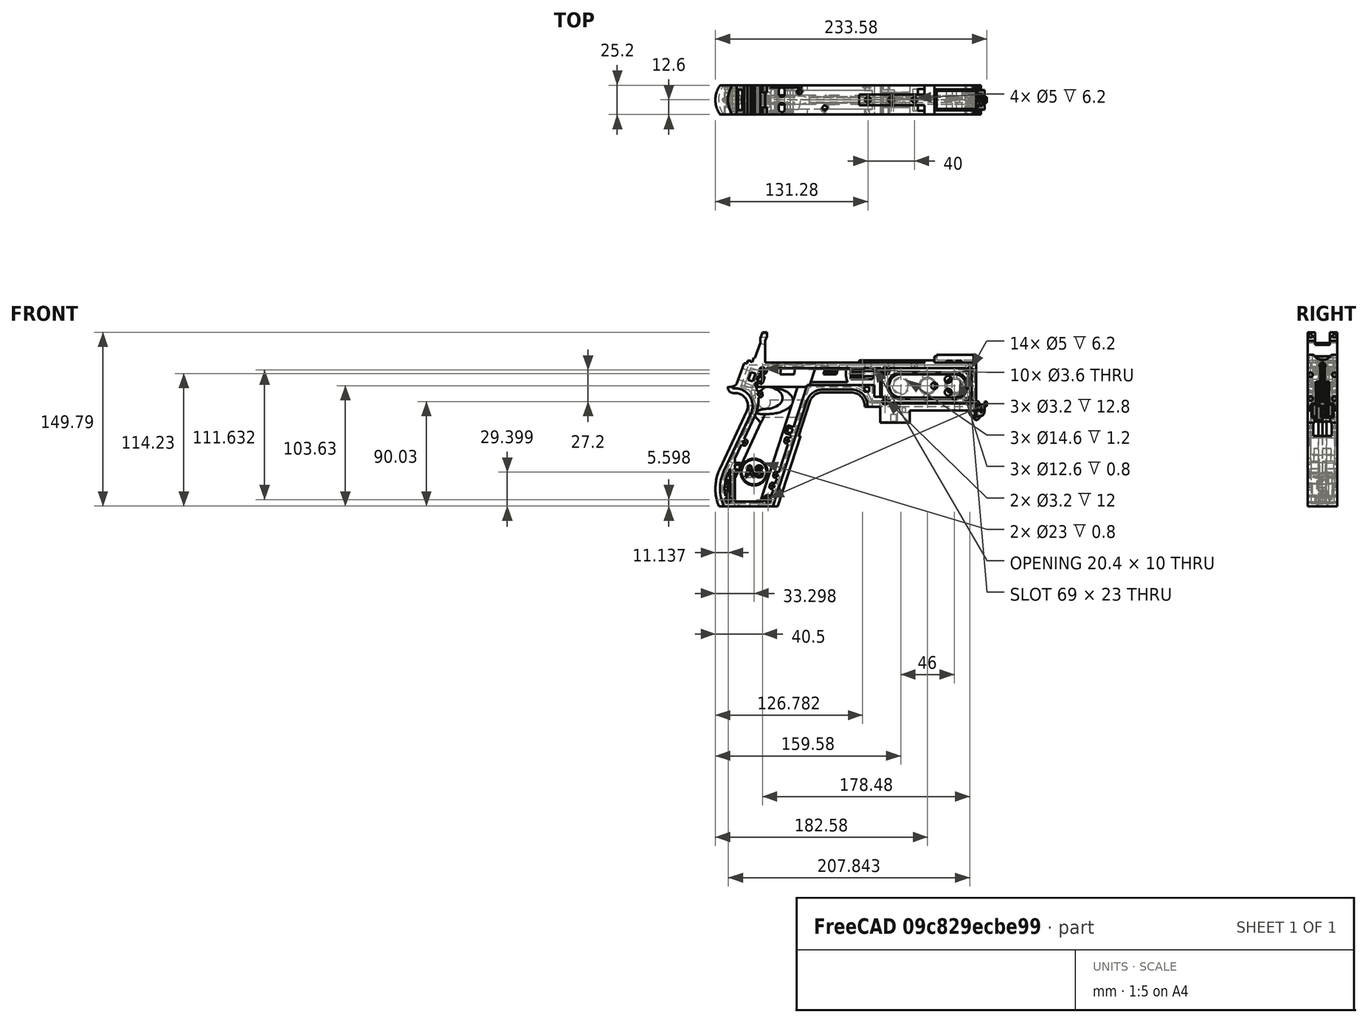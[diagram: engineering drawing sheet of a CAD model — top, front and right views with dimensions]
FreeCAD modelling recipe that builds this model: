
FCSTD DOCUMENT  (FreeCAD 1.0R39319 (Git))
Label: PICON-OF_ver_53_BIS
License: All rights reserved
LicenseURL: https://en.wikipedia.org/wiki/All_rights_reserved
objects: Sketcher::SketchObject×124, Part::Extrusion×63, Part::Cut×48, PartDesign::Pad×29, PartDesign::Pocket×21, PartDesign::Chamfer×15, PartDesign::Body×10, PartDesign::Fillet×6, Part::MultiFuse×5, Part::Part2DObjectPython×4, PartDesign::SubtractivePipe×4, PartDesign::SubtractiveLoft×4, PartDesign::Plane×3, PartDesign::SubShapeBinder×2, Part::Sweep×1, PartDesign::ShapeBinder×1, Mesh::Feature×1, PartDesign::Point×1, PartDesign::Groove×1
note: 626 computed .brp shape members not serialized (recipe doc carries the construction recipe); baked Part::Feature solids carry a one-line shape summary decoded from their .brp

FEATURE [Sketcher::SketchObject] Sketch  label="corpo principale"
  ArcFitTolerance = 1e-06
  AttacherType = Attacher::AttachEngine3D
  AttachmentSupport = -> [XZ_Plane]
  FullyConstrained = true
  MakeInternals = false
  MapMode = 5
  Placement = pos=(0,0,0) rot=(1,0,0;1.5708rad)
  sketch-geometry (65):
    g0: LineSegment StartX=0 StartY=0 StartZ=0 EndX=-57.2 EndY=0 EndZ=0
    g1: LineSegment StartX=-57.2 StartY=0 StartZ=0 EndX=-57.2 EndY=-10.4 EndZ=0
    g2: LineSegment StartX=-57.2 StartY=-10.4 StartZ=0 EndX=-82.8 EndY=-10.4 EndZ=0
    g3: LineSegment StartX=-82.8 StartY=-10.4 StartZ=0 EndX=-82.8 EndY=3.2 EndZ=0
    g4: LineSegment StartX=-82.8 StartY=3.2 StartZ=0 EndX=-93.6 EndY=3.2 EndZ=0
    g5: LineSegment StartX=-93.6 StartY=3.2 StartZ=0 EndX=-93.6 EndY=4 EndZ=0
    g6: LineSegment StartX=-107.6 StartY=18 StartZ=0 EndX=-132.428 EndY=18 EndZ=0
    g7: LineSegment StartX=-145.743 StartY=8.32624 StartZ=0 EndX=-175.232 EndY=-82.4316 EndZ=0
    g8: LineSegment StartX=-175.232 StartY=-82.4316 StartZ=0 EndX=-217.232 EndY=-82.4316 EndZ=0
    g9: LineSegment StartX=-217.232 StartY=-52.1862 StartZ=0 EndX=-193.988 EndY=-2.33927 EndZ=0
    g10: LineSegment StartX=-206.196 StartY=23.0857 StartZ=0 EndX=-199.861 EndY=40.4914 EndZ=0
    g11: LineSegment StartX=-199.861 StartY=40.4914 StartZ=0 EndX=-197.061 EndY=40.4914 EndZ=0
    g12: LineSegment StartX=-197.061 StartY=40.4914 StartZ=0 EndX=-197.061 EndY=42.8914 EndZ=0
    g13: LineSegment StartX=-197.061 StartY=42.8914 StartZ=0 EndX=-194.261 EndY=42.8914 EndZ=0
    g14: LineSegment StartX=-194.261 StartY=42.8914 StartZ=0 EndX=-194.535 EndY=42.1397 EndZ=0
    g15: LineSegment StartX=-194.535 StartY=42.1397 StartZ=0 EndX=-193.031 EndY=41.5924 EndZ=0
    g16: LineSegment StartX=-193.031 StartY=41.5924 StartZ=0 EndX=-191.663 EndY=45.3512 EndZ=0
    g17: LineSegment StartX=-191.663 StartY=45.3512 StartZ=0 EndX=-190.536 EndY=44.9408 EndZ=0
    g18: LineSegment StartX=-190.536 StartY=44.9408 StartZ=0 EndX=-185.747 EndY=58.0965 EndZ=0
    g19: LineSegment StartX=-185.747 StartY=58.0965 StartZ=0 EndX=-185.747 EndY=62.0965 EndZ=0
    g20: LineSegment StartX=-185.747 StartY=62.0965 StartZ=0 EndX=-183.832 EndY=67.3588 EndZ=0
    g21: LineSegment StartX=-183.832 StartY=67.3588 StartZ=0 EndX=-180.232 EndY=67.3588 EndZ=0
    g22: LineSegment StartX=-180.232 StartY=67.3588 StartZ=0 EndX=-180.232 EndY=63.7588 EndZ=0
    g23: LineSegment StartX=-180.232 StartY=63.7588 StartZ=0 EndX=-181.6 EndY=60 EndZ=0
    g24: LineSegment StartX=-181.6 StartY=60 StartZ=0 EndX=-181.6 EndY=41.2 EndZ=0
    g25: LineSegment StartX=-181.6 StartY=41.2 StartZ=0 EndX=-100.8 EndY=41.2 EndZ=0
    g26: LineSegment StartX=-36 StartY=43.2 StartZ=0 EndX=-36 EndY=41.2 EndZ=0
    g27: LineSegment StartX=0 StartY=48 StartZ=0 EndX=0 EndY=0 EndZ=0
    g28: LineSegment StartX=-209.901 StartY=19.85 StartZ=0 EndX=-209.901 EndY=20.1 EndZ=0
    g29: LineSegment StartX=-208.001 StartY=22 StartZ=0 EndX=-207.747 EndY=22 EndZ=0
    g30: LineSegment StartX=-207.583 StartY=19 StartZ=0 EndX=-209.051 EndY=19 EndZ=0
    g31: ArcOfCircle CenterX=-208.001 CenterY=20.1 CenterZ=0 NormalX=0 NormalY=0 NormalZ=1 AngleXU=0 Radius=1.9 StartAngle=1.5708 EndAngle=3.14159
    g32: GeomPoint [constr] X=-209.901 Y=22 Z=0
    g33: ArcOfCircle CenterX=-209.051 CenterY=19.85 CenterZ=0 NormalX=0 NormalY=0 NormalZ=1 AngleXU=0 Radius=0.85 StartAngle=3.14159 EndAngle=4.71239
    g34: GeomPoint [constr] X=-209.901 Y=19 Z=0
    g35: ArcOfCircle CenterX=-207.747 CenterY=23.65 CenterZ=0 NormalX=0 NormalY=0 NormalZ=1 AngleXU=0 Radius=1.65 StartAngle=4.71239 EndAngle=5.93412
    g36: GeomPoint [constr] X=-206.591 Y=22 Z=0
    g37: LineSegment StartX=-4 StartY=6 StartZ=0 EndX=-4 EndY=36.4 EndZ=0
    g38: LineSegment StartX=-4 StartY=36.4 StartZ=0 EndX=-185.2 EndY=36.4 EndZ=0
    g39: LineSegment StartX=-185.2 StartY=36.4 StartZ=0 EndX=-190.441 EndY=22 EndZ=0
    g40: LineSegment StartX=-214.575 StartY=-78.4316 StartZ=0 EndX=-178.142 EndY=-78.4316 EndZ=0
    g41: LineSegment StartX=-178.142 StartY=-78.4316 StartZ=0 EndX=-145.51 EndY=22 EndZ=0
    g42: LineSegment StartX=-145.51 StartY=22 StartZ=0 EndX=-87.91 EndY=22 EndZ=0
    g43: LineSegment StartX=-87.91 StartY=22 StartZ=0 EndX=-87.91 EndY=11.6 EndZ=0
    g44: LineSegment StartX=-87.91 StartY=11.6 StartZ=0 EndX=-80.11 EndY=11.6 EndZ=0
    g45: LineSegment StartX=-80.11 StartY=11.6 StartZ=0 EndX=-80.11 EndY=6 EndZ=0
    g46: LineSegment StartX=-80.11 StartY=6 StartZ=0 EndX=-4 EndY=6 EndZ=0
    g47: LineSegment StartX=-190.363 StartY=-4.02975 StartZ=0 EndX=-213.607 EndY=-53.8767 EndZ=0
    g48: ArcOfCircle CenterX=-132.428 CenterY=4 CenterZ=0 NormalX=0 NormalY=0 NormalZ=1 AngleXU=0 Radius=14 StartAngle=1.5708 EndAngle=2.82743
    g49: GeomPoint [constr] X=-142.6 Y=18 Z=0
    g50: ArcOfCircle CenterX=-107.6 CenterY=4 CenterZ=0 NormalX=0 NormalY=0 NormalZ=1 AngleXU=0 Radius=14 StartAngle=0 EndAngle=1.5708
    g51: GeomPoint [constr] X=-93.6 Y=18 Z=0
    g52: ArcOfCircle CenterX=-184.801 CenterY=-67.3089 CenterZ=0 NormalX=0 NormalY=0 NormalZ=1 AngleXU=0 Radius=35.7833 StartAngle=2.70526 EndAngle=3.57792
    g53: ArcOfCircle CenterX=-207.583 CenterY=4 CenterZ=0 NormalX=0 NormalY=0 NormalZ=1 AngleXU=0 Radius=15 StartAngle=5.84685 EndAngle=7.85398
    g54: LineSegment [constr] StartX=-213.607 StartY=-53.8767 StartZ=0 EndX=-217.232 EndY=-52.1862 EndZ=0
    g55: ArcOfCircle CenterX=-184.801 CenterY=-67.3089 CenterZ=0 NormalX=0 NormalY=0 NormalZ=1 AngleXU=0 Radius=31.7833 StartAngle=2.70526 EndAngle=3.49911
    g56: ArcOfCircle CenterX=-218.095 CenterY=8.90192 CenterZ=0 NormalX=0 NormalY=0 NormalZ=1 AngleXU=0 Radius=30.5989 StartAngle=5.84685 EndAngle=6.72553
    g57: LineSegment StartX=-44.6 StartY=43.2 StartZ=0 EndX=-36 EndY=43.2 EndZ=0
    g58: LineSegment StartX=-100.8 StartY=41.2 StartZ=0 EndX=-44.6 EndY=41.2 EndZ=0
    g59: LineSegment StartX=-44.6 StartY=41.2 StartZ=0 EndX=-44.6 EndY=43.2 EndZ=0
    g60: LineSegment StartX=-2.4 StartY=48 StartZ=0 EndX=0 EndY=48 EndZ=0
    g61: LineSegment StartX=-36 StartY=41.2 StartZ=0 EndX=-2.4 EndY=41.2 EndZ=0
    g62: LineSegment StartX=-2.4 StartY=41.2 StartZ=0 EndX=-2.4 EndY=48 EndZ=0
    g63: LineSegment [constr] StartX=-181.6 StartY=36.4 StartZ=0 EndX=-152.209 EndY=36.4 EndZ=0
    g64: LineSegment [constr] StartX=-181.6 StartY=36.4 StartZ=0 EndX=-130.41 EndY=36.4 EndZ=0
  constraints (183):
    c: Coincident(g-1,g0)
    c: PointOnObject(g0,g-1)
    c: Coincident(g0,g1)
    c: Vertical(g1)
    c: Coincident(g1,g2)
    c: Horizontal(g2)
    c: Coincident(g2,g3)
    c: Vertical(g3)
    c: Coincident(g3,g4)
    c: Coincident(g4,g5)
    c: Vertical(g5)
    c: Horizontal(g6)
    c: Coincident(g7,g8)
    c: Horizontal(g8)
    c: Coincident(g10,g11)
    c: Horizontal(g11)
    c: Coincident(g11,g12)
    c: Vertical(g12)
    c: Coincident(g12,g13)
    c: Horizontal(g13)
    c: Coincident(g13,g14)
    c: Coincident(g14,g15)
    c: Coincident(g15,g16)
    c: Coincident(g16,g17)
    c: Coincident(g17,g18)
    c: Coincident(g18,g19)
    c: Vertical(g19)
    c: Coincident(g19,g20)
    c: Coincident(g20,g21)
    c: Horizontal(g21)
    c: Coincident(g21,g22)
    c: Vertical(g22)
    c: Coincident(g22,g23)
    c: Coincident(g23,g24)
    c: Vertical(g24)
    c: Coincident(g24,g25)
    c: Horizontal(g25)
    c: Coincident(g57,g26)
    c: Vertical(g26)
    c: Coincident(g26,g61)
    c: PointOnObject(g60,g-2)
    c: Coincident(g60,g27)
    c: Coincident(g27,g0)
    c: DistanceY(g27,g27) = 48
    c: DistanceY(g1,g1) = 10.4
    c: DistanceX(g0,g0) = 57.2
    c: DistanceX(g2,g2) = 25.6
    c: Horizontal(g4)
    c: DistanceY(g3,g3) = 13.6
    c: DistanceX(g4,g4) = 10.8
    c: DistanceY(g5,g51) = 14.8
    c: DistanceX(g49,g51) = 49
    c: Distance(g7,g49) = 105.6
    c: DistanceX(g61,g60) = 36
    c: DistanceX(g25,g25) = 80.8
    c: DistanceY(g24,g24) = 18.8
    c: DistanceY(g22,g22) = 3.6
    c: Distance(g23) = 4
    c: Angle(g-1,g23) = 1.22173
    c: DistanceX(g21,g21) = 3.6
    c: Distance(g20) = 5.6
    c: Angle(g-1,g20) = 1.22173
    c: DistanceY(g19,g19) = 4
    c: Distance(g18) = 14
    c: Angle(g-1,g18) = 1.22173
    c: Distance(g17) = 1.2
    c: Distance(g16) = 4
    c: Angle(g16) = 1.22173
    c: Perpendicular(g18,g17)
    c: Distance(g15) = 1.6
    c: Perpendicular(g16,g15)
    c: Distance(g14) = 0.8
    c: DistanceX(g13,g13) = 2.8
    c: Perpendicular(g15,g14)
    c: DistanceY(g12,g12) = 2.4
    c: DistanceX(g11,g11) = 2.8
    c: Distance(g9) = 55
    c: Angle(g9,g-1) = 2.00713
    c: Horizontal(g29)
    c: Vertical(g28)
    c: Horizontal(g30)
    c: PointOnObject(g32,g29)
    c: PointOnObject(g32,g28)
    c: Tangent(g29,g31) = 1.5708
    c: Tangent(g28,g31) = 1.5708
    c: PointOnObject(g34,g28)
    c: PointOnObject(g34,g30)
    c: Tangent(g28,g33) = 1.5708
    c: Tangent(g30,g33) = 1.5708
    c: PointOnObject(g36,g29)
    c: PointOnObject(g36,g10)
    c: Tangent(g29,g35) = -1.5708
    c: Tangent(g10,g35) = -1.5708
    c: Angle(g-1,g10) = 1.22173
    c: Radius(g35) = 1.65
    c: Vertical(g37)
    c: Coincident(g37,g38)
    c: Horizontal(g38)
    c: Coincident(g38,g39)
    c: Horizontal(g40)
    c: Coincident(g40,g41)
    c: Coincident(g41,g42)
    c: Horizontal(g42)
    c: Coincident(g42,g43)
    c: Vertical(g43)
    c: Coincident(g43,g44)
    c: Horizontal(g44)
    c: Coincident(g44,g45)
    c: Vertical(g45)
    c: Coincident(g45,g46)
    c: Coincident(g46,g37)
    c: Horizontal(g46)
    c: DistanceY(g0,g37) = 6
    c: DistanceX(g37,g0) = 4
    c: DistanceY(g37,g25) = 4.8
    c: DistanceX(g38,g38) = 181.2
    c: DistanceX(g42,g42) = 57.6
    c: DistanceY(g49,g41) = 4
    c: DistanceX(g41,g49) = 2.91
    c: DistanceY(g43,g43) = 10.4
    c: DistanceX(g44,g44) = 7.8
    c: DistanceY(g7,g40) = 4
    c: Distance(g47) = 55
    c: Angle(g-1,g39) = 1.22173
    c: PointOnObject(g49,g7)
    c: PointOnObject(g49,g6)
    c: Tangent(g7,g48) = -1.5708
    c: Tangent(g6,g48) = -1.5708
    c: PointOnObject(g51,g5)
    c: PointOnObject(g51,g6)
    c: Tangent(g5,g50) = -1.5708
    c: Tangent(g6,g50) = -1.5708
    c: Radius(g50) = 14
    c: Radius(g48) = 14
    c: DistanceX(g8,g8) = 42
    c: Angle(g7,g-1) = 1.88496
    c: Parallel(g41,g7)
    c: Parallel(g47,g9)
    c: Coincident(g52,g8)
    c: Tangent(g52,g9) = 1.5708
    c: DistanceX(g9,g8) = 0
    c: Tangent(g53,g9) = -1.5708
    c: Tangent(g53,g30) = -1.5708
    c: Diameter(g53) = 30
    c: DistanceY(g53,g0) = -4
    c: Coincident(g54,g47)
    c: Distance(g54) = 4
    c: Coincident(g54,g9)
    c: Coincident(g55,g40)
    c: Tangent(g55,g47) = -1.5708
    c: Coincident(g52,g55)
    c: Coincident(g56,g39)
    c: Tangent(g56,g47) = 1.5708
    c: Horizontal(g57)
    c: DistanceX(g57,g57) = 8.6
    c: Coincident(g58,g25)
    c: Horizontal(g58)
    c: Coincident(g59,g58)
    c: Vertical(g59)
    c: DistanceY(g58,g57) = 2
    c: DistanceX(g58,g58) = 56.2
    c: Coincident(g59,g57)
    c: DistanceY(g41,g36) = 0
    c: DistanceY(g36,g39) = 0
    c: DistanceY(g28,g28) = 0.25
    c: DistanceX(g30,g36) = 2.46
    c: DistanceX(g28,g29) = 1.9
    c: Coincident(g62,g60)
    c: Horizontal(g60)
    c: DistanceX(g62,g27) = 2.4
    c: Coincident(g61,g62)
    c: DistanceY(g26,g26) = 2
    c: Vertical(g62)
    c: DistanceY(g61,g60) = 6.8
    c: Horizontal(g61)
    c: Distance(g63) = 29.391
    c: PointOnObject(g63,g38)
    c: PointOnObject(g63,g38)
    c: Distance(g64) = 51.19
    c: PointOnObject(g64,g38)
    c: PointOnObject(g64,g38)
    c: DistanceX(g24,g63) = 0
    c: DistanceX(g24,g64) = 0
FEATURE [Part::Extrusion] Extrude  label="Extrude corpo principale"
  Base = -> Sketch
  Dir = (0,-1,2e-16)
  DirMode = 2
  FaceMakerClass = Part::FaceMakerBullseye
  FaceMakerMode = 3
  LengthFwd = 25.2
  LengthRev = 12.6
  Solid = true
  Symmetric = true
FEATURE [Sketcher::SketchObject] Sketch002  label="scavo grilletto"
  ArcFitTolerance = 1e-06
  AttachmentSupport = -> [XZ_Plane]
  ExternalGeometry = -> [Sketch]
  FullyConstrained = true
  MakeInternals = false
  MapMode = 5
  Placement = pos=(0,0,0) rot=(1,0,0;1.5708rad)
  sketch-geometry (4):
    g0: LineSegment StartX=-89.51 StartY=22 StartZ=0 EndX=-152.71 EndY=22 EndZ=0
    g1: LineSegment StartX=-152.71 StartY=22 StartZ=0 EndX=-167.006 EndY=-22 EndZ=0
    g2: LineSegment StartX=-167.006 StartY=-22 StartZ=0 EndX=-89.51 EndY=-22 EndZ=0
    g3: LineSegment StartX=-89.51 StartY=-22 StartZ=0 EndX=-89.51 EndY=22 EndZ=0
  constraints (12):
    c: Horizontal(g0)
    c: Coincident(g0,g1)
    c: Coincident(g1,g2)
    c: Horizontal(g2)
    c: Coincident(g2,g3)
    c: Coincident(g3,g0)
    c: Vertical(g3)
    c: Angle(g1,g0) = 1.88496
    c: DistanceY(g3,g3) = 44
    c: DistanceX(g0,g0) = 63.2
    c: DistanceX(g0,g-3) = 1.6
    c: DistanceY(g-3,g0) = 0
FEATURE [Sketcher::SketchObject] Sketch004  label="traiettoria arrotondamento impugnatura anteriore"
  ArcFitTolerance = 1e-06
  AttachmentSupport = -> [XZ_Plane]
  ExternalGeometry = -> [Sketch]
  FullyConstrained = true
  MakeInternals = false
  MapMode = 5
  Placement = pos=(0,0,0) rot=(1,0,0;1.5708rad)
  sketch-geometry (13):
    g0: LineSegment StartX=-175.232 StartY=-82.4316 StartZ=0 EndX=-145.743 EndY=8.32624 EndZ=0
    g1: LineSegment StartX=-93.6 StartY=3.2 StartZ=0 EndX=-93.6 EndY=4 EndZ=0
    g2: LineSegment StartX=-132.428 StartY=18 StartZ=0 EndX=-107.6 EndY=18 EndZ=0
    g3: ArcOfCircle CenterX=-132.428 CenterY=4 CenterZ=0 NormalX=0 NormalY=0 NormalZ=1 AngleXU=0 Radius=14 StartAngle=1.5708 EndAngle=2.82743
    g4: ArcOfCircle CenterX=-107.6 CenterY=4 CenterZ=0 NormalX=0 NormalY=0 NormalZ=1 AngleXU=0 Radius=14 StartAngle=0 EndAngle=1.5708
    g5: LineSegment StartX=-175.232 StartY=-82.4316 StartZ=0 EndX=-217.232 EndY=-82.4316 EndZ=0
    g6: LineSegment StartX=-217.232 StartY=-52.1862 StartZ=0 EndX=-193.988 EndY=-2.33927 EndZ=0
    g7: LineSegment StartX=-209.051 StartY=19 StartZ=0 EndX=-207.583 EndY=19 EndZ=0
    g8: LineSegment StartX=-209.901 StartY=20.1 StartZ=0 EndX=-209.901 EndY=19.85 EndZ=0
    g9: ArcOfCircle CenterX=-184.801 CenterY=-67.3089 CenterZ=0 NormalX=0 NormalY=0 NormalZ=1 AngleXU=0 Radius=35.7833 StartAngle=2.70526 EndAngle=3.57792
    g10: ArcOfCircle CenterX=-207.583 CenterY=4 CenterZ=0 NormalX=0 NormalY=0 NormalZ=1 AngleXU=0 Radius=15 StartAngle=5.84685 EndAngle=7.85398
    g11: ArcOfCircle CenterX=-209.051 CenterY=19.85 CenterZ=0 NormalX=0 NormalY=0 NormalZ=1 AngleXU=0 Radius=0.85 StartAngle=3.14159 EndAngle=4.71239
    g12: ArcOfCircle CenterX=-208.001 CenterY=20.1 CenterZ=0 NormalX=0 NormalY=0 NormalZ=1 AngleXU=0 Radius=1.9 StartAngle=1.5708 EndAngle=3.14159
  constraints (26):
    c: Coincident(g0,g-3)
    c: Coincident(g0,g-6)
    c: Coincident(g1,g-8)
    c: Coincident(g1,g-7)
    c: Coincident(g2,g-5)
    c: Coincident(g2,g-4)
    c: Coincident(g3,g2)
    c: Tangent(g3,g0) = 1.5708
    c: Coincident(g4,g1)
    c: Tangent(g4,g2) = 1.5708
    c: Coincident(g5,g0)
    c: Coincident(g5,g-9)
    c: Coincident(g6,g-12)
    c: Coincident(g6,g-11)
    c: Coincident(g7,g-15)
    c: Coincident(g7,g-14)
    c: Coincident(g8,g-16)
    c: Coincident(g8,g-17)
    c: Tangent(g9,g6) = 1.5708
    c: Coincident(g9,g5)
    c: Coincident(g10,g7)
    c: Tangent(g10,g6) = -1.5708
    c: Tangent(g11,g7) = -1.5708
    c: Coincident(g11,g8)
    c: Tangent(g12,g8) = -1.5708
    c: Coincident(g12,g-17)
FEATURE [PartDesign::Plane] DatumPlane  label="Piano per disegno arrotondamento impugnatura"
  AttachmentSupport = -> [Sketch]
  Length = 73.6581
  MapMode = 7
  Placement = pos=(-145.743,1.8e-15,8.32624) rot=(0.154555,0.154555,0.97582;1.59527rad)
  ResizeMode = 0
  Width = 303.511
FEATURE [Sketcher::SketchObject] Sketch005  label="forma arrotondamento impugnatura anteriore"
  ArcFitTolerance = 1e-06
  AttachmentSupport = -> [DatumPlane]
  FullyConstrained = true
  MakeInternals = false
  MapMode = 5
  Placement = pos=(-145.743,1.8e-15,8.32624) rot=(0.154555,0.154555,0.97582;1.59527rad)
  sketch-geometry (5):
    g0: GeomPoint [constr] X=0 Y=-4 Z=0
    g1: GeomPoint [constr] X=-12.6 Y=7.1e-15 Z=0
    g2: GeomPoint [constr] X=12.6 Y=4.97e-14 Z=0
    g3: LineSegment StartX=-12.6 StartY=7.1e-15 StartZ=0 EndX=12.6 EndY=4.97e-14 EndZ=0
    g4: ArcOfCircle CenterX=-3.88e-14 CenterY=17.845 CenterZ=0 NormalX=0 NormalY=0 NormalZ=1 AngleXU=0 Radius=21.845 StartAngle=4.09759 EndAngle=5.32718
  constraints (11):
    c: DistanceY(g0,g-1) = 4
    c: DistanceX(g-1,g0) = 0
    c: DistanceX(g1,g-1) = 12.6
    c: DistanceX(g-1,g2) = 12.6
    c: DistanceY(g-1,g2) = 0
    c: DistanceY(g-1,g1) = 0
    c: Coincident(g3,g1)
    c: Coincident(g3,g2)
    c: Coincident(g4,g1)
    c: Coincident(g4,g2)
    c: PointOnObject(g0,g4)
FEATURE [Part::Sweep] Sweep  label="Sweep impugnatura"
  Frenet = true
  Sections = -> [Sketch005]
  Solid = true
  Spine = -> Sketch [Edge32,Edge33,Edge34,Edge35,Edge36,Edge37,Edge38,Edge39,Edge40,Edge41,Edge42,Edge43,Edge44]
  Transition = 1
FEATURE [Sketcher::SketchObject] Sketch008  label="buchi e pulizie varie"
  ArcFitTolerance = 1e-06
  AttachmentSupport = -> [XZ_Plane]
  ExternalGeometry = -> [Sketch]
  FullyConstrained = true
  MakeInternals = false
  MapMode = 5
  Placement = pos=(0,0,0) rot=(1,0,0;1.5708rad)
  sketch-geometry (26):
    g0: LineSegment StartX=-96.278 StartY=20.155 StartZ=0 EndX=-92.278 EndY=20.155 EndZ=0
    g1: LineSegment StartX=-92.278 StartY=20.155 StartZ=0 EndX=-92.278 EndY=16.155 EndZ=0
    g2: LineSegment StartX=-92.278 StartY=16.155 StartZ=0 EndX=-96.278 EndY=16.155 EndZ=0
    g3: LineSegment StartX=-96.278 StartY=16.155 StartZ=0 EndX=-96.278 EndY=20.155 EndZ=0
    g4: LineSegment StartX=-222.232 StartY=-82.4316 StartZ=0 EndX=-170.232 EndY=-82.4316 EndZ=0
    g5: LineSegment StartX=-170.232 StartY=-82.4316 StartZ=0 EndX=-170.232 EndY=-86.4316 EndZ=0
    g6: LineSegment StartX=-170.232 StartY=-86.4316 StartZ=0 EndX=-222.232 EndY=-86.4316 EndZ=0
    g7: LineSegment StartX=-222.232 StartY=-86.4316 StartZ=0 EndX=-222.232 EndY=-82.4316 EndZ=0
    g8: LineSegment StartX=-213.901 StartY=20.1 StartZ=0 EndX=-213.901 EndY=26 EndZ=0
    g9: LineSegment StartX=-213.901 StartY=26 StartZ=0 EndX=-206.196 EndY=26 EndZ=0
    g10: LineSegment StartX=-17.4 StartY=42.8 StartZ=0 EndX=-12.4 EndY=42.8 EndZ=0
    g11: LineSegment StartX=-12.4 StartY=42.8 StartZ=0 EndX=-12.4 EndY=41.2 EndZ=0
    g12: LineSegment StartX=-12.4 StartY=41.2 StartZ=0 EndX=-17.4 EndY=41.2 EndZ=0
    g13: LineSegment StartX=-17.4 StartY=41.2 StartZ=0 EndX=-17.4 EndY=42.8 EndZ=0
    g14: LineSegment StartX=-25.9 StartY=42.8 StartZ=0 EndX=-20.9 EndY=42.8 EndZ=0
    g15: LineSegment StartX=-20.9 StartY=42.8 StartZ=0 EndX=-20.9 EndY=41.2 EndZ=0
    g16: LineSegment StartX=-20.9 StartY=41.2 StartZ=0 EndX=-25.9 EndY=41.2 EndZ=0
    g17: LineSegment StartX=-25.9 StartY=41.2 StartZ=0 EndX=-25.9 EndY=42.8 EndZ=0
    g18: GeomPoint [constr] X=-206.196 Y=23.0857 Z=0
    g19: GeomPoint [constr] X=-213.901 Y=20.1 Z=0
    g20: BSplineCurve PolesCount=4 KnotsCount=2 Degree=3 IsPeriodic=0
    g21-g24: Circle [constr] x4 (B-spline internal-alignment scaffolding for g20; pole/knot coordinates omitted)
    g25: LineSegment StartX=-206.196 StartY=26 StartZ=0 EndX=-206.196 EndY=23.0857 EndZ=0
  constraints (73):
    c: Horizontal(g0)
    c: Coincident(g1,g0)
    c: Vertical(g1)
    c: Coincident(g2,g1)
    c: Horizontal(g2)
    c: Coincident(g3,g2)
    c: Coincident(g3,g0)
    c: Vertical(g3)
    c: DistanceX(g0,g-4) = 4.368
    c: DistanceY(g0,g-4) = 1.845
    c: DistanceY(g1,g1) = 4
    c: DistanceX(g2,g2) = 4
    c: Horizontal(g4)
    c: Coincident(g5,g4)
    c: Vertical(g5)
    c: Coincident(g6,g5)
    c: Horizontal(g6)
    c: Coincident(g7,g6)
    c: Coincident(g7,g4)
    c: Vertical(g7)
    c: DistanceY(g7,g7) = 4
    c: DistanceX(g4,g-5) = 5
    c: DistanceX(g-5,g4) = 5
    c: DistanceY(g4,g-5) = 0
    c: Coincident(g9,g8)
    c: Parallel(g9,g-6)
    c: DistanceX(g8,g-8) = 4
    c: Horizontal(g10)
    c: Coincident(g11,g10)
    c: Vertical(g11)
    c: Coincident(g12,g11)
    c: Horizontal(g12)
    c: Coincident(g13,g12)
    c: Coincident(g13,g10)
    c: Vertical(g13)
    c: Horizontal(g14)
    c: Coincident(g15,g14)
    c: Vertical(g15)
    c: Coincident(g16,g15)
    c: Horizontal(g16)
    c: Coincident(g17,g16)
    c: Coincident(g17,g14)
    c: Vertical(g17)
    c: DistanceY(g11,g10) = 1.6
    c: DistanceX(g10,g10) = 5
    c: DistanceY(g15,g14) = 1.6
    c: DistanceX(g14,g14) = 5
    c: DistanceX(g15,g12) = 3.5
    c: DistanceX(g11,g-9) = 10
    c: DistanceY(g-9,g11) = 0
    c: DistanceY(g-9,g15) = 0
    c: Perpendicular(g8,g9)
    c: DistanceY(g-7,g9) = 4
    c: DistanceY(g8,g-8) = 0
    c: InternalAlignment(g18,g20)
    c: InternalAlignment(g19,g20)
    c: InternalAlignment(g21,g20)
    c: Weight(g21) = 1
    c: InternalAlignment(g22,g20)
    c: Equal(g22,g21)
    c: InternalAlignment(g23,g20)
    c: Equal(g23,g21)
    c: InternalAlignment(g24,g20)
    c: Equal(g24,g21)
    c: Coincident(g18,g-12)
    c: Coincident(g19,g8)
    c: Coincident(g25,g9)
    c: Coincident(g25,g20)
    c: Vertical(g25)
    c: DistanceY(g20,g23) = 0
    c: DistanceY(g22,g18) = 2.26
    c: DistanceX(g22,g18) = 0.93
    c: DistanceX(g20,g23) = 2.9
FEATURE [Part::Extrusion] Extrude004  label="Extrude Buchi e pulizie varie"
  Base = -> Sketch008
  Dir = (0,-1,2e-16)
  DirMode = 2
  FaceMakerClass = Part::FaceMakerBullseye
  FaceMakerMode = 3
  LengthFwd = 25.2
  LengthRev = 0
  Solid = true
  Symmetric = true
FEATURE [Sketcher::SketchObject] Sketch009  label="rinforzi"
  ArcFitTolerance = 1e-06
  AttachmentSupport = -> [XZ_Plane]
  ExternalGeometry = -> [Sketch]
  FullyConstrained = true
  MakeInternals = false
  MapMode = 5
  Placement = pos=(0,0,0) rot=(1,0,0;1.5708rad)
  sketch-geometry (9):
    g0: LineSegment StartX=-87.91 StartY=22 StartZ=0 EndX=-87.91 EndY=36.4 EndZ=0
    g1: LineSegment StartX=-87.91 StartY=36.4 StartZ=0 EndX=-97.91 EndY=36.4 EndZ=0
    g2: LineSegment StartX=-97.91 StartY=36.4 StartZ=0 EndX=-97.91 EndY=22 EndZ=0
    g3: LineSegment StartX=-97.91 StartY=22 StartZ=0 EndX=-87.91 EndY=22 EndZ=0
    g4: LineSegment StartX=-149.713 StartY=9.06563 StartZ=0 EndX=-154.586 EndY=-5.93437 EndZ=0
    g5: LineSegment StartX=-154.586 StartY=-5.93437 StartZ=0 EndX=-191.863 EndY=-5.93437 EndZ=0
    g6: LineSegment StartX=-191.863 StartY=-5.93437 StartZ=0 EndX=-191.863 EndY=9.06563 EndZ=0
    g7: LineSegment StartX=-191.863 StartY=9.06563 StartZ=0 EndX=-149.713 EndY=9.06563 EndZ=0
    g8: LineSegment [constr] StartX=-145.51 StartY=22 StartZ=0 EndX=-149.713 EndY=9.06563 EndZ=0
  constraints (25):
    c: Vertical(g0)
    c: Coincident(g1,g0)
    c: Horizontal(g1)
    c: Coincident(g2,g1)
    c: Vertical(g2)
    c: Coincident(g3,g2)
    c: Coincident(g3,g0)
    c: Horizontal(g3)
    c: Coincident(g0,g-4)
    c: DistanceX(g3,g3) = 10
    c: DistanceY(g0,g-3) = 0
    c: Coincident(g5,g4)
    c: Horizontal(g5)
    c: Coincident(g6,g5)
    c: Vertical(g6)
    c: Coincident(g7,g6)
    c: Coincident(g7,g4)
    c: Horizontal(g7)
    c: Distance(g8) = 13.6
    c: Parallel(g-6,g8)
    c: Coincident(g-6,g8)
    c: Parallel(g4,g-6)
    c: DistanceY(g4,g4) = 15
    c: Coincident(g4,g8)
    c: DistanceX(g-5,g5) = -1.5
FEATURE [Part::Extrusion] Extrude001  label="Extrude scavo grilletto"
  Base = -> Sketch002
  Dir = (0,-1,2e-16)
  DirMode = 2
  FaceMakerClass = Part::FaceMakerBullseye
  FaceMakerMode = 3
  LengthFwd = 16
  LengthRev = 0
  Solid = true
  Symmetric = true
FEATURE [Part::Extrusion] Extrude005  label="Extrude Rinforzi"
  Base = -> Sketch009
  Dir = (0,-1,2e-16)
  DirMode = 2
  FaceMakerClass = Part::FaceMakerBullseye
  FaceMakerMode = 3
  LengthFwd = 2
  LengthRev = 0
  Placement = pos=(0,12.6,0) rot=(0,0,1;0rad)
  Solid = true
  Symmetric = false
FEATURE [PartDesign::ShapeBinder] CopyCut
  TraceSupport = false
FEATURE [PartDesign::Plane] DatumPlane001
  AttachmentSupport = -> [CopyCut]
  Length = 283.944
  MapMode = 5
  Placement = pos=(0,12.6,0) rot=(0,0.707107,0.707107;3.14159rad)
  ResizeMode = 0
  Width = 188.15
FEATURE [Sketcher::SketchObject] Sketch010  label="buco neopixel"
  ArcFitTolerance = 1e-06
  AttachmentSupport = -> [XZ_Plane]
  ExternalGeometry = -> [Sketch]
  FullyConstrained = true
  MakeInternals = false
  MapMode = 5
  Placement = pos=(0,0,0) rot=(1,0,0;1.5708rad)
  sketch-geometry (5):
    g0: LineSegment [constr] StartX=-199.861 StartY=40.4914 StartZ=0 EndX=-201.368 EndY=36.3521 EndZ=0
    g1: LineSegment StartX=-201.368 StartY=36.3521 StartZ=0 EndX=-204.932 EndY=26.5605 EndZ=0
    g2: LineSegment StartX=-201.368 StartY=36.3521 StartZ=0 EndX=-180.2 EndY=28.6477 EndZ=0
    g3: LineSegment StartX=-180.2 StartY=28.6477 StartZ=0 EndX=-183.764 EndY=18.8561 EndZ=0
    g4: LineSegment StartX=-183.764 StartY=18.8561 StartZ=0 EndX=-204.932 EndY=26.5605 EndZ=0
  constraints (14):
    c: Parallel(g0,g-3)
    c: Distance(g0) = 4.405
    c: Coincident(g0,g-3)
    c: Coincident(g2,g1)
    c: Coincident(g3,g2)
    c: Coincident(g4,g3)
    c: Coincident(g4,g1)
    c: Parallel(g1,g-3)
    c: Distance(g1) = 10.42
    c: Coincident(g1,g0)
    c: Parallel(g2,g4)
    c: Perpendicular(g1,g2)
    c: DistanceX(g-4,g2) = 5
    c: Parallel(g3,g1)
FEATURE [Part::Extrusion] Extrude006  label="Extrude buco neopixel"
  Base = -> Sketch010
  Dir = (0,-1,2e-16)
  DirMode = 2
  FaceMakerClass = Part::FaceMakerBullseye
  FaceMakerMode = 3
  LengthFwd = 17.2
  LengthRev = 0
  Solid = true
  Symmetric = true
FEATURE [Sketcher::SketchObject] Sketch011  label="fermo grilletto"
  ArcFitTolerance = 1e-06
  AttachmentSupport = -> [XZ_Plane]
  ExternalGeometry = -> [Sketch]
  FullyConstrained = true
  MakeInternals = false
  MapMode = 5
  Placement = pos=(0,0,0) rot=(1,0,0;1.5708rad)
  sketch-geometry (18):
    g0: LineSegment [constr] StartX=-145.51 StartY=22 StartZ=0 EndX=-157.347 EndY=-14.4293 EndZ=0
    g1: LineSegment [constr] StartX=-157.347 StartY=-14.4293 StartZ=0 EndX=-157.841 EndY=-15.951 EndZ=0
    g2: LineSegment StartX=-161.151 StartY=-13.1932 StartZ=0 EndX=-155.825 EndY=-14.9237 EndZ=0
    g3: LineSegment StartX=-163.167 StartY=-14.2205 StartZ=0 EndX=-164.403 EndY=-18.0247 EndZ=0
    g4: LineSegment StartX=-163.376 StartY=-20.0408 StartZ=0 EndX=-158.05 EndY=-21.7713 EndZ=0
    g5: LineSegment StartX=-158.05 StartY=-21.7713 StartZ=0 EndX=-155.825 EndY=-14.9237 EndZ=0
    g6: LineSegment StartX=-161.645 StartY=-14.7149 StartZ=0 EndX=-157.841 EndY=-15.951 EndZ=0
    g7: LineSegment StartX=-157.841 StartY=-15.951 StartZ=0 EndX=-159.077 EndY=-19.7552 EndZ=0
    g8: LineSegment StartX=-159.077 StartY=-19.7552 StartZ=0 EndX=-162.881 EndY=-18.5191 EndZ=0
    g9: LineSegment StartX=-162.881 StartY=-18.5191 StartZ=0 EndX=-161.645 EndY=-14.7149 EndZ=0
    g10: LineSegment [constr] StartX=-161.645 StartY=-14.7149 StartZ=0 EndX=-161.151 EndY=-13.1932 EndZ=0
    g11: LineSegment [constr] StartX=-159.077 StartY=-19.7552 StartZ=0 EndX=-157.555 EndY=-20.2496 EndZ=0
    g12: LineSegment [constr] StartX=-159.077 StartY=-19.7552 StartZ=0 EndX=-159.572 EndY=-21.2769 EndZ=0
    g13: LineSegment [constr] StartX=-161.645 StartY=-14.7149 StartZ=0 EndX=-163.167 EndY=-14.2205 EndZ=0
    g14: ArcOfCircle CenterX=-161.645 CenterY=-14.7149 CenterZ=0 NormalX=0 NormalY=0 NormalZ=1 AngleXU=0 Radius=1.6 StartAngle=1.25664 EndAngle=2.82743
    g15: GeomPoint [constr] X=-162.673 Y=-12.6988 Z=0
    g16: ArcOfCircle CenterX=-162.881 CenterY=-18.5191 CenterZ=0 NormalX=0 NormalY=0 NormalZ=1 AngleXU=0 Radius=1.6 StartAngle=2.82743 EndAngle=4.39823
    g17: GeomPoint [constr] X=-164.897 Y=-19.5464 Z=0
  constraints (48):
    c: Parallel(g0,g-3)
    c: Distance(g0) = 38.304
    c: Coincident(g0,g-3)
    c: Parallel(g1,g-3)
    c: Distance(g1) = 1.6
    c: Coincident(g1,g0)
    c: Coincident(g5,g4)
    c: Coincident(g5,g2)
    c: Coincident(g7,g6)
    c: Coincident(g8,g7)
    c: Coincident(g9,g8)
    c: Coincident(g9,g6)
    c: Parallel(g7,g-3)
    c: Parallel(g9,g7)
    c: Perpendicular(g6,g7)
    c: Parallel(g6,g8)
    c: Distance(g6) = 4
    c: Distance(g9) = 4
    c: Parallel(g5,g7)
    c: Parallel(g9,g3)
    c: Parallel(g2,g6)
    c: Parallel(g4,g8)
    c: Parallel(g13,g6)
    c: Parallel(g10,g9)
    c: Parallel(g11,g8)
    c: Parallel(g12,g7)
    c: Distance(g10) = 1.6
    c: Distance(g13) = 1.6
    c: Distance(g12) = 1.6
    c: Distance(g11) = 1.6
    c: Coincident(g10,g6)
    c: Coincident(g13,g6)
    c: Coincident(g12,g7)
    c: Coincident(g11,g7)
    c: Distance(g10,g15) = 1.6
    c: Distance(g15,g13) = 1.6
    c: Distance(g4,g12) = 1.6
    c: Distance(g4,g11) = 1.6
    c: PointOnObject(g15,g2)
    c: Tangent(g3,g14) = -1.5708
    c: Tangent(g2,g14) = 1.5708
    c: PointOnObject(g17,g4)
    c: PointOnObject(g17,g3)
    c: Tangent(g4,g16) = -1.5708
    c: Tangent(g3,g16) = -1.5708
    c: Equal(g16,g14)
    c: Coincident(g16,g8)
    c: Coincident(g6,g1)
FEATURE [Part::Extrusion] Extrude007  label="Extrude fermo grilletto"
  Base = -> Sketch011
  Dir = (0,-1,2e-16)
  DirMode = 2
  FaceMakerClass = Part::FaceMakerBullseye
  FaceMakerMode = 3
  LengthFwd = 25.2
  LengthRev = 0
  Solid = true
  Symmetric = true
FEATURE [Sketcher::SketchObject] Sketch012  label="buco oled"
  ArcFitTolerance = 1e-06
  AttachmentSupport = -> [XZ_Plane]
  ExternalGeometry = -> [Sketch]
  FullyConstrained = true
  MakeInternals = false
  MapMode = 5
  Placement = pos=(0,0,0) rot=(1,0,0;1.5708rad)
  sketch-geometry (4):
    g0: LineSegment StartX=-185.747 StartY=58.0965 StartZ=0 EndX=-180.232 EndY=56.0891 EndZ=0
    g1: LineSegment StartX=-185.747 StartY=58.0965 StartZ=0 EndX=-185.747 EndY=67.3588 EndZ=0
    g2: LineSegment StartX=-185.747 StartY=67.3588 StartZ=0 EndX=-180.232 EndY=67.3588 EndZ=0
    g3: LineSegment StartX=-180.232 StartY=67.3588 StartZ=0 EndX=-180.232 EndY=56.0891 EndZ=0
  constraints (10):
    c: Coincident(g1,g0)
    c: Coincident(g2,g1)
    c: Coincident(g3,g2)
    c: Coincident(g3,g0)
    c: Parallel(g1,g-5)
    c: Perpendicular(g-3,g0)
    c: Parallel(g2,g-6)
    c: Parallel(g3,g-4)
    c: Coincident(g0,g-5)
    c: Coincident(g2,g-6)
FEATURE [Part::Extrusion] Extrude008  label="Extrude buco oled"
  Base = -> Sketch012
  Dir = (0,-1,2e-16)
  DirMode = 2
  FaceMakerClass = Part::FaceMakerBullseye
  FaceMakerMode = 3
  LengthFwd = 12.8
  LengthRev = 0
  Solid = true
  Symmetric = true
FEATURE [Sketcher::SketchObject] Sketch013  label="buco pompa"
  ArcFitTolerance = 1e-06
  AttachmentSupport = -> [XZ_Plane]
  ExternalGeometry = -> [Sketch]
  FullyConstrained = true
  MakeInternals = false
  MapMode = 5
  Placement = pos=(0,0,0) rot=(1,0,0;1.5708rad)
  sketch-geometry (8):
    g0: LineSegment StartX=-82.8 StartY=-10.4 StartZ=0 EndX=-82.8 EndY=-9.6 EndZ=0
    g1: LineSegment StartX=-82.8 StartY=-9.6 StartZ=0 EndX=-67.9 EndY=-9.6 EndZ=0
    g2: LineSegment StartX=-67.9 StartY=-9.6 StartZ=0 EndX=-67.9 EndY=6 EndZ=0
    g3: LineSegment StartX=-67.9 StartY=6 StartZ=0 EndX=-65.9 EndY=6 EndZ=0
    g4: LineSegment StartX=-65.9 StartY=6 StartZ=0 EndX=-65.9 EndY=-1.7 EndZ=0
    g5: LineSegment StartX=-65.9 StartY=-1.7 StartZ=0 EndX=-57.2 EndY=-1.7 EndZ=0
    g6: LineSegment StartX=-57.2 StartY=-1.7 StartZ=0 EndX=-57.2 EndY=-10.4 EndZ=0
    g7: LineSegment StartX=-57.2 StartY=-10.4 StartZ=0 EndX=-82.8 EndY=-10.4 EndZ=0
  constraints (22):
    c: Vertical(g0)
    c: Coincident(g1,g0)
    c: Horizontal(g1)
    c: Coincident(g2,g1)
    c: Vertical(g2)
    c: Coincident(g3,g2)
    c: Horizontal(g3)
    c: Coincident(g4,g3)
    c: Vertical(g4)
    c: Coincident(g5,g4)
    c: Horizontal(g5)
    c: Coincident(g6,g5)
    c: Vertical(g6)
    c: Coincident(g7,g6)
    c: Coincident(g7,g0)
    c: DistanceY(g0,g0) = 0.8
    c: DistanceY(g6,g6) = 8.7
    c: DistanceX(g1,g1) = 14.9
    c: DistanceX(g3,g3) = 2
    c: Coincident(g0,g-4)
    c: DistanceY(g2,g-6) = 0
    c: Coincident(g6,g-5)
FEATURE [Part::Extrusion] Extrude009  label="Extrude buco pompa"
  Base = -> Sketch013
  Dir = (0,-1,2e-16)
  DirMode = 2
  FaceMakerClass = Part::FaceMakerBullseye
  FaceMakerMode = 3
  LengthFwd = 13.2
  LengthRev = 0
  Solid = true
  Symmetric = true
FEATURE [Sketcher::SketchObject] Sketch014  label="buco frontale"
  ArcFitTolerance = 1e-06
  AttachmentSupport = -> [XZ_Plane]
  ExternalGeometry = -> [Sketch]
  FullyConstrained = true
  MakeInternals = false
  MapMode = 5
  Placement = pos=(0,0,0) rot=(1,0,0;1.5708rad)
  sketch-geometry (10):
    g0: LineSegment StartX=0 StartY=0 StartZ=0 EndX=0 EndY=24.671 EndZ=0
    g1: LineSegment StartX=0 StartY=24.671 StartZ=0 EndX=-4 EndY=24.671 EndZ=0
    g2: LineSegment StartX=-4 StartY=24.671 StartZ=0 EndX=-4 EndY=16 EndZ=0
    g3: LineSegment StartX=-4 StartY=16 StartZ=0 EndX=-2.4 EndY=16 EndZ=0
    g4: LineSegment StartX=-2.4 StartY=16 StartZ=0 EndX=-2.4 EndY=10 EndZ=0
    g5: LineSegment StartX=-2.4 StartY=10 StartZ=0 EndX=-12 EndY=10 EndZ=0
    g6: LineSegment StartX=-12 StartY=10 StartZ=0 EndX=-12 EndY=6 EndZ=0
    g7: LineSegment StartX=-12 StartY=6 StartZ=0 EndX=-2.4 EndY=6 EndZ=0
    g8: LineSegment StartX=-2.4 StartY=6 StartZ=0 EndX=-2.4 EndY=0 EndZ=0
    g9: LineSegment StartX=-2.4 StartY=0 StartZ=0 EndX=0 EndY=0 EndZ=0
  constraints (29):
    c: Vertical(g0)
    c: Coincident(g1,g0)
    c: Horizontal(g1)
    c: Coincident(g2,g1)
    c: Vertical(g2)
    c: Coincident(g3,g2)
    c: Horizontal(g3)
    c: Coincident(g4,g3)
    c: Vertical(g4)
    c: Coincident(g5,g4)
    c: Horizontal(g5)
    c: Coincident(g6,g5)
    c: Vertical(g6)
    c: Coincident(g7,g6)
    c: Coincident(g8,g7)
    c: Vertical(g8)
    c: Coincident(g9,g8)
    c: Coincident(g9,g0)
    c: Horizontal(g9)
    c: DistanceY(g0,g0) = 24.671
    c: Horizontal(g7)
    c: DistanceY(g6,g6) = 4
    c: DistanceY(g4,g4) = 6
    c: DistanceX(g9,g9) = 2.4
    c: Coincident(g0,g-1)
    c: DistanceY(g-3,g7) = 0
    c: DistanceX(g8,g4) = 0
    c: DistanceX(g-3,g1) = 0
    c: DistanceX(g6,g-3) = 8
FEATURE [Part::Extrusion] Extrude010  label="Extrude buco frontale"
  Base = -> Sketch014
  Dir = (0,-1,2e-16)
  DirMode = 2
  FaceMakerClass = Part::FaceMakerBullseye
  FaceMakerMode = 3
  LengthFwd = 11.2
  LengthRev = 0
  Solid = true
  Symmetric = true
FEATURE [Sketcher::SketchObject] Sketch015  label="guida rail"
  ArcFitTolerance = 1e-06
  AttachmentSupport = -> [XZ_Plane]
  ExternalGeometry = -> [Sketch]
  FullyConstrained = true
  MakeInternals = false
  MapMode = 5
  Placement = pos=(0,0,0) rot=(1,0,0;1.5708rad)
  sketch-geometry (4):
    g0: LineSegment StartX=-100.8 StartY=43.2 StartZ=0 EndX=-44.6 EndY=43.2 EndZ=0
    g1: LineSegment StartX=-44.6 StartY=43.2 StartZ=0 EndX=-44.6 EndY=41.2 EndZ=0
    g2: LineSegment StartX=-44.6 StartY=41.2 StartZ=0 EndX=-100.8 EndY=41.2 EndZ=0
    g3: LineSegment StartX=-100.8 StartY=41.2 StartZ=0 EndX=-100.8 EndY=43.2 EndZ=0
  constraints (9):
    c: Horizontal(g0)
    c: Coincident(g1,g0)
    c: Coincident(g2,g1)
    c: Coincident(g3,g2)
    c: Coincident(g3,g0)
    c: Vertical(g3)
    c: Coincident(g2,g-3)
    c: Coincident(g1,g-3)
    c: Coincident(g0,g-4)
FEATURE [Part::Extrusion] Extrude011  label="Extrude guida rail"
  Base = -> Sketch015
  Dir = (0,-1,2e-16)
  DirMode = 2
  FaceMakerClass = Part::FaceMakerBullseye
  FaceMakerMode = 3
  LengthFwd = 9
  LengthRev = 0
  Solid = true
  Symmetric = true
FEATURE [Sketcher::SketchObject] Sketch016  label="guide per coperture laterali"
  ArcFitTolerance = 1e-06
  AttachmentSupport = -> [XZ_Plane]
  ExternalGeometry = -> [Sketch]
  FullyConstrained = true
  MakeInternals = false
  MapMode = 5
  Placement = pos=(0,0,0) rot=(1,0,0;1.5708rad)
  sketch-geometry (14):
    g0: Circle CenterX=-5.6 CenterY=7.6 CenterZ=0 NormalX=0 NormalY=0 NormalZ=1 AngleXU=0 Radius=1.6
    g1: Circle CenterX=-5.6 CenterY=7.6 CenterZ=0 NormalX=0 NormalY=0 NormalZ=1 AngleXU=0 Radius=4
    g2: Circle CenterX=-5.6 CenterY=34.8 CenterZ=0 NormalX=0 NormalY=0 NormalZ=1 AngleXU=0 Radius=1.6
    g3: Circle CenterX=-5.6 CenterY=34.8 CenterZ=0 NormalX=0 NormalY=0 NormalZ=1 AngleXU=0 Radius=4
    g4: Circle CenterX=-184.08 CenterY=34.8 CenterZ=0 NormalX=0 NormalY=0 NormalZ=1 AngleXU=0 Radius=1.6
    g5: Circle CenterX=-184.08 CenterY=34.8 CenterZ=0 NormalX=0 NormalY=0 NormalZ=1 AngleXU=0 Radius=4
    g6: Circle CenterX=-179.305 CenterY=-76.8316 CenterZ=0 NormalX=0 NormalY=0 NormalZ=1 AngleXU=0 Radius=1.6
    g7: Circle CenterX=-179.305 CenterY=-76.8316 CenterZ=0 NormalX=0 NormalY=0 NormalZ=1 AngleXU=0 Radius=4
    g8: Circle CenterX=-213.443 CenterY=-76.8316 CenterZ=0 NormalX=0 NormalY=0 NormalZ=1 AngleXU=0 Radius=1.6
    g9: Circle CenterX=-213.443 CenterY=-76.8316 CenterZ=0 NormalX=0 NormalY=0 NormalZ=1 AngleXU=0 Radius=4
    g10: Circle CenterX=-78.51 CenterY=7.6 CenterZ=0 NormalX=0 NormalY=0 NormalZ=1 AngleXU=0 Radius=1.6
    g11: Circle CenterX=-78.51 CenterY=7.6 CenterZ=0 NormalX=0 NormalY=0 NormalZ=1 AngleXU=0 Radius=4
    g12: Circle CenterX=-78.51 CenterY=34.8 CenterZ=0 NormalX=0 NormalY=0 NormalZ=1 AngleXU=0 Radius=1.6
    g13: Circle CenterX=-78.51 CenterY=34.8 CenterZ=0 NormalX=0 NormalY=0 NormalZ=1 AngleXU=0 Radius=4
  constraints (35):
    c: Diameter(g0) = 3.2
    c: Diameter(g1) = 8
    c: Coincident(g0,g1)
    c: Diameter(g2) = 3.2
    c: Diameter(g3) = 8
    c: Coincident(g3,g2)
    c: Tangent(g2,g-7)
    c: Diameter(g4) = 3.2
    c: Diameter(g5) = 8
    c: Coincident(g5,g4)
    c: Tangent(g4,g-7)
    c: Tangent(g4,g-8)
    c: Diameter(g6) = 3.2
    c: Diameter(g7) = 8
    c: Coincident(g7,g6)
    c: Tangent(g6,g-9)
    c: Tangent(g6,g-10)
    c: Diameter(g8) = 3.2
    c: Diameter(g9) = 8
    c: Coincident(g9,g8)
    c: Tangent(g8,g-10)
    c: Tangent(g8,g-11)
    c: Diameter(g10) = 3.2
    c: Diameter(g11) = 8
    c: Diameter(g12) = 3.2
    c: Diameter(g13) = 8
    c: Coincident(g12,g13)
    c: Coincident(g10,g11)
    c: Tangent(g12,g-7)
    c: DistanceX(g12,g10) = 0
    c: Tangent(g2,g-6)
    c: Tangent(g0,g-6)
    c: Tangent(g0,g-3)
    c: Tangent(g10,g-3)
    c: Tangent(g10,g-4)
FEATURE [Part::Extrusion] Extrude012  label="extrude guide per coperture laterali"
  Base = -> Sketch016
  Dir = (0,-1,2e-16)
  DirMode = 2
  FaceMakerClass = Part::FaceMakerBullseye
  FaceMakerMode = 3
  LengthFwd = 25.2
  LengthRev = 0
  Solid = true
  Symmetric = true
FEATURE [Sketcher::SketchObject] Sketch017  label="supporto CAM"
  ArcFitTolerance = 1e-06
  AttachmentSupport = -> [XZ_Plane]
  ExternalGeometry = -> [Sketch]
  FullyConstrained = true
  MakeInternals = false
  MapMode = 5
  Placement = pos=(0,0,0) rot=(1,0,0;1.5708rad)
  sketch-geometry (6):
    g0: LineSegment StartX=-2.4 StartY=48 StartZ=0 EndX=-2.4 EndY=41.2 EndZ=0
    g1: LineSegment StartX=-2.4 StartY=48 StartZ=0 EndX=-34 EndY=48 EndZ=0
    g2: LineSegment StartX=-34 StartY=48 StartZ=0 EndX=-34 EndY=46.72 EndZ=0
    g3: LineSegment StartX=-34 StartY=46.72 StartZ=0 EndX=-36 EndY=46.72 EndZ=0
    g4: LineSegment StartX=-36 StartY=46.72 StartZ=0 EndX=-36 EndY=41.2 EndZ=0
    g5: LineSegment StartX=-36 StartY=41.2 StartZ=0 EndX=-2.4 EndY=41.2 EndZ=0
  constraints (15):
    c: Coincident(g1,g0)
    c: Horizontal(g1)
    c: Coincident(g2,g1)
    c: Vertical(g2)
    c: Coincident(g3,g2)
    c: Horizontal(g3)
    c: Coincident(g4,g3)
    c: Coincident(g5,g4)
    c: DistanceX(g1,g0) = 31.6
    c: Coincident(g5,g0)
    c: Vertical(g4)
    c: DistanceY(g2,g1) = 1.28
    c: Coincident(g0,g-3)
    c: Coincident(g0,g-3)
    c: Coincident(g4,g-4)
FEATURE [Part::Extrusion] Extrude013  label="Extrude supporto CAM"
  Base = -> Sketch017
  Dir = (0,-1,2e-16)
  DirMode = 2
  FaceMakerClass = Part::FaceMakerBullseye
  FaceMakerMode = 3
  LengthFwd = 17.8
  LengthRev = 0
  Solid = true
  Symmetric = true
FEATURE [Sketcher::SketchObject] Sketch018  label="Scavo CAM"
  ArcFitTolerance = 1e-06
  AttachmentSupport = -> [YZ_Plane]
  ExternalGeometry = -> [Sketch]
  FullyConstrained = true
  MakeInternals = false
  MapMode = 5
  Placement = pos=(0,0,0) rot=(0.57735,0.57735,0.57735;2.0944rad)
  sketch-geometry (4):
    g0: LineSegment StartX=-7.73 StartY=48 StartZ=0 EndX=7.73 EndY=48 EndZ=0
    g1: LineSegment [constr] StartX=1.07e-14 StartY=48 StartZ=0 EndX=0 EndY=43.5155 EndZ=0
    g2: ArcOfCircle CenterX=9e-15 CenterY=52.42 CenterZ=0 NormalX=0 NormalY=0 NormalZ=1 AngleXU=0 Radius=8.90445 StartAngle=3.66102 EndAngle=5.76376
    g3: Circle [constr] CenterX=9e-15 CenterY=52.42 CenterZ=0 NormalX=0 NormalY=0 NormalZ=1 AngleXU=0 Radius=8.9
  constraints (13):
    c: Horizontal(g0)
    c: DistanceY(g-3,g0) = 0
    c: DistanceX(g0,g0) = 15.46
    c: DistanceX(g0,g-3) = 7.73
    c: DistanceX(g-3) = 0
    c: Coincident(g1,g-3)
    c: PointOnObject(g1,g-2)
    c: Coincident(g2,g0)
    c: Coincident(g2,g0)
    c: PointOnObject(g1,g2)
    c: Diameter(g3) = 17.8
    c: DistanceY(g1,g3) = 4.42
    c: Coincident(g2,g3)
FEATURE [Part::Extrusion] Extrude014  label="Extrude Scavo CAM"
  Base = -> Sketch018
  Dir = (1,0,0)
  DirMode = 2
  FaceMakerClass = Part::FaceMakerBullseye
  FaceMakerMode = 3
  LengthFwd = -34
  LengthRev = 0
  Solid = true
  Symmetric = false
FEATURE [Sketcher::SketchObject] Sketch019  label="scavo rumble"
  ArcFitTolerance = 1e-06
  AttachmentSupport = -> [XZ_Plane]
  ExternalGeometry = -> [Sketch]
  FullyConstrained = true
  MakeInternals = false
  MapMode = 5
  Placement = pos=(0,0,0) rot=(1,0,0;1.5708rad)
  sketch-geometry (6):
    g0: LineSegment StartX=-169.087 StartY=-38.264 StartZ=0 EndX=-166.994 EndY=-38.9438 EndZ=0
    g1: LineSegment StartX=-166.994 StartY=-38.9438 StartZ=0 EndX=-174.102 EndY=-60.8181 EndZ=0
    g2: LineSegment StartX=-174.102 StartY=-60.8181 StartZ=0 EndX=-176.194 EndY=-60.1383 EndZ=0
    g3: LineSegment StartX=-176.194 StartY=-60.1383 StartZ=0 EndX=-169.087 EndY=-38.264 EndZ=0
    g4: LineSegment [constr] StartX=-145.51 StartY=22 StartZ=0 EndX=-165.472 EndY=-39.4383 EndZ=0
    g5: LineSegment [constr] StartX=-166.994 StartY=-38.9438 StartZ=0 EndX=-165.472 EndY=-39.4383 EndZ=0
  constraints (17):
    c: Coincident(g1,g0)
    c: Coincident(g2,g1)
    c: Coincident(g3,g2)
    c: Coincident(g3,g0)
    c: Parallel(g3,g-3)
    c: Parallel(g3,g1)
    c: Perpendicular(g3,g0)
    c: Perpendicular(g2,g3)
    c: Distance(g2,g0) = 23
    c: Parallel(g4,g-3)
    c: Distance(g4) = 64.6
    c: Coincident(g4,g-3)
    c: Parallel(g5,g0)
    c: Distance(g5) = 1.6
    c: Coincident(g5,g0)
    c: Distance(g5,g0) = 3.8
    c: Coincident(g5,g4)
FEATURE [Part::Extrusion] Extrude015  label="scavo rumble001"
  Base = -> Sketch019
  Dir = (0,-1,2e-16)
  DirMode = 2
  FaceMakerClass = Part::FaceMakerBullseye
  FaceMakerMode = 3
  LengthFwd = 21
  LengthRev = 0
  Solid = true
  Symmetric = true
FEATURE [Sketcher::SketchObject] Sketch020  label="fermo rumble"
  ArcFitTolerance = 1e-06
  AttachmentSupport = -> [XZ_Plane]
  ExternalGeometry = -> [Sketch019,Sketch]
  FullyConstrained = true
  MakeInternals = false
  MapMode = 5
  Placement = pos=(0,0,0) rot=(1,0,0;1.5708rad)
  sketch-geometry (16):
    g0: LineSegment [constr] StartX=-171.22 StartY=-57.1279 StartZ=0 EndX=-172.58 EndY=-61.3126 EndZ=0
    g1: LineSegment [constr] StartX=-172.58 StartY=-61.3126 StartZ=0 EndX=-174.102 EndY=-60.8181 EndZ=0
    g2: LineSegment StartX=-172.633 StartY=-54.3557 StartZ=0 EndX=-170.54 EndY=-55.0356 EndZ=0
    g3: LineSegment StartX=-170.54 StartY=-55.0356 StartZ=0 EndX=-171.22 EndY=-57.1279 EndZ=0
    g4: LineSegment StartX=-171.22 StartY=-57.1279 StartZ=0 EndX=-173.313 EndY=-56.4481 EndZ=0
    g5: LineSegment StartX=-173.313 StartY=-56.4481 StartZ=0 EndX=-172.633 EndY=-54.3557 EndZ=0
    g6: LineSegment StartX=-172.138 StartY=-52.8341 StartZ=0 EndX=-168.714 EndY=-53.9465 EndZ=0
    g7: LineSegment StartX=-168.714 StartY=-53.9465 StartZ=0 EndX=-170.321 EndY=-58.892 EndZ=0
    g8: LineSegment StartX=-170.321 StartY=-58.892 StartZ=0 EndX=-173.745 EndY=-57.7795 EndZ=0
    g9: LineSegment StartX=-174.772 StartY=-55.7634 StartZ=0 EndX=-174.154 EndY=-53.8613 EndZ=0
    g10: LineSegment [constr] StartX=-174.154 StartY=-53.8613 StartZ=0 EndX=-173.66 EndY=-52.3396 EndZ=0
    g11: LineSegment [constr] StartX=-173.66 StartY=-52.3396 StartZ=0 EndX=-172.138 EndY=-52.8341 EndZ=0
    g12: ArcOfCircle CenterX=-173.251 CenterY=-56.2579 CenterZ=0 NormalX=0 NormalY=0 NormalZ=1 AngleXU=0 Radius=1.6 StartAngle=2.82743 EndAngle=4.39823
    g13: GeomPoint [constr] X=-175.267 Y=-57.2851 Z=0
    g14: ArcOfCircle CenterX=-172.633 CenterY=-54.3557 CenterZ=0 NormalX=0 NormalY=0 NormalZ=1 AngleXU=0 Radius=1.6 StartAngle=1.25664 EndAngle=2.82743
    g15: GeomPoint [constr] X=-173.66 Y=-52.3396 Z=0
  constraints (42):
    c: Parallel(g0,g-4)
    c: Distance(g0) = 4.4
    c: Coincident(g1,g0)
    c: Perpendicular(g0,g1)
    c: Distance(g1) = 1.6
    c: Coincident(g1,g-5)
    c: Coincident(g3,g2)
    c: Coincident(g4,g3)
    c: Coincident(g5,g4)
    c: Coincident(g5,g2)
    c: Parallel(g3,g-4)
    c: Parallel(g3,g5)
    c: Perpendicular(g2,g3)
    c: Parallel(g4,g2)
    c: Distance(g2) = 2.2
    c: Distance(g3) = 2.2
    c: Coincident(g7,g6)
    c: Coincident(g8,g7)
    c: Parallel(g7,g-4)
    c: Parallel(g7,g9)
    c: Perpendicular(g6,g7)
    c: Parallel(g6,g8)
    c: Distance(g6,g15) = 5.2
    c: Distance(g7) = 5.2
    c: Coincident(g11,g10)
    c: Parallel(g10,g9)
    c: Parallel(g11,g6)
    c: Distance(g10) = 1.6
    c: Distance(g11) = 1.6
    c: Coincident(g10,g15)
    c: Distance(g11,g2) = 1.6
    c: Distance(g2,g10) = 1.6
    c: PointOnObject(g13,g8)
    c: PointOnObject(g13,g9)
    c: Tangent(g8,g12) = 1.5708
    c: Tangent(g9,g12) = 1.5708
    c: PointOnObject(g15,g9)
    c: Tangent(g6,g14) = 1.5708
    c: Tangent(g9,g14) = 1.5708
    c: Equal(g12,g14)
    c: Coincident(g6,g11)
    c: Coincident(g3,g0)
FEATURE [Part::Extrusion] Extrude016  label="Extrude fermo rumble"
  Base = -> Sketch020
  Dir = (0,-1,2e-16)
  DirMode = 2
  FaceMakerClass = Part::FaceMakerBullseye
  FaceMakerMode = 3
  LengthFwd = 25.2
  LengthRev = 0
  Solid = true
  Symmetric = true
FEATURE [Sketcher::SketchObject] Sketch021  label="perno fermo rumble001"
  ArcFitTolerance = 1e-06
  AttachmentSupport = -> [XZ_Plane001]
  FullyConstrained = true
  MakeInternals = false
  MapMode = 5
  Placement = pos=(0,0,0) rot=(1,0,0;1.5708rad)
  sketch-geometry (16):
    g0: LineSegment StartX=0 StartY=0.45 StartZ=0 EndX=0 EndY=1.55 EndZ=0
    g1: LineSegment StartX=0.45 StartY=2 StartZ=0 EndX=1.55 EndY=2 EndZ=0
    g2: LineSegment StartX=2 StartY=1.55 StartZ=0 EndX=2 EndY=0.45 EndZ=0
    g3: LineSegment StartX=1.55 StartY=0 StartZ=0 EndX=0.45 EndY=0 EndZ=0
    g4: ArcOfCircle [constr] CenterX=0.45 CenterY=1.55 CenterZ=0 NormalX=0 NormalY=0 NormalZ=1 AngleXU=0 Radius=0.45 StartAngle=1.5708 EndAngle=3.14159
    g5: GeomPoint [constr] X=0 Y=2 Z=0
    g6: LineSegment StartX=0.45 StartY=2 StartZ=0 EndX=0 EndY=1.55 EndZ=0
    g7: ArcOfCircle [constr] CenterX=1.55 CenterY=1.55 CenterZ=0 NormalX=0 NormalY=0 NormalZ=1 AngleXU=0 Radius=0.45 StartAngle=0 EndAngle=1.5708
    g8: GeomPoint [constr] X=2 Y=2 Z=0
    g9: LineSegment StartX=2 StartY=1.55 StartZ=0 EndX=1.55 EndY=2 EndZ=0
    g10: ArcOfCircle [constr] CenterX=1.55 CenterY=0.45 CenterZ=0 NormalX=0 NormalY=0 NormalZ=1 AngleXU=0 Radius=0.45 StartAngle=4.71239 EndAngle=6.28319
    g11: GeomPoint [constr] X=2 Y=0 Z=0
    g12: LineSegment StartX=1.55 StartY=0 StartZ=0 EndX=2 EndY=0.45 EndZ=0
    g13: ArcOfCircle [constr] CenterX=0.45 CenterY=0.45 CenterZ=0 NormalX=0 NormalY=0 NormalZ=1 AngleXU=0 Radius=0.45 StartAngle=3.14159 EndAngle=4.71239
    g14: GeomPoint [constr] X=0 Y=0 Z=0
    g15: LineSegment StartX=0 StartY=0.45 StartZ=0 EndX=0.45 EndY=0 EndZ=0
  constraints (35):
    c: Coincident(g14,g-1)
    c: PointOnObject(g5,g-2)
    c: Horizontal(g1)
    c: Vertical(g2)
    c: Horizontal(g3)
    c: DistanceX(g5,g8) = 2
    c: DistanceY(g11,g8) = 2
    c: PointOnObject(g5,g0)
    c: PointOnObject(g5,g1)
    c: Tangent(g0,g4) = 1.5708
    c: Tangent(g1,g4) = 1.5708
    c: Coincident(g6,g0)
    c: Coincident(g6,g1)
    c: PointOnObject(g8,g2)
    c: PointOnObject(g8,g1)
    c: Tangent(g2,g7) = 1.5708
    c: Tangent(g1,g7) = 1.5708
    c: Coincident(g9,g2)
    c: Coincident(g9,g1)
    c: PointOnObject(g11,g2)
    c: PointOnObject(g11,g3)
    c: Tangent(g2,g10) = 1.5708
    c: Tangent(g3,g10) = 1.5708
    c: Coincident(g12,g2)
    c: Coincident(g12,g3)
    c: PointOnObject(g14,g0)
    c: PointOnObject(g14,g3)
    c: Tangent(g0,g13) = 1.5708
    c: Tangent(g3,g13) = 1.5708
    c: Coincident(g15,g0)
    c: Coincident(g15,g3)
    c: Equal(g6,g9)
    c: Equal(g9,g12)
    c: Equal(g12,g15)
    c: DistanceX(g14,g3) = 0.45
FEATURE [Sketcher::SketchObject] Sketch022  label="fori per M3x5(OD)x6(L)"
  ArcFitTolerance = 1e-06
  AttachmentSupport = -> [XZ_Plane]
  ExternalGeometry = -> [Sketch016]
  FullyConstrained = true
  MakeInternals = false
  MapMode = 5
  Placement = pos=(0,0,0) rot=(1,0,0;1.5708rad)
  sketch-geometry (7):
    g0: Circle CenterX=-5.6 CenterY=34.8 CenterZ=0 NormalX=0 NormalY=0 NormalZ=1 AngleXU=0 Radius=2.5
    g1: Circle CenterX=-5.6 CenterY=7.6 CenterZ=0 NormalX=0 NormalY=0 NormalZ=1 AngleXU=0 Radius=2.5
    g2: Circle CenterX=-78.51 CenterY=34.8 CenterZ=0 NormalX=0 NormalY=0 NormalZ=1 AngleXU=0 Radius=2.5
    g3: Circle CenterX=-78.51 CenterY=7.6 CenterZ=0 NormalX=0 NormalY=0 NormalZ=1 AngleXU=0 Radius=2.5
    g4: Circle CenterX=-184.08 CenterY=34.8 CenterZ=0 NormalX=0 NormalY=0 NormalZ=1 AngleXU=0 Radius=2.5
    g5: Circle CenterX=-179.305 CenterY=-76.8316 CenterZ=0 NormalX=0 NormalY=0 NormalZ=1 AngleXU=0 Radius=2.5
    g6: Circle CenterX=-213.443 CenterY=-76.8316 CenterZ=0 NormalX=0 NormalY=0 NormalZ=1 AngleXU=0 Radius=2.5
  constraints (14):
    c: Diameter(g0) = 5
    c: Diameter(g1) = 5
    c: Diameter(g2) = 5
    c: Diameter(g3) = 5
    c: Diameter(g4) = 5
    c: Diameter(g5) = 5
    c: Diameter(g6) = 5
    c: Coincident(g0,g-8)
    c: Coincident(g1,g-9)
    c: Coincident(g2,g-6)
    c: Coincident(g3,g-7)
    c: Coincident(g4,g-5)
    c: Coincident(g5,g-4)
    c: Coincident(g6,g-3)
FEATURE [Part::Extrusion] Extrude018  label="Extrude fori M3x5x6 - dx"
  Base = -> Sketch022
  Dir = (0,-1,2e-16)
  DirMode = 2
  FaceMakerClass = Part::FaceMakerBullseye
  FaceMakerMode = 3
  LengthFwd = 6.2
  LengthRev = 0
  Placement = pos=(0,-9.5,0) rot=(0,0,1;0rad)
  Solid = true
  Symmetric = true
FEATURE [Part::Extrusion] Extrude019  label="Extrude fori M3x5x6 - sx"
  Base = -> Sketch022
  Dir = (0,-1,2e-16)
  DirMode = 2
  FaceMakerClass = Part::FaceMakerBullseye
  FaceMakerMode = 3
  LengthFwd = 6.2
  LengthRev = 0
  Placement = pos=(0,9.5,0) rot=(0,0,1;0rad)
  Solid = true
  Symmetric = true
FEATURE [Sketcher::SketchObject] Sketch023  label="foro anteriore M3x5x6"
  ArcFitTolerance = 1e-06
  AttachmentSupport = -> [YZ_Plane]
  FullyConstrained = true
  MakeInternals = false
  MapMode = 5
  Placement = pos=(0,0,0) rot=(0.57735,0.57735,0.57735;2.0944rad)
  sketch-geometry (2):
    g0: LineSegment [constr] StartX=0 StartY=0 StartZ=0 EndX=0 EndY=38.6 EndZ=0
    g1: Circle CenterX=0 CenterY=38.6 CenterZ=0 NormalX=0 NormalY=0 NormalZ=1 AngleXU=0 Radius=2.5
  constraints (5):
    c: Coincident(g0,g-1)
    c: PointOnObject(g0,g-2)
    c: DistanceY(g0,g0) = 38.6
    c: Diameter(g1) = 5
    c: Coincident(g1,g0)
FEATURE [Part::Extrusion] Extrude020  label="Extrude foro anteriore M3x5x6"
  Base = -> Sketch023
  Dir = (1,0,0)
  DirMode = 2
  FaceMakerClass = Part::FaceMakerBullseye
  FaceMakerMode = 3
  LengthFwd = -6.2
  LengthRev = 0
  Solid = true
  Symmetric = false
FEATURE [Sketcher::SketchObject] Sketch024  label="fori per viti frontale"
  ArcFitTolerance = 1e-06
  AttachmentSupport = -> [YZ_Plane]
  FullyConstrained = true
  MakeInternals = false
  MapMode = 5
  Placement = pos=(0,0,0) rot=(0.57735,0.57735,0.57735;2.0944rad)
  sketch-geometry (9):
    g0: LineSegment [constr] StartX=-10.3 StartY=30.721 StartZ=0 EndX=10.3 EndY=30.721 EndZ=0
    g1: LineSegment [constr] StartX=10.3 StartY=30.721 StartZ=0 EndX=10.3 EndY=10.121 EndZ=0
    g2: LineSegment [constr] StartX=10.3 StartY=10.121 StartZ=0 EndX=-10.3 EndY=10.121 EndZ=0
    g3: LineSegment [constr] StartX=-10.3 StartY=10.121 StartZ=0 EndX=-10.3 EndY=30.721 EndZ=0
    g4: LineSegment [constr] StartX=0 StartY=0 StartZ=0 EndX=0 EndY=10.121 EndZ=0
    g5: Circle CenterX=-10.3 CenterY=30.721 CenterZ=0 NormalX=0 NormalY=0 NormalZ=1 AngleXU=0 Radius=2
    g6: Circle CenterX=10.3 CenterY=30.721 CenterZ=0 NormalX=0 NormalY=0 NormalZ=1 AngleXU=0 Radius=2
    g7: Circle CenterX=-10.3 CenterY=10.121 CenterZ=0 NormalX=0 NormalY=0 NormalZ=1 AngleXU=0 Radius=2
    g8: Circle CenterX=10.3 CenterY=10.121 CenterZ=0 NormalX=0 NormalY=0 NormalZ=1 AngleXU=0 Radius=2
  constraints (22):
    c: Horizontal(g0)
    c: Coincident(g1,g0)
    c: Vertical(g1)
    c: Coincident(g2,g1)
    c: Horizontal(g2)
    c: Coincident(g3,g2)
    c: Coincident(g3,g0)
    c: Vertical(g3)
    c: DistanceX(g0,g0) = 20.6
    c: DistanceY(g3,g3) = 20.6
    c: Coincident(g4,g-1)
    c: PointOnObject(g4,g-2)
    c: DistanceY(g4,g4) = 10.121
    c: Symmetric(g2,g2,g4)
    c: Diameter(g5) = 4
    c: Diameter(g6) = 4
    c: Diameter(g7) = 4
    c: Diameter(g8) = 4
    c: Coincident(g5,g0)
    c: Coincident(g6,g0)
    c: Coincident(g7,g2)
    c: Coincident(g8,g1)
FEATURE [Part::Extrusion] Extrude021  label="Extrude fori per viti frontale"
  Base = -> Sketch024
  Dir = (1,0,0)
  DirMode = 2
  FaceMakerClass = Part::FaceMakerBullseye
  FaceMakerMode = 3
  LengthFwd = -2.4
  LengthRev = 0
  Solid = true
  Symmetric = false
FEATURE [Sketcher::SketchObject] Sketch025  label="foro per filo CAM"
  ArcFitTolerance = 1e-06
  AttachmentSupport = -> [XZ_Plane]
  ExternalGeometry = -> [Sketch]
  FullyConstrained = true
  MakeInternals = false
  MapMode = 5
  Placement = pos=(0,0,0) rot=(1,0,0;1.5708rad)
  sketch-geometry (4):
    g0: LineSegment StartX=-44.6 StartY=41.2 StartZ=0 EndX=-44.6 EndY=36.4 EndZ=0
    g1: LineSegment StartX=-44.6 StartY=36.4 StartZ=0 EndX=-54.6 EndY=36.4 EndZ=0
    g2: LineSegment StartX=-54.6 StartY=36.4 StartZ=0 EndX=-50.4 EndY=41.2 EndZ=0
    g3: LineSegment StartX=-50.4 StartY=41.2 StartZ=0 EndX=-44.6 EndY=41.2 EndZ=0
  constraints (11):
    c: Vertical(g0)
    c: Coincident(g1,g0)
    c: Horizontal(g1)
    c: Coincident(g2,g1)
    c: Coincident(g3,g2)
    c: Coincident(g3,g0)
    c: Horizontal(g3)
    c: Coincident(g0,g-3)
    c: DistanceY(g0,g-4) = 0
    c: DistanceX(g3,g3) = 5.8
    c: DistanceX(g1,g1) = 10
FEATURE [Part::Extrusion] Extrude022  label="Extrude foro per filo CAM dx"
  Base = -> Sketch025
  Dir = (0,-1,2e-16)
  DirMode = 2
  FaceMakerClass = Part::FaceMakerBullseye
  FaceMakerMode = 3
  LengthFwd = 4.9
  LengthRev = 0
  Placement = pos=(0,6.95,0) rot=(0,0,1;0rad)
  Solid = true
  Symmetric = true
FEATURE [Part::Extrusion] Extrude023  label="Extrude foro per filo CAM sx"
  Base = -> Sketch025
  Dir = (0,-1,2e-16)
  DirMode = 2
  FaceMakerClass = Part::FaceMakerBullseye
  FaceMakerMode = 3
  LengthFwd = 4.9
  LengthRev = 0
  Placement = pos=(0,-6.95,0) rot=(0,0,1;0rad)
  Solid = true
  Symmetric = true
FEATURE [Sketcher::SketchObject] Sketch026  label="foro sotto anteriore M3x5x6"
  ArcFitTolerance = 1e-06
  AttachmentSupport = -> [XY_Plane]
  FullyConstrained = true
  MakeInternals = false
  MapMode = 5
  sketch-geometry (2):
    g0: LineSegment [constr] StartX=0 StartY=0 StartZ=0 EndX=-16.5 EndY=0 EndZ=0
    g1: Circle CenterX=-16.5 CenterY=0 CenterZ=0 NormalX=0 NormalY=0 NormalZ=1 AngleXU=0 Radius=2.5
  constraints (5):
    c: Distance(g0) = 16.5
    c: Coincident(g0,g-1)
    c: PointOnObject(g0,g-1)
    c: Diameter(g1) = 5
    c: Coincident(g0,g1)
FEATURE [Sketcher::SketchObject] Sketch027  label="foro sotto posteriore M3x5x6"
  ArcFitTolerance = 1e-06
  AttachmentSupport = -> [XY_Plane]
  ExternalGeometry = -> [Sketch]
  FullyConstrained = true
  MakeInternals = false
  MapMode = 5
  sketch-geometry (2):
    g0: LineSegment [constr] StartX=-82.8 StartY=2e-16 StartZ=0 EndX=-71.3 EndY=2e-16 EndZ=0
    g1: Circle CenterX=-71.3 CenterY=2e-16 CenterZ=0 NormalX=0 NormalY=0 NormalZ=1 AngleXU=0 Radius=2.5
  constraints (5):
    c: Distance(g0) = 11.5
    c: Coincident(g0,g-3)
    c: PointOnObject(g0,g-3)
    c: Diameter(g1) = 5
    c: Coincident(g1,g0)
FEATURE [Sketcher::SketchObject] Sketch029  label="fori sotto impugnatura"
  ArcFitTolerance = 1e-06
  AttachmentSupport = -> [XY_Plane]
  ExternalGeometry = -> [Sketch]
  FullyConstrained = true
  MakeInternals = false
  MapMode = 5
  sketch-geometry (15):
    g0: LineSegment [constr] StartX=-175.232 StartY=-1.83e-14 StartZ=0 EndX=-191.232 EndY=0 EndZ=0
    g1: Circle CenterX=-191.232 CenterY=0 CenterZ=0 NormalX=0 NormalY=0 NormalZ=1 AngleXU=0 Radius=3.95
    g2: LineSegment [constr] StartX=-175.232 StartY=-1.83e-14 StartZ=0 EndX=-204.275 EndY=0 EndZ=0
    g3: LineSegment StartX=-204.275 StartY=3.525 StartZ=0 EndX=-204.275 EndY=-3.525 EndZ=0
    g4: LineSegment StartX=-205.4 StartY=-4.65 StartZ=0 EndX=-206.65 EndY=-4.65 EndZ=0
    g5: LineSegment StartX=-207.775 StartY=-3.525 StartZ=0 EndX=-207.775 EndY=3.525 EndZ=0
    g6: LineSegment StartX=-206.65 StartY=4.65 StartZ=0 EndX=-205.4 EndY=4.65 EndZ=0
    g7: ArcOfCircle CenterX=-206.65 CenterY=3.525 CenterZ=0 NormalX=0 NormalY=0 NormalZ=1 AngleXU=0 Radius=1.125 StartAngle=1.5708 EndAngle=3.14159
    g8: GeomPoint [constr] X=-207.775 Y=4.65 Z=0
    g9: ArcOfCircle CenterX=-205.4 CenterY=3.525 CenterZ=0 NormalX=0 NormalY=0 NormalZ=1 AngleXU=0 Radius=1.125 StartAngle=0 EndAngle=1.5708
    g10: GeomPoint [constr] X=-204.275 Y=4.65 Z=0
    g11: ArcOfCircle CenterX=-205.4 CenterY=-3.525 CenterZ=0 NormalX=0 NormalY=0 NormalZ=1 AngleXU=0 Radius=1.125 StartAngle=4.71239 EndAngle=6.28319
    g12: GeomPoint [constr] X=-204.275 Y=-4.65 Z=0
    g13: ArcOfCircle CenterX=-206.65 CenterY=-3.525 CenterZ=0 NormalX=0 NormalY=0 NormalZ=1 AngleXU=0 Radius=1.125 StartAngle=3.14159 EndAngle=4.71239
    g14: GeomPoint [constr] X=-207.775 Y=-4.65 Z=0
  constraints (35):
    c: Distance(g0) = 16
    c: Coincident(g0,g-3)
    c: PointOnObject(g0,g-1)
    c: Diameter(g1) = 7.9
    c: Coincident(g1,g0)
    c: Coincident(g2,g0)
    c: PointOnObject(g2,g-1)
    c: Vertical(g3)
    c: Horizontal(g4)
    c: Vertical(g5)
    c: Horizontal(g6)
    c: DistanceY(g12,g10) = 9.3
    c: DistanceX(g8,g10) = 3.5
    c: Symmetric(g10,g12,g2)
    c: PointOnObject(g8,g5)
    c: PointOnObject(g8,g6)
    c: Tangent(g5,g7) = 1.5708
    c: Tangent(g6,g7) = 1.5708
    c: PointOnObject(g10,g3)
    c: PointOnObject(g10,g6)
    c: Tangent(g3,g9) = 1.5708
    c: Tangent(g6,g9) = 1.5708
    c: PointOnObject(g12,g3)
    c: PointOnObject(g12,g4)
    c: Tangent(g3,g11) = 1.5708
    c: Tangent(g4,g11) = 1.5708
    c: PointOnObject(g14,g4)
    c: PointOnObject(g14,g5)
    c: Tangent(g4,g13) = 1.5708
    c: Tangent(g5,g13) = 1.5708
    c: Equal(g7,g9)
    c: Equal(g9,g11)
    c: Equal(g11,g13)
    c: DistanceX(g6,g6) = 1.25
    c: DistanceX(g-5,g5) = 6.8
FEATURE [Sketcher::SketchObject] Sketch030  label="fori superiori per solenoide e oled"
  ArcFitTolerance = 1e-06
  AttachmentSupport = -> [XY_Plane]
  ExternalGeometry = -> [Sketch]
  FullyConstrained = true
  MakeInternals = false
  MapMode = 5
  sketch-geometry (33):
    g0: LineSegment [constr] StartX=-181.6 StartY=1.12e-14 StartZ=0 EndX=-169.91 EndY=0 EndZ=0
    g1: LineSegment [constr] StartX=-169.91 StartY=0 StartZ=0 EndX=-169.91 EndY=-2.6 EndZ=0
    g2: LineSegment [constr] StartX=-169.91 StartY=0 StartZ=0 EndX=-169.91 EndY=2.6 EndZ=0
    g3: LineSegment StartX=-169.91 StartY=4.975 StartZ=0 EndX=-169.91 EndY=8.225 EndZ=0
    g4: LineSegment StartX=-167.535 StartY=10.6 StartZ=0 EndX=-167.285 EndY=10.6 EndZ=0
    g5: LineSegment StartX=-164.91 StartY=8.225 StartZ=0 EndX=-164.91 EndY=4.975 EndZ=0
    g6: LineSegment StartX=-167.285 StartY=2.6 StartZ=0 EndX=-167.535 EndY=2.6 EndZ=0
    g7: LineSegment StartX=-169.91 StartY=-4.975 StartZ=0 EndX=-169.91 EndY=-8.225 EndZ=0
    g8: LineSegment StartX=-167.535 StartY=-10.6 StartZ=0 EndX=-167.285 EndY=-10.6 EndZ=0
    g9: LineSegment StartX=-164.91 StartY=-8.225 StartZ=0 EndX=-164.91 EndY=-4.975 EndZ=0
    g10: LineSegment StartX=-167.285 StartY=-2.6 StartZ=0 EndX=-167.535 EndY=-2.6 EndZ=0
    g11: ArcOfCircle CenterX=-167.535 CenterY=8.225 CenterZ=0 NormalX=0 NormalY=0 NormalZ=1 AngleXU=0 Radius=2.375 StartAngle=1.5708 EndAngle=3.14159
    g12: GeomPoint [constr] X=-169.91 Y=10.6 Z=0
    g13: ArcOfCircle CenterX=-167.285 CenterY=8.225 CenterZ=0 NormalX=0 NormalY=0 NormalZ=1 AngleXU=0 Radius=2.375 StartAngle=0 EndAngle=1.5708
    g14: GeomPoint [constr] X=-164.91 Y=10.6 Z=0
    g15: ArcOfCircle CenterX=-167.285 CenterY=4.975 CenterZ=0 NormalX=0 NormalY=0 NormalZ=1 AngleXU=0 Radius=2.375 StartAngle=4.71239 EndAngle=6.28319
    g16: GeomPoint [constr] X=-164.91 Y=2.6 Z=0
    g17: ArcOfCircle CenterX=-167.535 CenterY=4.975 CenterZ=0 NormalX=0 NormalY=0 NormalZ=1 AngleXU=0 Radius=2.375 StartAngle=3.14159 EndAngle=4.71239
    g18: GeomPoint [constr] X=-169.91 Y=2.6 Z=0
    g19: ArcOfCircle CenterX=-167.535 CenterY=-4.975 CenterZ=0 NormalX=0 NormalY=0 NormalZ=1 AngleXU=0 Radius=2.375 StartAngle=1.5708 EndAngle=3.14159
    g20: GeomPoint [constr] X=-169.91 Y=-2.6 Z=0
    g21: ArcOfCircle CenterX=-167.285 CenterY=-4.975 CenterZ=0 NormalX=0 NormalY=0 NormalZ=1 AngleXU=0 Radius=2.375 StartAngle=0 EndAngle=1.5708
    g22: GeomPoint [constr] X=-164.91 Y=-2.6 Z=0
    g23: ArcOfCircle CenterX=-167.285 CenterY=-8.225 CenterZ=0 NormalX=0 NormalY=0 NormalZ=1 AngleXU=0 Radius=2.375 StartAngle=4.71239 EndAngle=6.28319
    g24: GeomPoint [constr] X=-164.91 Y=-10.6 Z=0
    g25: ArcOfCircle CenterX=-167.535 CenterY=-8.225 CenterZ=0 NormalX=0 NormalY=0 NormalZ=1 AngleXU=0 Radius=2.375 StartAngle=3.14159 EndAngle=4.71239
    g26: GeomPoint [constr] X=-169.91 Y=-10.6 Z=0
    g27: LineSegment [constr] StartX=-181.6 StartY=1.12e-14 StartZ=0 EndX=-152.209 EndY=0 EndZ=0
    g28: LineSegment [constr] StartX=-181.6 StartY=1.12e-14 StartZ=0 EndX=-130.41 EndY=0 EndZ=0
    g29: LineSegment [constr] StartX=-152.209 StartY=0 StartZ=0 EndX=-152.209 EndY=6.95 EndZ=0
    g30: LineSegment [constr] StartX=-130.41 StartY=0 StartZ=0 EndX=-130.41 EndY=-6.95 EndZ=0
    g31: Circle CenterX=-152.209 CenterY=6.95 CenterZ=0 NormalX=0 NormalY=0 NormalZ=1 AngleXU=0 Radius=2.1
    g32: Circle CenterX=-130.41 CenterY=-6.95 CenterZ=0 NormalX=0 NormalY=0 NormalZ=1 AngleXU=0 Radius=2.1
  constraints (79):
    c: Distance(g0) = 11.69
    c: PointOnObject(g0,g-1)
    c: Coincident(g-4,g0)
    c: Distance(g1) = 2.6
    c: Coincident(g1,g0)
    c: Vertical(g1)
    c: Distance(g2) = 2.6
    c: Coincident(g2,g0)
    c: Vertical(g2)
    c: Distance(g18,g12) = 8
    c: Coincident(g18,g2)
    c: Vertical(g3)
    c: Distance(g14,g12) = 5
    c: Horizontal(g4)
    c: Distance(g16,g14) = 8
    c: Vertical(g5)
    c: Distance(g26,g20) = 8
    c: Coincident(g20,g1)
    c: Vertical(g7)
    c: Distance(g26,g24) = 5
    c: Horizontal(g8)
    c: Distance(g24,g22) = 8
    c: Vertical(g9)
    c: PointOnObject(g12,g3)
    c: PointOnObject(g12,g4)
    c: Tangent(g3,g11) = 1.5708
    c: Tangent(g4,g11) = 1.5708
    c: PointOnObject(g14,g5)
    c: PointOnObject(g14,g4)
    c: Tangent(g5,g13) = 1.5708
    c: Tangent(g4,g13) = 1.5708
    c: PointOnObject(g16,g5)
    c: PointOnObject(g16,g6)
    c: Tangent(g5,g15) = 1.5708
    c: Tangent(g6,g15) = 1.5708
    c: PointOnObject(g18,g3)
    c: PointOnObject(g18,g6)
    c: Tangent(g3,g17) = 1.5708
    c: Tangent(g6,g17) = 1.5708
    c: Equal(g11,g13)
    c: Equal(g13,g15)
    c: Equal(g15,g17)
    c: DistanceX(g4,g4) = 0.25
    c: PointOnObject(g20,g7)
    c: PointOnObject(g20,g10)
    c: Tangent(g7,g19) = -1.5708
    c: Tangent(g10,g19) = -1.5708
    c: PointOnObject(g22,g9)
    c: PointOnObject(g22,g10)
    c: Tangent(g9,g21) = -1.5708
    c: Tangent(g10,g21) = -1.5708
    c: PointOnObject(g24,g9)
    c: PointOnObject(g24,g8)
    c: Tangent(g9,g23) = -1.5708
    c: Tangent(g8,g23) = -1.5708
    c: PointOnObject(g26,g8)
    c: PointOnObject(g26,g7)
    c: Tangent(g8,g25) = -1.5708
    c: Tangent(g7,g25) = -1.5708
    c: Equal(g19,g21)
    c: Equal(g21,g23)
    c: Equal(g23,g25)
    c: DistanceX(g10,g10) = 0.25
    c: Distance(g27) = 29.391
    c: Coincident(g27,g0)
    c: PointOnObject(g27,g-1)
    c: Distance(g28) = 51.19
    c: Coincident(g28,g0)
    c: PointOnObject(g28,g-1)
    c: Distance(g29) = 6.95
    c: Coincident(g29,g27)
    c: Vertical(g29)
    c: Distance(g30) = 6.95
    c: Coincident(g30,g28)
    c: Vertical(g30)
    c: Diameter(g31) = 4.2
    c: Diameter(g32) = 4.2
    c: Coincident(g32,g30)
    c: Coincident(g31,g29)
FEATURE [Sketcher::SketchObject] Sketch031  label="fori inferiori switch pompa"
  ArcFitTolerance = 1e-06
  AttachmentSupport = -> [XY_Plane]
  ExternalGeometry = -> [Sketch]
  FullyConstrained = true
  MakeInternals = false
  MapMode = 5
  sketch-geometry (4):
    g0: LineSegment [constr] StartX=-57.2 StartY=1.9e-15 StartZ=0 EndX=-62.45 EndY=1.9e-15 EndZ=0
    g1: LineSegment [constr] StartX=-62.45 StartY=3.25 StartZ=0 EndX=-62.45 EndY=-3.25 EndZ=0
    g2: Circle CenterX=-62.45 CenterY=3.25 CenterZ=0 NormalX=0 NormalY=0 NormalZ=1 AngleXU=0 Radius=1.6
    g3: Circle CenterX=-62.45 CenterY=-3.25 CenterZ=0 NormalX=0 NormalY=0 NormalZ=1 AngleXU=0 Radius=1.6
  constraints (10):
    c: Distance(g0) = 5.25
    c: Coincident(g0,g-3)
    c: PointOnObject(g0,g-3)
    c: Vertical(g1)
    c: DistanceY(g1,g1) = 6.5
    c: Symmetric(g1,g1,g0)
    c: Diameter(g2) = 3.2
    c: Diameter(g3) = 3.2
    c: Coincident(g2,g1)
    c: Coincident(g3,g1)
FEATURE [Sketcher::SketchObject] Sketch032  label="spazio per PILA 18650"
  ArcFitTolerance = 1e-06
  AttachmentSupport = -> [XY_Plane]
  ExternalGeometry = -> [Sketch]
  FullyConstrained = true
  MakeInternals = false
  MapMode = 5
  sketch-geometry (2):
    g0: LineSegment [constr] StartX=-178.142 StartY=-1.74e-14 StartZ=0 EndX=-191.142 EndY=-1.83e-14 EndZ=0
    g1: Circle CenterX=-191.142 CenterY=-1.83e-14 CenterZ=0 NormalX=0 NormalY=0 NormalZ=1 AngleXU=0 Radius=10.5
  constraints (5):
    c: Distance(g0) = 13
    c: Coincident(g0,g-3)
    c: PointOnObject(g0,g-4)
    c: Diameter(g1) = 21
    c: Coincident(g1,g0)
FEATURE [Part::Extrusion] Extrude030  label="Extrude spazio per PILA 18650"
  Base = -> Sketch032
  Dir = (0,0,1)
  DirLink = -> Sketch [Edge45]
  DirMode = 2
  FaceMakerClass = Part::FaceMakerBullseye
  FaceMakerMode = 3
  LengthFwd = 76
  LengthRev = 0
  Placement = pos=(6,0,-72) rot=(0,0,1;0rad)
  Solid = true
  Symmetric = false
FEATURE [Sketcher::SketchObject] Sketch033  label="fermo per scheda micro"
  ArcFitTolerance = 1e-06
  AttachmentSupport = -> [XZ_Plane]
  ExternalGeometry = -> [Sketch]
  FullyConstrained = true
  MakeInternals = false
  MapMode = 5
  Placement = pos=(0,0,0) rot=(1,0,0;1.5708rad)
  sketch-geometry (12):
    g0: LineSegment StartX=-11.6 StartY=6 StartZ=0 EndX=-4 EndY=6 EndZ=0
    g1: LineSegment StartX=-4 StartY=6 StartZ=0 EndX=-4 EndY=36.4 EndZ=0
    g2: LineSegment StartX=-4 StartY=36.4 StartZ=0 EndX=-11.6 EndY=36.4 EndZ=0
    g3: LineSegment StartX=-11.6 StartY=36.4 StartZ=0 EndX=-11.6 EndY=6 EndZ=0
    g4: LineSegment StartX=-80.11 StartY=11.6 StartZ=0 EndX=-70.51 EndY=11.6 EndZ=0
    g5: LineSegment StartX=-70.51 StartY=11.6 StartZ=0 EndX=-70.51 EndY=6 EndZ=0
    g6: LineSegment StartX=-70.51 StartY=6 StartZ=0 EndX=-80.11 EndY=6 EndZ=0
    g7: LineSegment StartX=-80.11 StartY=6 StartZ=0 EndX=-80.11 EndY=11.6 EndZ=0
    g8: LineSegment StartX=-78.51 StartY=36.4 StartZ=0 EndX=-70.51 EndY=36.4 EndZ=0
    g9: LineSegment StartX=-70.51 StartY=36.4 StartZ=0 EndX=-70.51 EndY=30.8 EndZ=0
    g10: LineSegment StartX=-70.51 StartY=30.8 StartZ=0 EndX=-78.51 EndY=30.8 EndZ=0
    g11: LineSegment StartX=-78.51 StartY=30.8 StartZ=0 EndX=-78.51 EndY=36.4 EndZ=0
  constraints (33):
    c: Horizontal(g0)
    c: Coincident(g1,g0)
    c: Coincident(g2,g1)
    c: Horizontal(g2)
    c: Coincident(g3,g2)
    c: Coincident(g3,g0)
    c: Vertical(g3)
    c: DistanceX(g2,g2) = 7.6
    c: Coincident(g1,g-3)
    c: Coincident(g0,g-3)
    c: Horizontal(g4)
    c: Coincident(g5,g4)
    c: Vertical(g5)
    c: Coincident(g6,g5)
    c: Horizontal(g6)
    c: Coincident(g7,g6)
    c: Coincident(g7,g4)
    c: Vertical(g7)
    c: DistanceY(g5,g5) = 5.6
    c: DistanceX(g4,g4) = 9.6
    c: Coincident(g9,g8)
    c: Vertical(g9)
    c: Coincident(g10,g9)
    c: Horizontal(g10)
    c: Coincident(g11,g10)
    c: Coincident(g11,g8)
    c: Vertical(g11)
    c: DistanceY(g9,g9) = 5.6
    c: DistanceX(g10,g10) = 8
    c: Coincident(g4,g-4)
    c: DistanceX(g4,g10) = 1.6
    c: Horizontal(g8)
    c: DistanceY(g8,g1) = 0
FEATURE [Sketcher::SketchObject] Sketch034  label="buchi guida rail"
  ArcFitTolerance = 1e-06
  AttachmentSupport = -> [XY_Plane]
  ExternalGeometry = -> [Sketch]
  FullyConstrained = true
  MakeInternals = false
  MapMode = 5
  sketch-geometry (6):
    g0: LineSegment [constr] StartX=-100.8 StartY=9.1e-15 StartZ=0 EndX=-93.3 EndY=0 EndZ=0
    g1: LineSegment [constr] StartX=-93.3 StartY=0 StartZ=0 EndX=-73.3 EndY=0 EndZ=0
    g2: LineSegment [constr] StartX=-73.3 StartY=0 StartZ=0 EndX=-53.3 EndY=0 EndZ=0
    g3: Circle CenterX=-93.3 CenterY=0 CenterZ=0 NormalX=0 NormalY=0 NormalZ=1 AngleXU=0 Radius=2.5
    g4: Circle CenterX=-73.3 CenterY=0 CenterZ=0 NormalX=0 NormalY=0 NormalZ=1 AngleXU=0 Radius=2.5
    g5: Circle CenterX=-53.3 CenterY=0 CenterZ=0 NormalX=0 NormalY=0 NormalZ=1 AngleXU=0 Radius=2.5
  constraints (15):
    c: Distance(g0) = 7.5
    c: Coincident(g0,g-3)
    c: PointOnObject(g0,g-1)
    c: Distance(g1) = 20
    c: Coincident(g1,g0)
    c: PointOnObject(g1,g-1)
    c: Distance(g2) = 20
    c: Coincident(g2,g1)
    c: PointOnObject(g2,g-1)
    c: Diameter(g3) = 5
    c: Diameter(g4) = 5
    c: Diameter(g5) = 5
    c: Coincident(g3,g0)
    c: Coincident(g4,g1)
    c: Coincident(g5,g2)
FEATURE [Part::Extrusion] Extrude032  label="Extrude buchi guida rail"
  Base = -> Sketch034
  Dir = (0,0,1)
  DirMode = 2
  FaceMakerClass = Part::FaceMakerBullseye
  FaceMakerMode = 3
  LengthFwd = -6.2
  LengthRev = 0
  Placement = pos=(0,0,43.2) rot=(0,0,1;0rad)
  Solid = true
  Symmetric = false
FEATURE [Part::Extrusion] Extrude033  label="Extrude fori superiori per solenoide e oled001"
  Base = -> Sketch030
  Dir = (0,0,1)
  DirMode = 2
  FaceMakerClass = Part::FaceMakerBullseye
  FaceMakerMode = 3
  LengthFwd = -4.8
  LengthRev = 0
  Placement = pos=(0,0,41.2) rot=(0,0,1;0rad)
  Solid = true
  Symmetric = false
FEATURE [Part::Extrusion] Extrude034  label="Extrude fori sotto impugnatura001"
  Base = -> Sketch029
  Dir = (0,0,1)
  DirMode = 2
  FaceMakerClass = Part::FaceMakerBullseye
  FaceMakerMode = 3
  LengthFwd = 5
  LengthRev = 0
  Placement = pos=(0,0,-83) rot=(0,0,1;0rad)
  Solid = true
  Symmetric = false
FEATURE [Part::Extrusion] Extrude035  label="Extrude fori inferiori switch pompa001"
  Base = -> Sketch031
  Dir = (0,0,1)
  DirMode = 2
  FaceMakerClass = Part::FaceMakerBullseye
  FaceMakerMode = 3
  LengthFwd = 4
  LengthRev = 0
  Placement = pos=(0,0,-1.7) rot=(0,0,1;0rad)
  Solid = true
  Symmetric = false
FEATURE [Part::Extrusion] Extrude036  label="Extrude foro sotto posteriore M3x5x007"
  Base = -> Sketch027
  Dir = (0,0,1)
  DirMode = 2
  FaceMakerClass = Part::FaceMakerBullseye
  FaceMakerMode = 3
  LengthFwd = 6.2
  LengthRev = 0
  Placement = pos=(0,0,-9.6) rot=(0,0,1;0rad)
  Solid = true
  Symmetric = false
FEATURE [Part::Extrusion] Extrude037  label="Extrude foro sotto anteriore M3x5x007"
  Base = -> Sketch026
  Dir = (0,0,1)
  DirMode = 2
  FaceMakerClass = Part::FaceMakerBullseye
  FaceMakerMode = 3
  LengthFwd = 6.2
  LengthRev = 0
  Solid = true
  Symmetric = false
FEATURE [Sketcher::SketchObject] Sketch035  label="foro per fissaggio micro"
  ArcFitTolerance = 1e-06
  AttachmentSupport = -> [XZ_Plane]
  ExternalGeometry = -> [Sketch,Sketch033]
  FullyConstrained = true
  MakeInternals = false
  MapMode = 5
  Placement = pos=(0,0,0) rot=(1,0,0;1.5708rad)
  sketch-geometry (3):
    g0: Circle CenterX=-7.8 CenterY=21.2 CenterZ=0 NormalX=0 NormalY=0 NormalZ=1 AngleXU=0 Radius=1.6
    g1: GeomPoint [constr] X=-4 Y=21.2 Z=0
    g2: LineSegment [constr] StartX=-4 StartY=21.2 StartZ=0 EndX=-11.6 EndY=21.2 EndZ=0
  constraints (6):
    c: Diameter(g0) = 3.2
    c: Symmetric(g-3,g-3,g1)
    c: Coincident(g2,g1)
    c: Horizontal(g2)
    c: DistanceX(g-4,g2) = 0
    c: Symmetric(g2,g1,g0)
FEATURE [Part::Extrusion] Extrude038  label="Extrude foro per fissaggio micro"
  Base = -> Sketch035
  Dir = (0,-1,2e-16)
  DirMode = 2
  FaceMakerClass = Part::FaceMakerBullseye
  FaceMakerMode = 3
  LengthFwd = 3
  LengthRev = 0
  Placement = pos=(0,8.6,0) rot=(0,0,1;0rad)
  Solid = true
  Symmetric = false
FEATURE [Sketcher::SketchObject] Sketch036  label="supporto per alimentatore"
  ArcFitTolerance = 1e-06
  AttachmentSupport = -> [XZ_Plane]
  ExternalGeometry = -> [Sketch,Sketch016,Sketch022]
  FullyConstrained = true
  MakeInternals = false
  MapMode = 5
  Placement = pos=(0,0,0) rot=(1,0,0;1.5708rad)
  sketch-geometry (5):
    g0: LineSegment StartX=-211.843 StartY=-50.0944 StartZ=0 EndX=-211.843 EndY=-80.4316 EndZ=0
    g1: LineSegment StartX=-211.843 StartY=-50.0944 StartZ=0 EndX=-207.775 EndY=-41.3701 EndZ=0
    g2: LineSegment [constr] StartX=-209.443 StartY=-50.0944 StartZ=0 EndX=-209.443 EndY=-80.4316 EndZ=0
    g3: LineSegment StartX=-207.775 StartY=-41.3701 StartZ=0 EndX=-207.775 EndY=-80.4316 EndZ=0
    g4: LineSegment StartX=-211.843 StartY=-80.4316 StartZ=0 EndX=-207.775 EndY=-80.4316 EndZ=0
  constraints (15):
    c: Vertical(g0)
    c: Coincident(g1,g0)
    c: Vertical(g2)
    c: Tangent(g2,g-5)
    c: Coincident(g3,g1)
    c: Vertical(g3)
    c: DistanceY(g-3,g3) = -2
    c: Tangent(g1,g-8)
    c: DistanceY(g-3,g0) = -2
    c: Coincident(g4,g0)
    c: Coincident(g4,g3)
    c: Tangent(g0,g-6)
    c: DistanceY(g-3,g2) = -2
    c: DistanceY(g2,g0) = 0
    c: DistanceX(g-3,g3) = 6.8
FEATURE [Part::Extrusion] Extrude039  label="Extrude039 supporto alimentatore"
  Base = -> Sketch036
  Dir = (0,-1,2e-16)
  DirMode = 2
  FaceMakerClass = Part::FaceMakerBullseye
  FaceMakerMode = 3
  LengthFwd = 25.2
  LengthRev = 0
  Solid = true
  Symmetric = true
FEATURE [Sketcher::SketchObject] Sketch037  label="scavo per alimentatore"
  ArcFitTolerance = 1e-06
  AttachmentSupport = -> [XZ_Plane]
  ExternalGeometry = -> [Sketch036]
  FullyConstrained = true
  MakeInternals = false
  MapMode = 5
  Placement = pos=(0,0,0) rot=(1,0,0;1.5708rad)
  sketch-geometry (4):
    g0: LineSegment StartX=-209.575 StartY=-50.4316 StartZ=0 EndX=-209.575 EndY=-80.4316 EndZ=0
    g1: LineSegment StartX=-209.575 StartY=-50.4316 StartZ=0 EndX=-207.775 EndY=-50.4316 EndZ=0
    g2: LineSegment StartX=-207.775 StartY=-50.4316 StartZ=0 EndX=-207.775 EndY=-80.4316 EndZ=0
    g3: LineSegment StartX=-207.775 StartY=-80.4316 StartZ=0 EndX=-209.575 EndY=-80.4316 EndZ=0
  constraints (11):
    c: Vertical(g0)
    c: Coincident(g1,g0)
    c: Horizontal(g1)
    c: Coincident(g2,g1)
    c: Vertical(g2)
    c: Coincident(g3,g2)
    c: Coincident(g3,g0)
    c: Horizontal(g3)
    c: DistanceX(g1,g1) = 1.8
    c: Coincident(g2,g-3)
    c: DistanceY(g2,g2) = 30
FEATURE [Part::Extrusion] Extrude040  label="Extrude040 scavo alimentatore"
  Base = -> Sketch037
  Dir = (0,-1,2e-16)
  DirMode = 2
  FaceMakerClass = Part::FaceMakerBullseye
  FaceMakerMode = 3
  LengthFwd = 19.5
  LengthRev = 0
  Solid = true
  Symmetric = true
FEATURE [Part::Extrusion] Extrude031  label="Extrude fermo per scheda micro"
  Base = -> Sketch033
  Dir = (0,-1,2e-16)
  DirMode = 2
  FaceMakerClass = Part::FaceMakerBullseye
  FaceMakerMode = 3
  LengthFwd = 3
  LengthRev = 0
  Placement = pos=(0,8.6,0) rot=(0,0,1;0rad)
  Solid = true
  Symmetric = false
FEATURE [Sketcher::SketchObject] Sketch038  label="scavo driver solenoide"
  ArcFitTolerance = 1e-06
  AttachmentSupport = -> [XZ_Plane]
  ExternalGeometry = -> [Sketch,Sketch036]
  FullyConstrained = true
  MakeInternals = false
  MapMode = 5
  Placement = pos=(0,0,0) rot=(1,0,0;1.5708rad)
  sketch-geometry (7):
    g0: LineSegment StartX=-192.222 StartY=-8.0175 StartZ=0 EndX=-194.941 EndY=-6.74965 EndZ=0
    g1: LineSegment StartX=-194.941 StartY=-6.74965 StartZ=0 EndX=-212.269 EndY=-43.9083 EndZ=0
    g2: LineSegment StartX=-192.222 StartY=-8.0175 StartZ=0 EndX=-188.779 EndY=-9.62345 EndZ=0
    g3: LineSegment StartX=-188.779 StartY=-9.62345 StartZ=0 EndX=-205.357 EndY=-45.1761 EndZ=0
    g4: LineSegment StartX=-205.357 StartY=-45.1761 StartZ=0 EndX=-209.55 EndY=-45.1761 EndZ=0
    g5: LineSegment [constr] StartX=-212.269 StartY=-43.9083 StartZ=0 EndX=-209.55 EndY=-45.1761 EndZ=0
    g6: LineSegment StartX=-212.269 StartY=-43.9083 StartZ=0 EndX=-209.55 EndY=-45.1761 EndZ=0
  constraints (20):
    c: Coincident(g1,g0)
    c: Coincident(g3,g2)
    c: Coincident(g4,g3)
    c: Distance(g2) = 3.8
    c: Distance(g1) = 41
    c: Coincident(g5,g1)
    c: Distance(g5) = 3
    c: Perpendicular(g5,g-3)
    c: Parallel(g1,g-3)
    c: Perpendicular(g1,g0)
    c: Distance(g0) = 3
    c: Coincident(g6,g1)
    c: Parallel(g3,g-3)
    c: Perpendicular(g2,g3)
    c: Coincident(g2,g0)
    c: Perpendicular(g-4,g4)
    c: PointOnObject(g5,g-3)
    c: Distance(g-3,g5) = 9.6
    c: Coincident(g4,g5)
    c: Coincident(g6,g4)
FEATURE [Part::Extrusion] Extrude041  label="Extrude scavo driver solenoide"
  Base = -> Sketch038
  Dir = (0,-1,2e-16)
  DirMode = 2
  FaceMakerClass = Part::FaceMakerBullseye
  FaceMakerMode = 3
  LengthFwd = 20.6
  LengthRev = 0
  Solid = true
  Symmetric = true
FEATURE [Sketcher::SketchObject] Sketch039  label="scavo per cavo usb per micro"
  ArcFitTolerance = 1e-06
  AttachmentSupport = -> [XZ_Plane]
  ExternalGeometry = -> [Sketch,Sketch016]
  FullyConstrained = true
  MakeInternals = false
  MapMode = 5
  Placement = pos=(0,0,0) rot=(1,0,0;1.5708rad)
  sketch-geometry (4):
    g0: LineSegment StartX=-82.51 StartY=36.4 StartZ=0 EndX=-74.51 EndY=36.4 EndZ=0
    g1: LineSegment StartX=-74.51 StartY=36.4 StartZ=0 EndX=-74.51 EndY=30.8 EndZ=0
    g2: LineSegment StartX=-74.51 StartY=30.8 StartZ=0 EndX=-82.51 EndY=30.8 EndZ=0
    g3: LineSegment StartX=-82.51 StartY=30.8 StartZ=0 EndX=-82.51 EndY=36.4 EndZ=0
  constraints (11):
    c: Coincident(g1,g0)
    c: Vertical(g1)
    c: Coincident(g2,g1)
    c: Horizontal(g2)
    c: Coincident(g3,g2)
    c: Coincident(g3,g0)
    c: Vertical(g3)
    c: Tangent(g0,g-3)
    c: Tangent(g2,g-4)
    c: Tangent(g3,g-4)
    c: Tangent(g1,g-4)
FEATURE [Part::Extrusion] Extrude042  label="Extrude scavo per cavo usb per micro"
  Base = -> Sketch039
  Dir = (0,-1,2e-16)
  DirMode = 2
  FaceMakerClass = Part::FaceMakerBullseye
  FaceMakerMode = 3
  LengthFwd = 11.2
  LengthRev = 0
  Solid = true
  Symmetric = true
FEATURE [Sketcher::SketchObject] Sketch040  label="scavo saldature alimentatore connettore 5v"
  ArcFitTolerance = 1e-06
  AttachmentSupport = -> [XZ_Plane]
  ExternalGeometry = -> [Sketch037]
  FullyConstrained = true
  MakeInternals = false
  MapMode = 5
  Placement = pos=(0,0,0) rot=(1,0,0;1.5708rad)
  sketch-geometry (4):
    g0: LineSegment StartX=-211.175 StartY=-52.4316 StartZ=0 EndX=-211.175 EndY=-56.4316 EndZ=0
    g1: LineSegment StartX=-211.175 StartY=-52.4316 StartZ=0 EndX=-209.575 EndY=-52.4316 EndZ=0
    g2: LineSegment StartX=-209.575 StartY=-52.4316 StartZ=0 EndX=-209.575 EndY=-56.4316 EndZ=0
    g3: LineSegment StartX=-209.575 StartY=-56.4316 StartZ=0 EndX=-211.175 EndY=-56.4316 EndZ=0
  constraints (11):
    c: Vertical(g0)
    c: Coincident(g1,g0)
    c: Horizontal(g1)
    c: Coincident(g2,g1)
    c: Coincident(g3,g2)
    c: Coincident(g3,g0)
    c: Horizontal(g3)
    c: DistanceX(g1,g1) = 1.6
    c: DistanceY(g2,g2) = 4
    c: Tangent(g2,g-3)
    c: DistanceY(g1,g-3) = 2
FEATURE [Part::Extrusion] Extrude043  label="Extrude scavo saldature alimentatore connettore 5v"
  Base = -> Sketch040
  Dir = (0,-1,2e-16)
  DirMode = 2
  FaceMakerClass = Part::FaceMakerBullseye
  FaceMakerMode = 3
  LengthFwd = 8
  LengthRev = 0
  Solid = true
  Symmetric = true
FEATURE [Sketcher::SketchObject] Sketch041  label="scavo saldature alimentatore connettore 5v verticali"
  ArcFitTolerance = 1e-06
  AttachmentSupport = -> [XZ_Plane]
  ExternalGeometry = -> [Sketch037]
  FullyConstrained = true
  MakeInternals = false
  MapMode = 5
  Placement = pos=(0,0,0) rot=(1,0,0;1.5708rad)
  sketch-geometry (4):
    g0: LineSegment StartX=-211.175 StartY=-53.6316 StartZ=0 EndX=-209.575 EndY=-53.6316 EndZ=0
    g1: LineSegment StartX=-209.575 StartY=-53.6316 StartZ=0 EndX=-209.575 EndY=-76.6316 EndZ=0
    g2: LineSegment StartX=-209.575 StartY=-76.6316 StartZ=0 EndX=-211.175 EndY=-76.6316 EndZ=0
    g3: LineSegment StartX=-211.175 StartY=-76.6316 StartZ=0 EndX=-211.175 EndY=-53.6316 EndZ=0
  constraints (11):
    c: Horizontal(g0)
    c: Coincident(g1,g0)
    c: Coincident(g2,g1)
    c: Horizontal(g2)
    c: Coincident(g3,g2)
    c: Coincident(g3,g0)
    c: Vertical(g3)
    c: DistanceY(g3,g3) = 23
    c: DistanceX(g0,g0) = 1.6
    c: Tangent(g1,g-3)
    c: DistanceY(g0,g-3) = 3.2
FEATURE [Part::Extrusion] Extrude044  label="Extrude scavo saldature alimentatore connettore 5v verticali"
  Base = -> Sketch041
  Dir = (0,-1,2e-16)
  DirMode = 2
  FaceMakerClass = Part::FaceMakerBullseye
  FaceMakerMode = 3
  LengthFwd = 3.2
  LengthRev = 0
  Placement = pos=(0,8.3,0) rot=(0,0,1;0rad)
  Solid = true
  Symmetric = false
FEATURE [Sketcher::SketchObject] Sketch042  label="fermi per driver solenoide e alimentatore"
  ArcFitTolerance = 1e-06
  AttachmentSupport = -> [XZ_Plane]
  ExternalGeometry = -> [Sketch036,Sketch037,Sketch,Sketch038]
  FullyConstrained = true
  MakeInternals = false
  MapMode = 5
  Placement = pos=(0,0,0) rot=(1,0,0;1.5708rad)
  sketch-geometry (27):
    g0: LineSegment StartX=-200.506 StartY=-25.7811 StartZ=0 EndX=-201.436 EndY=-27.775 EndZ=0
    g1: LineSegment StartX=-201.436 StartY=-27.775 StartZ=0 EndX=-199.442 EndY=-28.7048 EndZ=0
    g2: LineSegment StartX=-199.442 StartY=-28.7048 StartZ=0 EndX=-198.512 EndY=-26.7109 EndZ=0
    g3: LineSegment StartX=-198.512 StartY=-26.7109 StartZ=0 EndX=-200.506 EndY=-25.7811 EndZ=0
    g4: LineSegment StartX=-201.28 StartY=-23.6549 StartZ=0 EndX=-203.562 EndY=-28.5489 EndZ=0
    g5: LineSegment StartX=-203.562 StartY=-28.5489 StartZ=0 EndX=-200.118 EndY=-30.1549 EndZ=0
    g6: LineSegment StartX=-197.992 StartY=-29.381 StartZ=0 EndX=-197.062 EndY=-27.3871 EndZ=0
    g7: LineSegment StartX=-197.836 StartY=-25.2608 StartZ=0 EndX=-201.28 EndY=-23.6549 EndZ=0
    g8: LineSegment [constr] StartX=-198.668 StartY=-30.8311 StartZ=0 EndX=-197.992 EndY=-29.381 EndZ=0
    g9: LineSegment [constr] StartX=-198.668 StartY=-30.8311 StartZ=0 EndX=-200.118 EndY=-30.1549 EndZ=0
    g10: ArcOfCircle CenterX=-198.512 CenterY=-26.7109 CenterZ=0 NormalX=0 NormalY=0 NormalZ=1 AngleXU=0 Radius=1.6 StartAngle=5.84685 EndAngle=7.41765
    g11: GeomPoint [constr] X=-196.386 Y=-25.937 Z=0
    g12: ArcOfCircle CenterX=-199.442 CenterY=-28.7048 CenterZ=0 NormalX=0 NormalY=0 NormalZ=1 AngleXU=0 Radius=1.6 StartAngle=4.27606 EndAngle=5.84685
    g13: GeomPoint [constr] X=-198.668 Y=-30.8311 Z=0
    g14: LineSegment StartX=-207.775 StartY=-46.8316 StartZ=0 EndX=-207.775 EndY=-50.8316 EndZ=0
    g15: LineSegment StartX=-207.775 StartY=-46.8316 StartZ=0 EndX=-203.775 EndY=-46.8316 EndZ=0
    g16: LineSegment StartX=-203.775 StartY=-46.8316 StartZ=0 EndX=-203.775 EndY=-50.8316 EndZ=0
    g17: LineSegment StartX=-207.775 StartY=-50.8316 StartZ=0 EndX=-203.775 EndY=-50.8316 EndZ=0
    g18: LineSegment StartX=-209.375 StartY=-52.4316 StartZ=0 EndX=-203.775 EndY=-52.4316 EndZ=0
    g19: LineSegment StartX=-202.175 StartY=-50.8316 StartZ=0 EndX=-202.175 EndY=-46.8316 EndZ=0
    g20: LineSegment StartX=-203.775 StartY=-45.2316 StartZ=0 EndX=-209.375 EndY=-45.2316 EndZ=0
    g21: LineSegment StartX=-209.375 StartY=-45.2316 StartZ=0 EndX=-209.375 EndY=-52.4316 EndZ=0
    g22: ArcOfCircle CenterX=-203.775 CenterY=-46.8316 CenterZ=0 NormalX=0 NormalY=0 NormalZ=1 AngleXU=0 Radius=1.6 StartAngle=1.8e-15 EndAngle=1.5708
    g23: GeomPoint [constr] X=-202.175 Y=-45.2316 Z=0
    g24: ArcOfCircle CenterX=-203.775 CenterY=-50.8316 CenterZ=0 NormalX=0 NormalY=0 NormalZ=1 AngleXU=0 Radius=1.6 StartAngle=4.71239 EndAngle=6.28319
    g25: GeomPoint [constr] X=-202.175 Y=-52.4316 Z=0
    g26: LineSegment [constr] StartX=-207.775 StartY=-50.4316 StartZ=0 EndX=-207.775 EndY=-50.8316 EndZ=0
  constraints (69):
    c: Coincident(g1,g0)
    c: Coincident(g2,g1)
    c: Coincident(g3,g2)
    c: Coincident(g3,g0)
    c: Parallel(g0,g2)
    c: Perpendicular(g3,g0)
    c: Perpendicular(g1,g0)
    c: Coincident(g5,g4)
    c: Coincident(g7,g4)
    c: Distance(g3) = 2.2
    c: Distance(g2) = 2.2
    c: Parallel(g6,g2)
    c: Parallel(g6,g4)
    c: Perpendicular(g5,g6)
    c: Perpendicular(g7,g6)
    c: Distance(g13,g11) = 5.4
    c: Distance(g5,g13) = 5.4
    c: Coincident(g9,g8)
    c: Distance(g8) = 1.6
    c: Distance(g9) = 1.6
    c: Perpendicular(g9,g8)
    c: Parallel(g8,g6)
    c: Coincident(g8,g13)
    c: Distance(g8,g1) = 1.6
    c: Distance(g9,g1) = 1.6
    c: Tangent(g0,g-5)
    c: Distance(g0,g-6) = 19.2
    c: PointOnObject(g11,g7)
    c: PointOnObject(g11,g6)
    c: Tangent(g7,g10) = -1.5708
    c: Tangent(g6,g10) = -1.5708
    c: PointOnObject(g13,g5)
    c: Tangent(g5,g12) = -1.5708
    c: Tangent(g6,g12) = -1.5708
    c: Equal(g10,g12)
    c: Coincident(g10,g2)
    c: Vertical(g14)
    c: Coincident(g15,g14)
    c: Horizontal(g15)
    c: Coincident(g16,g15)
    c: Vertical(g16)
    c: Coincident(g17,g14)
    c: Coincident(g17,g16)
    c: Horizontal(g17)
    c: Distance(g16) = 4
    c: Distance(g15) = 4
    c: Horizontal(g18)
    c: Vertical(g19)
    c: Horizontal(g20)
    c: Coincident(g21,g20)
    c: Coincident(g21,g18)
    c: Vertical(g21)
    c: Distance(g20,g23) = 7.2
    c: Distance(g25,g23) = 7.2
    c: DistanceY(g18,g14) = 1.6
    c: DistanceX(g18,g14) = 1.6
    c: PointOnObject(g23,g20)
    c: PointOnObject(g23,g19)
    c: Tangent(g20,g22) = -1.5708
    c: Tangent(g19,g22) = -1.5708
    c: PointOnObject(g25,g19)
    c: Tangent(g18,g24) = -1.5708
    c: Tangent(g19,g24) = -1.5708
    c: Equal(g22,g24)
    c: Coincident(g22,g15)
    c: Vertical(g26)
    c: Distance(g26) = 0.4
    c: Coincident(g26,g-4)
    c: Coincident(g14,g26)
FEATURE [Part::Extrusion] Extrude045  label="Extrude fermi per driver solenoide e alimentatore"
  Base = -> Sketch042
  Dir = (0,-1,2e-16)
  DirMode = 2
  FaceMakerClass = Part::FaceMakerBullseye
  FaceMakerMode = 3
  LengthFwd = 25.2
  LengthRev = 0
  Solid = true
  Symmetric = true
FEATURE [Sketcher::SketchObject] Sketch043  label="scavo pulizia fermo alimentatore"
  ArcFitTolerance = 1e-06
  AttachmentSupport = -> [XZ_Plane]
  ExternalGeometry = -> [Sketch042,Sketch036,Sketch037]
  FullyConstrained = true
  MakeInternals = false
  MapMode = 5
  Placement = pos=(0,0,0) rot=(1,0,0;1.5708rad)
  sketch-geometry (6):
    g0: LineSegment StartX=-209.375 StartY=-52.4316 StartZ=0 EndX=-209.375 EndY=-50.4316 EndZ=0
    g1: LineSegment StartX=-209.375 StartY=-50.4316 StartZ=0 EndX=-207.775 EndY=-50.4316 EndZ=0
    g2: LineSegment StartX=-207.775 StartY=-50.4316 StartZ=0 EndX=-207.775 EndY=-45.2316 EndZ=0
    g3: LineSegment StartX=-207.775 StartY=-45.2316 StartZ=0 EndX=-202.175 EndY=-45.2316 EndZ=0
    g4: LineSegment StartX=-202.175 StartY=-45.2316 StartZ=0 EndX=-202.175 EndY=-52.4316 EndZ=0
    g5: LineSegment StartX=-202.175 StartY=-52.4316 StartZ=0 EndX=-209.375 EndY=-52.4316 EndZ=0
  constraints (13):
    c: Vertical(g0)
    c: Coincident(g1,g0)
    c: Coincident(g2,g1)
    c: Coincident(g3,g2)
    c: Coincident(g4,g3)
    c: Coincident(g5,g4)
    c: Coincident(g5,g0)
    c: Horizontal(g5)
    c: Coincident(g0,g-6)
    c: Tangent(g1,g-8)
    c: Tangent(g2,g-4)
    c: Tangent(g3,g-7)
    c: Tangent(g4,g-3)
FEATURE [Part::Extrusion] Extrude046  label="Extrude scavo pulizia fermo alimentatore"
  Base = -> Sketch043
  Dir = (0,-1,2e-16)
  DirMode = 2
  FaceMakerClass = Part::FaceMakerBullseye
  FaceMakerMode = 3
  LengthFwd = 19.5
  LengthRev = 0
  Solid = true
  Symmetric = true
FEATURE [Sketcher::SketchObject] Sketch044  label="buchini per fissaggio oled"
  ArcFitTolerance = 1e-06
  AttachmentSupport = -> [YZ_Plane]
  ExternalGeometry = -> [Sketch]
  FullyConstrained = true
  MakeInternals = false
  MapMode = 5
  Placement = pos=(0,0,0) rot=(0.57735,0.57735,0.57735;2.0944rad)
  sketch-geometry (5):
    g0: LineSegment [constr] StartX=1.5e-14 StartY=67.3588 StartZ=0 EndX=0 EndY=64.3588 EndZ=0
    g1: LineSegment [constr] StartX=0 StartY=64.3588 StartZ=0 EndX=10.4 EndY=64.3588 EndZ=0
    g2: LineSegment [constr] StartX=0 StartY=64.3588 StartZ=0 EndX=-10.4 EndY=64.3588 EndZ=0
    g3: Circle CenterX=10.4 CenterY=64.3588 CenterZ=0 NormalX=0 NormalY=0 NormalZ=1 AngleXU=0 Radius=1.5
    g4: Circle CenterX=-10.4 CenterY=64.3588 CenterZ=0 NormalX=0 NormalY=0 NormalZ=1 AngleXU=0 Radius=1.5
  constraints (13):
    c: Distance(g0) = 3
    c: PointOnObject(g0,g-2)
    c: Coincident(g1,g0)
    c: Horizontal(g1)
    c: Coincident(g2,g0)
    c: Horizontal(g2)
    c: DistanceX(g1,g1) = 10.4
    c: Coincident(g3,g1)
    c: Diameter(g4) = 3
    c: Coincident(g4,g2)
    c: Coincident(g0,g-7)
    c: Equal(g1,g2)
    c: Equal(g4,g3)
FEATURE [Part::Extrusion] Extrude047  label="Extrude buchini per fissaggio oled"
  Base = -> Sketch044
  Dir = (1,0,0)
  DirMode = 2
  FaceMakerClass = Part::FaceMakerBullseye
  FaceMakerMode = 3
  LengthFwd = 10
  LengthRev = 0
  Placement = pos=(-186,0,0) rot=(0,0,1;0rad)
  Solid = true
  Symmetric = false
FEATURE [Sketcher::SketchObject] Sketch046  label="scavo 5x5 neopixel"
  ArcFitTolerance = 1e-06
  AttachmentSupport = -> [YZ_Plane002]
  FullyConstrained = true
  MakeInternals = false
  MapMode = 5
  Placement = pos=(0,0,0) rot=(0.57735,0.57735,0.57735;2.0944rad)
  sketch-geometry (4):
    g0: LineSegment StartX=-2.7 StartY=2.7 StartZ=0 EndX=2.7 EndY=2.7 EndZ=0
    g1: LineSegment StartX=2.7 StartY=2.7 StartZ=0 EndX=2.7 EndY=-2.7 EndZ=0
    g2: LineSegment StartX=2.7 StartY=-2.7 StartZ=0 EndX=-2.7 EndY=-2.7 EndZ=0
    g3: LineSegment StartX=-2.7 StartY=-2.7 StartZ=0 EndX=-2.7 EndY=2.7 EndZ=0
  constraints (11):
    c: Horizontal(g0)
    c: Coincident(g1,g0)
    c: Vertical(g1)
    c: Coincident(g2,g1)
    c: Horizontal(g2)
    c: Coincident(g3,g2)
    c: Coincident(g3,g0)
    c: Vertical(g3)
    c: DistanceX(g0,g0) = 5.4
    c: DistanceY(g1,g1) = 5.4
    c: Symmetric(g0,g1,g-1)
FEATURE [Sketcher::SketchObject] Sketch047  label="scavo 10x10 neopixel corpo"
  ArcFitTolerance = 1e-06
  AttachmentOffset = pos=(0,0,1) rot=(0,0,1;0rad)
  AttachmentSupport = -> [YZ_Plane002]
  FullyConstrained = true
  MakeInternals = false
  MapMode = 5
  Placement = pos=(1,0,0) rot=(0.57735,0.57735,0.57735;2.0944rad)
  sketch-geometry (4):
    g0: LineSegment StartX=-5 StartY=5.1 StartZ=0 EndX=5 EndY=5.1 EndZ=0
    g1: LineSegment StartX=5 StartY=5.1 StartZ=0 EndX=5 EndY=-5.1 EndZ=0
    g2: LineSegment StartX=5 StartY=-5.1 StartZ=0 EndX=-5 EndY=-5.1 EndZ=0
    g3: LineSegment StartX=-5 StartY=-5.1 StartZ=0 EndX=-5 EndY=5.1 EndZ=0
  constraints (11):
    c: Horizontal(g0)
    c: Coincident(g1,g0)
    c: Vertical(g1)
    c: Coincident(g2,g1)
    c: Horizontal(g2)
    c: Coincident(g3,g2)
    c: Coincident(g3,g0)
    c: Vertical(g3)
    c: DistanceX(g0,g0) = 10
    c: DistanceY(g1,g1) = 10.2
    c: Symmetric(g0,g2,g-1)
FEATURE [Sketcher::SketchObject] Sketch048  label="buco per perno blocco neopixel"
  ArcFitTolerance = 1e-06
  AttachmentSupport = -> [XZ_Plane002]
  FullyConstrained = true
  MakeInternals = false
  MapMode = 5
  Placement = pos=(0,0,0) rot=(1,0,0;1.5708rad)
  sketch-geometry (4):
    g0: LineSegment StartX=3 StartY=1.2 StartZ=0 EndX=3 EndY=-1.2 EndZ=0
    g1: LineSegment StartX=3 StartY=-1.2 StartZ=0 EndX=5.4 EndY=-1.2 EndZ=0
    g2: LineSegment StartX=5.4 StartY=-1.2 StartZ=0 EndX=5.4 EndY=1.2 EndZ=0
    g3: LineSegment StartX=5.4 StartY=1.2 StartZ=0 EndX=3 EndY=1.2 EndZ=0
  constraints (11):
    c: Coincident(g1,g0)
    c: Horizontal(g1)
    c: Coincident(g2,g1)
    c: Vertical(g2)
    c: Coincident(g3,g2)
    c: Coincident(g3,g0)
    c: Horizontal(g3)
    c: DistanceX(g1,g1) = 2.4
    c: DistanceY(g2,g2) = 2.4
    c: Symmetric(g0,g0,g-1)
    c: DistanceX(g-1,g0) = 3
FEATURE [Sketcher::SketchObject] Sketch045  label="blocco principale per neopixel"
  ArcFitTolerance = 1e-06
  AttachmentSupport = -> [XZ_Plane002]
  ExternalGeometry = -> [Sketch048]
  FullyConstrained = true
  MakeInternals = false
  MapMode = 5
  Placement = pos=(0,0,0) rot=(1,0,0;1.5708rad)
  sketch-geometry (6):
    g0: LineSegment StartX=0 StartY=5.1 StartZ=0 EndX=0 EndY=-5.1 EndZ=0
    g1: LineSegment StartX=0 StartY=-5.1 StartZ=0 EndX=3 EndY=-5.1 EndZ=0
    g2: LineSegment StartX=7 StartY=-1.1 StartZ=0 EndX=7 EndY=5.1 EndZ=0
    g3: LineSegment StartX=7 StartY=5.1 StartZ=0 EndX=0 EndY=5.1 EndZ=0
    g4: ArcOfCircle CenterX=3 CenterY=-1.1 CenterZ=0 NormalX=0 NormalY=0 NormalZ=1 AngleXU=0 Radius=4 StartAngle=4.71239 EndAngle=6.28319
    g5: GeomPoint [constr] X=7 Y=-5.1 Z=0
  constraints (15):
    c: Vertical(g0)
    c: Coincident(g1,g0)
    c: Horizontal(g1)
    c: Vertical(g2)
    c: Coincident(g3,g2)
    c: Coincident(g3,g0)
    c: Horizontal(g3)
    c: DistanceY(g0,g0) = 10.2
    c: Symmetric(g0,g0,g-1)
    c: DistanceX(g3,g3) = 7
    c: PointOnObject(g5,g2)
    c: PointOnObject(g5,g1)
    c: Tangent(g2,g4) = -1.5708
    c: Tangent(g1,g4) = -1.5708
    c: DistanceX(g-3,g1) = 0
FEATURE [Sketcher::SketchObject] Sketch049  label="rinforzi esterni per corpo neopoixel"
  ArcFitTolerance = 1e-06
  AttachmentSupport = -> [XZ_Plane002]
  ExternalGeometry = -> [Sketch045]
  FullyConstrained = true
  MakeInternals = false
  MapMode = 5
  Placement = pos=(0,0,0) rot=(1,0,0;1.5708rad)
  sketch-geometry (8):
    g0: LineSegment StartX=1 StartY=-4.1 StartZ=0 EndX=2 EndY=-4.1 EndZ=0
    g1: LineSegment StartX=2 StartY=-4.1 StartZ=0 EndX=2 EndY=-5.1 EndZ=0
    g2: LineSegment StartX=2 StartY=-5.1 StartZ=0 EndX=1 EndY=-5.1 EndZ=0
    g3: LineSegment StartX=1 StartY=-5.1 StartZ=0 EndX=1 EndY=-4.1 EndZ=0
    g4: LineSegment StartX=1 StartY=5.1 StartZ=0 EndX=2 EndY=5.1 EndZ=0
    g5: LineSegment StartX=2 StartY=5.1 StartZ=0 EndX=2 EndY=4.1 EndZ=0
    g6: LineSegment StartX=2 StartY=4.1 StartZ=0 EndX=1 EndY=4.1 EndZ=0
    g7: LineSegment StartX=1 StartY=4.1 StartZ=0 EndX=1 EndY=5.1 EndZ=0
  constraints (24):
    c: Horizontal(g0)
    c: Coincident(g1,g0)
    c: Vertical(g1)
    c: Coincident(g2,g1)
    c: Horizontal(g2)
    c: Coincident(g3,g2)
    c: Coincident(g3,g0)
    c: Vertical(g3)
    c: Horizontal(g4)
    c: Coincident(g5,g4)
    c: Vertical(g5)
    c: Coincident(g6,g5)
    c: Horizontal(g6)
    c: Coincident(g7,g6)
    c: Coincident(g7,g4)
    c: Vertical(g7)
    c: DistanceX(g4,g4) = 1
    c: DistanceY(g5,g5) = 1
    c: DistanceX(g0,g0) = 1
    c: DistanceY(g1,g1) = 1
    c: DistanceX(g-3,g4) = 1
    c: DistanceY(g-3,g4) = 0
    c: DistanceX(g-4,g2) = 1
    c: DistanceY(g2,g-4) = 0
FEATURE [Sketcher::SketchObject] Sketch052  label="scavo saldature driver solenoide"
  ArcFitTolerance = 1e-06
  AttachmentSupport = -> [XZ_Plane]
  ExternalGeometry = -> [Sketch038]
  FullyConstrained = true
  MakeInternals = false
  MapMode = 5
  Placement = pos=(0,0,0) rot=(1,0,0;1.5708rad)
  sketch-geometry (4):
    g0: LineSegment StartX=-195.304 StartY=-6.5806 StartZ=0 EndX=-196.994 EndY=-10.2058 EndZ=0
    g1: LineSegment StartX=-196.994 StartY=-10.2058 StartZ=0 EndX=-196.632 EndY=-10.3749 EndZ=0
    g2: LineSegment StartX=-196.632 StartY=-10.3749 StartZ=0 EndX=-194.941 EndY=-6.74965 EndZ=0
    g3: LineSegment StartX=-194.941 StartY=-6.74965 StartZ=0 EndX=-195.304 EndY=-6.5806 EndZ=0
  constraints (11):
    c: Coincident(g1,g0)
    c: Coincident(g2,g1)
    c: Coincident(g3,g2)
    c: Coincident(g3,g0)
    c: Parallel(g2,g0)
    c: Perpendicular(g2,g3)
    c: Perpendicular(g1,g2,g1) = 1.5708
    c: Parallel(g2,g-3)
    c: Distance(g2) = 4
    c: Distance(g3) = 0.4
    c: Coincident(g2,g-3)
FEATURE [Part::Extrusion] Extrude055  label="Extrude scavo saldature driver solenoide"
  Base = -> Sketch052
  Dir = (0,-1,2e-16)
  DirMode = 2
  FaceMakerClass = Part::FaceMakerBullseye
  FaceMakerMode = 3
  LengthFwd = 6
  LengthRev = 0
  Solid = true
  Symmetric = true
FEATURE [Sketcher::SketchObject] Sketch053  label="scavo saldature rumble"
  ArcFitTolerance = 1e-06
  AttachmentSupport = -> [XZ_Plane]
  ExternalGeometry = -> [Sketch019]
  FullyConstrained = true
  MakeInternals = false
  MapMode = 5
  Placement = pos=(0,0,0) rot=(1,0,0;1.5708rad)
  sketch-geometry (4):
    g0: LineSegment StartX=-172.866 StartY=-57.0139 StartZ=0 EndX=-174.102 EndY=-60.8181 EndZ=0
    g1: LineSegment StartX=-174.102 StartY=-60.8181 StartZ=0 EndX=-175.243 EndY=-60.4473 EndZ=0
    g2: LineSegment StartX=-175.243 StartY=-60.4473 StartZ=0 EndX=-174.007 EndY=-56.6431 EndZ=0
    g3: LineSegment StartX=-174.007 StartY=-56.6431 StartZ=0 EndX=-172.866 EndY=-57.0139 EndZ=0
  constraints (11):
    c: Coincident(g1,g0)
    c: Coincident(g2,g1)
    c: Coincident(g3,g2)
    c: Coincident(g3,g0)
    c: Parallel(g0,g2)
    c: Perpendicular(g3,g0)
    c: Perpendicular(g1,g0)
    c: Parallel(g0,g-3)
    c: Distance(g0) = 4
    c: Distance(g1) = 1.2
    c: Coincident(g0,g-3)
FEATURE [Part::Extrusion] Extrude056  label="Extrude scavo saldature rumble"
  Base = -> Sketch053
  Dir = (0,-1,2e-16)
  DirMode = 2
  FaceMakerClass = Part::FaceMakerBullseye
  FaceMakerMode = 3
  LengthFwd = 8.4
  LengthRev = 0
  Solid = true
  Symmetric = true
FEATURE [Sketcher::SketchObject] Sketch054  label="scavo saldature alimentatore connettore USB"
  ArcFitTolerance = 1e-06
  AttachmentSupport = -> [XZ_Plane]
  ExternalGeometry = -> [Sketch037]
  FullyConstrained = true
  MakeInternals = false
  MapMode = 5
  Placement = pos=(0,0,0) rot=(1,0,0;1.5708rad)
  sketch-geometry (4):
    g0: LineSegment StartX=-209.575 StartY=-80.4316 StartZ=0 EndX=-210.375 EndY=-80.4316 EndZ=0
    g1: LineSegment StartX=-210.375 StartY=-80.4316 StartZ=0 EndX=-210.375 EndY=-72.4316 EndZ=0
    g2: LineSegment StartX=-210.375 StartY=-72.4316 StartZ=0 EndX=-209.575 EndY=-72.4316 EndZ=0
    g3: LineSegment StartX=-209.575 StartY=-72.4316 StartZ=0 EndX=-209.575 EndY=-80.4316 EndZ=0
  constraints (11):
    c: Horizontal(g0)
    c: Coincident(g1,g0)
    c: Vertical(g1)
    c: Coincident(g2,g1)
    c: Horizontal(g2)
    c: Coincident(g3,g2)
    c: Coincident(g3,g0)
    c: Vertical(g3)
    c: DistanceX(g0,g0) = 0.8
    c: DistanceY(g3,g3) = 8
    c: Coincident(g0,g-4)
FEATURE [Part::Extrusion] Extrude057  label="Extrude scavo saldature alimentatore connettore USB"
  Base = -> Sketch054
  Dir = (0,-1,2e-16)
  DirMode = 2
  FaceMakerClass = Part::FaceMakerBullseye
  FaceMakerMode = 3
  LengthFwd = 11
  LengthRev = 0
  Solid = true
  Symmetric = true
FEATURE [Sketcher::SketchObject] Sketch055  label="buco interno per micro switch"
  ArcFitTolerance = 1e-06
  AttachmentSupport = -> [XZ_Plane]
  ExternalGeometry = -> [Sketch]
  FullyConstrained = true
  MakeInternals = false
  MapMode = 5
  Placement = pos=(0,0,0) rot=(1,0,0;1.5708rad)
  sketch-geometry (11):
    g0: LineSegment [constr] StartX=-194.483 StartY=34.2854 StartZ=0 EndX=-196.022 EndY=30.0568 EndZ=0
    g1: LineSegment [constr] StartX=-196.022 StartY=30.0568 StartZ=0 EndX=-197.561 EndY=25.8282 EndZ=0
    g2: LineSegment [constr] StartX=-196.022 StartY=30.0568 StartZ=0 EndX=-194.143 EndY=29.3727 EndZ=0
    g3: LineSegment [constr] StartX=-196.022 StartY=30.0568 StartZ=0 EndX=-197.902 EndY=30.7408 EndZ=0
    g4: LineSegment StartX=-196.362 StartY=34.9694 StartZ=0 EndX=-192.604 EndY=33.6014 EndZ=0
    g5: LineSegment StartX=-199.441 StartY=26.5122 StartZ=0 EndX=-195.682 EndY=25.1441 EndZ=0
    g6: LineSegment StartX=-192.604 StartY=33.6014 StartZ=0 EndX=-195.682 EndY=25.1441 EndZ=0
    g7: LineSegment StartX=-196.362 StartY=34.9694 StartZ=0 EndX=-199.441 EndY=26.5122 EndZ=0
    g8: GeomPoint [constr] X=-187.821 Y=29.2 Z=0
    g9: LineSegment [constr] StartX=-188.505 StartY=27.3206 StartZ=0 EndX=-196.022 EndY=30.0568 EndZ=0
    g10: LineSegment [constr] StartX=-187.821 StartY=29.2 StartZ=0 EndX=-188.505 EndY=27.3206 EndZ=0
  constraints (27):
    c: Coincident(g2,g0)
    c: Parallel(g0,g-3)
    c: Tangent(g1,g0) = -1.5708
    c: Perpendicular(g0,g2)
    c: Tangent(g2,g3)
    c: Distance(g0,g1) = 9
    c: Equal(g0,g1)
    c: Distance(g3,g2) = 4
    c: Equal(g2,g3)
    c: Parallel(g3,g4)
    c: Symmetric(g4,g4,g0)
    c: Parallel(g6,g1)
    c: Parallel(g7,g1)
    c: Symmetric(g6,g6,g2)
    c: Symmetric(g5,g5,g1)
    c: Symmetric(g7,g7,g3)
    c: Coincident(g7,g4)
    c: Coincident(g6,g4)
    c: Coincident(g5,g6)
    c: Symmetric(g-3,g-3,g8)
    c: Perpendicular(g-3,g9)
    c: Distance(g9) = 8
    c: Coincident(g3,g9)
    c: Coincident(g10,g8)
    c: Parallel(g10,g-3)
    c: Distance(g10) = 2
    c: Coincident(g10,g9)
FEATURE [Sketcher::SketchObject] Sketch056  label="buco esterno per micro switch"
  ArcFitTolerance = 1e-06
  AttachmentSupport = -> [XZ_Plane]
  ExternalGeometry = -> [Sketch055]
  FullyConstrained = true
  MakeInternals = false
  MapMode = 5
  Placement = pos=(0,0,0) rot=(1,0,0;1.5708rad)
  sketch-geometry (17):
    g0: GeomPoint [constr] X=-194.143 Y=29.3727 Z=0
    g1: GeomPoint [constr] X=-194.483 Y=34.2854 Z=0
    g2: GeomPoint [constr] X=-197.902 Y=30.7408 Z=0
    g3: GeomPoint [constr] X=-197.561 Y=25.8282 Z=0
    g4: GeomPoint [constr] X=-196.022 Y=30.0568 Z=0
    g5: LineSegment [constr] StartX=-194.483 StartY=34.2854 StartZ=0 EndX=-196.022 EndY=30.0568 EndZ=0
    g6: LineSegment [constr] StartX=-196.022 StartY=30.0568 StartZ=0 EndX=-197.561 EndY=25.8282 EndZ=0
    g7: LineSegment [constr] StartX=-197.902 StartY=30.7408 StartZ=0 EndX=-196.022 EndY=30.0568 EndZ=0
    g8: LineSegment [constr] StartX=-196.022 StartY=30.0568 StartZ=0 EndX=-194.143 EndY=29.3727 EndZ=0
    g9: LineSegment [constr] StartX=-195.338 StartY=31.9362 StartZ=0 EndX=-196.022 EndY=30.0568 EndZ=0
    g10: LineSegment [constr] StartX=-196.022 StartY=30.0568 StartZ=0 EndX=-196.706 EndY=28.1774 EndZ=0
    g11: LineSegment [constr] StartX=-196.022 StartY=30.0568 StartZ=0 EndX=-196.821 EndY=30.3475 EndZ=0
    g12: LineSegment [constr] StartX=-196.022 StartY=30.0568 StartZ=0 EndX=-195.223 EndY=29.7661 EndZ=0
    g13: LineSegment StartX=-194.539 StartY=31.6454 StartZ=0 EndX=-195.907 EndY=27.8867 EndZ=0
    g14: LineSegment StartX=-196.137 StartY=32.2269 StartZ=0 EndX=-197.505 EndY=28.4681 EndZ=0
    g15: LineSegment StartX=-196.137 StartY=32.2269 StartZ=0 EndX=-194.539 EndY=31.6454 EndZ=0
    g16: LineSegment StartX=-197.505 StartY=28.4681 StartZ=0 EndX=-195.907 EndY=27.8867 EndZ=0
  constraints (34):
    c: Symmetric(g-5,g-5,g1)
    c: Symmetric(g-5,g-6,g0)
    c: Symmetric(g-6,g-6,g3)
    c: Symmetric(g-5,g-6,g2)
    c: Coincident(g5,g1)
    c: Coincident(g5,g4)
    c: Coincident(g6,g4)
    c: Coincident(g6,g3)
    c: Equal(g5,g6)
    c: Coincident(g7,g2)
    c: Coincident(g7,g4)
    c: Coincident(g8,g4)
    c: Coincident(g8,g0)
    c: Equal(g7,g8)
    c: Coincident(g11,g9)
    c: Coincident(g12,g9)
    c: Tangent(g10,g9) = -1.5708
    c: Perpendicular(g11,g9)
    c: Parallel(g9,g-4)
    c: Equal(g9,g10)
    c: Parallel(g12,g11)
    c: Equal(g11,g12)
    c: Distance(g11,g12) = 1.7
    c: Distance(g9,g10) = 4
    c: Symmetric(g13,g13,g12)
    c: Parallel(g13,g9)
    c: Symmetric(g14,g14,g11)
    c: Symmetric(g15,g15,g9)
    c: Parallel(g15,g11)
    c: Symmetric(g16,g16,g10)
    c: Coincident(g16,g14)
    c: Coincident(g15,g14)
    c: Coincident(g13,g15)
    c: Coincident(g9,g4)
FEATURE [Sketcher::SketchObject] Sketch057  label="buco interno per SWITCH"
  ArcFitTolerance = 1e-06
  AttachmentSupport = -> [XZ_Plane]
  ExternalGeometry = -> [Sketch]
  FullyConstrained = true
  MakeInternals = false
  MapMode = 5
  Placement = pos=(0,0,0) rot=(1,0,0;1.5708rad)
  sketch-geometry (10):
    g0: GeomPoint [constr] X=-187.821 Y=29.2 Z=0
    g1: LineSegment [constr] StartX=-188.505 StartY=27.3206 StartZ=0 EndX=-193.203 EndY=29.0307 EndZ=0
    g2: LineSegment [constr] StartX=-190.809 StartY=35.6086 StartZ=0 EndX=-195.597 EndY=22.4529 EndZ=0
    g3: GeomPoint [constr] X=-193.203 Y=29.0307 Z=0
    g4: LineSegment [constr] StartX=-196.492 StartY=30.2278 StartZ=0 EndX=-189.914 EndY=27.8336 EndZ=0
    g5: LineSegment StartX=-194.098 StartY=36.8056 StartZ=0 EndX=-187.52 EndY=34.4115 EndZ=0
    g6: LineSegment StartX=-194.098 StartY=36.8056 StartZ=0 EndX=-198.886 EndY=23.6499 EndZ=0
    g7: LineSegment StartX=-187.52 StartY=34.4115 StartZ=0 EndX=-192.308 EndY=21.2558 EndZ=0
    g8: LineSegment StartX=-198.886 StartY=23.6499 StartZ=0 EndX=-192.308 EndY=21.2558 EndZ=0
    g9: LineSegment [constr] StartX=-187.821 StartY=29.2 StartZ=0 EndX=-188.505 EndY=27.3206 EndZ=0
  constraints (23):
    c: Symmetric(g-3,g-3,g0)
    c: Perpendicular(g1,g-3)
    c: Parallel(g2,g-3)
    c: Symmetric(g2,g2,g3)
    c: Perpendicular(g2,g4)
    c: Symmetric(g4,g4,g3)
    c: Distance(g2) = 14
    c: Distance(g4) = 7
    c: Distance(g1) = 5
    c: Parallel(g5,g4)
    c: Parallel(g7,g2)
    c: Symmetric(g5,g5,g2)
    c: Symmetric(g6,g6,g4)
    c: Symmetric(g7,g7,g4)
    c: Symmetric(g8,g8,g2)
    c: Coincident(g6,g5)
    c: Coincident(g7,g5)
    c: Coincident(g8,g7)
    c: Coincident(g3,g1)
    c: Coincident(g9,g0)
    c: Parallel(g9,g-3)
    c: Distance(g9) = 2
    c: Coincident(g1,g9)
FEATURE [Sketcher::SketchObject] Sketch058  label="buco esterno per SWITCH"
  ArcFitTolerance = 1e-06
  AttachmentSupport = -> [XZ_Plane]
  ExternalGeometry = -> [Sketch057]
  FullyConstrained = true
  MakeInternals = false
  MapMode = 5
  Placement = pos=(0,0,0) rot=(1,0,0;1.5708rad)
  sketch-geometry (12):
    g0: GeomPoint [constr] X=-190.809 Y=35.6086 Z=0
    g1: GeomPoint [constr] X=-196.492 Y=30.2278 Z=0
    g2: GeomPoint [constr] X=-189.914 Y=27.8336 Z=0
    g3: GeomPoint [constr] X=-195.597 Y=22.4529 Z=0
    g4: GeomPoint [constr] X=-193.203 Y=29.0307 Z=0
    g5: LineSegment [constr] StartX=-192.006 StartY=32.3196 StartZ=0 EndX=-194.4 EndY=25.7418 EndZ=0
    g6: GeomPoint [constr] X=-193.203 Y=29.0307 Z=0
    g7: LineSegment [constr] StartX=-195.082 StartY=29.7148 StartZ=0 EndX=-191.324 EndY=28.3467 EndZ=0
    g8: LineSegment StartX=-193.885 StartY=33.0037 StartZ=0 EndX=-190.127 EndY=31.6356 EndZ=0
    g9: LineSegment StartX=-190.127 StartY=31.6356 StartZ=0 EndX=-192.521 EndY=25.0578 EndZ=0
    g10: LineSegment StartX=-196.28 StartY=26.4258 StartZ=0 EndX=-192.521 EndY=25.0578 EndZ=0
    g11: LineSegment StartX=-193.885 StartY=33.0037 StartZ=0 EndX=-196.28 EndY=26.4258 EndZ=0
  constraints (21):
    c: Symmetric(g-6,g-6,g3)
    c: Symmetric(g-4,g-6,g2)
    c: Symmetric(g-5,g-4,g0)
    c: Symmetric(g-5,g-6,g1)
    c: Symmetric(g1,g2,g4)
    c: Parallel(g5,g-4)
    c: Symmetric(g5,g5,g6)
    c: Perpendicular(g7,g5)
    c: Symmetric(g7,g7,g6)
    c: Distance(g5) = 7
    c: Distance(g7) = 4
    c: Parallel(g8,g7)
    c: Parallel(g11,g5)
    c: Symmetric(g8,g8,g5)
    c: Symmetric(g9,g9,g7)
    c: Symmetric(g10,g10,g5)
    c: Symmetric(g11,g11,g7)
    c: Coincident(g11,g8)
    c: Coincident(g9,g8)
    c: Coincident(g9,g10)
    c: Coincident(g6,g4)
FEATURE [Part::Extrusion] Extrude060  label="Extrude buco interno per SWITCH destro"
  Base = -> Sketch057
  Dir = (0,-1,2e-16)
  DirMode = 2
  FaceMakerClass = Part::FaceMakerBullseye
  FaceMakerMode = 3
  LengthFwd = 13.2
  LengthRev = 0
  Placement = pos=(0,2.6,0) rot=(0,0,1;0rad)
  Solid = true
  Symmetric = false
FEATURE [Part::Extrusion] Extrude061  label="Extrude buco esterno per SWITCH destro"
  Base = -> Sketch058
  Dir = (0,-1,2e-16)
  DirMode = 2
  FaceMakerClass = Part::FaceMakerBullseye
  FaceMakerMode = 3
  LengthFwd = 2
  LengthRev = 0
  Placement = pos=(0,-10.6,0) rot=(0,0,1;0rad)
  Solid = true
  Symmetric = false
FEATURE [Sketcher::SketchObject] Sketch059  label="buco per spazio introduzione SWITCH"
  ArcFitTolerance = 1e-06
  AttachmentSupport = -> [XZ_Plane]
  ExternalGeometry = -> [Sketch057,Sketch010]
  FullyConstrained = true
  MakeInternals = false
  MapMode = 5
  Placement = pos=(0,0,0) rot=(1,0,0;1.5708rad)
  sketch-geometry (8):
    g0: LineSegment [constr] StartX=-201.368 StartY=36.3521 StartZ=0 EndX=-195.094 EndY=34.0687 EndZ=0
    g1: LineSegment [constr] StartX=-194.098 StartY=36.8056 StartZ=0 EndX=-195.094 EndY=34.0687 EndZ=0
    g2: LineSegment StartX=-198.658 StartY=24.2771 StartZ=0 EndX=-199.654 EndY=21.5401 EndZ=0
    g3: LineSegment StartX=-199.654 StartY=21.5401 StartZ=0 EndX=-181.196 EndY=14.822 EndZ=0
    g4: LineSegment StartX=-181.196 StartY=14.822 StartZ=0 EndX=-180.2 EndY=17.559 EndZ=0
    g5: LineSegment StartX=-180.2 StartY=17.559 StartZ=0 EndX=-198.658 EndY=24.2771 EndZ=0
    g6: LineSegment [constr] StartX=-204.932 StartY=26.5605 StartZ=0 EndX=-198.658 EndY=24.2771 EndZ=0
    g7: LineSegment [constr] StartX=-198.658 StartY=24.2771 StartZ=0 EndX=-199.654 EndY=21.5401 EndZ=0
  constraints (20):
    c: Parallel(g1,g-3)
    c: Parallel(g0,g-4)
    c: Coincident(g0,g-4)
    c: Coincident(g1,g-3)
    c: Coincident(g0,g1)
    c: Coincident(g3,g2)
    c: Coincident(g4,g3)
    c: Coincident(g5,g4)
    c: Coincident(g5,g2)
    c: Parallel(g5,g-5)
    c: Parallel(g3,g-5)
    c: Parallel(g4,g-6)
    c: DistanceX(g-6,g4) = 0
    c: Coincident(g6,g-5)
    c: Equal(g6,g0)
    c: Coincident(g7,g6)
    c: Equal(g7,g1)
    c: Tangent(g7,g-3)
    c: Coincident(g2,g6)
    c: Coincident(g2,g7)
FEATURE [Part::Extrusion] Extrude062  label="Extrude buco per spazio introduzione SWITCH"
  Base = -> Sketch059
  Dir = (0,-1,2e-16)
  DirMode = 2
  FaceMakerClass = Part::FaceMakerBullseye
  FaceMakerMode = 3
  LengthFwd = 13.2
  LengthRev = 0
  Solid = true
  Symmetric = true
FEATURE [Part::Extrusion] Extrude063  label="Extrude buco interno per SWITCH sinistro"
  Base = -> Sketch057
  Dir = (0,-1,2e-16)
  DirMode = 2
  FaceMakerClass = Part::FaceMakerBullseye
  FaceMakerMode = 3
  LengthFwd = 13.2
  LengthRev = 0
  Placement = pos=(0,10.6,0) rot=(0,0,1;0rad)
  Solid = true
  Symmetric = false
FEATURE [Part::Extrusion] Extrude064  label="Extrude buco esterno per SWITCH sinistro"
  Base = -> Sketch058
  Dir = (0,-1,2e-16)
  DirMode = 2
  FaceMakerClass = Part::FaceMakerBullseye
  FaceMakerMode = 3
  LengthFwd = 2
  LengthRev = 0
  Placement = pos=(0,12.6,0) rot=(0,0,1;0rad)
  Solid = true
  Symmetric = false
FEATURE [Sketcher::SketchObject] Sketch061  label="struttura esterna blocco switch"
  ArcFitTolerance = 1e-06
  AttachmentSupport = -> [XZ_Plane003]
  FullyConstrained = true
  MakeInternals = false
  MapMode = 5
  Placement = pos=(0,0,0) rot=(1,0,0;1.5708rad)
  sketch-geometry (5):
    g0: LineSegment StartX=-1 StartY=-5.1 StartZ=0 EndX=1 EndY=-5.1 EndZ=0
    g1: LineSegment StartX=1 StartY=-5.1 StartZ=0 EndX=1 EndY=5.1 EndZ=0
    g2: LineSegment StartX=1 StartY=5.1 StartZ=0 EndX=-1 EndY=5.1 EndZ=0
    g3: LineSegment StartX=-1 StartY=5.1 StartZ=0 EndX=-1 EndY=-5.1 EndZ=0
    g4: GeomPoint [constr] X=0 Y=0 Z=0
  constraints (12):
    c: Coincident(g0,g1)
    c: Coincident(g1,g2)
    c: Coincident(g2,g3)
    c: Coincident(g3,g0)
    c: Horizontal(g0)
    c: Horizontal(g2)
    c: Vertical(g1)
    c: Vertical(g3)
    c: Symmetric(g2,g0,g4)
    c: Distance(g1,g3) = 2
    c: Distance(g0,g2) = 10.2
    c: Coincident(g4,g-1)
FEATURE [Sketcher::SketchObject] Sketch062  label="struttura interna blocco switch"
  ArcFitTolerance = 1e-06
  AttachmentSupport = -> [XZ_Plane003]
  ExternalGeometry = -> [Sketch061]
  FullyConstrained = true
  MakeInternals = false
  MapMode = 5
  Placement = pos=(0,0,0) rot=(1,0,0;1.5708rad)
  sketch-geometry (5):
    g0: LineSegment StartX=-1 StartY=3.1 StartZ=0 EndX=-1 EndY=-3.1 EndZ=0
    g1: LineSegment StartX=-1 StartY=-3.1 StartZ=0 EndX=1 EndY=-3.1 EndZ=0
    g2: LineSegment StartX=1 StartY=-3.1 StartZ=0 EndX=1 EndY=3.1 EndZ=0
    g3: LineSegment StartX=1 StartY=3.1 StartZ=0 EndX=-1 EndY=3.1 EndZ=0
    g4: GeomPoint [constr] X=0 Y=0 Z=0
  constraints (12):
    c: Coincident(g0,g1)
    c: Coincident(g1,g2)
    c: Coincident(g2,g3)
    c: Coincident(g3,g0)
    c: Vertical(g0)
    c: Vertical(g2)
    c: Horizontal(g1)
    c: Horizontal(g3)
    c: Symmetric(g2,g0,g4)
    c: Coincident(g4,g-1)
    c: Distance(g0) = 6.2
    c: Equal(g3,g-3)
FEATURE [Sketcher::SketchObject] Sketch063  label="blocchi tra switch"
  ArcFitTolerance = 1e-06
  AttachmentSupport = -> [XZ_Plane003]
  ExternalGeometry = -> [Sketch061,Sketch062]
  FullyConstrained = true
  MakeInternals = false
  MapMode = 5
  Placement = pos=(0,0,0) rot=(1,0,0;1.5708rad)
  sketch-geometry (8):
    g0: LineSegment StartX=-3 StartY=5.1 StartZ=0 EndX=-1 EndY=5.1 EndZ=0
    g1: LineSegment StartX=-1 StartY=5.1 StartZ=0 EndX=-1 EndY=3.1 EndZ=0
    g2: LineSegment StartX=-1 StartY=3.1 StartZ=0 EndX=-3 EndY=3.1 EndZ=0
    g3: LineSegment StartX=-3 StartY=3.1 StartZ=0 EndX=-3 EndY=5.1 EndZ=0
    g4: LineSegment StartX=-3 StartY=-3.1 StartZ=0 EndX=-1 EndY=-3.1 EndZ=0
    g5: LineSegment StartX=-1 StartY=-3.1 StartZ=0 EndX=-1 EndY=-5.1 EndZ=0
    g6: LineSegment StartX=-1 StartY=-5.1 StartZ=0 EndX=-3 EndY=-5.1 EndZ=0
    g7: LineSegment StartX=-3 StartY=-5.1 StartZ=0 EndX=-3 EndY=-3.1 EndZ=0
  constraints (20):
    c: Horizontal(g0)
    c: Coincident(g1,g0)
    c: Coincident(g2,g1)
    c: Horizontal(g2)
    c: Coincident(g3,g2)
    c: Coincident(g3,g0)
    c: Vertical(g3)
    c: Horizontal(g4)
    c: Coincident(g5,g4)
    c: Coincident(g6,g5)
    c: Horizontal(g6)
    c: Coincident(g7,g6)
    c: Coincident(g7,g4)
    c: Vertical(g7)
    c: Coincident(g0,g-4)
    c: Coincident(g1,g-5)
    c: Coincident(g4,g-6)
    c: Coincident(g5,g-7)
    c: Distance(g0) = 2
    c: Distance(g4) = 2
FEATURE [Sketcher::SketchObject] Sketch066  label="piano per rampino"
  ArcFitTolerance = 1e-06
  AttachmentSupport = -> [XZ_Plane002]
  ExternalGeometry = -> [Sketch045]
  FullyConstrained = true
  MakeInternals = false
  MapMode = 5
  Placement = pos=(0,0,0) rot=(1,0,0;1.5708rad)
  sketch-geometry (4):
    g0: LineSegment StartX=5.4 StartY=5.1 StartZ=0 EndX=5.4 EndY=3.9 EndZ=0
    g1: LineSegment StartX=5.4 StartY=3.9 StartZ=0 EndX=7 EndY=3.9 EndZ=0
    g2: LineSegment StartX=7 StartY=3.9 StartZ=0 EndX=7 EndY=5.1 EndZ=0
    g3: LineSegment StartX=7 StartY=5.1 StartZ=0 EndX=5.4 EndY=5.1 EndZ=0
  constraints (11):
    c: Coincident(g0,g1)
    c: Coincident(g1,g2)
    c: Coincident(g2,g3)
    c: Coincident(g3,g0)
    c: Vertical(g0)
    c: Vertical(g2)
    c: Horizontal(g1)
    c: Horizontal(g3)
    c: Distance(g0,g2) = 1.6
    c: Distance(g1,g3) = 1.2
    c: Coincident(g2,g-3)
FEATURE [Sketcher::SketchObject] Sketch064  label="rampini_per_serraggio_struttura"
  ArcFitTolerance = 1e-06
  AttachmentSupport = -> [XZ_Plane002]
  ExternalGeometry = -> [Sketch066,Sketch045]
  FullyConstrained = true
  MakeInternals = false
  MapMode = 5
  Placement = pos=(0,0,0) rot=(1,0,0;1.5708rad)
  sketch-geometry (7):
    g0: LineSegment StartX=7 StartY=5.1 StartZ=0 EndX=7 EndY=3.9 EndZ=0
    g1: LineSegment StartX=7 StartY=3.9 StartZ=0 EndX=9 EndY=3.9 EndZ=0
    g2: LineSegment StartX=7 StartY=5.1 StartZ=0 EndX=7 EndY=5.1 EndZ=0
    g3: LineSegment StartX=7 StartY=5.1 StartZ=0 EndX=7 EndY=7.5 EndZ=0
    g4: LineSegment StartX=9 StartY=5.1 StartZ=0 EndX=9 EndY=3.9 EndZ=0
    g5: LineSegment StartX=7 StartY=7.5 StartZ=0 EndX=9 EndY=7.5 EndZ=0
    g6: LineSegment StartX=9 StartY=7.5 StartZ=0 EndX=9 EndY=5.1 EndZ=0
  constraints (20):
    c: Vertical(g0)
    c: Coincident(g1,g0)
    c: Horizontal(g1)
    c: Coincident(g2,g0)
    c: Horizontal(g2)
    c: Coincident(g3,g2)
    c: Vertical(g3)
    c: Coincident(g5,g3)
    c: Coincident(g4,g6)
    c: Coincident(g4,g1)
    c: Vertical(g4)
    c: Coincident(g0,g-3)
    c: DistanceY(g-4,g3) = 2.4
    c: DistanceX(g1,g1) = 2
    c: DistanceY(g2,g6) = 0
    c: DistanceX(g2,g2) = 0
    c: DistanceY(g0,g0) = 1.2
    c: Coincident(g5,g6)
    c: Horizontal(g5)
    c: Vertical(g6)
FEATURE [Sketcher::SketchObject] Sketch067  label="perno per blocco switch"
  ArcFitTolerance = 1e-06
  AttachmentSupport = -> [XZ_Plane]
  ExternalGeometry = -> [Sketch,Sketch010]
  FullyConstrained = true
  MakeInternals = false
  MapMode = 5
  Placement = pos=(0,0,0) rot=(1,0,0;1.5708rad)
  sketch-geometry (14):
    g0: LineSegment StartX=-191.073 StartY=24.9429 StartZ=0 EndX=-185.81 EndY=23.0276 EndZ=0
    g1: LineSegment StartX=-183.76 StartY=23.9839 StartZ=0 EndX=-182.392 EndY=27.7427 EndZ=0
    g2: LineSegment StartX=-183.348 StartY=29.7934 StartZ=0 EndX=-188.61 EndY=31.7087 EndZ=0
    g3: LineSegment StartX=-188.61 StartY=31.7087 StartZ=0 EndX=-191.073 EndY=24.9429 EndZ=0
    g4: GeomPoint [constr] X=-186.459 Y=27.0946 Z=0
    g5: LineSegment StartX=-189.022 StartY=25.8992 StartZ=0 EndX=-185.263 EndY=24.5311 EndZ=0
    g6: LineSegment StartX=-185.263 StartY=24.5311 StartZ=0 EndX=-183.895 EndY=28.2899 EndZ=0
    g7: LineSegment StartX=-183.895 StartY=28.2899 StartZ=0 EndX=-187.654 EndY=29.658 EndZ=0
    g8: LineSegment StartX=-187.654 StartY=29.658 StartZ=0 EndX=-189.022 EndY=25.8992 EndZ=0
    g9: GeomPoint [constr] X=-186.459 Y=27.0946 Z=0
    g10: ArcOfCircle CenterX=-185.263 CenterY=24.5311 CenterZ=0 NormalX=0 NormalY=0 NormalZ=1 AngleXU=0 Radius=1.6 StartAngle=4.36332 EndAngle=5.93412
    g11: GeomPoint [constr] X=-184.307 Y=22.4804 Z=0
    g12: ArcOfCircle CenterX=-183.895 CenterY=28.2899 CenterZ=0 NormalX=0 NormalY=0 NormalZ=1 AngleXU=0 Radius=1.6 StartAngle=5.93412 EndAngle=7.50492
    g13: GeomPoint [constr] X=-181.844 Y=29.2462 Z=0
  constraints (30):
    c: Coincident(g2,g3)
    c: Coincident(g3,g0)
    c: Symmetric(g13,g0,g4)
    c: Distance(g11,g3) = 7.2
    c: Distance(g0,g2) = 7.2
    c: Parallel(g3,g1)
    c: Parallel(g2,g0)
    c: Perpendicular(g2,g3)
    c: Coincident(g5,g6)
    c: Coincident(g6,g7)
    c: Coincident(g7,g8)
    c: Coincident(g8,g5)
    c: Symmetric(g7,g5,g9)
    c: Distance(g6,g8) = 4
    c: Distance(g5,g7) = 4
    c: Coincident(g9,g4)
    c: Parallel(g8,g6)
    c: Parallel(g7,g5)
    c: Perpendicular(g7,g8)
    c: Tangent(g8,g-3)
    c: Tangent(g2,g-4)
    c: PointOnObject(g11,g1)
    c: PointOnObject(g11,g0)
    c: Tangent(g1,g10) = -1.5708
    c: Tangent(g0,g10) = -1.5708
    c: PointOnObject(g13,g1)
    c: Tangent(g1,g12) = -1.5708
    c: Tangent(g2,g12) = -1.5708
    c: Equal(g10,g12)
    c: Coincident(g10,g5)
FEATURE [Part::Extrusion] Extrude072  label="Extrude perno per blocco switch"
  Base = -> Sketch067
  Dir = (0,-1,2e-16)
  DirMode = 2
  FaceMakerClass = Part::FaceMakerBullseye
  FaceMakerMode = 3
  LengthFwd = 25.2
  LengthRev = 0
  Solid = true
  Symmetric = true
FEATURE [Part::MultiFuse] Fusion
  Refine = true
  Shapes = -> [Extrude,Sweep,Extrude007,Extrude011,Extrude005,Extrude012,Extrude013,Extrude016,Extrude031,Extrude039,Extrude045,Extrude072]
FEATURE [Part::Cut] Cut
  Base = -> Fusion
  Refine = true
  Tool = -> Extrude001
FEATURE [Part::Cut] Cut001
  Base = -> Cut
  Refine = true
  Tool = -> Extrude004
FEATURE [Part::Cut] Cut002
  Base = -> Cut001
  Refine = true
  Tool = -> Extrude006
FEATURE [Part::Cut] Cut003
  Base = -> Cut002
  Refine = true
  Tool = -> Extrude008
FEATURE [Part::Cut] Cut004
  Base = -> Cut003
  Refine = true
  Tool = -> Extrude009
FEATURE [Part::Cut] Cut005
  Base = -> Cut004
  Refine = true
  Tool = -> Extrude010
FEATURE [Part::Cut] Cut006
  Base = -> Cut005
  Refine = true
  Tool = -> Extrude014
FEATURE [Part::Cut] Cut007
  Base = -> Cut006
  Refine = true
  Tool = -> Extrude015
FEATURE [Part::Cut] Cut008
  Base = -> Cut007
  Refine = true
  Tool = -> Extrude018
FEATURE [Part::Cut] Cut009
  Base = -> Cut008
  Refine = true
  Tool = -> Extrude019
FEATURE [Part::Cut] Cut010
  Base = -> Cut009
  Refine = true
  Tool = -> Extrude020
FEATURE [Part::Cut] Cut011
  Base = -> Cut010
  Refine = true
  Tool = -> Extrude021
FEATURE [Part::Cut] Cut012
  Base = -> Cut011
  Refine = true
  Tool = -> Extrude022
FEATURE [Part::Cut] Cut013
  Base = -> Cut012
  Refine = true
  Tool = -> Extrude023
FEATURE [Part::Cut] Cut014
  Base = -> Cut013
  Refine = true
  Tool = -> Extrude032
FEATURE [Part::Cut] Cut015
  Base = -> Cut014
  Refine = true
  Tool = -> Extrude033
FEATURE [Part::Cut] Cut016
  Base = -> Cut015
  Refine = true
  Tool = -> Extrude034
FEATURE [Part::Cut] Cut017
  Base = -> Cut016
  Refine = true
  Tool = -> Extrude035
FEATURE [Part::Cut] Cut018
  Base = -> Cut017
  Refine = true
  Tool = -> Extrude036
FEATURE [Part::Cut] Cut019
  Base = -> Cut018
  Refine = true
  Tool = -> Extrude037
FEATURE [Part::Cut] Cut020
  Base = -> Cut019
  Refine = true
  Tool = -> Extrude030
FEATURE [Part::Cut] Cut022
  Base = -> Cut020
  Refine = true
  Tool = -> Extrude038
FEATURE [Part::Cut] Cut023
  Base = -> Cut022
  Refine = true
  Tool = -> Extrude041
FEATURE [Part::Cut] Cut024
  Base = -> Cut023
  Refine = true
  Tool = -> Extrude040
FEATURE [Part::Cut] Cut025
  Base = -> Cut024
  Refine = true
  Tool = -> Extrude042
FEATURE [Part::Cut] Cut026
  Base = -> Cut025
  Refine = true
  Tool = -> Extrude043
FEATURE [Part::Cut] Cut027
  Base = -> Cut026
  Refine = true
  Tool = -> Extrude044
FEATURE [Part::Cut] Cut028
  Base = -> Cut027
  Refine = true
  Tool = -> Extrude046
FEATURE [Part::Cut] Cut029
  Base = -> Cut028
  Refine = true
  Tool = -> Extrude047
FEATURE [Part::Cut] Cut033
  Base = -> Cut029
  Refine = true
  Tool = -> Extrude055
FEATURE [Part::Cut] Cut034
  Base = -> Cut033
  Refine = true
  Tool = -> Extrude056
FEATURE [Part::Cut] Cut035
  Base = -> Cut034
  Refine = true
  Tool = -> Extrude057
FEATURE [Part::Cut] Cut037
  Base = -> Cut035
  Refine = true
  Tool = -> Extrude060
FEATURE [Part::Cut] Cut038
  Base = -> Cut037
  Refine = true
  Tool = -> Extrude061
FEATURE [Part::Cut] Cut039
  Base = -> Cut038
  Refine = true
  Tool = -> Extrude063
FEATURE [Part::Cut] Cut040
  Base = -> Cut039
  Refine = true
  Tool = -> Extrude064
FEATURE [Part::Cut] Cut041
  Base = -> Cut040
  Refine = true
  Tool = -> Extrude062
FEATURE [Sketcher::SketchObject] Sketch068  label="base con smusso sopra neopixel"
  ArcFitTolerance = 1e-06
  AttachmentSupport = -> [YZ_Plane002]
  FullyConstrained = true
  MakeInternals = false
  MapMode = 5
  Placement = pos=(0,0,0) rot=(0.57735,0.57735,0.57735;2.0944rad)
  sketch-geometry (5):
    g0: LineSegment StartX=-9.5 StartY=-6.1 StartZ=0 EndX=9.5 EndY=-6.1 EndZ=0
    g1: LineSegment StartX=9.5 StartY=-6.1 StartZ=0 EndX=9.5 EndY=6.1 EndZ=0
    g2: LineSegment StartX=9.5 StartY=6.1 StartZ=0 EndX=-9.5 EndY=6.1 EndZ=0
    g3: LineSegment StartX=-9.5 StartY=6.1 StartZ=0 EndX=-9.5 EndY=-6.1 EndZ=0
    g4: GeomPoint [constr] X=0 Y=0 Z=0
  constraints (12):
    c: Coincident(g0,g1)
    c: Coincident(g1,g2)
    c: Coincident(g2,g3)
    c: Coincident(g3,g0)
    c: Horizontal(g0)
    c: Horizontal(g2)
    c: Vertical(g1)
    c: Vertical(g3)
    c: Symmetric(g2,g0,g4)
    c: Distance(g1,g3) = 19
    c: Distance(g0,g2) = 12.2
    c: Coincident(g4,g-1)
FEATURE [Sketcher::SketchObject] Sketch069  label="cilindro minore"
  ArcFitTolerance = 1e-06
  AttachmentSupport = -> [XZ_Plane004]
  FullyConstrained = true
  MakeInternals = false
  MapMode = 5
  Placement = pos=(0,0,0) rot=(1,0,0;1.5708rad)
  sketch-geometry (1):
    g0: Circle CenterX=0 CenterY=0 CenterZ=0 NormalX=0 NormalY=0 NormalZ=1 AngleXU=0 Radius=5.8
  constraints (2):
    c: Diameter(g0) = 11.6
    c: Coincident(g0,g-1)
FEATURE [Sketcher::SketchObject] Sketch070  label="cilindro maggiore"
  ArcFitTolerance = 1e-06
  AttachmentSupport = -> [XZ_Plane004]
  ExternalGeometry = -> [Sketch069]
  FullyConstrained = true
  MakeInternals = false
  MapMode = 5
  Placement = pos=(0,0,0) rot=(1,0,0;1.5708rad)
  sketch-geometry (1):
    g0: Circle CenterX=0 CenterY=0 CenterZ=0 NormalX=0 NormalY=0 NormalZ=1 AngleXU=0 Radius=6.5
  constraints (2):
    c: Coincident(g0,g-1)
    c: Diameter(g0) = 13
FEATURE [Sketcher::SketchObject] Sketch071  label="buco interno"
  ArcFitTolerance = 1e-06
  AttachmentSupport = -> [XZ_Plane004]
  ExternalGeometry = -> [Sketch069]
  FullyConstrained = true
  MakeInternals = false
  MapMode = 5
  Placement = pos=(0,0,0) rot=(1,0,0;1.5708rad)
  sketch-geometry (1):
    g0: Circle CenterX=0 CenterY=0 CenterZ=0 NormalX=0 NormalY=0 NormalZ=1 AngleXU=0 Radius=5
  constraints (2):
    c: Coincident(g0,g-1)
    c: Diameter(g0) = 10
FEATURE [PartDesign::Pad] Pad
  Direction = (0,-1,2e-16)
  Length = 1.2
  Length2 = 10
  Placement = pos=(0,0,0) rot=(1,0,0;1.5708rad)
  Profile = -> Sketch070
  ReferenceAxis = -> Sketch070 [N_Axis]
  Refine = true
  Suppressed = false
  Type = 0
FEATURE [PartDesign::Pad] Pad001
  BaseFeature = -> Pad
  Direction = (0,-1,2e-16)
  Length = 5.6
  Length2 = 10
  Placement = pos=(0,0,0) rot=(1,0,0;1.5708rad)
  Profile = -> Sketch069
  ReferenceAxis = -> Sketch069 [N_Axis]
  Refine = true
  Suppressed = false
  Type = 0
FEATURE [PartDesign::Pocket] Pocket
  BaseFeature = -> Pad001
  Direction = (0,1,-2e-16)
  Length = 7
  Length2 = 5
  Midplane = true
  Placement = pos=(0,0,0) rot=(1,0,0;1.5708rad)
  Profile = -> Sketch071
  ReferenceAxis = -> Sketch071 [N_Axis]
  Refine = true
  Suppressed = false
  Type = 0
FEATURE [PartDesign::Fillet] Fillet
  Base = -> Pocket [Face7]
  BaseFeature = -> Pocket
  Placement = pos=(0,0,0) rot=(1,0,0;1.5708rad)
  Radius = 1
  Refine = true
  SupportTransform = false
  Suppressed = false
  UseAllEdges = false
FEATURE [PartDesign::Body] Body004  label="pulsanti lato sinistro"
  AllowCompound = false
  Group = -> [Sketch069,Sketch070,Sketch071,Pad,Pad001,Pocket,Fillet]
  Origin = -> Origin004
  Tip = -> Fillet
FEATURE [Sketcher::SketchObject] Sketch072  label="buco per saldature e diodo driver solenoide"
  ArcFitTolerance = 1e-06
  AttachmentSupport = -> [XZ_Plane]
  ExternalGeometry = -> [Sketch038]
  FullyConstrained = true
  MakeInternals = false
  MapMode = 5
  Placement = pos=(0,0,0) rot=(1,0,0;1.5708rad)
  sketch-geometry (4):
    g0: LineSegment StartX=-212.269 StartY=-43.9083 StartZ=0 EndX=-207.197 EndY=-33.0326 EndZ=0
    g1: LineSegment StartX=-207.197 StartY=-33.0326 StartZ=0 EndX=-207.56 EndY=-32.8635 EndZ=0
    g2: LineSegment StartX=-207.56 StartY=-32.8635 StartZ=0 EndX=-212.631 EndY=-43.7392 EndZ=0
    g3: LineSegment StartX=-212.631 StartY=-43.7392 StartZ=0 EndX=-212.269 EndY=-43.9083 EndZ=0
  constraints (11):
    c: Coincident(g1,g0)
    c: Coincident(g2,g1)
    c: Coincident(g3,g2)
    c: Coincident(g3,g0)
    c: Parallel(g-3,g0)
    c: Parallel(g0,g2)
    c: Perpendicular(g0,g3)
    c: Perpendicular(g1,g0)
    c: Distance(g3) = 0.4
    c: Distance(g2) = 12
    c: Coincident(g0,g-3)
FEATURE [Part::Extrusion] Extrude074  label="Extrude buco per saldature e diodo driver solenoide"
  Base = -> Sketch072
  Dir = (0,-1,2e-16)
  DirMode = 2
  FaceMakerClass = Part::FaceMakerBullseye
  FaceMakerMode = 3
  LengthFwd = 14.6
  LengthRev = 0
  Solid = true
  Symmetric = true
FEATURE [Part::Cut] Cut042
  Base = -> Cut041
  Refine = true
  Tool = -> Extrude074
FEATURE [Sketcher::SketchObject] Sketch073  label="fori slargati blocco solenoide"
  ArcFitTolerance = 1e-06
  AttachmentSupport = -> [XY_Plane]
  ExternalGeometry = -> [Sketch030]
  FullyConstrained = true
  MakeInternals = false
  MapMode = 5
  sketch-geometry (2):
    g0: Circle CenterX=-152.209 CenterY=6.95 CenterZ=0 NormalX=0 NormalY=0 NormalZ=1 AngleXU=0 Radius=3.7
    g1: Circle CenterX=-130.41 CenterY=-6.95 CenterZ=0 NormalX=0 NormalY=0 NormalZ=1 AngleXU=0 Radius=3.7
  constraints (4):
    c: Diameter(g0) = 7.4
    c: Coincident(g0,g-3)
    c: Diameter(g1) = 7.4
    c: Coincident(g1,g-4)
FEATURE [Part::Extrusion] Extrude075  label="Extrude fori slargati blocco solenoide"
  Base = -> Sketch073
  Dir = (0,0,1)
  DirMode = 2
  FaceMakerClass = Part::FaceMakerBullseye
  FaceMakerMode = 3
  LengthFwd = 1.5
  LengthRev = 0
  Placement = pos=(0,0,36.4) rot=(0,0,1;0rad)
  Solid = true
  Symmetric = false
FEATURE [Part::Cut] Cut043
  Base = -> Cut042
  Refine = true
  Tool = -> Extrude075
FEATURE [Sketcher::SketchObject] Sketch074  label="lato sx pistola"
  ArcFitTolerance = 1e-06
  AttachmentSupport = -> [XZ_Plane]
  ExternalGeometry = -> [Sketch016,Sketch,Sketch058]
  FullyConstrained = true
  MakeInternals = false
  MapMode = 5
  Placement = pos=(0,0,0) rot=(1,0,0;1.5708rad)
  sketch-geometry (37):
    g0: LineSegment StartX=-82.8 StartY=3.2 StartZ=0 EndX=0 EndY=3.2 EndZ=0
    g1: LineSegment StartX=-82.8 StartY=3.2 StartZ=0 EndX=-82.8 EndY=6.2 EndZ=0
    g2: LineSegment [constr] StartX=-107.6 StartY=18 StartZ=0 EndX=-107.6 EndY=20 EndZ=0
    g3: LineSegment [constr] StartX=-132.428 StartY=18 StartZ=0 EndX=-132.428 EndY=20 EndZ=0
    g4: LineSegment StartX=-132.428 StartY=20 StartZ=0 EndX=-107.6 EndY=20 EndZ=0
    g5: ArcOfCircle CenterX=-107.6 CenterY=4 CenterZ=0 NormalX=0 NormalY=0 NormalZ=1 AngleXU=0 Radius=16 StartAngle=0.137937 EndAngle=1.5708
    g6: LineSegment StartX=-82.8 StartY=6.2 StartZ=0 EndX=-91.752 EndY=6.2 EndZ=0
    g7: LineSegment [constr] StartX=-145.743 StartY=8.32624 StartZ=0 EndX=-147.645 EndY=8.94427 EndZ=0
    g8: ArcOfCircle CenterX=-132.428 CenterY=4 CenterZ=0 NormalX=0 NormalY=0 NormalZ=1 AngleXU=0 Radius=16 StartAngle=1.5708 EndAngle=2.82743
    g9: LineSegment StartX=-215.932 StartY=-80.4316 StartZ=0 EndX=-176.685 EndY=-80.4316 EndZ=0
    g10: LineSegment StartX=-147.645 StartY=8.94427 StartZ=0 EndX=-176.685 EndY=-80.4316 EndZ=0
    g11: LineSegment [constr] StartX=-193.988 StartY=-2.33927 StartZ=0 EndX=-192.176 EndY=-3.18451 EndZ=0
    g12: LineSegment [constr] StartX=-217.232 StartY=-52.1862 StartZ=0 EndX=-215.42 EndY=-53.0314 EndZ=0
    g13: LineSegment StartX=-192.176 StartY=-3.18451 StartZ=0 EndX=-215.42 EndY=-53.0314 EndZ=0
    g14: ArcOfCircle CenterX=-184.801 CenterY=-67.3089 CenterZ=0 NormalX=0 NormalY=0 NormalZ=1 AngleXU=0 Radius=33.7833 StartAngle=2.70526 EndAngle=3.54053
    g15: ArcOfCircle CenterX=-207.583 CenterY=4 CenterZ=0 NormalX=0 NormalY=0 NormalZ=1 AngleXU=0 Radius=17 StartAngle=5.84685 EndAngle=7.56663
    g16: LineSegment StartX=-202.765 StartY=20.303 StartZ=0 EndX=-195.887 EndY=39.2 EndZ=0
    g17: LineSegment [constr] StartX=-193.885 StartY=33.0037 StartZ=0 EndX=-197.644 EndY=34.3718 EndZ=0
    g18: LineSegment StartX=-195.887 StartY=39.2 StartZ=0 EndX=0 EndY=39.2 EndZ=0
    g19: LineSegment StartX=0 StartY=3.2 StartZ=0 EndX=0 EndY=39.2 EndZ=0
    g20: LineSegment StartX=-189.939 StartY=31.5672 StartZ=0 EndX=-192.333 EndY=24.9893 EndZ=0
    g21: LineSegment StartX=-196.467 StartY=26.4942 StartZ=0 EndX=-194.073 EndY=33.0721 EndZ=0
    g22: Circle CenterX=-213.443 CenterY=-76.8316 CenterZ=0 NormalX=0 NormalY=0 NormalZ=1 AngleXU=0 Radius=1.8
    g23: Circle CenterX=-179.305 CenterY=-76.8316 CenterZ=0 NormalX=0 NormalY=0 NormalZ=1 AngleXU=0 Radius=1.8
    g24: Circle CenterX=-184.08 CenterY=34.8 CenterZ=0 NormalX=0 NormalY=0 NormalZ=1 AngleXU=0 Radius=1.8
    g25: Circle CenterX=-78.51 CenterY=34.8 CenterZ=0 NormalX=0 NormalY=0 NormalZ=1 AngleXU=0 Radius=1.8
    g26: Circle CenterX=-78.51 CenterY=7.6 CenterZ=0 NormalX=0 NormalY=0 NormalZ=1 AngleXU=0 Radius=1.8
    g27: Circle CenterX=-5.6 CenterY=34.8 CenterZ=0 NormalX=0 NormalY=0 NormalZ=1 AngleXU=0 Radius=1.8
    g28: Circle CenterX=-5.6 CenterY=7.6 CenterZ=0 NormalX=0 NormalY=0 NormalZ=1 AngleXU=0 Radius=1.8
    g29: LineSegment StartX=-190.127 StartY=31.6356 StartZ=0 EndX=-189.939 EndY=31.5672 EndZ=0
    g30: LineSegment StartX=-194.073 StartY=33.0721 StartZ=0 EndX=-193.885 EndY=33.0037 EndZ=0
    g31: LineSegment StartX=-193.885 StartY=33.0037 StartZ=0 EndX=-190.127 EndY=31.6356 EndZ=0
    g32: LineSegment StartX=-196.467 StartY=26.4942 StartZ=0 EndX=-192.333 EndY=24.9893 EndZ=0
    g33: Circle CenterX=-19 CenterY=21.2 CenterZ=0 NormalX=0 NormalY=0 NormalZ=1 AngleXU=0 Radius=6.3
    g34: Circle CenterX=-42 CenterY=21.2 CenterZ=0 NormalX=0 NormalY=0 NormalZ=1 AngleXU=0 Radius=6.3
    g35: Circle CenterX=-65 CenterY=21.2 CenterZ=0 NormalX=0 NormalY=0 NormalZ=1 AngleXU=0 Radius=6.3
    g36: LineSegment [constr] StartX=-4 StartY=21.2 StartZ=0 EndX=-65 EndY=21.2 EndZ=0
  constraints (96):
    c: Coincident(g0,g-41)
    c: Horizontal(g0)
    c: PointOnObject(g0,g-39)
    c: Coincident(g1,g0)
    c: Vertical(g1)
    c: DistanceY(g1,g1) = 3
    c: Coincident(g2,g-17)
    c: Vertical(g2)
    c: Coincident(g3,g-16)
    c: Vertical(g3)
    c: DistanceY(g2,g2) = 2
    c: DistanceY(g3,g3) = 2
    c: Coincident(g4,g3)
    c: Coincident(g4,g2)
    c: Coincident(g5,g-17)
    c: Coincident(g5,g2)
    c: Coincident(g6,g1)
    c: Horizontal(g6)
    c: Coincident(g6,g5)
    c: Coincident(g7,g-15)
    c: Coincident(g8,g7)
    c: Coincident(g8,g3)
    c: Coincident(g8,g-15)
    c: Horizontal(g9)
    c: DistanceY(g-13,g9) = 2
    c: Coincident(g10,g7)
    c: Parallel(g10,g-14)
    c: Coincident(g9,g10)
    c: Distance(g11) = 2
    c: Coincident(g11,g-11)
    c: Perpendicular(g-11,g11)
    c: Distance(g12) = 2
    c: Coincident(g12,g-12)
    c: Perpendicular(g-11,g12)
    c: Coincident(g13,g11)
    c: Coincident(g13,g12)
    c: Coincident(g14,g-32)
    c: Coincident(g14,g12)
    c: Coincident(g14,g9)
    c: Coincident(g15,g-10)
    c: Coincident(g15,g11)
    c: Parallel(g16,g-22)
    c: Distance(g17) = 4
    c: PointOnObject(g17,g16)
    c: Coincident(g15,g16)
    c: Horizontal(g18)
    c: Coincident(g18,g16)
    c: Coincident(g19,g0)
    c: PointOnObject(g19,g-39)
    c: DistanceY(g19,g-36) = 2
    c: Coincident(g18,g19)
    c: Diameter(g22) = 3.6
    c: Coincident(g22,g-9)
    c: Diameter(g23) = 3.6
    c: Coincident(g23,g-8)
    c: Diameter(g24) = 3.6
    c: Diameter(g25) = 3.6
    c: Diameter(g26) = 3.6
    c: Diameter(g27) = 3.6
    c: Diameter(g28) = 3.6
    c: Coincident(g27,g-4)
    c: Coincident(g28,g-3)
    c: Coincident(g25,g-6)
    c: Coincident(g26,g-5)
    c: Coincident(g24,g-7)
    c: Parallel(g20,g-21)
    c: Equal(g20,g-21)
    c: Parallel(g21,g-19)
    c: Equal(g21,g-19)
    c: Distance(g29) = 0.2
    c: Distance(g30) = 0.2
    c: Parallel(g29,g-20)
    c: Parallel(g31,g-20)
    c: Equal(g31,g-20)
    c: Coincident(g30,g31)
    c: Coincident(g31,g29)
    c: Coincident(g29,g-21)
    c: Parallel(g30,g31)
    c: Coincident(g17,g30)
    c: Coincident(g20,g29)
    c: Coincident(g21,g30)
    c: Perpendicular(g16,g17)
    c: Coincident(g32,g21)
    c: Coincident(g32,g20)
    c: Perpendicular(g10,g7)
    c: Diameter(g33) = 12.6
    c: Diameter(g34) = 12.6
    c: Diameter(g35) = 12.6
    c: Horizontal(g36)
    c: PointOnObject(g33,g36)
    c: PointOnObject(g34,g36)
    c: DistanceX(g34,g33) = 23
    c: DistanceX(g35,g34) = 23
    c: DistanceX(g33,g36) = 15
    c: Symmetric(g-24,g-24,g36)
    c: Coincident(g36,g35)
FEATURE [Sketcher::SketchObject] Sketch075  label="lato dx pistola"
  ArcFitTolerance = 1e-06
  AttachmentSupport = -> [XZ_Plane]
  ExternalGeometry = -> [Sketch016,Sketch,Sketch058,Sketch074]
  FullyConstrained = true
  MakeInternals = false
  MapMode = 5
  Placement = pos=(0,0,0) rot=(1,0,0;1.5708rad)
  sketch-geometry (61):
    g0: LineSegment StartX=-82.8 StartY=3.2 StartZ=0 EndX=0 EndY=3.2 EndZ=0
    g1: LineSegment StartX=-82.8 StartY=3.2 StartZ=0 EndX=-82.8 EndY=6.2 EndZ=0
    g2: LineSegment [constr] StartX=-107.6 StartY=18 StartZ=0 EndX=-107.6 EndY=20 EndZ=0
    g3: LineSegment [constr] StartX=-132.428 StartY=18 StartZ=0 EndX=-132.428 EndY=20 EndZ=0
    g4: LineSegment StartX=-132.428 StartY=20 StartZ=0 EndX=-107.6 EndY=20 EndZ=0
    g5: ArcOfCircle CenterX=-107.6 CenterY=4 CenterZ=0 NormalX=0 NormalY=0 NormalZ=1 AngleXU=0 Radius=16 StartAngle=0.137937 EndAngle=1.5708
    g6: LineSegment StartX=-82.8 StartY=6.2 StartZ=0 EndX=-91.752 EndY=6.2 EndZ=0
    g7: LineSegment [constr] StartX=-145.743 StartY=8.32624 StartZ=0 EndX=-147.645 EndY=8.94427 EndZ=0
    g8: ArcOfCircle CenterX=-132.428 CenterY=4 CenterZ=0 NormalX=0 NormalY=0 NormalZ=1 AngleXU=0 Radius=16 StartAngle=1.5708 EndAngle=2.82743
    g9: LineSegment StartX=-215.932 StartY=-80.4316 StartZ=0 EndX=-176.685 EndY=-80.4316 EndZ=0
    g10: LineSegment StartX=-147.645 StartY=8.94427 StartZ=0 EndX=-176.685 EndY=-80.4316 EndZ=0
    g11: LineSegment [constr] StartX=-193.988 StartY=-2.33927 StartZ=0 EndX=-192.176 EndY=-3.18451 EndZ=0
    g12: LineSegment [constr] StartX=-217.232 StartY=-52.1862 StartZ=0 EndX=-215.42 EndY=-53.0314 EndZ=0
    g13: LineSegment StartX=-192.176 StartY=-3.18451 StartZ=0 EndX=-215.42 EndY=-53.0314 EndZ=0
    g14: ArcOfCircle CenterX=-184.801 CenterY=-67.3089 CenterZ=0 NormalX=0 NormalY=0 NormalZ=1 AngleXU=0 Radius=33.7833 StartAngle=2.70526 EndAngle=3.54053
    g15: ArcOfCircle CenterX=-207.583 CenterY=4 CenterZ=0 NormalX=0 NormalY=0 NormalZ=1 AngleXU=0 Radius=17 StartAngle=5.84685 EndAngle=7.56663
    g16: LineSegment StartX=-202.765 StartY=20.303 StartZ=0 EndX=-195.887 EndY=39.2 EndZ=0
    g17: LineSegment [constr] StartX=-193.885 StartY=33.0037 StartZ=0 EndX=-197.644 EndY=34.3718 EndZ=0
    g18: LineSegment StartX=-195.887 StartY=39.2 StartZ=0 EndX=0 EndY=39.2 EndZ=0
    g19: LineSegment StartX=0 StartY=3.2 StartZ=0 EndX=0 EndY=39.2 EndZ=0
    g20: LineSegment StartX=-189.939 StartY=31.5672 StartZ=0 EndX=-192.333 EndY=24.9893 EndZ=0
    g21: LineSegment StartX=-196.467 StartY=26.4942 StartZ=0 EndX=-194.073 EndY=33.0721 EndZ=0
    g22: Circle CenterX=-213.443 CenterY=-76.8316 CenterZ=0 NormalX=0 NormalY=0 NormalZ=1 AngleXU=0 Radius=1.8
    g23: Circle CenterX=-179.305 CenterY=-76.8316 CenterZ=0 NormalX=0 NormalY=0 NormalZ=1 AngleXU=0 Radius=1.8
    g24: Circle CenterX=-184.08 CenterY=34.8 CenterZ=0 NormalX=0 NormalY=0 NormalZ=1 AngleXU=0 Radius=1.8
    g25: Circle CenterX=-78.51 CenterY=34.8 CenterZ=0 NormalX=0 NormalY=0 NormalZ=1 AngleXU=0 Radius=1.8
    g26: Circle CenterX=-78.51 CenterY=7.6 CenterZ=0 NormalX=0 NormalY=0 NormalZ=1 AngleXU=0 Radius=1.8
    g27: Circle CenterX=-5.6 CenterY=34.8 CenterZ=0 NormalX=0 NormalY=0 NormalZ=1 AngleXU=0 Radius=1.8
    g28: Circle CenterX=-5.6 CenterY=7.6 CenterZ=0 NormalX=0 NormalY=0 NormalZ=1 AngleXU=0 Radius=1.8
    g29: LineSegment StartX=-190.127 StartY=31.6356 StartZ=0 EndX=-189.939 EndY=31.5672 EndZ=0
    g30: LineSegment StartX=-194.073 StartY=33.0721 StartZ=0 EndX=-193.885 EndY=33.0037 EndZ=0
    g31: LineSegment StartX=-193.885 StartY=33.0037 StartZ=0 EndX=-190.127 EndY=31.6356 EndZ=0
    g32: LineSegment StartX=-196.467 StartY=26.4942 StartZ=0 EndX=-192.333 EndY=24.9893 EndZ=0
    g33: LineSegment [constr] StartX=-4 StartY=21.2 StartZ=0 EndX=-87.91 EndY=21.2 EndZ=0
    g34: GeomPoint [constr] X=-4 Y=21.2 Z=0
    g35: LineSegment [constr] StartX=-15.2 StartY=33.7 StartZ=0 EndX=-15.2 EndY=8.7 EndZ=0
    g36: LineSegment [constr] StartX=-15.2 StartY=33.7 StartZ=0 EndX=-56.2 EndY=33.7 EndZ=0
    g37: LineSegment [constr] StartX=-15.2 StartY=8.7 StartZ=0 EndX=-56.2 EndY=8.7 EndZ=0
    g38: LineSegment [constr] StartX=-56.2 StartY=33.7 StartZ=0 EndX=-56.2 EndY=8.7 EndZ=0
    g39: Circle CenterX=-18.6 CenterY=30.3 CenterZ=0 NormalX=0 NormalY=0 NormalZ=1 AngleXU=0 Radius=3.4
    g40: Circle CenterX=-18.6 CenterY=12.1 CenterZ=0 NormalX=0 NormalY=0 NormalZ=1 AngleXU=0 Radius=3.4
    g41: Circle CenterX=-43.2 CenterY=30.3 CenterZ=0 NormalX=0 NormalY=0 NormalZ=1 AngleXU=0 Radius=3.4
    g42: Circle CenterX=-43.2 CenterY=12.1 CenterZ=0 NormalX=0 NormalY=0 NormalZ=1 AngleXU=0 Radius=3.4
    g43: LineSegment [constr] StartX=-4 StartY=21.2 StartZ=0 EndX=-15.2 EndY=21.2 EndZ=0
    g44: LineSegment [constr] StartX=-15.2 StartY=21.2 StartZ=0 EndX=-36.2 EndY=21.2 EndZ=0
    g45: LineSegment [constr] StartX=-41.5 StartY=16.2 StartZ=0 EndX=-30.9 EndY=16.2 EndZ=0
    g46: LineSegment [constr] StartX=-30.9 StartY=16.2 StartZ=0 EndX=-30.9 EndY=26.2 EndZ=0
    g47: LineSegment [constr] StartX=-30.9 StartY=26.2 StartZ=0 EndX=-41.5 EndY=26.2 EndZ=0
    g48: LineSegment [constr] StartX=-41.5 StartY=26.2 StartZ=0 EndX=-41.5 EndY=16.2 EndZ=0
    g49: GeomPoint [constr] X=-36.2 Y=21.2 Z=0
    g50: Circle CenterX=-36.2 CenterY=21.2 CenterZ=0 NormalX=0 NormalY=0 NormalZ=1 AngleXU=0 Radius=2.8
    g51: LineSegment [constr] StartX=-24.2 StartY=26.7 StartZ=0 EndX=-24.2 EndY=15.7 EndZ=0
    g52: Circle CenterX=-24.2 CenterY=26.7 CenterZ=0 NormalX=0 NormalY=0 NormalZ=1 AngleXU=0 Radius=3
    g53: Circle CenterX=-24.2 CenterY=15.7 CenterZ=0 NormalX=0 NormalY=0 NormalZ=1 AngleXU=0 Radius=3
    g54: GeomPoint X=-18.6 Y=30.3 Z=0
    g55: GeomPoint X=-18.6 Y=12.1 Z=0
    g56: GeomPoint X=-43.2 Y=12.1 Z=0
    g57: GeomPoint X=-43.2 Y=30.3 Z=0
    g58: Circle CenterX=-65 CenterY=21.2 CenterZ=0 NormalX=0 NormalY=0 NormalZ=1 AngleXU=0 Radius=1.5
    g59: Circle CenterX=-42 CenterY=21.2 CenterZ=0 NormalX=0 NormalY=0 NormalZ=1 AngleXU=0 Radius=1.5
    g60: Circle CenterX=-19 CenterY=21.2 CenterZ=0 NormalX=0 NormalY=0 NormalZ=1 AngleXU=0 Radius=1.5
  constraints (149):
    c: Coincident(g0,g-41)
    c: Horizontal(g0)
    c: PointOnObject(g0,g-39)
    c: Coincident(g1,g0)
    c: Vertical(g1)
    c: DistanceY(g1,g1) = 3
    c: Coincident(g2,g-17)
    c: Vertical(g2)
    c: Coincident(g3,g-16)
    c: Vertical(g3)
    c: DistanceY(g2,g2) = 2
    c: DistanceY(g3,g3) = 2
    c: Coincident(g4,g3)
    c: Coincident(g4,g2)
    c: Coincident(g5,g-17)
    c: Coincident(g5,g2)
    c: Coincident(g6,g1)
    c: Horizontal(g6)
    c: Coincident(g6,g5)
    c: Coincident(g7,g-15)
    c: Coincident(g8,g7)
    c: Coincident(g8,g3)
    c: Coincident(g8,g-15)
    c: Horizontal(g9)
    c: DistanceY(g-13,g9) = 2
    c: Coincident(g10,g7)
    c: Parallel(g10,g-14)
    c: Coincident(g9,g10)
    c: Distance(g11) = 2
    c: Coincident(g11,g-11)
    c: Perpendicular(g-11,g11)
    c: Distance(g12) = 2
    c: Coincident(g12,g-12)
    c: Perpendicular(g-11,g12)
    c: Coincident(g13,g11)
    c: Coincident(g13,g12)
    c: Coincident(g14,g-32)
    c: Coincident(g14,g12)
    c: Coincident(g14,g9)
    c: Coincident(g15,g-10)
    c: Coincident(g15,g11)
    c: Parallel(g16,g-22)
    c: Distance(g17) = 4
    c: PointOnObject(g17,g16)
    c: Coincident(g15,g16)
    c: Horizontal(g18)
    c: Coincident(g18,g16)
    c: Coincident(g19,g0)
    c: PointOnObject(g19,g-39)
    c: DistanceY(g19,g-36) = 2
    c: Coincident(g18,g19)
    c: Diameter(g22) = 3.6
    c: Coincident(g22,g-9)
    c: Diameter(g23) = 3.6
    c: Coincident(g23,g-8)
    c: Diameter(g24) = 3.6
    c: Diameter(g25) = 3.6
    c: Diameter(g26) = 3.6
    c: Diameter(g27) = 3.6
    c: Diameter(g28) = 3.6
    c: Coincident(g27,g-4)
    c: Coincident(g28,g-3)
    c: Coincident(g25,g-6)
    c: Coincident(g26,g-5)
    c: Coincident(g24,g-7)
    c: Parallel(g20,g-21)
    c: Equal(g20,g-21)
    c: Parallel(g21,g-19)
    c: Equal(g21,g-19)
    c: Distance(g29) = 0.2
    c: Distance(g30) = 0.2
    c: Parallel(g29,g-20)
    c: Parallel(g31,g-20)
    c: Equal(g31,g-20)
    c: Coincident(g30,g31)
    c: Coincident(g31,g29)
    c: Coincident(g29,g-21)
    c: Parallel(g30,g31)
    c: Coincident(g17,g30)
    c: Coincident(g20,g29)
    c: Coincident(g21,g30)
    c: Perpendicular(g16,g17)
    c: Coincident(g32,g21)
    c: Coincident(g32,g20)
    c: Perpendicular(g10,g7)
    c: Horizontal(g33)
    c: Symmetric(g-24,g-24,g33)
    c: PointOnObject(g33,g-28)
    c: Symmetric(g-24,g-24,g34)
    c: DistanceY(g35,g35) = 25
    c: Symmetric(g35,g35,g33)
    c: Distance(g36) = 41
    c: Coincident(g36,g35)
    c: Horizontal(g36)
    c: Coincident(g37,g35)
    c: Horizontal(g37)
    c: Coincident(g38,g36)
    c: Vertical(g38)
    c: Coincident(g37,g38)
    c: Diameter(g39) = 6.8
    c: Diameter(g40) = 6.8
    c: Tangent(g39,g36)
    c: Tangent(g40,g37)
    c: Tangent(g39,g35)
    c: Tangent(g40,g35)
    c: Diameter(g41) = 6.8
    c: Diameter(g42) = 6.8
    c: Tangent(g41,g36)
    c: Tangent(g42,g37)
    c: DistanceX(g41,g39) = 24.6
    c: DistanceX(g42,g40) = 24.6
    c: Distance(g43) = 11.2
    c: Coincident(g43,g33)
    c: PointOnObject(g43,g33)
    c: PointOnObject(g43,g35)
    c: Distance(g44) = 21
    c: Coincident(g44,g43)
    c: PointOnObject(g44,g33)
    c: Coincident(g45,g46)
    c: Coincident(g46,g47)
    c: Coincident(g47,g48)
    c: Coincident(g48,g45)
    c: Horizontal(g45)
    c: Horizontal(g47)
    c: Vertical(g46)
    c: Vertical(g48)
    c: Symmetric(g47,g45,g49)
    c: Distance(g46,g48) = 10.6
    c: Distance(g45,g47) = 10
    c: Coincident(g49,g44)
    c: Diameter(g50) = 5.6
    c: Coincident(g50,g44)
    c: Distance(g51) = 11
    c: Symmetric(g51,g51,g33)
    c: DistanceX(g51,g43) = 9
    c: Diameter(g52) = 6
    c: Coincident(g52,g51)
    c: Diameter(g53) = 6
    c: Coincident(g53,g51)
    c: Coincident(g40,g55)
    c: Coincident(g39,g54)
    c: Coincident(g41,g57)
    c: Coincident(g42,g56)
    c: Diameter(g58) = 3
    c: Diameter(g59) = 3
    c: Diameter(g60) = 3
    c: Coincident(g58,g-44)
    c: Coincident(g59,g-46)
    c: Coincident(g60,g-45)
FEATURE [Sketcher::SketchObject] Sketch078
  ArcFitTolerance = 1e-06
  AttachmentSupport = -> [XZ_Plane005]
  FullyConstrained = true
  MakeInternals = false
  MapMode = 5
  Placement = pos=(0,0,0) rot=(1,0,0;1.5708rad)
  sketch-geometry (5):
    g0: LineSegment [constr] StartX=0 StartY=5.5 StartZ=0 EndX=0 EndY=-5.5 EndZ=0
    g1: ArcOfCircle CenterX=0 CenterY=5.5 CenterZ=0 NormalX=0 NormalY=0 NormalZ=1 AngleXU=0 Radius=2.7 StartAngle=0 EndAngle=3.14159
    g2: ArcOfCircle CenterX=0 CenterY=-5.5 CenterZ=0 NormalX=0 NormalY=0 NormalZ=1 AngleXU=0 Radius=2.7 StartAngle=3.1416 EndAngle=6.28318
    g3: LineSegment StartX=-2.7 StartY=5.5 StartZ=0 EndX=-2.7 EndY=-5.50001 EndZ=0
    g4: LineSegment StartX=2.7 StartY=5.5 StartZ=0 EndX=2.7 EndY=-5.50001 EndZ=0
  constraints (13):
    c: Distance(g0) = 11
    c: Vertical(g0)
    c: Symmetric(g0,g0,g-1)
    c: Radius(g1) = 2.7
    c: Coincident(g1,g0)
    c: Radius(g2) = 2.7
    c: Coincident(g2,g0)
    c: Vertical(g3)
    c: Vertical(g4)
    c: Coincident(g2,g4)
    c: Coincident(g2,g3)
    c: Tangent(g3,g1) = -1.5708
    c: Tangent(g4,g1) = 1.5708
FEATURE [PartDesign::Pad] Pad002
  Direction = (0,-1,2e-16)
  Length = 0.8
  Length2 = 10
  Placement = pos=(0,0,0) rot=(1,0,0;1.5708rad)
  Profile = -> Sketch078
  ReferenceAxis = -> Sketch078 [N_Axis]
  Refine = true
  Suppressed = false
  Type = 0
FEATURE [Sketcher::SketchObject] Sketch079
  ArcFitTolerance = 1e-06
  AttachmentSupport = -> [XZ_Plane005]
  ExternalGeometry = -> [Sketch078]
  FullyConstrained = true
  MakeInternals = false
  MapMode = 5
  Placement = pos=(0,0,0) rot=(1,0,0;1.5708rad)
  sketch-geometry (2):
    g0: Circle CenterX=-1e-16 CenterY=5.5 CenterZ=0 NormalX=0 NormalY=0 NormalZ=1 AngleXU=0 Radius=2.7
    g1: Circle CenterX=0 CenterY=-5.5 CenterZ=0 NormalX=0 NormalY=0 NormalZ=1 AngleXU=0 Radius=2.7
  constraints (4):
    c: Coincident(g0,g-3)
    c: PointOnObject(g-3,g0)
    c: Coincident(g1,g-4)
    c: Equal(g1,g-4)
FEATURE [PartDesign::Pad] Pad003
  BaseFeature = -> Pad002
  Direction = (0,-1,2e-16)
  Length = 5
  Length2 = 10
  Placement = pos=(0,0,0) rot=(1,0,0;1.5708rad)
  Profile = -> Sketch079
  ReferenceAxis = -> Sketch079 [N_Axis]
  Refine = true
  Suppressed = false
  Type = 0
FEATURE [PartDesign::Fillet] Fillet001
  Base = -> Pad003 [Edge16,Edge14]
  BaseFeature = -> Pad003
  Placement = pos=(0,0,0) rot=(1,0,0;1.5708rad)
  Radius = 0.4
  Refine = true
  SupportTransform = false
  Suppressed = false
  UseAllEdges = false
FEATURE [PartDesign::Body] Body005  label="pulsanti lato destro"
  AllowCompound = false
  Group = -> [Sketch078,Pad002,Sketch079,Pad003,Fillet001]
  Origin = -> Origin005
  Tip = -> Fillet001
FEATURE [PartDesign::SubShapeBinder] Binder
  BindCopyOnChange = 0
  BindMode = 0
  ClaimChildren = false
  Context = -> Body006 [Binder.]
  Fuse = false
  MakeFace = true
  OffsetFill = false
  OffsetIntersection = false
  OffsetJoinType = 0
  OffsetOpenResult = false
  PartialLoad = false
  Refine = true
  Relative = true
  Support = -> [Body[Sketch074.]]
  _Version = 2
FEATURE [PartDesign::SubShapeBinder] Binder001
  BindCopyOnChange = 0
  BindMode = 0
  ClaimChildren = false
  Context = -> Body007 [Binder001.]
  Fuse = false
  MakeFace = true
  OffsetFill = false
  OffsetIntersection = false
  OffsetJoinType = 0
  OffsetOpenResult = false
  PartialLoad = false
  Refine = true
  Relative = true
  Support = -> [Body[Sketch075.]]
  _Version = 2
FEATURE [Mesh::Feature] logo_per_PCB_definitivo_positivo
  Placement = pos=(-191,17,-66) rot=(0,1,1;0rad)
FEATURE [Sketcher::SketchObject] Sketch114  label="Sketch114 - base lato DX"
  ArcFitTolerance = 1e-06
  AttachmentSupport = -> [Binder001]
  ExternalGeometry = -> [Binder001]
  FullyConstrained = true
  MakeInternals = false
  MapMode = 5
  Placement = pos=(0,1e-15,0) rot=(0,0.707107,0.707107;3.14159rad)
  sketch-geometry (30):
    g0: Circle CenterX=5.6 CenterY=34.8 CenterZ=0 NormalX=0 NormalY=0 NormalZ=1 AngleXU=0 Radius=1.8
    g1: Circle CenterX=5.6 CenterY=7.6 CenterZ=0 NormalX=0 NormalY=0 NormalZ=1 AngleXU=0 Radius=1.8
    g2: Circle CenterX=24.2 CenterY=26.7 CenterZ=0 NormalX=0 NormalY=0 NormalZ=1 AngleXU=0 Radius=3
    g3: Circle CenterX=24.2 CenterY=15.7 CenterZ=0 NormalX=0 NormalY=0 NormalZ=1 AngleXU=0 Radius=3
    g4: Circle CenterX=36.2 CenterY=21.2 CenterZ=0 NormalX=0 NormalY=0 NormalZ=1 AngleXU=0 Radius=2.8
    g5: Circle CenterX=78.51 CenterY=34.8 CenterZ=0 NormalX=0 NormalY=0 NormalZ=1 AngleXU=0 Radius=1.8
    g6: Circle CenterX=78.51 CenterY=7.6 CenterZ=0 NormalX=0 NormalY=0 NormalZ=1 AngleXU=0 Radius=1.8
    g7: Circle CenterX=184.08 CenterY=34.8 CenterZ=0 NormalX=0 NormalY=0 NormalZ=1 AngleXU=0 Radius=1.8
    g8: Circle CenterX=213.443 CenterY=-76.8316 CenterZ=0 NormalX=0 NormalY=0 NormalZ=1 AngleXU=0 Radius=1.8
    g9: Circle CenterX=179.305 CenterY=-76.8316 CenterZ=0 NormalX=0 NormalY=0 NormalZ=1 AngleXU=0 Radius=1.8
    g10: ArcOfCircle [constr] CenterX=132.428 CenterY=4 CenterZ=0 NormalX=0 NormalY=0 NormalZ=1 AngleXU=0 Radius=16 StartAngle=0.314159 EndAngle=1.5708
    g11: ArcOfCircle CenterX=107.6 CenterY=4 CenterZ=0 NormalX=0 NormalY=0 NormalZ=1 AngleXU=0 Radius=16 StartAngle=1.5708 EndAngle=3.00366
    g12: ArcOfCircle CenterX=207.583 CenterY=4 CenterZ=0 NormalX=0 NormalY=0 NormalZ=1 AngleXU=0 Radius=17 StartAngle=1.85815 EndAngle=3.57792
    g13: ArcOfCircle CenterX=184.801 CenterY=-67.3089 CenterZ=0 NormalX=0 NormalY=0 NormalZ=1 AngleXU=0 Radius=33.7833 StartAngle=5.88425 EndAngle=6.71952
    g14: LineSegment StartX=0 StartY=39.2 StartZ=0 EndX=0 EndY=3.2 EndZ=0
    g15: LineSegment StartX=0 StartY=3.2 StartZ=0 EndX=82.8 EndY=3.2 EndZ=0
    g16: LineSegment StartX=82.8 StartY=3.2 StartZ=0 EndX=82.8 EndY=6.2 EndZ=0
    g17: LineSegment StartX=82.8 StartY=6.2 StartZ=0 EndX=91.752 EndY=6.2 EndZ=0
    g18: LineSegment StartX=107.6 StartY=20 StartZ=0 EndX=132.428 EndY=20 EndZ=0
    g19: LineSegment StartX=147.645 StartY=8.94427 StartZ=0 EndX=176.685 EndY=-80.4316 EndZ=0
    g20: LineSegment StartX=176.685 StartY=-80.4316 StartZ=0 EndX=215.932 EndY=-80.4316 EndZ=0
    g21: LineSegment StartX=215.42 StartY=-53.0314 StartZ=0 EndX=192.176 EndY=-3.18451 EndZ=0
    g22: LineSegment StartX=202.765 StartY=20.303 StartZ=0 EndX=195.887 EndY=39.2 EndZ=0
    g23: LineSegment StartX=195.887 StartY=39.2 StartZ=0 EndX=0 EndY=39.2 EndZ=0
    g24: LineSegment StartX=196.467 StartY=26.4942 StartZ=0 EndX=194.073 EndY=33.0721 EndZ=0
    g25: LineSegment StartX=194.073 StartY=33.0721 StartZ=0 EndX=189.939 EndY=31.5672 EndZ=0
    g26: LineSegment StartX=189.939 StartY=31.5672 StartZ=0 EndX=192.333 EndY=24.9893 EndZ=0
    g27: LineSegment StartX=192.333 StartY=24.9893 StartZ=0 EndX=196.467 EndY=26.4942 EndZ=0
    g28: LineSegment StartX=132.428 StartY=20 StartZ=0 EndX=144.053 EndY=20 EndZ=0
    g29: LineSegment StartX=144.053 StartY=20 StartZ=0 EndX=147.645 EndY=8.94427 EndZ=0
  constraints (65):
    c: Equal(g0,g-25)
    c: Equal(g2,g-29)
    c: Equal(g3,g-30)
    c: Equal(g4,g-28)
    c: Equal(g1,g-26)
    c: Coincident(g0,g-25)
    c: Coincident(g1,g-26)
    c: Coincident(g2,g-29)
    c: Coincident(g3,g-30)
    c: Coincident(g4,g-28)
    c: Equal(g5,g-23)
    c: Equal(g6,g-24)
    c: Coincident(g5,g-23)
    c: Coincident(g6,g-24)
    c: Equal(g7,g-20)
    c: Coincident(g7,g-20)
    c: Equal(g9,g-22)
    c: Coincident(g9,g-22)
    c: Equal(g8,g-21)
    c: Coincident(g8,g-21)
    c: Equal(g13,g-12)
    c: Equal(g12,g-14)
    c: Equal(g10,g-9)
    c: Equal(g11,g-7)
    c: Coincident(g14,g-27)
    c: Coincident(g14,g-27)
    c: Coincident(g15,g14)
    c: Coincident(g15,g-5)
    c: Coincident(g16,g15)
    c: Coincident(g16,g-6)
    c: Coincident(g17,g16)
    c: Coincident(g17,g-7)
    c: Coincident(g11,g17)
    c: Coincident(g11,g-8)
    c: Coincident(g18,g11)
    c: Coincident(g18,g-9)
    c: Coincident(g10,g18)
    c: Coincident(g10,g-10)
    c: Coincident(g19,g10)
    c: Coincident(g19,g-11)
    c: Coincident(g20,g19)
    c: Coincident(g20,g-12)
    c: Coincident(g13,g20)
    c: Coincident(g13,g-13)
    c: Coincident(g21,g13)
    c: Coincident(g21,g-14)
    c: Coincident(g12,g21)
    c: Coincident(g12,g-15)
    c: Coincident(g22,g12)
    c: Coincident(g22,g-15)
    c: Coincident(g23,g22)
    c: Coincident(g23,g14)
    c: Coincident(g24,g-18)
    c: Coincident(g24,g-16)
    c: Coincident(g25,g24)
    c: Coincident(g25,g-19)
    c: Coincident(g26,g25)
    c: Coincident(g26,g-19)
    c: Coincident(g27,g26)
    c: Coincident(g27,g24)
    c: Coincident(g29,g10)
    c: Coincident(g28,g10)
    c: Coincident(g29,g28)
    c: Parallel(g28,g18)
    c: Parallel(g29,g19)
FEATURE [PartDesign::Pad] Pad011
  Direction = (0,1,-2e-16)
  Length = 2
  Length2 = 10
  Profile = -> Sketch114
  ReferenceAxis = -> Sketch114 [N_Axis]
  Refine = true
  Reversed = true
  Suppressed = false
  Type = 0
FEATURE [Sketcher::SketchObject] Sketch115
  ArcFitTolerance = 1e-06
  AttachmentSupport = -> [Pad011]
  ExternalGeometry = -> [Binder001]
  FullyConstrained = true
  MakeInternals = false
  MapMode = 5
  Placement = pos=(0,1.7e-15,0) rot=(0,0.707107,0.707107;3.14159rad)
  sketch-geometry (4):
    g0: ArcOfCircle CenterX=24.2 CenterY=26.7 CenterZ=0 NormalX=0 NormalY=0 NormalZ=1 AngleXU=0 Radius=3 StartAngle=4.48384e-08 EndAngle=3.14159
    g1: ArcOfCircle CenterX=24.2 CenterY=15.7 CenterZ=0 NormalX=0 NormalY=0 NormalZ=1 AngleXU=0 Radius=3 StartAngle=3.14159 EndAngle=6.28318
    g2: LineSegment StartX=21.2 StartY=26.7 StartZ=0 EndX=21.2 EndY=15.7 EndZ=0
    g3: LineSegment StartX=27.2 StartY=26.7 StartZ=0 EndX=27.2 EndY=15.7 EndZ=0
  constraints (12):
    c: Equal(g1,g-4)
    c: Equal(g0,g-3)
    c: Coincident(g0,g-3)
    c: Coincident(g1,g-4)
    c: Vertical(g2)
    c: Vertical(g3)
    c: Tangent(g3,g-3)
    c: Tangent(g2,g-3)
    c: Coincident(g0,g2)
    c: Coincident(g0,g3)
    c: Coincident(g1,g2)
    c: Coincident(g3,g1)
FEATURE [Sketcher::SketchObject] Sketch117  label="Sketch117 - fori per inserto M3 x 3 x 4.5"
  ArcFitTolerance = 1e-06
  AttachmentSupport = -> [Pad011]
  ExternalGeometry = -> [Binder001]
  FullyConstrained = true
  MakeInternals = false
  MapMode = 5
  Placement = pos=(0,1.7e-15,0) rot=(0,0.707107,0.707107;3.14159rad)
  sketch-geometry (4):
    g0: Circle CenterX=43.2 CenterY=30.3 CenterZ=0 NormalX=0 NormalY=0 NormalZ=1 AngleXU=0 Radius=2.25
    g1: Circle CenterX=43.2 CenterY=12.1 CenterZ=0 NormalX=0 NormalY=0 NormalZ=1 AngleXU=0 Radius=2.25
    g2: Circle CenterX=18.6 CenterY=30.3 CenterZ=0 NormalX=0 NormalY=0 NormalZ=1 AngleXU=0 Radius=2.25
    g3: Circle CenterX=18.6 CenterY=12.1 CenterZ=0 NormalX=0 NormalY=0 NormalZ=1 AngleXU=0 Radius=2.25
  constraints (8):
    c: Diameter(g0) = 4.5
    c: Diameter(g1) = 4.5
    c: Diameter(g2) = 4.5
    c: Diameter(g3) = 4.5
    c: Coincident(g2,g-3)
    c: Coincident(g3,g-6)
    c: Coincident(g0,g-4)
    c: Coincident(g1,g-5)
FEATURE [Sketcher::SketchObject] Sketch118
  ArcFitTolerance = 1e-06
  AttachmentSupport = -> [Pad011]
  ExternalGeometry = -> [Binder001]
  FullyConstrained = true
  MakeInternals = false
  MapMode = 5
  Placement = pos=(0,-2,0) rot=(1,0,0;1.5708rad)
  sketch-geometry (12):
    g0: Circle CenterX=-78.51 CenterY=34.8 CenterZ=0 NormalX=0 NormalY=0 NormalZ=1 AngleXU=0 Radius=1.8
    g1: Circle CenterX=-78.51 CenterY=7.6 CenterZ=0 NormalX=0 NormalY=0 NormalZ=1 AngleXU=0 Radius=1.8
    g2: Circle CenterX=-5.6 CenterY=34.8 CenterZ=0 NormalX=0 NormalY=0 NormalZ=1 AngleXU=0 Radius=1.8
    g3: Circle CenterX=-5.6 CenterY=7.6 CenterZ=0 NormalX=0 NormalY=0 NormalZ=1 AngleXU=0 Radius=1.8
    g4: LineSegment StartX=0 StartY=39.2 StartZ=0 EndX=0 EndY=3.2 EndZ=0
    g5: LineSegment StartX=0 StartY=3.2 StartZ=0 EndX=-82.8 EndY=3.2 EndZ=0
    g6: LineSegment StartX=-82.8 StartY=3.2 StartZ=0 EndX=-82.8 EndY=39.2 EndZ=0
    g7: LineSegment StartX=-82.8 StartY=39.2 StartZ=0 EndX=0 EndY=39.2 EndZ=0
    g8: ArcOfCircle CenterX=-65 CenterY=21.2 CenterZ=0 NormalX=0 NormalY=0 NormalZ=1 AngleXU=0 Radius=10 StartAngle=1.5708 EndAngle=4.71239
    g9: ArcOfCircle CenterX=-19 CenterY=21.2 CenterZ=0 NormalX=0 NormalY=0 NormalZ=1 AngleXU=0 Radius=10 StartAngle=4.71239 EndAngle=7.85398
    g10: LineSegment StartX=-65 StartY=31.2 StartZ=0 EndX=-19 EndY=31.2 EndZ=0
    g11: LineSegment StartX=-65 StartY=11.2 StartZ=0 EndX=-19 EndY=11.2 EndZ=0
  constraints (25):
    c: Equal(g2,g-5)
    c: Equal(g3,g-7)
    c: Equal(g1,g-6)
    c: Equal(g0,g-4)
    c: Coincident(g0,g-4)
    c: Coincident(g1,g-6)
    c: Coincident(g3,g-7)
    c: Coincident(g2,g-5)
    c: Coincident(g4,g-8)
    c: Coincident(g4,g-9)
    c: Coincident(g5,g4)
    c: Coincident(g5,g-10)
    c: Coincident(g6,g5)
    c: PointOnObject(g6,g-3)
    c: Vertical(g6)
    c: Coincident(g7,g6)
    c: Coincident(g7,g4)
    c: Tangent(g8,g10) = 1.5708
    c: Tangent(g8,g11) = -1.5708
    c: Tangent(g9,g10) = 1.5708
    c: Tangent(g9,g11) = -1.5708
    c: Equal(g8,g9)
    c: Radius(g8) = 10
    c: Coincident(g8,g-11)
    c: Coincident(g9,g-12)
FEATURE [Sketcher::SketchObject] Sketch120
  ArcFitTolerance = 1e-06
  AttachmentSupport = -> [Pad011]
  ExternalGeometry = -> [Binder001]
  FullyConstrained = true
  MakeInternals = false
  MapMode = 5
  Placement = pos=(0,-2,0) rot=(1,0,0;1.5708rad)
  sketch-geometry (4):
    g0: LineSegment StartX=-137.815 StartY=39.2 StartZ=0 EndX=-142.655 EndY=24.303 EndZ=0
    g1: LineSegment StartX=-137.815 StartY=39.2 StartZ=0 EndX=-110.815 EndY=39.2 EndZ=0
    g2: LineSegment StartX=-142.655 StartY=24.303 StartZ=0 EndX=-110.815 EndY=24.303 EndZ=0
    g3: ArcOfCircle CenterX=-92.2534 CenterY=31.7515 CenterZ=0 NormalX=0 NormalY=0 NormalZ=1 AngleXU=0 Radius=20 StartAngle=2.75997 EndAngle=3.52321
  constraints (12):
    c: PointOnObject(g0,g-3)
    c: Coincident(g1,g0)
    c: PointOnObject(g1,g-3)
    c: Coincident(g2,g0)
    c: Horizontal(g2)
    c: Tangent(g0,g-4)
    c: Vertical(g2,g1)
    c: DistanceX(g1,g1) = 27
    c: DistanceY(g-6,g0) = 4
    c: Radius(g3) = 20
    c: Coincident(g3,g1)
    c: Coincident(g3,g2)
FEATURE [Sketcher::SketchObject] Sketch121
  ArcFitTolerance = 1e-06
  AttachmentSupport = -> [Pad011]
  ExternalGeometry = -> [Binder001]
  FullyConstrained = true
  MakeInternals = false
  MapMode = 5
  Placement = pos=(0,-2,0) rot=(1,0,0;1.5708rad)
  sketch-geometry (15):
    g0: LineSegment StartX=-137.815 StartY=39.2 StartZ=0 EndX=-143.955 EndY=20.303 EndZ=0
    g1: LineSegment StartX=-143.955 StartY=20.303 StartZ=0 EndX=-190.141 EndY=20.303 EndZ=0
    g2: LineSegment StartX=-190.141 StartY=20.303 StartZ=0 EndX=-186.139 EndY=31.3 EndZ=0
    g3: LineSegment StartX=-178.754 StartY=39.2 StartZ=0 EndX=-180.791 EndY=33.6029 EndZ=0
    g4: ArcOfCircle CenterX=-184.08 CenterY=34.8 CenterZ=0 NormalX=0 NormalY=0 NormalZ=1 AngleXU=0 Radius=3.5 StartAngle=4.71239 EndAngle=5.93412
    g5: LineSegment StartX=-184.08 StartY=31.3 StartZ=0 EndX=-186.139 EndY=31.3 EndZ=0
    g6: LineSegment StartX=-137.815 StartY=39.2 StartZ=0 EndX=-156.815 EndY=39.2 EndZ=0
    g7: LineSegment StartX=-168.815 StartY=39.2 StartZ=0 EndX=-178.754 EndY=39.2 EndZ=0
    g8: LineSegment StartX=-157.815 StartY=39.2 StartZ=0 EndX=-167.815 EndY=39.2 EndZ=0
    g9: LineSegment StartX=-168.815 StartY=31.2 StartZ=0 EndX=-156.815 EndY=31.2 EndZ=0
    g10: LineSegment StartX=-167.436 StartY=36.2 StartZ=0 EndX=-157.436 EndY=36.2 EndZ=0
    g11: ArcOfCircle CenterX=-176.411 CenterY=35.2 CenterZ=0 NormalX=0 NormalY=0 NormalZ=1 AngleXU=0 Radius=20 StartAngle=6.08183 EndAngle=6.48454
    g12: ArcOfCircle CenterX=-188.411 CenterY=35.2 CenterZ=0 NormalX=0 NormalY=0 NormalZ=1 AngleXU=0 Radius=20 StartAngle=6.08183 EndAngle=6.48454
    g13: ArcOfCircle CenterX=-177.411 CenterY=35.2 CenterZ=0 NormalX=0 NormalY=0 NormalZ=1 AngleXU=0 Radius=20 StartAngle=0.0500209 EndAngle=0.201358
    g14: ArcOfCircle CenterX=-187.411 CenterY=35.2 CenterZ=0 NormalX=0 NormalY=0 NormalZ=1 AngleXU=0 Radius=20 StartAngle=0.0500209 EndAngle=0.201358
  constraints (46):
    c: PointOnObject(g0,g-3)
    c: Tangent(g0,g-5)
    c: Coincident(g1,g0)
    c: Horizontal(g1)
    c: Coincident(g2,g1)
    c: PointOnObject(g3,g-3)
    c: Parallel(g3,g-6)
    c: Parallel(g2,g-6)
    c: Radius(g4) = 3.5
    c: Coincident(g4,g-7)
    c: Tangent(g3,g4) = 1.5708
    c: Horizontal(g5)
    c: Tangent(g5,g4) = 1.5708
    c: DistanceX(g-8,g5) = 3.8
    c: Coincident(g2,g5)
    c: Coincident(g6,g0)
    c: PointOnObject(g6,g-3)
    c: DistanceX(g6,g6) = 19
    c: PointOnObject(g7,g-3)
    c: DistanceX(g7,g6) = 12
    c: Coincident(g7,g3)
    c: PointOnObject(g8,g-3)
    c: PointOnObject(g8,g-3)
    c: DistanceX(g8,g8) = 10
    c: DistanceX(g8,g6) = 1
    c: Horizontal(g9)
    c: Vertical(g7,g9)
    c: Vertical(g6,g9)
    c: DistanceY(g9,g7) = 8
    c: Horizontal(g10)
    c: Equal(g8,g10)
    c: DistanceY(g10,g8) = 3
    c: Radius(g11) = 20
    c: Coincident(g11,g6)
    c: Coincident(g11,g9)
    c: Radius(g12) = 20
    c: Coincident(g12,g7)
    c: Coincident(g12,g9)
    c: Equal(g13,g11)
    c: Coincident(g13,g8)
    c: Coincident(g13,g10)
    c: Horizontal(g13,g11)
    c: Equal(g14,g12)
    c: Coincident(g14,g8)
    c: Coincident(g14,g10)
    c: Horizontal(g1,g-6)
FEATURE [Sketcher::SketchObject] Sketch122
  ArcFitTolerance = 1e-06
  AttachmentSupport = -> [Pad011]
  ExternalGeometry = -> [Binder001]
  FullyConstrained = true
  MakeInternals = false
  MapMode = 5
  Placement = pos=(0,-2,0) rot=(1,0,0;1.5708rad)
  sketch-geometry (8):
    g0: ArcOfCircle CenterX=-184.801 CenterY=-67.3089 CenterZ=0 NormalX=0 NormalY=0 NormalZ=1 AngleXU=0 Radius=33.7833 StartAngle=2.70526 EndAngle=3.54053
    g1: LineSegment StartX=-176.685 StartY=-80.4316 StartZ=0 EndX=-215.932 EndY=-80.4316 EndZ=0
    g2: LineSegment StartX=-215.42 StartY=-53.0314 StartZ=0 EndX=-192.176 EndY=-3.18454 EndZ=0
    g3: ArcOfCircle CenterX=-207.583 CenterY=4 CenterZ=0 NormalX=0 NormalY=0 NormalZ=1 AngleXU=0 Radius=17 StartAngle=5.84685 EndAngle=7.56663
    g4: Circle CenterX=-213.443 CenterY=-76.8316 CenterZ=0 NormalX=0 NormalY=0 NormalZ=1 AngleXU=0 Radius=3
    g5: Circle CenterX=-179.305 CenterY=-76.8316 CenterZ=0 NormalX=0 NormalY=0 NormalZ=1 AngleXU=0 Radius=3
    g6: LineSegment StartX=-143.955 StartY=20.303 StartZ=0 EndX=-176.685 EndY=-80.4316 EndZ=0
    g7: LineSegment StartX=-202.765 StartY=20.303 StartZ=0 EndX=-143.955 EndY=20.303 EndZ=0
  constraints (18):
    c: Coincident(g0,g-7)
    c: Coincident(g0,g-8)
    c: Coincident(g1,g0)
    c: Tangent(g2,g-5)
    c: Coincident(g3,g-6)
    c: Coincident(g2,g3)
    c: Coincident(g0,g2)
    c: Diameter(g4) = 6
    c: Diameter(g5) = 6
    c: Coincident(g4,g-9)
    c: Coincident(g5,g-10)
    c: Horizontal(g1)
    c: Coincident(g6,g1)
    c: Tangent(g6,g-4)
    c: Coincident(g3,g-6)
    c: Coincident(g7,g3)
    c: Horizontal(g7)
    c: Coincident(g7,g6)
FEATURE [Sketcher::SketchObject] Sketch123
  ArcFitTolerance = 1e-06
  AttachmentSupport = -> [Pad011]
  ExternalGeometry = -> [Binder001]
  FullyConstrained = true
  MakeInternals = false
  MapMode = 5
  Placement = pos=(0,-2,0) rot=(1,0,0;1.5708rad)
  sketch-geometry (4):
    g0: LineSegment StartX=-108 StartY=36.8 StartZ=0 EndX=-90 EndY=36.8 EndZ=0
    g1: LineSegment StartX=-108 StartY=36.8 StartZ=0 EndX=-108 EndY=26.8 EndZ=0
    g2: LineSegment StartX=-108 StartY=26.8 StartZ=0 EndX=-90 EndY=26.8 EndZ=0
    g3: ArcOfCircle CenterX=-94 CenterY=31.8 CenterZ=0 NormalX=0 NormalY=0 NormalZ=1 AngleXU=0 Radius=6.40312 StartAngle=5.38713 EndAngle=7.17924
  constraints (13):
    c: Horizontal(g0)
    c: Coincident(g1,g0)
    c: Vertical(g1)
    c: Coincident(g2,g1)
    c: Horizontal(g2)
    c: DistanceX(g0,g0) = 18
    c: DistanceY(g1,g1) = 10
    c: Equal(g0,g2)
    c: DistanceX(g0,g-3) = 90
    c: DistanceY(g0,g-3) = 2.4
    c: Coincident(g3,g0)
    c: Coincident(g3,g2)
    c: DistanceX(g3,g0) = 4
FEATURE [PartDesign::Chamfer] Chamfer014
  Angle = 45
  Base = -> Pad011 [Edge80,Edge4,Edge7]
  BaseFeature = -> Pad011
  ChamferType = 0
  FlipDirection = false
  Refine = true
  Size = 1.9
  Size2 = 1
  SupportTransform = false
  Suppressed = false
  UseAllEdges = false
FEATURE [PartDesign::Pocket] Pocket006
  BaseFeature = -> Chamfer014
  Direction = (0,-1,2e-16)
  Length = 1.2
  Length2 = 5
  Profile = -> Sketch115
  ReferenceAxis = -> Sketch115 [N_Axis]
  Refine = true
  Suppressed = false
  Type = 0
FEATURE [Sketcher::SketchObject] Sketch116  label="Sketch116 - pieno per inserto M3 x 3 x 4,5"
  ArcFitTolerance = 1e-06
  AttachmentSupport = -> [Pocket006]
  ExternalGeometry = -> [Binder001]
  FullyConstrained = true
  MakeInternals = false
  MapMode = 5
  Placement = pos=(0,1.7e-15,0) rot=(0,0.707107,0.707107;3.14159rad)
  sketch-geometry (4):
    g0: Circle CenterX=43.2 CenterY=30.3 CenterZ=0 NormalX=0 NormalY=0 NormalZ=1 AngleXU=0 Radius=3.4
    g1: Circle CenterX=43.2 CenterY=12.1 CenterZ=0 NormalX=0 NormalY=0 NormalZ=1 AngleXU=0 Radius=3.4
    g2: Circle CenterX=18.6 CenterY=30.3 CenterZ=0 NormalX=0 NormalY=0 NormalZ=1 AngleXU=0 Radius=3.4
    g3: Circle CenterX=18.6 CenterY=12.1 CenterZ=0 NormalX=0 NormalY=0 NormalZ=1 AngleXU=0 Radius=3.4
  constraints (8):
    c: Diameter(g0) = 6.8
    c: Diameter(g1) = 6.8
    c: Diameter(g2) = 6.8
    c: Diameter(g3) = 6.8
    c: Coincident(g2,g-3)
    c: Coincident(g0,g-4)
    c: Coincident(g3,g-6)
    c: Coincident(g1,g-5)
FEATURE [PartDesign::Pad] Pad012
  BaseFeature = -> Pocket006
  Direction = (0,1,-2e-16)
  Length = 2.4
  Length2 = 10
  Profile = -> Sketch116
  ReferenceAxis = -> Sketch116 [N_Axis]
  Refine = true
  Suppressed = false
  Type = 0
FEATURE [PartDesign::Pocket] Pocket007
  BaseFeature = -> Pad012
  Direction = (0,-1,2e-16)
  Length = 0.6
  Length2 = 2.4
  Profile = -> Sketch117
  ReferenceAxis = -> Sketch117 [N_Axis]
  Refine = true
  Suppressed = false
  Type = 4
FEATURE [PartDesign::Pad] Pad013
  BaseFeature = -> Pocket007
  Direction = (0,-1,2e-16)
  Length = 1.6
  Length2 = 10
  Profile = -> Sketch118
  ReferenceAxis = -> Sketch118 [N_Axis]
  Refine = true
  Suppressed = false
  Type = 0
FEATURE [Sketcher::SketchObject] Sketch119
  ArcFitTolerance = 1e-06
  AttachmentSupport = -> [Pad013]
  ExternalGeometry = -> [Binder001]
  FullyConstrained = true
  MakeInternals = false
  MapMode = 5
  Placement = pos=(0,-3.6,0) rot=(1,0,0;1.5708rad)
  sketch-geometry (21):
    g0: LineSegment [constr] StartX=-82.8 StartY=3.2 StartZ=0 EndX=-82.8 EndY=39.2 EndZ=0
    g1: ArcOfCircle CenterX=-78.51 CenterY=34.8 CenterZ=0 NormalX=0 NormalY=0 NormalZ=1 AngleXU=0 Radius=3.5 StartAngle=4.71239 EndAngle=6.28319
    g2: ArcOfCircle CenterX=-78.51 CenterY=7.6 CenterZ=0 NormalX=0 NormalY=0 NormalZ=1 AngleXU=0 Radius=3.5 StartAngle=0 EndAngle=1.5708
    g3: ArcOfCircle CenterX=-5.6 CenterY=34.8 CenterZ=0 NormalX=0 NormalY=0 NormalZ=1 AngleXU=0 Radius=3.5 StartAngle=3.14159 EndAngle=4.71239
    g4: ArcOfCircle CenterX=-5.6 CenterY=7.6 CenterZ=0 NormalX=0 NormalY=0 NormalZ=1 AngleXU=0 Radius=3.5 StartAngle=1.5708 EndAngle=3.14159
    g5: LineSegment StartX=0 StartY=39.2 StartZ=0 EndX=0 EndY=31.3 EndZ=0
    g6: LineSegment StartX=0 StartY=39.2 StartZ=0 EndX=-9.1 EndY=39.2 EndZ=0
    g7: LineSegment StartX=0 StartY=3.2 StartZ=0 EndX=0 EndY=11.1 EndZ=0
    g8: LineSegment StartX=0 StartY=3.2 StartZ=0 EndX=-9.1 EndY=3.2 EndZ=0
    g9: LineSegment StartX=-82.8 StartY=3.2 StartZ=0 EndX=-75.01 EndY=3.2 EndZ=0
    g10: LineSegment StartX=-82.8 StartY=3.2 StartZ=0 EndX=-82.8 EndY=11.1 EndZ=0
    g11: LineSegment StartX=-82.8 StartY=39.2 StartZ=0 EndX=-82.8 EndY=31.3 EndZ=0
    g12: LineSegment StartX=-82.8 StartY=39.2 StartZ=0 EndX=-75.01 EndY=39.2 EndZ=0
    g13: LineSegment StartX=-82.8 StartY=31.3 StartZ=0 EndX=-78.51 EndY=31.3 EndZ=0
    g14: LineSegment StartX=-75.01 StartY=39.2 StartZ=0 EndX=-75.01 EndY=34.8 EndZ=0
    g15: LineSegment StartX=-82.8 StartY=11.1 StartZ=0 EndX=-78.51 EndY=11.1 EndZ=0
    g16: LineSegment StartX=-75.01 StartY=3.2 StartZ=0 EndX=-75.01 EndY=7.6 EndZ=0
    g17: LineSegment StartX=-9.1 StartY=39.2 StartZ=0 EndX=-9.1 EndY=34.8 EndZ=0
    g18: LineSegment StartX=0 StartY=31.3 StartZ=0 EndX=-5.6 EndY=31.3 EndZ=0
    g19: LineSegment StartX=0 StartY=11.1 StartZ=0 EndX=-5.6 EndY=11.1 EndZ=0
    g20: LineSegment StartX=-9.1 StartY=3.2 StartZ=0 EndX=-9.1 EndY=7.6 EndZ=0
  constraints (51):
    c: Coincident(g0,g-10)
    c: PointOnObject(g0,g-8)
    c: Vertical(g0)
    c: Coincident(g1,g-3)
    c: Coincident(g2,g-4)
    c: Coincident(g3,g-5)
    c: Coincident(g4,g-6)
    c: Radius(g4) = 3.5
    c: Radius(g3) = 3.5
    c: Radius(g1) = 3.5
    c: Radius(g2) = 3.5
    c: Coincident(g5,g-9)
    c: PointOnObject(g5,g-9)
    c: Coincident(g6,g5)
    c: PointOnObject(g6,g-8)
    c: Coincident(g7,g-9)
    c: PointOnObject(g7,g-9)
    c: Coincident(g8,g7)
    c: PointOnObject(g8,g-7)
    c: Coincident(g9,g0)
    c: PointOnObject(g9,g-7)
    c: Coincident(g10,g0)
    c: PointOnObject(g10,g0)
    c: Coincident(g11,g0)
    c: PointOnObject(g11,g0)
    c: Coincident(g12,g0)
    c: PointOnObject(g12,g-8)
    c: Coincident(g13,g11)
    c: Horizontal(g13)
    c: Coincident(g14,g12)
    c: Vertical(g14)
    c: Coincident(g15,g10)
    c: Horizontal(g15)
    c: Coincident(g16,g9)
    c: Vertical(g16)
    c: Coincident(g17,g6)
    c: Vertical(g17)
    c: Coincident(g18,g5)
    c: Horizontal(g18)
    c: Coincident(g19,g7)
    c: Horizontal(g19)
    c: Coincident(g20,g8)
    c: Vertical(g20)
    c: Tangent(g20,g4) = 1.5708
    c: Tangent(g4,g19) = -1.5708
    c: Tangent(g18,g3) = 1.5708
    c: Tangent(g3,g17) = -1.5708
    c: Tangent(g13,g1) = -1.5708
    c: Tangent(g1,g14) = 1.5708
    c: Tangent(g16,g2) = -1.5708
    c: Tangent(g2,g15) = 1.5708
FEATURE [PartDesign::Pocket] Pocket008
  BaseFeature = -> Pad013
  Direction = (0,1,-2e-16)
  Length = 1.6
  Length2 = 5
  Profile = -> Sketch119
  ReferenceAxis = -> Sketch119 [N_Axis]
  Refine = true
  Suppressed = false
  Type = 0
FEATURE [PartDesign::Pad] Pad017
  BaseFeature = -> Pocket008
  Direction = (0,-1,2e-16)
  Length = 1.6
  Length2 = 10
  Profile = -> Sketch123
  ReferenceAxis = -> Sketch123 [N_Axis]
  Refine = true
  Suppressed = false
  Type = 0
FEATURE [Sketcher::SketchObject] Sketch125
  ArcFitTolerance = 1e-06
  AttachmentSupport = -> [Pad017]
  ExternalGeometry = -> [Pad017]
  FullyConstrained = true
  MakeInternals = false
  MapMode = 5
  Placement = pos=(0,-3.6,8e-16) rot=(1,0,0;1.5708rad)
  sketch-geometry (20):
    g0: LineSegment StartX=-108 StartY=35.8 StartZ=0 EndX=-108 EndY=35 EndZ=0
    g1: LineSegment StartX=-108 StartY=35 StartZ=0 EndX=-97 EndY=35 EndZ=0
    g2: LineSegment StartX=-97 StartY=35 StartZ=0 EndX=-97 EndY=35.8 EndZ=0
    g3: LineSegment StartX=-97 StartY=35.8 StartZ=0 EndX=-108 EndY=35.8 EndZ=0
    g4: LineSegment StartX=-108 StartY=28.6 StartZ=0 EndX=-108 EndY=27.8 EndZ=0
    g5: LineSegment StartX=-108 StartY=27.8 StartZ=0 EndX=-97 EndY=27.8 EndZ=0
    g6: LineSegment StartX=-97 StartY=27.8 StartZ=0 EndX=-97 EndY=28.6 EndZ=0
    g7: LineSegment StartX=-97 StartY=28.6 StartZ=0 EndX=-108 EndY=28.6 EndZ=0
    g8: LineSegment StartX=-108 StartY=30.4 StartZ=0 EndX=-108 EndY=29.6 EndZ=0
    g9: LineSegment StartX=-108 StartY=29.6 StartZ=0 EndX=-97 EndY=29.6 EndZ=0
    g10: LineSegment StartX=-97 StartY=29.6 StartZ=0 EndX=-97 EndY=30.4 EndZ=0
    g11: LineSegment StartX=-97 StartY=30.4 StartZ=0 EndX=-108 EndY=30.4 EndZ=0
    g12: LineSegment StartX=-108 StartY=32.2 StartZ=0 EndX=-108 EndY=31.4 EndZ=0
    g13: LineSegment StartX=-108 StartY=31.4 StartZ=0 EndX=-97 EndY=31.4 EndZ=0
    g14: LineSegment StartX=-97 StartY=31.4 StartZ=0 EndX=-97 EndY=32.2 EndZ=0
    g15: LineSegment StartX=-97 StartY=32.2 StartZ=0 EndX=-108 EndY=32.2 EndZ=0
    g16: LineSegment StartX=-108 StartY=34 StartZ=0 EndX=-108 EndY=33.2 EndZ=0
    g17: LineSegment StartX=-108 StartY=33.2 StartZ=0 EndX=-97 EndY=33.2 EndZ=0
    g18: LineSegment StartX=-97 StartY=33.2 StartZ=0 EndX=-97 EndY=34 EndZ=0
    g19: LineSegment StartX=-97 StartY=34 StartZ=0 EndX=-108 EndY=34 EndZ=0
  constraints (55):
    c: Coincident(g1,g0)
    c: Horizontal(g1)
    c: Coincident(g2,g1)
    c: Vertical(g2)
    c: Coincident(g3,g2)
    c: Horizontal(g3)
    c: Coincident(g3,g0)
    c: DistanceX(g1,g1) = 11
    c: DistanceY(g2,g2) = 0.8
    c: Coincident(g5,g4)
    c: Horizontal(g5)
    c: Coincident(g6,g5)
    c: Vertical(g6)
    c: Coincident(g7,g6)
    c: Horizontal(g7)
    c: Coincident(g7,g4)
    c: Coincident(g9,g8)
    c: Horizontal(g9)
    c: Coincident(g10,g9)
    c: Vertical(g10)
    c: Coincident(g11,g10)
    c: Horizontal(g11)
    c: Coincident(g11,g8)
    c: Coincident(g13,g12)
    c: Horizontal(g13)
    c: Coincident(g14,g13)
    c: Vertical(g14)
    c: Coincident(g15,g14)
    c: Horizontal(g15)
    c: Coincident(g15,g12)
    c: Coincident(g17,g16)
    c: Horizontal(g17)
    c: Coincident(g18,g17)
    c: Vertical(g18)
    c: Coincident(g19,g18)
    c: Horizontal(g19)
    c: Coincident(g19,g16)
    c: Equal(g3,g19)
    c: Equal(g3,g15)
    c: Equal(g3,g11)
    c: Equal(g3,g7)
    c: Equal(g2,g18)
    c: Equal(g2,g14)
    c: Equal(g2,g10)
    c: Equal(g2,g6)
    c: DistanceY(g-4,g4) = 1
    c: DistanceY(g4,g8) = 1
    c: DistanceY(g8,g12) = 1
    c: DistanceY(g12,g16) = 1
    c: DistanceY(g16,g0) = 1
    c: Tangent(g0,g-5)
    c: Tangent(g16,g-5)
    c: Tangent(g12,g-5)
    c: Tangent(g8,g-5)
    c: Tangent(g4,g-5)
FEATURE [PartDesign::Chamfer] Chamfer009
  Angle = 45
  Base = -> Pad017 [Edge151,Edge154]
  BaseFeature = -> Pad017
  ChamferType = 1
  FlipDirection = false
  Refine = true
  Size = 1.5
  Size2 = 2.8
  SupportTransform = false
  Suppressed = false
  UseAllEdges = false
FEATURE [PartDesign::Pocket] Pocket009
  BaseFeature = -> Chamfer009
  Direction = (0,1,-2e-16)
  Length = 1
  Length2 = 5
  Profile = -> Sketch125
  ReferenceAxis = -> Sketch125 [N_Axis]
  Refine = true
  Suppressed = false
  Type = 0
FEATURE [PartDesign::Pad] Pad014
  BaseFeature = -> Pocket009
  Direction = (0,-1,2e-16)
  Length = 0.8
  Length2 = 10
  Profile = -> Sketch120
  ReferenceAxis = -> Sketch120 [N_Axis]
  Refine = true
  Suppressed = false
  Type = 0
FEATURE [Sketcher::SketchObject] Sketch124
  ArcFitTolerance = 1e-06
  AttachmentSupport = -> [Pad014]
  ExternalGeometry = -> [Binder001]
  FullyConstrained = true
  MakeInternals = false
  MapMode = 5
  Placement = pos=(0,-2.8,6e-16) rot=(1,0,0;1.5708rad)
  sketch-geometry (4):
    g0: LineSegment StartX=-129 StartY=39.2 StartZ=0 EndX=-131.599 EndY=31.2 EndZ=0
    g1: LineSegment StartX=-118 StartY=39.2 StartZ=0 EndX=-120.599 EndY=31.2 EndZ=0
    g2: LineSegment StartX=-129 StartY=39.2 StartZ=0 EndX=-118 EndY=39.2 EndZ=0
    g3: LineSegment StartX=-120.599 StartY=31.2 StartZ=0 EndX=-131.599 EndY=31.2 EndZ=0
  constraints (12):
    c: PointOnObject(g0,g-3)
    c: PointOnObject(g1,g-3)
    c: Parallel(g-4,g0)
    c: Parallel(g-4,g1)
    c: Coincident(g2,g0)
    c: Coincident(g2,g1)
    c: DistanceX(g2,g2) = 11
    c: DistanceY(g1,g1) = 8
    c: Coincident(g3,g1)
    c: Horizontal(g3)
    c: Coincident(g3,g0)
    c: DistanceX(g1,g-3) = 118
FEATURE [PartDesign::Pad] Pad018
  BaseFeature = -> Pad014
  Direction = (0,-1,2e-16)
  Length = 1.2
  Length2 = 10
  Profile = -> Sketch124
  ReferenceAxis = -> Sketch124 [N_Axis]
  Refine = true
  Suppressed = false
  Type = 0
FEATURE [Sketcher::SketchObject] Sketch126
  ArcFitTolerance = 1e-06
  AttachmentSupport = -> [Pad018]
  ExternalGeometry = -> [Pad018]
  FullyConstrained = true
  MakeInternals = false
  MapMode = 5
  Placement = pos=(0,-4,0) rot=(1,0,0;1.5708rad)
  sketch-geometry (8):
    g0: LineSegment StartX=-129.877 StartY=36.5 StartZ=0 EndX=-130.137 EndY=35.7 EndZ=0
    g1: LineSegment StartX=-130.69 StartY=34 StartZ=0 EndX=-130.95 EndY=33.2 EndZ=0
    g2: LineSegment StartX=-129.877 StartY=36.5 StartZ=0 EndX=-118.877 EndY=36.5 EndZ=0
    g3: LineSegment StartX=-130.137 StartY=35.7 StartZ=0 EndX=-119.137 EndY=35.7 EndZ=0
    g4: LineSegment StartX=-130.69 StartY=34 StartZ=0 EndX=-119.69 EndY=34 EndZ=0
    g5: LineSegment StartX=-130.95 StartY=33.2 StartZ=0 EndX=-119.95 EndY=33.2 EndZ=0
    g6: LineSegment StartX=-118.877 StartY=36.5 StartZ=0 EndX=-119.137 EndY=35.7 EndZ=0
    g7: LineSegment StartX=-119.69 StartY=34 StartZ=0 EndX=-119.95 EndY=33.2 EndZ=0
  constraints (20):
    c: Coincident(g2,g0)
    c: Horizontal(g2)
    c: Coincident(g3,g0)
    c: Horizontal(g3)
    c: Coincident(g4,g1)
    c: Horizontal(g4)
    c: Coincident(g5,g1)
    c: Horizontal(g5)
    c: Coincident(g6,g2)
    c: Coincident(g6,g3)
    c: Coincident(g7,g4)
    c: Coincident(g7,g5)
    c: Tangent(g0,g-4)
    c: Tangent(g6,g-5)
    c: Tangent(g1,g-4)
    c: Tangent(g7,g-5)
    c: DistanceY(g3,g2) = 0.8
    c: DistanceY(g5,g4) = 0.8
    c: DistanceY(g-6,g1) = 2
    c: DistanceY(g-6,g0) = 4.5
FEATURE [PartDesign::Chamfer] Chamfer008
  Angle = 45
  Base = -> Pad018 [Edge257]
  BaseFeature = -> Pad018
  ChamferType = 1
  FlipDirection = false
  Refine = true
  Size = 1
  Size2 = 6
  SupportTransform = false
  Suppressed = false
  UseAllEdges = false
FEATURE [PartDesign::Pocket] Pocket010
  BaseFeature = -> Chamfer008
  Direction = (0,1,-2e-16)
  Length = 1
  Length2 = 5
  Profile = -> Sketch126
  ReferenceAxis = -> Sketch126 [N_Axis]
  Refine = true
  Suppressed = false
  Type = 0
FEATURE [PartDesign::Pad] Pad015
  BaseFeature = -> Pocket010
  Direction = (0,-1,2e-16)
  Length = 2
  Length2 = 10
  Profile = -> Sketch121
  ReferenceAxis = -> Sketch121 [N_Axis]
  Refine = true
  Suppressed = false
  Type = 0
FEATURE [PartDesign::Pad] Pad016
  BaseFeature = -> Pad015
  Direction = (0,-1,2e-16)
  Length = 1.6
  Length2 = 10
  Profile = -> Sketch122
  ReferenceAxis = -> Sketch122 [N_Axis]
  Refine = true
  Suppressed = false
  Type = 0
FEATURE [Sketcher::SketchObject] Sketch129
  ArcFitTolerance = 1e-06
  AttachmentSupport = -> [Pad016]
  ExternalGeometry = -> [Binder001]
  FullyConstrained = true
  MakeInternals = false
  MapMode = 5
  Placement = pos=(0,-3.6,0) rot=(1,0,0;1.5708rad)
  sketch-geometry (12):
    g0: LineSegment [constr] StartX=-192.176 StartY=-3.18451 StartZ=0 EndX=-181.223 EndY=20.303 EndZ=0
    g1: LineSegment [constr] StartX=-202.765 StartY=20.303 StartZ=0 EndX=-181.223 EndY=20.303 EndZ=0
    g2: LineSegment StartX=-202.765 StartY=20.303 StartZ=0 EndX=-181.223 EndY=20.303 EndZ=0
    g3: LineSegment StartX=-192.176 StartY=-3.18451 StartZ=0 EndX=-196.804 EndY=-13.1107 EndZ=0
    g4: ArcOfCircle CenterX=-207.583 CenterY=4 CenterZ=0 NormalX=0 NormalY=0 NormalZ=1 AngleXU=0 Radius=17 StartAngle=5.84685 EndAngle=7.56663
    g5: ArcOfEllipse CenterX=-181.223 CenterY=8.55923 CenterZ=0 NormalX=0 NormalY=0 NormalZ=1 MajorRadius=23.4779 MinorRadius=11.7437 AngleXU=2e-16 StartAngle=4.71239 EndAngle=7.85398
    g6: LineSegment [constr] StartX=-157.745 StartY=8.55923 StartZ=0 EndX=-204.701 EndY=8.55923 EndZ=0
    g7: LineSegment [constr] StartX=-181.223 StartY=20.303 StartZ=0 EndX=-181.223 EndY=-3.18451 EndZ=0
    g8: GeomPoint [constr] X=-160.894 Y=8.55923 Z=0
    g9: GeomPoint [constr] X=-201.553 Y=8.55923 Z=0
    g10: ArcOfCircle CenterX=-181.223 CenterY=-20.3763 CenterZ=0 NormalX=0 NormalY=0 NormalZ=1 AngleXU=0 Radius=17.1918 StartAngle=1.57079 EndAngle=2.70526
    g11: GeomPoint [constr] X=-181.223 Y=-3.18451 Z=0
  constraints (23):
    c: Coincident(g0,g-5)
    c: Coincident(g1,g-6)
    c: Horizontal(g1)
    c: Coincident(g1,g0)
    c: Parallel(g0,g-4)
    c: Coincident(g2,g1)
    c: Coincident(g2,g0)
    c: Coincident(g3,g0)
    c: Equal(g4,g-5)
    c: Coincident(g4,g1)
    c: Coincident(g4,g0)
    c: InternalAlignment(g6-g9 -> g5) x4
    c: Vertical(g5,g0)
    c: Horizontal(g6)
    c: Coincident(g5,g0)
    c: DistanceX(g6,g-3) = 10.1
    c: Tangent(g10,g3) = -1.5708
    c: PointOnObject(g11,g10)
    c: Tangent(g5,g10,g11) = 1.5708
    c: Coincident(g10,g5)
    c: Coincident(g11,g7)
    c: Parallel(g3,g-4)
    c: Horizontal(g5,g0)
FEATURE [Sketcher::SketchObject] Sketch130
  ArcFitTolerance = 1e-06
  AttachmentOffset = pos=(0,0,-1.6) rot=(0,0,1;0rad)
  AttachmentSupport = -> [Pad016]
  ExternalGeometry = -> [Binder001]
  FullyConstrained = true
  MakeInternals = false
  MapMode = 5
  Placement = pos=(0,-2,-4e-16) rot=(1,0,0;1.5708rad)
  sketch-geometry (12):
    g0: LineSegment [constr] StartX=-192.176 StartY=-3.18451 StartZ=0 EndX=-181.223 EndY=20.303 EndZ=0
    g1: LineSegment [constr] StartX=-202.765 StartY=20.303 StartZ=0 EndX=-181.223 EndY=20.303 EndZ=0
    g2: LineSegment StartX=-202.765 StartY=20.303 StartZ=0 EndX=-181.223 EndY=20.303 EndZ=0
    g3: LineSegment StartX=-192.176 StartY=-3.18451 StartZ=0 EndX=-193.827 EndY=-6.72678 EndZ=0
    g4: ArcOfCircle CenterX=-207.583 CenterY=4 CenterZ=0 NormalX=0 NormalY=0 NormalZ=1 AngleXU=0 Radius=17 StartAngle=5.84685 EndAngle=7.56663
    g5: ArcOfEllipse CenterX=-181.223 CenterY=10.803 CenterZ=0 NormalX=0 NormalY=0 NormalZ=1 MajorRadius=14.4779 MinorRadius=9.5 AngleXU=0 StartAngle=4.71239 EndAngle=7.85398
    g6: LineSegment [constr] StartX=-166.745 StartY=10.803 StartZ=0 EndX=-195.701 EndY=10.803 EndZ=0
    g7: LineSegment [constr] StartX=-181.223 StartY=20.303 StartZ=0 EndX=-181.223 EndY=1.30297 EndZ=0
    g8: GeomPoint [constr] X=-170.298 Y=10.803 Z=0
    g9: GeomPoint [constr] X=-192.148 Y=10.803 Z=0
    g10: ArcOfCircle CenterX=-181.223 CenterY=-12.6042 CenterZ=0 NormalX=0 NormalY=0 NormalZ=1 AngleXU=0 Radius=13.9072 StartAngle=1.5708 EndAngle=2.70526
    g11: GeomPoint [constr] X=-181.223 Y=1.30297 Z=0
  constraints (23):
    c: Coincident(g0,g-5)
    c: Coincident(g1,g-6)
    c: Horizontal(g1)
    c: Coincident(g1,g0)
    c: Parallel(g0,g-4)
    c: Coincident(g2,g1)
    c: Coincident(g2,g0)
    c: Coincident(g3,g0)
    c: Equal(g4,g-5)
    c: Coincident(g4,g1)
    c: Coincident(g4,g0)
    c: InternalAlignment(g6-g9 -> g5) x4
    c: Vertical(g5,g0)
    c: Horizontal(g6)
    c: Coincident(g5,g0)
    c: DistanceX(g6,g-3) = 19.1
    c: Tangent(g10,g3) = -1.5708
    c: PointOnObject(g11,g10)
    c: Tangent(g5,g10,g11) = 1.5708
    c: Coincident(g10,g5)
    c: Coincident(g11,g7)
    c: Parallel(g3,g-4)
    c: DistanceY(g5,g0) = 19
FEATURE [Part::Part2DObjectPython] Clone2D001  label="Sketch130 (2D)"  # Draft 2D object (typed FeaturePython)
  Fuse = false
  Objects = -> [Sketch130]
  Placement = pos=(0,-2,-4e-16) rot=(1,0,0;1.5708rad)
  Scale = (1,1,1)
FEATURE [Sketcher::SketchObject] Sketch131
  ArcFitTolerance = 1e-06
  AttachmentOffset = pos=(0,0,-3.5) rot=(0,0,1;0rad)
  AttachmentSupport = -> [Pad016]
  ExternalGeometry = -> [Binder001]
  FullyConstrained = true
  MakeInternals = false
  MapMode = 5
  Placement = pos=(0,-0.1,-8e-16) rot=(1,0,0;1.5708rad)
  sketch-geometry (1):
    g0: GeomPoint X=-197.47 Y=8.55923 Z=0
  constraints (1):
    c: Symmetric(g-6,g-4,g0)
FEATURE [Sketcher::SketchObject] Sketch132
  ArcFitTolerance = 1e-06
  AttachmentSupport = -> [Pad016]
  ExternalGeometry = -> [Binder001]
  FullyConstrained = true
  MakeInternals = false
  MapMode = 5
  Placement = pos=(0,-3.6,0) rot=(1,0,0;1.5708rad)
  sketch-geometry (3):
    g0: LineSegment [constr] StartX=-215.42 StartY=-53.0314 StartZ=0 EndX=-167.782 EndY=-53.0314 EndZ=0
    g1: Circle CenterX=-191.282 CenterY=-53.0314 CenterZ=0 NormalX=0 NormalY=0 NormalZ=1 AngleXU=0 Radius=11.5
    g2: Circle CenterX=-191.282 CenterY=-53.0314 CenterZ=0 NormalX=0 NormalY=0 NormalZ=1 AngleXU=0 Radius=10.7
  constraints (8):
    c: Coincident(g0,g-3)
    c: PointOnObject(g0,g-4)
    c: Horizontal(g0)
    c: Diameter(g1) = 23
    c: PointOnObject(g1,g0)
    c: DistanceX(g1,g0) = 23.5
    c: Diameter(g2) = 21.4
    c: Coincident(g2,g1)
FEATURE [Part::Part2DObjectPython] ShapeString  # Draft 2D object (typed FeaturePython)
  FontFile = <path>
  Fuse = false
  Justification = 6
  JustificationReference = 0
  KeepLeftMargin = false
  MakeFace = true
  ObliqueAngle = 0
  Placement = pos=(-199,-3.6,-57.5) rot=(1,0,0;1.5708rad)
  ScaleToSize = true
  Size = 10
  String = AS
  Tracking = 0
FEATURE [Sketcher::SketchObject] Sketch133
  ArcFitTolerance = 1e-06
  AttachmentSupport = -> [Binder]
  ExternalGeometry = -> [Binder]
  FullyConstrained = true
  MakeInternals = false
  MapMode = 5
  Placement = pos=(0,9e-16,0) rot=(0,0.707107,0.707107;3.14159rad)
  sketch-geometry (30):
    g0: LineSegment StartX=0 StartY=39.2 StartZ=0 EndX=0 EndY=3.2 EndZ=0
    g1: LineSegment StartX=0 StartY=3.2 StartZ=0 EndX=82.8 EndY=3.2 EndZ=0
    g2: LineSegment StartX=82.8 StartY=3.2 StartZ=0 EndX=82.8 EndY=6.2 EndZ=0
    g3: LineSegment StartX=82.8 StartY=6.2 StartZ=0 EndX=91.752 EndY=6.2 EndZ=0
    g4: LineSegment StartX=0 StartY=39.2 StartZ=0 EndX=195.887 EndY=39.2 EndZ=0
    g5: LineSegment StartX=195.887 StartY=39.2 StartZ=0 EndX=202.765 EndY=20.303 EndZ=0
    g6: LineSegment StartX=192.333 StartY=24.9893 StartZ=0 EndX=196.467 EndY=26.4942 EndZ=0
    g7: LineSegment StartX=196.467 StartY=26.4942 StartZ=0 EndX=194.073 EndY=33.0721 EndZ=0
    g8: LineSegment StartX=194.073 StartY=33.0721 StartZ=0 EndX=189.939 EndY=31.5672 EndZ=0
    g9: LineSegment StartX=189.939 StartY=31.5672 StartZ=0 EndX=192.333 EndY=24.9893 EndZ=0
    g10: ArcOfCircle CenterX=107.6 CenterY=4 CenterZ=0 NormalX=0 NormalY=0 NormalZ=1 AngleXU=0 Radius=16 StartAngle=1.5708 EndAngle=3.00366
    g11: LineSegment StartX=107.6 StartY=20 StartZ=0 EndX=132.428 EndY=20 EndZ=0
    g12: ArcOfCircle [constr] CenterX=132.428 CenterY=4 CenterZ=0 NormalX=0 NormalY=0 NormalZ=1 AngleXU=0 Radius=16 StartAngle=0.314159 EndAngle=1.5708
    g13: LineSegment StartX=147.645 StartY=8.94427 StartZ=0 EndX=176.685 EndY=-80.4316 EndZ=0
    g14: LineSegment StartX=176.685 StartY=-80.4316 StartZ=0 EndX=215.932 EndY=-80.4316 EndZ=0
    g15: ArcOfCircle CenterX=207.583 CenterY=4 CenterZ=0 NormalX=0 NormalY=0 NormalZ=1 AngleXU=0 Radius=17 StartAngle=1.85815 EndAngle=3.57792
    g16: ArcOfCircle CenterX=184.801 CenterY=-67.3089 CenterZ=0 NormalX=0 NormalY=0 NormalZ=1 AngleXU=0 Radius=33.7833 StartAngle=5.88425 EndAngle=6.71952
    g17: LineSegment StartX=192.176 StartY=-3.18451 StartZ=0 EndX=215.42 EndY=-53.0314 EndZ=0
    g18: Circle CenterX=5.6 CenterY=34.8 CenterZ=0 NormalX=0 NormalY=0 NormalZ=1 AngleXU=0 Radius=1.8
    g19: Circle CenterX=5.6 CenterY=7.6 CenterZ=0 NormalX=0 NormalY=0 NormalZ=1 AngleXU=0 Radius=1.8
    g20: Circle CenterX=78.51 CenterY=34.8 CenterZ=0 NormalX=0 NormalY=0 NormalZ=1 AngleXU=0 Radius=1.8
    g21: Circle CenterX=78.51 CenterY=7.6 CenterZ=0 NormalX=0 NormalY=0 NormalZ=1 AngleXU=0 Radius=1.8
    g22: Circle CenterX=184.08 CenterY=34.8 CenterZ=0 NormalX=0 NormalY=0 NormalZ=1 AngleXU=0 Radius=1.8
    g23: Circle CenterX=179.305 CenterY=-76.8316 CenterZ=0 NormalX=0 NormalY=0 NormalZ=1 AngleXU=0 Radius=1.8
    g24: Circle CenterX=213.443 CenterY=-76.8316 CenterZ=0 NormalX=0 NormalY=0 NormalZ=1 AngleXU=0 Radius=1.8
    g25: Circle CenterX=19 CenterY=21.2 CenterZ=0 NormalX=0 NormalY=0 NormalZ=1 AngleXU=0 Radius=6.3
    g26: Circle CenterX=42 CenterY=21.2 CenterZ=0 NormalX=0 NormalY=0 NormalZ=1 AngleXU=0 Radius=6.3
    g27: Circle CenterX=65 CenterY=21.2 CenterZ=0 NormalX=0 NormalY=0 NormalZ=1 AngleXU=0 Radius=6.3
    g28: LineSegment StartX=132.428 StartY=20 StartZ=0 EndX=144.053 EndY=20 EndZ=0
    g29: LineSegment StartX=147.645 StartY=8.94427 StartZ=0 EndX=144.053 EndY=20 EndZ=0
  constraints (65):
    c: Coincident(g0,g-4)
    c: Coincident(g0,g-5)
    c: Coincident(g1,g0)
    c: Coincident(g1,g-6)
    c: Coincident(g2,g1)
    c: Coincident(g2,g-7)
    c: Coincident(g3,g2)
    c: Coincident(g3,g-8)
    c: Coincident(g4,g0)
    c: Coincident(g4,g-16)
    c: Coincident(g5,g4)
    c: Coincident(g5,g-16)
    c: Coincident(g6,g-20)
    c: Coincident(g6,g-21)
    c: Coincident(g7,g6)
    c: Coincident(g7,g-23)
    c: Coincident(g8,g7)
    c: Coincident(g8,g-22)
    c: Coincident(g9,g8)
    c: Coincident(g9,g6)
    c: Equal(g10,g-8)
    c: Coincident(g10,g3)
    c: Coincident(g10,g-9)
    c: Coincident(g11,g10)
    c: Coincident(g11,g-10)
    c: Equal(g12,g-10)
    c: Coincident(g12,g11)
    c: Coincident(g12,g-11)
    c: Coincident(g13,g12)
    c: Coincident(g13,g-12)
    c: Coincident(g14,g13)
    c: Coincident(g14,g-13)
    c: Equal(g15,g-15)
    c: Coincident(g15,g5)
    c: Coincident(g15,g-15)
    c: Equal(g16,g-13)
    c: Coincident(g16,g14)
    c: Coincident(g16,g-14)
    c: Coincident(g17,g15)
    c: Coincident(g17,g16)
    c: Equal(g18,g-28)
    c: Equal(g19,g-29)
    c: Equal(g20,g-26)
    c: Equal(g21,g-27)
    c: Equal(g22,g-17)
    c: Equal(g24,g-25)
    c: Equal(g23,g-24)
    c: Coincident(g23,g-24)
    c: Coincident(g24,g-25)
    c: Coincident(g22,g-17)
    c: Coincident(g20,g-26)
    c: Coincident(g21,g-27)
    c: Coincident(g18,g-28)
    c: Coincident(g19,g-29)
    c: Equal(g25,g-30)
    c: Equal(g26,g-31)
    c: Equal(g27,g-32)
    c: Coincident(g25,g-30)
    c: Coincident(g26,g-31)
    c: Coincident(g27,g-32)
    c: Parallel(g28,g11)
    c: Parallel(g29,g13)
    c: Coincident(g28,g11)
    c: Coincident(g29,g12)
    c: Coincident(g29,g28)
FEATURE [PartDesign::Pad] Pad019
  Direction = (0,1,-2e-16)
  Length = 2
  Length2 = 10
  Profile = -> Sketch133
  ReferenceAxis = -> Sketch133 [N_Axis]
  Refine = true
  Suppressed = false
  Type = 0
FEATURE [Sketcher::SketchObject] Sketch091  label="Sketch091 - forma anteriore"
  ArcFitTolerance = 1e-06
  AttachmentSupport = -> [Pad019]
  ExternalGeometry = -> [Binder]
  FullyConstrained = true
  MakeInternals = false
  MapMode = 5
  Placement = pos=(0,2,0) rot=(0,0.707107,0.707107;3.14159rad)
  sketch-geometry (12):
    g0: Circle CenterX=5.6 CenterY=34.8 CenterZ=0 NormalX=0 NormalY=0 NormalZ=1 AngleXU=0 Radius=1.8
    g1: Circle CenterX=5.6 CenterY=7.6 CenterZ=0 NormalX=0 NormalY=0 NormalZ=1 AngleXU=0 Radius=1.8
    g2: Circle CenterX=78.51 CenterY=34.8 CenterZ=0 NormalX=0 NormalY=0 NormalZ=1 AngleXU=0 Radius=1.8
    g3: Circle CenterX=78.51 CenterY=7.6 CenterZ=0 NormalX=0 NormalY=0 NormalZ=1 AngleXU=0 Radius=1.8
    g4: LineSegment StartX=0 StartY=39.2 StartZ=0 EndX=0 EndY=3.2 EndZ=0
    g5: LineSegment StartX=0 StartY=3.2 StartZ=0 EndX=82.8 EndY=3.2 EndZ=0
    g6: LineSegment StartX=82.8 StartY=3.2 StartZ=0 EndX=82.8 EndY=39.2 EndZ=0
    g7: LineSegment StartX=82.8 StartY=39.2 StartZ=0 EndX=0 EndY=39.2 EndZ=0
    g8: ArcOfCircle CenterX=19 CenterY=21.2 CenterZ=0 NormalX=0 NormalY=0 NormalZ=1 AngleXU=0 Radius=10 StartAngle=1.5708 EndAngle=4.71239
    g9: ArcOfCircle CenterX=65 CenterY=21.2 CenterZ=0 NormalX=0 NormalY=0 NormalZ=1 AngleXU=0 Radius=10 StartAngle=4.71239 EndAngle=7.85398
    g10: LineSegment StartX=19 StartY=31.2 StartZ=0 EndX=65 EndY=31.2 EndZ=0
    g11: LineSegment StartX=19 StartY=11.2 StartZ=0 EndX=65 EndY=11.2 EndZ=0
  constraints (25):
    c: Equal(g2,g-7)
    c: Equal(g3,g-8)
    c: Equal(g1,g-13)
    c: Equal(g0,g-12)
    c: Coincident(g0,g-12)
    c: Coincident(g1,g-13)
    c: Coincident(g3,g-8)
    c: Coincident(g2,g-7)
    c: Coincident(g4,g-4)
    c: Coincident(g4,g-5)
    c: Coincident(g5,g4)
    c: Coincident(g5,g-6)
    c: Coincident(g6,g5)
    c: PointOnObject(g6,g-3)
    c: Vertical(g6)
    c: Coincident(g7,g6)
    c: Coincident(g7,g4)
    c: Tangent(g8,g10) = 1.5708
    c: Tangent(g8,g11) = -1.5708
    c: Tangent(g9,g10) = 1.5708
    c: Tangent(g9,g11) = -1.5708
    c: Equal(g8,g9)
    c: Radius(g8) = 10
    c: Coincident(g8,g-11)
    c: Coincident(g9,g-9)
FEATURE [Sketcher::SketchObject] Sketch093  label="Sketch093 - scavi interni pulsanti"
  ArcFitTolerance = 1e-06
  AttachmentSupport = -> [Pad019]
  ExternalGeometry = -> [Binder]
  FullyConstrained = true
  MakeInternals = false
  MapMode = 5
  Placement = pos=(0,1.8e-15,0) rot=(1,0,0;1.5708rad)
  sketch-geometry (3):
    g0: Circle CenterX=-65 CenterY=21.2 CenterZ=0 NormalX=0 NormalY=0 NormalZ=1 AngleXU=0 Radius=7.3
    g1: Circle CenterX=-42 CenterY=21.2 CenterZ=0 NormalX=0 NormalY=0 NormalZ=1 AngleXU=0 Radius=7.3
    g2: Circle CenterX=-19 CenterY=21.2 CenterZ=0 NormalX=0 NormalY=0 NormalZ=1 AngleXU=0 Radius=7.3
  constraints (6):
    c: Coincident(g0,g-3)
    c: Coincident(g1,g-4)
    c: Coincident(g2,g-5)
    c: Diameter(g0) = 14.6
    c: Diameter(g1) = 14.6
    c: Diameter(g2) = 14.6
FEATURE [Sketcher::SketchObject] Sketch094  label="Sketch094 - forma centrale"
  ArcFitTolerance = 1e-06
  AttachmentSupport = -> [Pad019]
  ExternalGeometry = -> [Binder]
  FullyConstrained = true
  MakeInternals = false
  MapMode = 5
  Placement = pos=(0,2,0) rot=(0,0.707107,0.707107;3.14159rad)
  sketch-geometry (4):
    g0: LineSegment StartX=137.815 StartY=39.2 StartZ=0 EndX=142.655 EndY=24.303 EndZ=0
    g1: LineSegment StartX=110.815 StartY=24.303 StartZ=0 EndX=142.655 EndY=24.303 EndZ=0
    g2: LineSegment StartX=137.815 StartY=39.2 StartZ=0 EndX=110.815 EndY=39.2 EndZ=0
    g3: ArcOfCircle CenterX=92.2534 CenterY=31.7515 CenterZ=0 NormalX=0 NormalY=0 NormalZ=1 AngleXU=0 Radius=20 StartAngle=5.90156 EndAngle=6.66481
  constraints (12):
    c: PointOnObject(g0,g-3)
    c: Tangent(g0,g-5)
    c: Horizontal(g1)
    c: Coincident(g1,g0)
    c: Coincident(g2,g0)
    c: PointOnObject(g2,g-3)
    c: DistanceX(g2,g2) = 27
    c: Vertical(g1,g2)
    c: Coincident(g3,g2)
    c: Radius(g3) = 20
    c: Coincident(g3,g1)
    c: DistanceY(g-6,g0) = 4
FEATURE [Sketcher::SketchObject] Sketch095  label="Sketch095 - forma posteriore"
  ArcFitTolerance = 1e-06
  AttachmentSupport = -> [Pad019]
  ExternalGeometry = -> [Binder]
  FullyConstrained = true
  MakeInternals = false
  MapMode = 5
  Placement = pos=(0,2,0) rot=(0,0.707107,0.707107;3.14159rad)
  sketch-geometry (15):
    g0: LineSegment StartX=137.815 StartY=39.2 StartZ=0 EndX=143.955 EndY=20.303 EndZ=0
    g1: LineSegment StartX=143.955 StartY=20.303 StartZ=0 EndX=190.141 EndY=20.303 EndZ=0
    g2: ArcOfCircle CenterX=184.08 CenterY=34.8 CenterZ=0 NormalX=0 NormalY=0 NormalZ=1 AngleXU=0 Radius=3.5 StartAngle=3.49066 EndAngle=4.71239
    g3: LineSegment StartX=180.791 StartY=33.6029 StartZ=0 EndX=178.754 EndY=39.2 EndZ=0
    g4: LineSegment StartX=184.08 StartY=31.3 StartZ=0 EndX=186.139 EndY=31.3 EndZ=0
    g5: LineSegment StartX=190.141 StartY=20.303 StartZ=0 EndX=186.139 EndY=31.3 EndZ=0
    g6: LineSegment StartX=137.815 StartY=39.2 StartZ=0 EndX=156.815 EndY=39.2 EndZ=0
    g7: LineSegment StartX=178.754 StartY=39.2 StartZ=0 EndX=168.815 EndY=39.2 EndZ=0
    g8: LineSegment StartX=156.815 StartY=31.2 StartZ=0 EndX=168.815 EndY=31.2 EndZ=0
    g9: ArcOfCircle CenterX=176.411 CenterY=35.2 CenterZ=0 NormalX=0 NormalY=0 NormalZ=1 AngleXU=0 Radius=20 StartAngle=2.94023 EndAngle=3.34295
    g10: ArcOfCircle CenterX=188.411 CenterY=35.2 CenterZ=0 NormalX=0 NormalY=0 NormalZ=1 AngleXU=0 Radius=20 StartAngle=2.94023 EndAngle=3.34295
    g11: LineSegment StartX=157.815 StartY=39.2 StartZ=0 EndX=167.815 EndY=39.2 EndZ=0
    g12: LineSegment StartX=157.436 StartY=36.2 StartZ=0 EndX=167.436 EndY=36.2 EndZ=0
    g13: ArcOfCircle CenterX=177.411 CenterY=35.2 CenterZ=0 NormalX=0 NormalY=0 NormalZ=1 AngleXU=0 Radius=20 StartAngle=2.94023 EndAngle=3.09157
    g14: ArcOfCircle CenterX=187.411 CenterY=35.2 CenterZ=0 NormalX=0 NormalY=0 NormalZ=1 AngleXU=0 Radius=20 StartAngle=2.94023 EndAngle=3.09157
  constraints (46):
    c: PointOnObject(g0,g-3)
    c: Tangent(g0,g-6)
    c: Coincident(g1,g0)
    c: Horizontal(g1)
    c: Radius(g2) = 3.5
    c: Coincident(g2,g-5)
    c: PointOnObject(g3,g-3)
    c: Parallel(g3,g-4)
    c: Tangent(g3,g2) = 1.5708
    c: Horizontal(g4)
    c: Tangent(g4,g2) = -1.5708
    c: Coincident(g5,g1)
    c: Parallel(g5,g-4)
    c: Coincident(g5,g4)
    c: DistanceX(g4,g-8) = 3.8
    c: Coincident(g6,g0)
    c: PointOnObject(g6,g-3)
    c: Coincident(g7,g3)
    c: PointOnObject(g7,g-3)
    c: Horizontal(g8)
    c: DistanceX(g6,g7) = 12
    c: Vertical(g8,g6)
    c: Vertical(g7,g8)
    c: DistanceY(g8,g6) = 8
    c: Coincident(g9,g8)
    c: Coincident(g9,g6)
    c: Coincident(g10,g7)
    c: Coincident(g10,g8)
    c: Radius(g9) = 20
    c: Radius(g10) = 20
    c: PointOnObject(g11,g-3)
    c: PointOnObject(g11,g-3)
    c: DistanceX(g11,g11) = 10
    c: DistanceX(g6,g11) = 1
    c: Horizontal(g12)
    c: Equal(g12,g11)
    c: DistanceY(g12,g11) = 3
    c: Coincident(g13,g11)
    c: Coincident(g13,g12)
    c: Radius(g13) = 20
    c: Coincident(g14,g11)
    c: Coincident(g14,g12)
    c: Radius(g14) = 20
    c: DistanceX(g0,g6) = 19
    c: Horizontal(g9,g13)
    c: Horizontal(g0,g-4)
FEATURE [Sketcher::SketchObject] Sketch096  label="Sketch096 - forma impugnatura"
  ArcFitTolerance = 1e-06
  AttachmentSupport = -> [Pad019]
  ExternalGeometry = -> [Binder]
  FullyConstrained = true
  MakeInternals = false
  MapMode = 5
  Placement = pos=(0,2,0) rot=(0,0.707107,0.707107;3.14159rad)
  sketch-geometry (8):
    g0: LineSegment StartX=176.685 StartY=-80.4316 StartZ=0 EndX=143.955 EndY=20.303 EndZ=0
    g1: LineSegment StartX=176.685 StartY=-80.4316 StartZ=0 EndX=215.932 EndY=-80.4316 EndZ=0
    g2: Circle CenterX=179.305 CenterY=-76.8316 CenterZ=0 NormalX=0 NormalY=0 NormalZ=1 AngleXU=0 Radius=3
    g3: Circle CenterX=213.443 CenterY=-76.8316 CenterZ=0 NormalX=0 NormalY=0 NormalZ=1 AngleXU=0 Radius=3
    g4: LineSegment StartX=143.955 StartY=20.303 StartZ=0 EndX=202.765 EndY=20.303 EndZ=0
    g5: LineSegment StartX=215.42 StartY=-53.0314 StartZ=0 EndX=192.176 EndY=-3.18451 EndZ=0
    g6: ArcOfCircle CenterX=184.801 CenterY=-67.3089 CenterZ=0 NormalX=0 NormalY=0 NormalZ=1 AngleXU=0 Radius=33.7833 StartAngle=5.88425 EndAngle=6.71952
    g7: ArcOfCircle CenterX=207.583 CenterY=4 CenterZ=0 NormalX=0 NormalY=0 NormalZ=1 AngleXU=0 Radius=17 StartAngle=1.85815 EndAngle=3.57792
  constraints (19):
    c: Coincident(g0,g-4)
    c: PointOnObject(g0,g-3)
    c: Horizontal(g0,g-7)
    c: Coincident(g1,g0)
    c: Coincident(g1,g-5)
    c: Diameter(g2) = 6
    c: Diameter(g3) = 6
    c: Coincident(g2,g-9)
    c: Coincident(g3,g-10)
    c: Coincident(g4,g0)
    c: Coincident(g5,g-6)
    c: Coincident(g6,g1)
    c: Coincident(g6,g5)
    c: Equal(g-5,g6)
    c: Coincident(g5,g-7)
    c: Coincident(g4,g-7)
    c: Tangent(g7,g-7)
    c: Coincident(g7,g4)
    c: Coincident(g7,g5)
FEATURE [Sketcher::SketchObject] Sketch097
  ArcFitTolerance = 1e-06
  AttachmentSupport = -> [Pad019]
  ExternalGeometry = -> [Binder]
  FullyConstrained = true
  MakeInternals = false
  MapMode = 5
  Placement = pos=(0,2,0) rot=(0,0.707107,0.707107;3.14159rad)
  sketch-geometry (4):
    g0: LineSegment StartX=90 StartY=36.8 StartZ=0 EndX=108 EndY=36.8 EndZ=0
    g1: LineSegment StartX=108 StartY=36.8 StartZ=0 EndX=108 EndY=26.8 EndZ=0
    g2: LineSegment StartX=108 StartY=26.8 StartZ=0 EndX=90 EndY=26.8 EndZ=0
    g3: ArcOfCircle CenterX=94 CenterY=31.8 CenterZ=0 NormalX=0 NormalY=0 NormalZ=1 AngleXU=0 Radius=6.40312 StartAngle=2.24554 EndAngle=4.03765
  constraints (13):
    c: Horizontal(g0)
    c: Coincident(g1,g0)
    c: Vertical(g1)
    c: DistanceX(g0,g0) = 18
    c: DistanceY(g1,g1) = 10
    c: Coincident(g2,g1)
    c: Horizontal(g2)
    c: Equal(g2,g0)
    c: DistanceY(g0,g-3) = 2.4
    c: Coincident(g3,g0)
    c: Coincident(g3,g2)
    c: DistanceX(g2,g3) = 4
    c: DistanceX(g-3,g0) = 90
FEATURE [PartDesign::Chamfer] Chamfer015
  Angle = 45
  Base = -> Pad019 [Edge19,Edge22,Edge79]
  BaseFeature = -> Pad019
  ChamferType = 0
  FlipDirection = false
  Refine = true
  Size = 1.9
  Size2 = 1
  SupportTransform = false
  Suppressed = false
  UseAllEdges = false
FEATURE [PartDesign::Pocket] Pocket002
  BaseFeature = -> Chamfer015
  Direction = (0,1,-2e-16)
  Length = 1.2
  Length2 = 5
  Profile = -> Sketch093
  ReferenceAxis = -> Sketch093 [N_Axis]
  Refine = true
  Suppressed = false
  Type = 0
FEATURE [PartDesign::Pad] Pad005
  BaseFeature = -> Pocket002
  Direction = (0,1,-2e-16)
  Length = 1.6
  Length2 = 10
  Profile = -> Sketch091
  ReferenceAxis = -> Sketch091 [N_Axis]
  Refine = true
  Suppressed = false
  Type = 0
FEATURE [Sketcher::SketchObject] Sketch092  label="Sketch092 - scavi per viti anteriori"
  ArcFitTolerance = 1e-06
  AttachmentSupport = -> [Pad005]
  ExternalGeometry = -> [Binder]
  FullyConstrained = true
  MakeInternals = false
  MapMode = 5
  Placement = pos=(0,3.6,0) rot=(0,0.707107,0.707107;3.14159rad)
  sketch-geometry (20):
    g0: ArcOfCircle CenterX=5.6 CenterY=7.6 CenterZ=0 NormalX=0 NormalY=0 NormalZ=1 AngleXU=0 Radius=3.5 StartAngle=0 EndAngle=1.5708
    g1: ArcOfCircle CenterX=5.6 CenterY=34.8 CenterZ=0 NormalX=0 NormalY=0 NormalZ=1 AngleXU=0 Radius=3.5 StartAngle=4.71239 EndAngle=6.28319
    g2: ArcOfCircle CenterX=78.51 CenterY=34.8 CenterZ=0 NormalX=0 NormalY=0 NormalZ=1 AngleXU=0 Radius=3.5 StartAngle=3.14159 EndAngle=4.71239
    g3: ArcOfCircle CenterX=78.51 CenterY=7.6 CenterZ=0 NormalX=0 NormalY=0 NormalZ=1 AngleXU=0 Radius=3.5 StartAngle=1.5708 EndAngle=3.14159
    g4: LineSegment StartX=0 StartY=3.2 StartZ=0 EndX=0 EndY=11.1 EndZ=0
    g5: LineSegment StartX=0 StartY=11.1 StartZ=0 EndX=5.6 EndY=11.1 EndZ=0
    g6: LineSegment StartX=0 StartY=3.2 StartZ=0 EndX=9.1 EndY=3.2 EndZ=0
    g7: LineSegment StartX=9.1 StartY=3.2 StartZ=0 EndX=9.1 EndY=7.6 EndZ=0
    g8: LineSegment StartX=0 StartY=39.2 StartZ=0 EndX=0 EndY=31.3 EndZ=0
    g9: LineSegment StartX=0 StartY=31.3 StartZ=0 EndX=5.6 EndY=31.3 EndZ=0
    g10: LineSegment StartX=0 StartY=39.2 StartZ=0 EndX=9.1 EndY=39.2 EndZ=0
    g11: LineSegment StartX=9.1 StartY=39.2 StartZ=0 EndX=9.1 EndY=34.8 EndZ=0
    g12: LineSegment StartX=82.8 StartY=39.2 StartZ=0 EndX=75.01 EndY=39.2 EndZ=0
    g13: LineSegment StartX=82.8 StartY=39.2 StartZ=0 EndX=82.8 EndY=31.3 EndZ=0
    g14: LineSegment StartX=82.8 StartY=31.3 StartZ=0 EndX=78.51 EndY=31.3 EndZ=0
    g15: LineSegment StartX=82.8 StartY=3.2 StartZ=0 EndX=75.01 EndY=3.2 EndZ=0
    g16: LineSegment StartX=75.01 StartY=3.2 StartZ=0 EndX=75.01 EndY=7.6 EndZ=0
    g17: LineSegment StartX=82.8 StartY=3.2 StartZ=0 EndX=82.8 EndY=11.1 EndZ=0
    g18: LineSegment StartX=82.8 StartY=11.1 StartZ=0 EndX=78.51 EndY=11.1 EndZ=0
    g19: LineSegment StartX=75.01 StartY=39.2 StartZ=0 EndX=75.01 EndY=34.8 EndZ=0
  constraints (48):
    c: Radius(g0) = 3.5
    c: Coincident(g0,g-10)
    c: Radius(g1) = 3.5
    c: Coincident(g1,g-9)
    c: Radius(g2) = 3.5
    c: Coincident(g2,g-8)
    c: Radius(g3) = 3.5
    c: Coincident(g3,g-7)
    c: Coincident(g4,g-5)
    c: PointOnObject(g4,g-4)
    c: Coincident(g5,g4)
    c: Horizontal(g5)
    c: Coincident(g6,g4)
    c: PointOnObject(g6,g-5)
    c: Coincident(g7,g6)
    c: Vertical(g7)
    c: Coincident(g8,g-4)
    c: PointOnObject(g8,g-4)
    c: Coincident(g9,g8)
    c: Horizontal(g9)
    c: Coincident(g10,g8)
    c: PointOnObject(g10,g-3)
    c: Coincident(g11,g10)
    c: Vertical(g11)
    c: PointOnObject(g12,g-3)
    c: PointOnObject(g12,g-3)
    c: Coincident(g13,g12)
    c: Vertical(g13)
    c: Coincident(g14,g13)
    c: Horizontal(g14)
    c: Coincident(g15,g-6)
    c: PointOnObject(g15,g-5)
    c: Coincident(g16,g15)
    c: Vertical(g16)
    c: Coincident(g17,g15)
    c: Coincident(g18,g17)
    c: Horizontal(g18)
    c: Tangent(g3,g18) = -1.5708
    c: Tangent(g16,g3) = 1.5708
    c: Coincident(g19,g12)
    c: Vertical(g19)
    c: Tangent(g2,g19) = -1.5708
    c: Tangent(g2,g14) = 1.5708
    c: Tangent(g0,g7) = -1.5708
    c: Tangent(g0,g5) = 1.5708
    c: Tangent(g9,g1) = -1.5708
    c: Tangent(g1,g11) = 1.5708
    c: Tangent(g17,g13)
FEATURE [PartDesign::Pocket] Pocket001
  BaseFeature = -> Pad005
  Direction = (0,-1,2e-16)
  Length = 1.6
  Length2 = 5
  Profile = -> Sketch092
  ReferenceAxis = -> Sketch092 [N_Axis]
  Refine = true
  Suppressed = false
  Type = 0
FEATURE [PartDesign::Pad] Pad006
  BaseFeature = -> Pocket001
  Direction = (0,1,-2e-16)
  Length = 0.8
  Length2 = 10
  Profile = -> Sketch094
  ReferenceAxis = -> Sketch094 [N_Axis]
  Refine = true
  Suppressed = false
  Type = 0
FEATURE [PartDesign::Pad] Pad007
  BaseFeature = -> Pad006
  Direction = (0,1,-2e-16)
  Length = 2
  Length2 = 10
  Profile = -> Sketch095
  ReferenceAxis = -> Sketch095 [N_Axis]
  Refine = true
  Suppressed = false
  Type = 0
FEATURE [PartDesign::Pad] Pad008  label="Pad008 - forma impugnatura"
  BaseFeature = -> Pad007
  Direction = (0,1,-2e-16)
  Length = 1.6
  Length2 = 10
  Profile = -> Sketch096
  ReferenceAxis = -> Sketch096 [N_Axis]
  Refine = true
  Suppressed = false
  Type = 0
FEATURE [PartDesign::Pad] Pad009
  BaseFeature = -> Pad008
  Direction = (0,1,-2e-16)
  Length = 1.6
  Length2 = 10
  Profile = -> Sketch097
  ReferenceAxis = -> Sketch097 [N_Axis]
  Refine = true
  Suppressed = false
  Type = 0
FEATURE [Sketcher::SketchObject] Sketch098
  ArcFitTolerance = 1e-06
  AttachmentSupport = -> [Pad006]
  ExternalGeometry = -> [Binder]
  FullyConstrained = true
  MakeInternals = false
  MapMode = 5
  Placement = pos=(0,2.8,-7e-16) rot=(0,0.707107,0.707107;3.14159rad)
  sketch-geometry (4):
    g0: LineSegment StartX=118 StartY=39.2 StartZ=0 EndX=129 EndY=39.2 EndZ=0
    g1: LineSegment StartX=120.599 StartY=31.2 StartZ=0 EndX=131.599 EndY=31.2 EndZ=0
    g2: LineSegment StartX=129 StartY=39.2 StartZ=0 EndX=131.599 EndY=31.2 EndZ=0
    g3: LineSegment StartX=118 StartY=39.2 StartZ=0 EndX=120.599 EndY=31.2 EndZ=0
  constraints (12):
    c: PointOnObject(g0,g-3)
    c: PointOnObject(g0,g-3)
    c: DistanceX(g0,g0) = 11
    c: Horizontal(g1)
    c: Equal(g1,g0)
    c: Coincident(g2,g0)
    c: Coincident(g3,g0)
    c: Parallel(g-4,g2)
    c: Coincident(g1,g2)
    c: Coincident(g1,g3)
    c: DistanceY(g1,g0) = 8
    c: DistanceX(g-3,g0) = 118
FEATURE [Sketcher::SketchObject] Sketch099
  ArcFitTolerance = 1e-06
  AttachmentSupport = -> [Pad008]
  ExternalGeometry = -> [Binder]
  FullyConstrained = true
  MakeInternals = false
  MapMode = 5
  Placement = pos=(0,3.6,0) rot=(0,0.707107,0.707107;3.14159rad)
  sketch-geometry (13):
    g0: LineSegment StartX=192.176 StartY=-3.18451 StartZ=0 EndX=196.804 EndY=-13.1108 EndZ=0
    g1: LineSegment [constr] StartX=202.765 StartY=20.303 StartZ=0 EndX=181.223 EndY=20.303 EndZ=0
    g2: LineSegment [constr] StartX=181.223 StartY=20.303 StartZ=0 EndX=181.223 EndY=-3.18451 EndZ=0
    g3: ArcOfCircle CenterX=181.223 CenterY=-20.3764 CenterZ=0 NormalX=0 NormalY=0 NormalZ=1 AngleXU=0 Radius=17.1918 StartAngle=0.436332 EndAngle=1.57079
    g4: ArcOfEllipse CenterX=181.223 CenterY=8.55923 CenterZ=0 NormalX=0 NormalY=0 NormalZ=1 MajorRadius=23.4779 MinorRadius=11.7437 AngleXU=0 StartAngle=1.5708 EndAngle=4.71239
    g5: LineSegment [constr] StartX=204.701 StartY=8.55923 StartZ=0 EndX=157.745 EndY=8.55923 EndZ=0
    g6: LineSegment [constr] StartX=181.223 StartY=20.303 StartZ=0 EndX=181.223 EndY=-3.18451 EndZ=0
    g7: GeomPoint [constr] X=201.553 Y=8.55923 Z=0
    g8: GeomPoint [constr] X=160.894 Y=8.55923 Z=0
    g9: GeomPoint [constr] X=181.223 Y=-3.18451 Z=0
    g10: LineSegment StartX=181.223 StartY=20.303 StartZ=0 EndX=202.765 EndY=20.303 EndZ=0
    g11: ArcOfCircle CenterX=207.583 CenterY=4 CenterZ=0 NormalX=0 NormalY=0 NormalZ=1 AngleXU=0 Radius=17 StartAngle=1.85815 EndAngle=3.57792
    g12: LineSegment [constr] StartX=172.411 StartY=39.2 StartZ=0 EndX=192.176 EndY=-3.18451 EndZ=0
  constraints (27):
    c: Coincident(g1,g-7)
    c: Horizontal(g1)
    c: Coincident(g2,g1)
    c: Vertical(g2)
    c: Horizontal(g2,g0)
    c: Coincident(g3,g0)
    c: Coincident(g3,g2)
    c: InternalAlignment(g5-g8 -> g4) x4
    c: Horizontal(g5)
    c: PointOnObject(g4,g2)
    c: Coincident(g4,g1)
    c: DistanceX(g-3,g5) = 10.1
    c: Coincident(g4,g2)
    c: Tangent(g3,g-5)
    c: PointOnObject(g9,g4)
    c: PointOnObject(g9,g3)
    c: Tangent(g4,g3,g9) = 1.5708
    c: Coincident(g10,g1)
    c: Coincident(g10,g1)
    c: Equal(g11,g-4)
    c: Coincident(g11,g1)
    c: Coincident(g11,g0)
    c: PointOnObject(g12,g-6)
    c: PointOnObject(g1,g12)
    c: Tangent(g12,g-5) = -1.5708
    c: Tangent(g0,g-5) = -1.5708
    c: Horizontal(g9,g12)
FEATURE [Sketcher::SketchObject] Sketch106  label="Sketch106 - smusso impuniatura interno"
  ArcFitTolerance = 1e-06
  AttachmentSupport = -> [Pad008]
  ExternalGeometry = -> [Pad008]
  FullyConstrained = true
  MakeInternals = false
  MapMode = 5
  Placement = pos=(0,-1.586e-13,-80.4316) rot=(1,0,0;3.14159rad)
  sketch-geometry (9):
    g0: LineSegment StartX=-176.685 StartY=-3.6 StartZ=0 EndX=-176.685 EndY=6.928e-13 EndZ=0
    g1: LineSegment [constr] StartX=-176.685 StartY=-7.37e-14 StartZ=0 EndX=-176.685 EndY=6.928e-13 EndZ=0
    g2: LineSegment [constr] StartX=-186.685 StartY=-3.6 StartZ=0 EndX=-186.685 EndY=6.928e-13 EndZ=0
    g3: ArcOfEllipse CenterX=-186.685 CenterY=6.928e-13 CenterZ=0 NormalX=0 NormalY=0 NormalZ=1 MajorRadius=10 MinorRadius=3.6 AngleXU=-3.14159 StartAngle=1.5708 EndAngle=3.14159
    g4: LineSegment [constr] StartX=-196.685 StartY=-5.9e-15 StartZ=0 EndX=-176.685 EndY=-5.9e-15 EndZ=0
    g5: LineSegment [constr] StartX=-186.685 StartY=-3.6 StartZ=0 EndX=-186.685 EndY=3.6 EndZ=0
    g6: GeomPoint [constr] X=-196.015 Y=-1.3e-14 Z=0
    g7: GeomPoint [constr] X=-177.356 Y=-4.9e-15 Z=0
    g8: LineSegment StartX=-176.685 StartY=-3.6 StartZ=0 EndX=-186.685 EndY=-3.6 EndZ=0
  constraints (15):
    c: PointOnObject(g2,g-3)
    c: Coincident(g1,g-5)
    c: DistanceY(g1,g1) = 0
    c: Coincident(g0,g1)
    c: DistanceX(g2,g-5) = 10
    c: Vertical(g2)
    c: Horizontal(g2,g0)
    c: InternalAlignment(g4-g7 -> g3) x4
    c: Coincident(g3,g2)
    c: Horizontal(g4)
    c: Coincident(g3,g0)
    c: Tangent(g0,g-5) = 1.5708
    c: Coincident(g3,g2)
    c: Coincident(g8,g0)
    c: Coincident(g8,g2)
FEATURE [Sketcher::SketchObject] Sketch107  label="Sketch107 - smusso impugnatura esterno"
  ArcFitTolerance = 1e-06
  AttachmentSupport = -> [Pad008]
  ExternalGeometry = -> [Pad008]
  FullyConstrained = true
  MakeInternals = false
  MapMode = 5
  Placement = pos=(0,-1.586e-13,-80.4316) rot=(1,0,0;3.14159rad)
  sketch-geometry (9):
    g0: LineSegment [constr] StartX=-215.932 StartY=-1.416e-13 StartZ=0 EndX=-215.932 EndY=-4.13e-14 EndZ=0
    g1: LineSegment StartX=-215.932 StartY=-3.6 StartZ=0 EndX=-215.932 EndY=-4.13e-14 EndZ=0
    g2: LineSegment StartX=-215.932 StartY=-3.6 StartZ=0 EndX=-205.932 EndY=-3.6 EndZ=0
    g3: LineSegment [constr] StartX=-205.932 StartY=-3.6 StartZ=0 EndX=-205.932 EndY=-4.13e-14 EndZ=0
    g4: ArcOfEllipse CenterX=-205.932 CenterY=-4.13e-14 CenterZ=0 NormalX=0 NormalY=0 NormalZ=1 MajorRadius=10 MinorRadius=3.6 AngleXU=-3.14159 StartAngle=-2.66e-14 EndAngle=1.5708
    g5: LineSegment [constr] StartX=-215.932 StartY=-1.416e-13 StartZ=0 EndX=-195.932 EndY=-1.416e-13 EndZ=0
    g6: LineSegment [constr] StartX=-205.932 StartY=-3.6 StartZ=0 EndX=-205.932 EndY=3.6 EndZ=0
    g7: GeomPoint [constr] X=-215.262 Y=-1.336e-13 Z=0
    g8: GeomPoint [constr] X=-196.602 Y=-1.551e-13 Z=0
  constraints (16):
    c: Coincident(g0,g-6)
    c: PointOnObject(g0,g-6)
    c: DistanceY(g0,g0) = 0
    c: Coincident(g1,g-6)
    c: Coincident(g1,g0)
    c: Tangent(g2,g-3)
    c: DistanceX(g2,g2) = 10
    c: Coincident(g3,g2)
    c: Vertical(g3)
    c: Horizontal(g3,g0)
    c: InternalAlignment(g5-g8 -> g4) x4
    c: Coincident(g4,g3)
    c: Horizontal(g5)
    c: Coincident(g4,g0)
    c: Coincident(g4,g2)
    c: PointOnObject(g2,g1)
FEATURE [Sketcher::SketchObject] Sketch108
  ArcFitTolerance = 1e-06
  AttachmentOffset = pos=(0,0,-1.6) rot=(0,0,1;0rad)
  AttachmentSupport = -> [Pad008]
  ExternalGeometry = -> [Binder]
  FullyConstrained = true
  MakeInternals = false
  MapMode = 5
  Placement = pos=(0,2,4e-16) rot=(0,0.707107,0.707107;3.14159rad)
  sketch-geometry (14):
    g0: LineSegment StartX=192.176 StartY=-3.18451 StartZ=0 EndX=193.827 EndY=-6.72678 EndZ=0
    g1: LineSegment [constr] StartX=202.765 StartY=20.303 StartZ=0 EndX=181.223 EndY=20.303 EndZ=0
    g2: LineSegment [constr] StartX=181.223 StartY=20.303 StartZ=0 EndX=181.223 EndY=1.30297 EndZ=0
    g3: ArcOfCircle CenterX=181.223 CenterY=-12.6042 CenterZ=0 NormalX=0 NormalY=0 NormalZ=1 AngleXU=0 Radius=13.9072 StartAngle=0.436332 EndAngle=1.5708
    g4: ArcOfEllipse CenterX=181.223 CenterY=10.803 CenterZ=0 NormalX=0 NormalY=0 NormalZ=1 MajorRadius=14.4779 MinorRadius=9.5 AngleXU=0 StartAngle=1.5708 EndAngle=4.71239
    g5: LineSegment [constr] StartX=195.701 StartY=10.803 StartZ=0 EndX=166.745 EndY=10.803 EndZ=0
    g6: LineSegment [constr] StartX=181.223 StartY=20.303 StartZ=0 EndX=181.223 EndY=1.30297 EndZ=0
    g7: GeomPoint [constr] X=192.148 Y=10.803 Z=0
    g8: GeomPoint [constr] X=170.298 Y=10.803 Z=0
    g9: LineSegment StartX=181.223 StartY=20.303 StartZ=0 EndX=202.765 EndY=20.303 EndZ=0
    g10: ArcOfCircle CenterX=207.583 CenterY=4 CenterZ=0 NormalX=0 NormalY=0 NormalZ=1 AngleXU=0 Radius=17 StartAngle=1.85815 EndAngle=3.57792
    g11: LineSegment [constr] StartX=172.411 StartY=39.2 StartZ=0 EndX=192.176 EndY=-3.18451 EndZ=0
    g12: GeomPoint [constr] X=181.223 Y=1.30297 Z=0
    g13: GeomPoint [constr] X=181.223 Y=1.30297 Z=0
  constraints (28):
    c: Coincident(g1,g-7)
    c: Horizontal(g1)
    c: Coincident(g2,g1)
    c: Vertical(g2)
    c: Coincident(g3,g2)
    c: InternalAlignment(g5-g8 -> g4) x4
    c: Horizontal(g5)
    c: PointOnObject(g4,g2)
    c: Coincident(g4,g1)
    c: DistanceX(g-3,g5) = 19.1
    c: Coincident(g4,g2)
    c: Coincident(g9,g1)
    c: Coincident(g9,g1)
    c: Coincident(g10,g1)
    c: Coincident(g10,g0)
    c: PointOnObject(g11,g-6)
    c: PointOnObject(g1,g11)
    c: DistanceY(g2,g1) = 19
    c: Coincident(g10,g-4)
    c: PointOnObject(g12,g4)
    c: PointOnObject(g12,g3)
    c: Tangent(g11,g-5) = -1.5708
    c: Tangent(g0,g-5) = -1.5708
    c: Tangent(g3,g0) = 1.5708
    c: PointOnObject(g13,g4)
    c: PointOnObject(g13,g3)
    c: Tangent(g4,g3,g13) = 1.5708
    c: Horizontal(g11,g0)
FEATURE [Part::Part2DObjectPython] Clone2D  label="Sketch108 (2D)"  # Draft 2D object (typed FeaturePython)
  Fuse = false
  Objects = -> [Sketch108]
  Placement = pos=(0,2,4e-16) rot=(0,0.707107,0.707107;3.14159rad)
  Scale = (1,1,1)
FEATURE [Sketcher::SketchObject] Sketch109
  ArcFitTolerance = 1e-06
  AttachmentOffset = pos=(0,0,-3.5) rot=(0,0,1;0rad)
  AttachmentSupport = -> [Pad008]
  ExternalGeometry = -> [Binder]
  FullyConstrained = true
  MakeInternals = false
  MapMode = 5
  Placement = pos=(0,0.1,8e-16) rot=(0,0.707107,0.707107;3.14159rad)
  sketch-geometry (1):
    g0: GeomPoint X=197.47 Y=8.55923 Z=0
  constraints (1):
    c: Symmetric(g-7,g-5,g0)
FEATURE [PartDesign::Chamfer] Chamfer005
  Angle = 45
  Base = -> Pad009 [Edge215,Edge212]
  BaseFeature = -> Pad009
  ChamferType = 1
  FlipDirection = false
  Refine = true
  Size = 1.5
  Size2 = 2.8
  SupportTransform = false
  Suppressed = false
  UseAllEdges = false
FEATURE [Sketcher::SketchObject] Sketch111
  ArcFitTolerance = 1e-06
  AttachmentSupport = -> [Pad009]
  ExternalGeometry = -> [Pad009]
  FullyConstrained = true
  MakeInternals = false
  MapMode = 5
  Placement = pos=(0,3.6,-8e-16) rot=(0,0.707107,0.707107;3.14159rad)
  sketch-geometry (21):
    g0: LineSegment [constr] StartX=97 StartY=36.8 StartZ=0 EndX=97 EndY=26.8 EndZ=0
    g1: LineSegment StartX=97 StartY=28.6 StartZ=0 EndX=97 EndY=27.8 EndZ=0
    g2: LineSegment StartX=97 StartY=27.8 StartZ=0 EndX=108 EndY=27.8 EndZ=0
    g3: LineSegment StartX=108 StartY=27.8 StartZ=0 EndX=108 EndY=28.6 EndZ=0
    g4: LineSegment StartX=108 StartY=28.6 StartZ=0 EndX=97 EndY=28.6 EndZ=0
    g5: LineSegment StartX=97 StartY=35.8 StartZ=0 EndX=97 EndY=35 EndZ=0
    g6: LineSegment StartX=97 StartY=35 StartZ=0 EndX=108 EndY=35 EndZ=0
    g7: LineSegment StartX=108 StartY=35 StartZ=0 EndX=108 EndY=35.8 EndZ=0
    g8: LineSegment StartX=108 StartY=35.8 StartZ=0 EndX=97 EndY=35.8 EndZ=0
    g9: LineSegment StartX=97 StartY=30.4 StartZ=0 EndX=97 EndY=29.6 EndZ=0
    g10: LineSegment StartX=97 StartY=29.6 StartZ=0 EndX=108 EndY=29.6 EndZ=0
    g11: LineSegment StartX=108 StartY=29.6 StartZ=0 EndX=108 EndY=30.4 EndZ=0
    g12: LineSegment StartX=108 StartY=30.4 StartZ=0 EndX=97 EndY=30.4 EndZ=0
    g13: LineSegment StartX=97 StartY=34 StartZ=0 EndX=97 EndY=33.2 EndZ=0
    g14: LineSegment StartX=97 StartY=33.2 StartZ=0 EndX=108 EndY=33.2 EndZ=0
    g15: LineSegment StartX=108 StartY=33.2 StartZ=0 EndX=108 EndY=34 EndZ=0
    g16: LineSegment StartX=108 StartY=34 StartZ=0 EndX=97 EndY=34 EndZ=0
    g17: LineSegment StartX=97 StartY=32.2 StartZ=0 EndX=97 EndY=31.4 EndZ=0
    g18: LineSegment StartX=97 StartY=31.4 StartZ=0 EndX=108 EndY=31.4 EndZ=0
    g19: LineSegment StartX=108 StartY=31.4 StartZ=0 EndX=108 EndY=32.2 EndZ=0
    g20: LineSegment StartX=108 StartY=32.2 StartZ=0 EndX=97 EndY=32.2 EndZ=0
  constraints (54):
    c: Vertical(g0)
    c: PointOnObject(g0,g-3)
    c: PointOnObject(g0,g-4)
    c: DistanceX(g0,g-5) = 11
    c: Coincident(g1,g2)
    c: Coincident(g2,g3)
    c: Coincident(g3,g4)
    c: Coincident(g4,g1)
    c: Horizontal(g2)
    c: Horizontal(g4)
    c: Tangent(g1,g0)
    c: Tangent(g3,g-5)
    c: DistanceY(g2,g3) = 0.8
    c: Coincident(g5,g6)
    c: Coincident(g6,g7)
    c: Coincident(g7,g8)
    c: Coincident(g8,g5)
    c: Horizontal(g6)
    c: Horizontal(g8)
    c: DistanceY(g6,g7) = 0.8
    c: Coincident(g9,g10)
    c: Coincident(g10,g11)
    c: Coincident(g11,g12)
    c: Coincident(g12,g9)
    c: Horizontal(g10)
    c: Horizontal(g12)
    c: DistanceY(g10,g11) = 0.8
    c: Tangent(g5,g0)
    c: Tangent(g7,g-5)
    c: Tangent(g9,g0)
    c: Tangent(g11,g-5)
    c: Coincident(g13,g14)
    c: Coincident(g14,g15)
    c: Coincident(g15,g16)
    c: Coincident(g16,g13)
    c: Horizontal(g14)
    c: Horizontal(g16)
    c: DistanceY(g14,g15) = 0.8
    c: Tangent(g13,g0)
    c: Tangent(g15,g-5)
    c: Coincident(g17,g18)
    c: Coincident(g18,g19)
    c: Coincident(g19,g20)
    c: Coincident(g20,g17)
    c: Horizontal(g18)
    c: Horizontal(g20)
    c: DistanceY(g18,g19) = 0.8
    c: Tangent(g17,g0)
    c: Tangent(g19,g-5)
    c: DistanceY(g1,g9) = 1
    c: DistanceY(g9,g17) = 1
    c: DistanceY(g17,g13) = 1
    c: DistanceY(g13,g5) = 1
    c: DistanceY(g0,g1) = 1
FEATURE [PartDesign::Pocket] Pocket004
  BaseFeature = -> Chamfer005
  Direction = (0,-1,2e-16)
  Length = 1
  Length2 = 5
  Profile = -> Sketch111
  ReferenceAxis = -> Sketch111 [N_Axis]
  Refine = true
  Suppressed = false
  Type = 0
FEATURE [PartDesign::Pad] Pad010
  BaseFeature = -> Pocket004
  Direction = (0,1,-2e-16)
  Length = 1.2
  Length2 = 10
  Profile = -> Sketch098
  ReferenceAxis = -> Sketch098 [N_Axis]
  Refine = true
  Suppressed = false
  Type = 0
FEATURE [PartDesign::Chamfer] Chamfer006
  Angle = 45
  Base = -> Pad010 [Edge291]
  BaseFeature = -> Pad010
  ChamferType = 1
  FlipDirection = false
  Refine = true
  Size = 1
  Size2 = 6
  SupportTransform = false
  Suppressed = false
  UseAllEdges = false
FEATURE [Sketcher::SketchObject] Sketch110
  ArcFitTolerance = 1e-06
  AttachmentSupport = -> [Pad010]
  ExternalGeometry = -> [Sketch098]
  FullyConstrained = true
  MakeInternals = false
  MapMode = 5
  Placement = pos=(0,4,-9e-16) rot=(0,0.707107,0.707107;3.14159rad)
  sketch-geometry (8):
    g0: LineSegment StartX=119.69 StartY=34 StartZ=0 EndX=130.69 EndY=34 EndZ=0
    g1: LineSegment StartX=119.95 StartY=33.2 StartZ=0 EndX=130.95 EndY=33.2 EndZ=0
    g2: LineSegment StartX=119.137 StartY=35.7 StartZ=0 EndX=130.137 EndY=35.7 EndZ=0
    g3: LineSegment StartX=118.877 StartY=36.5 StartZ=0 EndX=129.877 EndY=36.5 EndZ=0
    g4: LineSegment StartX=118.877 StartY=36.5 StartZ=0 EndX=119.137 EndY=35.7 EndZ=0
    g5: LineSegment StartX=129.877 StartY=36.5 StartZ=0 EndX=130.137 EndY=35.7 EndZ=0
    g6: LineSegment StartX=119.69 StartY=34 StartZ=0 EndX=119.95 EndY=33.2 EndZ=0
    g7: LineSegment StartX=130.69 StartY=34 StartZ=0 EndX=130.95 EndY=33.2 EndZ=0
  constraints (24):
    c: Horizontal(g0)
    c: Horizontal(g1)
    c: Horizontal(g2)
    c: Horizontal(g3)
    c: Equal(g1,g-5)
    c: Equal(g0,g-5)
    c: Equal(g2,g-5)
    c: Equal(g3,g-5)
    c: PointOnObject(g0,g-3)
    c: PointOnObject(g1,g-3)
    c: PointOnObject(g2,g-3)
    c: PointOnObject(g3,g-3)
    c: Coincident(g4,g3)
    c: Coincident(g4,g2)
    c: Coincident(g5,g3)
    c: Coincident(g5,g2)
    c: Coincident(g6,g0)
    c: Coincident(g6,g1)
    c: Coincident(g7,g0)
    c: Coincident(g7,g1)
    c: DistanceY(g1,g0) = 0.8
    c: DistanceY(g2,g3) = 0.8
    c: DistanceY(g-5,g1) = 2
    c: DistanceY(g-5,g2) = 4.5
FEATURE [PartDesign::Pocket] Pocket003
  BaseFeature = -> Chamfer006
  Direction = (0,-1,2e-16)
  Length = 1
  Length2 = 5
  Profile = -> Sketch110
  ReferenceAxis = -> Sketch110 [N_Axis]
  Refine = true
  Suppressed = false
  Type = 0
FEATURE [PartDesign::SubtractivePipe] SubtractivePipe
  AuxilleryCurvelinear = true
  AuxillerySpineTangent = false
  BaseFeature = -> Pocket003
  Binormal = (0,0,0)
  Mode = 0
  Profile = -> Sketch106
  Refine = true
  Spine = -> Pad008 [Edge215]
  SpineTangent = false
  Suppressed = false
  Transformation = 0
  Transition = 0
FEATURE [PartDesign::SubtractivePipe] SubtractivePipe001
  AuxilleryCurvelinear = true
  AuxillerySpineTangent = false
  BaseFeature = -> SubtractivePipe
  Binormal = (0,0,0)
  Mode = 0
  Profile = -> Sketch107
  Refine = true
  Spine = -> Pad008 [Edge213,Edge216,Edge210]
  SpineTangent = false
  Suppressed = false
  Transformation = 0
  Transition = 0
FEATURE [PartDesign::SubtractiveLoft] SubtractiveLoft
  BaseFeature = -> SubtractivePipe001
  Closed = false
  Profile = -> Sketch099
  Refine = true
  Ruled = false
  Sections = -> [Sketch108]
  Suppressed = false
FEATURE [PartDesign::SubtractiveLoft] SubtractiveLoft001
  BaseFeature = -> SubtractiveLoft
  Closed = false
  Profile = -> Clone2D
  Refine = true
  Ruled = false
  Sections = -> [Sketch109]
  Suppressed = false
FEATURE [Sketcher::SketchObject] Sketch112
  ArcFitTolerance = 1e-06
  AttachmentSupport = -> [Pad008]
  ExternalGeometry = -> [Binder]
  FullyConstrained = true
  MakeInternals = false
  MapMode = 5
  Placement = pos=(0,3.6,0) rot=(0,0.707107,0.707107;3.14159rad)
  sketch-geometry (4):
    g0: LineSegment [constr] StartX=167.782 StartY=-53.0314 StartZ=0 EndX=215.42 EndY=-53.0314 EndZ=0
    g1: GeomPoint [constr] X=191.282 Y=-53.0314 Z=0
    g2: Circle CenterX=191.282 CenterY=-53.0314 CenterZ=0 NormalX=0 NormalY=0 NormalZ=1 AngleXU=0 Radius=11.5
    g3: Circle CenterX=191.282 CenterY=-53.0314 CenterZ=0 NormalX=0 NormalY=0 NormalZ=1 AngleXU=0 Radius=10.7
  constraints (9):
    c: Horizontal(g0)
    c: PointOnObject(g0,g-3)
    c: Diameter(g2) = 23
    c: Coincident(g2,g1)
    c: Diameter(g3) = 21.4
    c: Coincident(g3,g1)
    c: DistanceX(g0,g1) = 23.5
    c: PointOnObject(g1,g0)
    c: Coincident(g0,g-4)
FEATURE [PartDesign::Chamfer] Chamfer016
  Angle = 45
  Base = -> SubtractiveLoft001 [Edge118,Edge117,Edge119,Edge120,Edge109]
  BaseFeature = -> SubtractiveLoft001
  ChamferType = 0
  FlipDirection = false
  Refine = true
  Size = 1.5
  Size2 = 1
  SupportTransform = false
  Suppressed = false
  UseAllEdges = false
FEATURE [PartDesign::Chamfer] Chamfer017
  Angle = 45
  Base = -> Chamfer016 [Edge15]
  BaseFeature = -> Chamfer016
  ChamferType = 0
  FlipDirection = false
  Refine = true
  Size = 1.6
  Size2 = 1
  SupportTransform = false
  Suppressed = false
  UseAllEdges = false
FEATURE [PartDesign::Chamfer] Chamfer018
  Angle = 45
  Base = -> Chamfer017 [Edge10]
  BaseFeature = -> Chamfer017
  ChamferType = 0
  FlipDirection = false
  Refine = true
  Size = 3.5
  Size2 = 1
  SupportTransform = false
  Suppressed = false
  UseAllEdges = false
FEATURE [PartDesign::Chamfer] Chamfer019
  Angle = 45
  Base = -> Chamfer018 [Edge94]
  BaseFeature = -> Chamfer018
  ChamferType = 0
  FlipDirection = false
  Refine = true
  Size = 1.9
  Size2 = 1
  SupportTransform = false
  Suppressed = false
  UseAllEdges = false
FEATURE [PartDesign::Fillet] Fillet009
  Base = -> Chamfer019 [Edge83]
  BaseFeature = -> Chamfer019
  Radius = 1.1
  Refine = true
  SupportTransform = false
  Suppressed = false
  UseAllEdges = false
FEATURE [PartDesign::Fillet] Fillet010
  Base = -> Fillet009 [Edge76]
  BaseFeature = -> Fillet009
  Radius = 1.9
  Refine = true
  SupportTransform = false
  Suppressed = false
  UseAllEdges = false
FEATURE [PartDesign::Pocket] Pocket005
  BaseFeature = -> Fillet010
  Direction = (0,-1,2e-16)
  Length = 0.8
  Length2 = 5
  Profile = -> Sketch112
  ReferenceAxis = -> Sketch112 [N_Axis]
  Refine = true
  Suppressed = false
  Type = 0
FEATURE [Part::Part2DObjectPython] ShapeString001  # Draft 2D object (typed FeaturePython)
  FontFile = <path>
  Fuse = false
  Justification = 6
  JustificationReference = 0
  KeepLeftMargin = false
  MakeFace = true
  ObliqueAngle = 0
  Placement = pos=(-183.5,3.6,-57.5) rot=(0,0.707107,0.707107;3.14159rad)
  ScaleToSize = true
  Size = 10
  String = AS
  Tracking = 0
FEATURE [PartDesign::Pocket] Pocket013
  BaseFeature = -> Pocket005
  Direction = (-1e-16,-1,2e-16)
  Length = 1
  Length2 = 5
  Profile = -> ShapeString001
  ReferenceAxis = -> ShapeString001 [N_Axis]
  Refine = true
  Suppressed = false
  Type = 0
FEATURE [PartDesign::Pad] Pad020
  Direction = (0,-1,2e-16)
  Length = 25.2
  Length2 = 10
  Midplane = true
  Placement = pos=(0,0,0) rot=(1,0,0;1.5708rad)
  Profile = -> Sketch021
  ReferenceAxis = -> Sketch021 [N_Axis]
  Refine = true
  Suppressed = false
  Type = 0
FEATURE [PartDesign::Body] Body001  label="perno fermo rumble e driver solenoide"
  AllowCompound = false
  Group = -> [Sketch021,Pad020]
  Origin = -> Origin001
  Tip = -> Pad020
FEATURE [PartDesign::Pad] Pad021
  Direction = (0,-1,2e-16)
  Length = 16.8
  Length2 = 10
  Midplane = true
  Placement = pos=(0,0,0) rot=(1,0,0;1.5708rad)
  Profile = -> Sketch061
  ReferenceAxis = -> Sketch061 [N_Axis]
  Refine = true
  Suppressed = false
  Type = 0
FEATURE [PartDesign::Pocket] Pocket014
  BaseFeature = -> Pad021
  Direction = (0,1,-2e-16)
  Length = 12.8
  Length2 = 5
  Midplane = true
  Placement = pos=(0,0,0) rot=(1,0,0;1.5708rad)
  Profile = -> Sketch062
  ReferenceAxis = -> Sketch062 [N_Axis]
  Refine = true
  Suppressed = false
  Type = 0
FEATURE [PartDesign::Pad] Pad022
  BaseFeature = -> Pocket014
  Direction = (0,-1,2e-16)
  Length = 7.6
  Length2 = 10
  Midplane = true
  Placement = pos=(0,0,0) rot=(1,0,0;1.5708rad)
  Profile = -> Sketch063
  ReferenceAxis = -> Sketch063 [N_Axis]
  Refine = true
  Suppressed = false
  Type = 0
FEATURE [PartDesign::Body] Body003  label="blocco switch"
  AllowCompound = false
  Group = -> [Sketch061,Sketch062,Sketch063,Pad021,Pocket014,Pad022]
  Origin = -> Origin003
  Tip = -> Pad022
FEATURE [PartDesign::Pad] Pad024
  Direction = (0,-1,2e-16)
  Length = 17
  Length2 = 10
  Midplane = true
  Placement = pos=(0,0,0) rot=(1,0,0;1.5708rad)
  Profile = -> Sketch045
  ReferenceAxis = -> Sketch045 [N_Axis]
  Refine = true
  Suppressed = false
  Type = 0
FEATURE [PartDesign::Pocket] Pocket015
  BaseFeature = -> Pad024
  Direction = (-1,0,0)
  Length = 8
  Length2 = 5
  Placement = pos=(0,0,0) rot=(1,0,0;1.5708rad)
  Profile = -> Sketch047
  ReferenceAxis = -> Sketch047 [N_Axis]
  Refine = true
  Reversed = true
  Suppressed = false
  Type = 0
FEATURE [PartDesign::Pocket] Pocket016
  BaseFeature = -> Pocket015
  Direction = (-1,0,0)
  Length = 1
  Length2 = 5
  Placement = pos=(0,0,0) rot=(1,0,0;1.5708rad)
  Profile = -> Sketch046
  ReferenceAxis = -> Sketch046 [N_Axis]
  Refine = true
  Reversed = true
  Suppressed = false
  Type = 0
FEATURE [PartDesign::Pocket] Pocket017
  BaseFeature = -> Pocket016
  Direction = (0,1,-2e-16)
  Length = 17
  Length2 = 5
  Midplane = true
  Placement = pos=(0,0,0) rot=(1,0,0;1.5708rad)
  Profile = -> Sketch048
  ReferenceAxis = -> Sketch048 [N_Axis]
  Refine = true
  Suppressed = false
  Type = 0
FEATURE [PartDesign::Pad] Pad025
  BaseFeature = -> Pocket017
  Direction = (0,-1,2e-16)
  Length = 17
  Length2 = 10
  Midplane = true
  Placement = pos=(0,0,0) rot=(1,0,0;1.5708rad)
  Profile = -> Sketch049
  ReferenceAxis = -> Sketch049 [N_Axis]
  Refine = true
  Suppressed = false
  Type = 0
FEATURE [PartDesign::Pad] Pad026
  BaseFeature = -> Pad025
  Direction = (0,-1,2e-16)
  Length = 17
  Length2 = 10
  Midplane = true
  Placement = pos=(0,0,0) rot=(1,0,0;1.5708rad)
  Profile = -> Sketch066
  ReferenceAxis = -> Sketch066 [N_Axis]
  Refine = true
  Suppressed = false
  Type = 0
FEATURE [PartDesign::Pad] Pad027
  BaseFeature = -> Pad026
  Direction = (0,-1,2e-16)
  Length = 5
  Length2 = 10
  Midplane = true
  Placement = pos=(0,0,0) rot=(1,0,0;1.5708rad)
  Profile = -> Sketch064
  ReferenceAxis = -> Sketch064 [N_Axis]
  Refine = true
  Suppressed = false
  Type = 0
FEATURE [PartDesign::Pad] Pad028
  BaseFeature = -> Pad027
  Direction = (1,0,0)
  Length = 1
  Length2 = 10
  Placement = pos=(0,0,0) rot=(1,0,0;1.5708rad)
  Profile = -> Sketch068
  ReferenceAxis = -> Sketch068 [N_Axis]
  Refine = true
  Reversed = true
  Suppressed = false
  Type = 0
FEATURE [PartDesign::Chamfer] Chamfer020
  Angle = 45
  Base = -> Pad028 [Edge73,Edge75,Edge78,Edge77]
  BaseFeature = -> Pad028
  ChamferType = 0
  FlipDirection = false
  Placement = pos=(0,0,0) rot=(1,0,0;1.5708rad)
  Refine = true
  Size = 0.5
  Size2 = 1
  SupportTransform = false
  Suppressed = false
  UseAllEdges = false
FEATURE [PartDesign::Body] Body002  label="supporto per neopixel"
  AllowCompound = false
  Group = -> [Sketch045,Sketch047,Sketch046,Sketch048,Sketch049,Sketch066,Sketch064,Sketch068,Pad024,Pocket015,Pocket016,Pocket017,Pad025,Pad026,Pad027,Pad028,Chamfer020]
  Origin = -> Origin002
  Tip = -> Chamfer020
FEATURE [Sketcher::SketchObject] Sketch134  label="perno fermo rumble002"
  ArcFitTolerance = 1e-06
  AttachmentSupport = -> [XZ_Plane008]
  FullyConstrained = true
  MakeInternals = false
  MapMode = 5
  Placement = pos=(0,0,0) rot=(1,0,0;1.5708rad)
  sketch-geometry (16):
    g0: LineSegment StartX=0 StartY=0.45 StartZ=0 EndX=0 EndY=1.55 EndZ=0
    g1: LineSegment StartX=0.45 StartY=2 StartZ=0 EndX=1.55 EndY=2 EndZ=0
    g2: LineSegment StartX=2 StartY=1.55 StartZ=0 EndX=2 EndY=0.45 EndZ=0
    g3: LineSegment StartX=1.55 StartY=0 StartZ=0 EndX=0.45 EndY=0 EndZ=0
    g4: ArcOfCircle [constr] CenterX=0.45 CenterY=1.55 CenterZ=0 NormalX=0 NormalY=0 NormalZ=1 AngleXU=0 Radius=0.45 StartAngle=1.5708 EndAngle=3.14159
    g5: GeomPoint [constr] X=0 Y=2 Z=0
    g6: LineSegment StartX=0.45 StartY=2 StartZ=0 EndX=0 EndY=1.55 EndZ=0
    g7: ArcOfCircle [constr] CenterX=1.55 CenterY=1.55 CenterZ=0 NormalX=0 NormalY=0 NormalZ=1 AngleXU=0 Radius=0.45 StartAngle=0 EndAngle=1.5708
    g8: GeomPoint [constr] X=2 Y=2 Z=0
    g9: LineSegment StartX=2 StartY=1.55 StartZ=0 EndX=1.55 EndY=2 EndZ=0
    g10: ArcOfCircle [constr] CenterX=1.55 CenterY=0.45 CenterZ=0 NormalX=0 NormalY=0 NormalZ=1 AngleXU=0 Radius=0.45 StartAngle=4.71239 EndAngle=6.28319
    g11: GeomPoint [constr] X=2 Y=0 Z=0
    g12: LineSegment StartX=1.55 StartY=0 StartZ=0 EndX=2 EndY=0.45 EndZ=0
    g13: ArcOfCircle [constr] CenterX=0.45 CenterY=0.45 CenterZ=0 NormalX=0 NormalY=0 NormalZ=1 AngleXU=0 Radius=0.45 StartAngle=3.14159 EndAngle=4.71239
    g14: GeomPoint [constr] X=0 Y=0 Z=0
    g15: LineSegment StartX=0 StartY=0.45 StartZ=0 EndX=0.45 EndY=0 EndZ=0
  constraints (35):
    c: Coincident(g14,g-1)
    c: PointOnObject(g5,g-2)
    c: Horizontal(g1)
    c: Vertical(g2)
    c: Horizontal(g3)
    c: DistanceX(g5,g8) = 2
    c: DistanceY(g11,g8) = 2
    c: PointOnObject(g5,g0)
    c: PointOnObject(g5,g1)
    c: Tangent(g0,g4) = 1.5708
    c: Tangent(g1,g4) = 1.5708
    c: Coincident(g6,g0)
    c: Coincident(g6,g1)
    c: PointOnObject(g8,g2)
    c: PointOnObject(g8,g1)
    c: Tangent(g2,g7) = 1.5708
    c: Tangent(g1,g7) = 1.5708
    c: Coincident(g9,g2)
    c: Coincident(g9,g1)
    c: PointOnObject(g11,g2)
    c: PointOnObject(g11,g3)
    c: Tangent(g2,g10) = 1.5708
    c: Tangent(g3,g10) = 1.5708
    c: Coincident(g12,g2)
    c: Coincident(g12,g3)
    c: PointOnObject(g14,g0)
    c: PointOnObject(g14,g3)
    c: Tangent(g0,g13) = 1.5708
    c: Tangent(g3,g13) = 1.5708
    c: Coincident(g15,g0)
    c: Coincident(g15,g3)
    c: Equal(g6,g9)
    c: Equal(g9,g12)
    c: Equal(g12,g15)
    c: DistanceX(g14,g3) = 0.45
FEATURE [PartDesign::Pad] Pad029
  Direction = (0,-1,2e-16)
  Length = 17
  Length2 = 10
  Midplane = true
  Placement = pos=(0,0,0) rot=(1,0,0;1.5708rad)
  Profile = -> Sketch134
  ReferenceAxis = -> Sketch134 [N_Axis]
  Refine = true
  Suppressed = false
  Type = 0
FEATURE [PartDesign::Body] Body008  label="perno fermo neopixel"
  AllowCompound = false
  Group = -> [Sketch134,Pad029]
  Origin = -> Origin008
  Tip = -> Pad029
FEATURE [Sketcher::SketchObject] Sketch135  label="perno fermo rumble003"
  ArcFitTolerance = 1e-06
  AttachmentSupport = -> [XZ_Plane009]
  FullyConstrained = true
  MakeInternals = false
  MapMode = 5
  Placement = pos=(0,0,0) rot=(1,0,0;1.5708rad)
  sketch-geometry (16):
    g0: LineSegment StartX=4.69e-14 StartY=0.8 StartZ=0 EndX=-3.04e-14 EndY=3.1 EndZ=0
    g1: LineSegment StartX=0.8 StartY=3.9 StartZ=0 EndX=3.1 EndY=3.9 EndZ=0
    g2: LineSegment StartX=3.9 StartY=3.1 StartZ=0 EndX=3.9 EndY=0.8 EndZ=0
    g3: LineSegment StartX=3.1 StartY=0 StartZ=0 EndX=0.8 EndY=0 EndZ=0
    g4: ArcOfCircle [constr] CenterX=0.8 CenterY=3.1 CenterZ=0 NormalX=0 NormalY=0 NormalZ=1 AngleXU=0 Radius=0.8 StartAngle=1.5708 EndAngle=3.14159
    g5: GeomPoint [constr] X=0 Y=3.9 Z=0
    g6: LineSegment StartX=0.8 StartY=3.9 StartZ=0 EndX=-3.04e-14 EndY=3.1 EndZ=0
    g7: ArcOfCircle [constr] CenterX=3.1 CenterY=3.1 CenterZ=0 NormalX=0 NormalY=0 NormalZ=1 AngleXU=0 Radius=0.8 StartAngle=-2.4e-14 EndAngle=1.5708
    g8: GeomPoint [constr] X=3.9 Y=3.9 Z=0
    g9: LineSegment StartX=3.9 StartY=3.1 StartZ=0 EndX=3.1 EndY=3.9 EndZ=0
    g10: ArcOfCircle [constr] CenterX=3.1 CenterY=0.8 CenterZ=0 NormalX=0 NormalY=0 NormalZ=1 AngleXU=0 Radius=0.8 StartAngle=4.71239 EndAngle=6.28319
    g11: GeomPoint [constr] X=3.9 Y=0 Z=0
    g12: LineSegment StartX=3.1 StartY=0 StartZ=0 EndX=3.9 EndY=0.8 EndZ=0
    g13: ArcOfCircle [constr] CenterX=0.8 CenterY=0.8 CenterZ=0 NormalX=0 NormalY=0 NormalZ=1 AngleXU=0 Radius=0.8 StartAngle=3.14159 EndAngle=4.71239
    g14: GeomPoint [constr] X=0 Y=0 Z=0
    g15: LineSegment StartX=4.69e-14 StartY=0.8 StartZ=0 EndX=0.8 EndY=0 EndZ=0
  constraints (35):
    c: Coincident(g14,g-1)
    c: PointOnObject(g5,g-2)
    c: Horizontal(g1)
    c: Vertical(g2)
    c: Horizontal(g3)
    c: DistanceX(g5,g8) = 3.9
    c: DistanceY(g11,g8) = 3.9
    c: PointOnObject(g5,g0)
    c: PointOnObject(g5,g1)
    c: Tangent(g0,g4) = 1.5708
    c: Tangent(g1,g4) = 1.5708
    c: Coincident(g6,g0)
    c: Coincident(g6,g1)
    c: PointOnObject(g8,g2)
    c: PointOnObject(g8,g1)
    c: Tangent(g2,g7) = 1.5708
    c: Tangent(g1,g7) = 1.5708
    c: Coincident(g9,g2)
    c: Coincident(g9,g1)
    c: PointOnObject(g11,g2)
    c: PointOnObject(g11,g3)
    c: Tangent(g2,g10) = 1.5708
    c: Tangent(g3,g10) = 1.5708
    c: Coincident(g12,g2)
    c: Coincident(g12,g3)
    c: PointOnObject(g14,g0)
    c: PointOnObject(g14,g3)
    c: Tangent(g0,g13) = 1.5708
    c: Tangent(g3,g13) = 1.5708
    c: Coincident(g15,g0)
    c: Coincident(g15,g3)
    c: Equal(g6,g9)
    c: Equal(g9,g12)
    c: Equal(g12,g15)
    c: DistanceX(g14,g3) = 0.8
FEATURE [PartDesign::Pad] Pad030
  Direction = (0,-1,2e-16)
  Length = 25.2
  Length2 = 10
  Midplane = true
  Placement = pos=(0,0,0) rot=(1,0,0;1.5708rad)
  Profile = -> Sketch135
  ReferenceAxis = -> Sketch135 [N_Axis]
  Refine = true
  Suppressed = false
  Type = 0
FEATURE [PartDesign::Body] Body009  label="perno fermo switch - caricabatterie - grilletto"
  AllowCompound = false
  Group = -> [Sketch135,Pad030]
  Origin = -> Origin009
  Tip = -> Pad030
FEATURE [Sketcher::SketchObject] Sketch136  label="scavo_rele"
  ArcFitTolerance = 1e-06
  AttachmentSupport = -> [XZ_Plane]
  ExternalGeometry = -> [Sketch]
  FullyConstrained = true
  MakeInternals = false
  MapMode = 5
  Placement = pos=(0,0,0) rot=(1,0,0;1.5708rad)
  sketch-geometry (7):
    g0: LineSegment [constr] StartX=-173.013 StartY=-62.644 StartZ=0 EndX=-176.535 EndY=-73.4861 EndZ=0
    g1: LineSegment [constr] StartX=-173.013 StartY=-62.644 StartZ=0 EndX=-170.35 EndY=-63.5093 EndZ=0
    g2: LineSegment [constr] StartX=-173.013 StartY=-62.644 StartZ=0 EndX=-176.627 EndY=-61.4698 EndZ=0
    g3: LineSegment StartX=-176.627 StartY=-61.4698 StartZ=0 EndX=-170.35 EndY=-63.5093 EndZ=0
    g4: LineSegment StartX=-176.627 StartY=-61.4698 StartZ=0 EndX=-180.149 EndY=-72.3118 EndZ=0
    g5: LineSegment StartX=-170.35 StartY=-63.5093 StartZ=0 EndX=-173.872 EndY=-74.3513 EndZ=0
    g6: LineSegment StartX=-180.149 StartY=-72.3118 StartZ=0 EndX=-173.872 EndY=-74.3513 EndZ=0
  constraints (19):
    c: Tangent(g0,g-3)
    c: Distance(g0,g-3) = 89
    c: Distance(g0,g0) = 11.4
    c: Coincident(g1,g0)
    c: Coincident(g2,g0)
    c: Distance(g2) = 3.8
    c: Distance(g1) = 2.8
    c: Perpendicular(g0,g1)
    c: Perpendicular(g0,g2)
    c: Coincident(g3,g2)
    c: Coincident(g3,g1)
    c: Equal(g4,g0)
    c: Equal(g5,g0)
    c: Parallel(g4,g0)
    c: Parallel(g5,g0)
    c: Coincident(g4,g2)
    c: Coincident(g5,g1)
    c: Coincident(g6,g4)
    c: Coincident(g6,g5)
FEATURE [Part::Extrusion] Extrude076  label="Extrude076 - scavo_rele"
  Base = -> Sketch136
  Dir = (0,-1,2e-16)
  DirMode = 2
  FaceMakerClass = Part::FaceMakerBullseye
  FaceMakerMode = 3
  LengthFwd = 17.8
  LengthRev = 0
  Solid = true
  Symmetric = true
FEATURE [Sketcher::SketchObject] Sketch137  label="scavo_nuovo_driver"
  ArcFitTolerance = 1e-06
  AttachmentSupport = -> [XZ_Plane]
  ExternalGeometry = -> [Sketch]
  FullyConstrained = true
  MakeInternals = false
  MapMode = 5
  Placement = pos=(0,0,0) rot=(1,0,0;1.5708rad)
  sketch-geometry (7):
    g0: LineSegment [constr] StartX=-160.157 StartY=-23.0801 StartZ=0 EndX=-164.978 EndY=-37.9166 EndZ=0
    g1: LineSegment [constr] StartX=-160.157 StartY=-23.0801 StartZ=0 EndX=-157.875 EndY=-23.8217 EndZ=0
    g2: LineSegment [constr] StartX=-160.157 StartY=-23.0801 StartZ=0 EndX=-163.771 EndY=-21.9058 EndZ=0
    g3: LineSegment StartX=-163.771 StartY=-21.9058 StartZ=0 EndX=-157.875 EndY=-23.8217 EndZ=0
    g4: LineSegment StartX=-163.771 StartY=-21.9058 StartZ=0 EndX=-168.592 EndY=-36.7423 EndZ=0
    g5: LineSegment StartX=-157.875 StartY=-23.8217 StartZ=0 EndX=-162.696 EndY=-38.6582 EndZ=0
    g6: LineSegment StartX=-168.592 StartY=-36.7423 StartZ=0 EndX=-162.696 EndY=-38.6582 EndZ=0
  constraints (19):
    c: Distance(g0,g-3) = 47.4
    c: Distance(g0) = 15.6
    c: Tangent(g0,g-3)
    c: Coincident(g1,g0)
    c: Coincident(g2,g0)
    c: Distance(g1) = 2.4
    c: Distance(g2) = 3.8
    c: Perpendicular(g0,g1)
    c: Perpendicular(g0,g2)
    c: Coincident(g3,g2)
    c: Coincident(g3,g1)
    c: Equal(g4,g0)
    c: Equal(g5,g0)
    c: Parallel(g4,g0)
    c: Parallel(g5,g0)
    c: Coincident(g4,g2)
    c: Coincident(g5,g1)
    c: Coincident(g6,g4)
    c: Coincident(g6,g5)
FEATURE [Part::Extrusion] Extrude077  label="Extrude077 - scavo_nuovo_driver"
  Base = -> Sketch137
  Dir = (0,-1,2e-16)
  DirMode = 2
  FaceMakerClass = Part::FaceMakerBullseye
  FaceMakerMode = 3
  LengthFwd = 20.8
  LengthRev = 0
  Solid = true
  Symmetric = true
FEATURE [Sketcher::SketchObject] Sketch138  label="scavo_nuovo_driver_alto"
  ArcFitTolerance = 1e-06
  AttachmentSupport = -> [XZ_Plane]
  ExternalGeometry = -> [Sketch]
  FullyConstrained = true
  MakeInternals = false
  MapMode = 5
  Placement = pos=(0,0,0) rot=(1,0,0;1.5708rad)
  sketch-geometry (7):
    g0: LineSegment [constr] StartX=-188.796 StartY=17.7274 StartZ=0 EndX=-187.75 EndY=4.97025 EndZ=0
    g1: LineSegment StartX=-187.75 StartY=4.97025 StartZ=0 EndX=-189.743 EndY=4.8067 EndZ=0
    g2: LineSegment StartX=-187.75 StartY=4.97025 StartZ=0 EndX=-182.766 EndY=5.37913 EndZ=0
    g3: LineSegment StartX=-190.79 StartY=17.5638 StartZ=0 EndX=-189.743 EndY=4.8067 EndZ=0
    g4: LineSegment StartX=-183.813 StartY=18.1363 StartZ=0 EndX=-182.766 EndY=5.37913 EndZ=0
    g5: LineSegment StartX=-190.79 StartY=17.5638 StartZ=0 EndX=-188.796 EndY=17.7274 EndZ=0
    g6: LineSegment StartX=-188.796 StartY=17.7274 StartZ=0 EndX=-183.813 EndY=18.1363 EndZ=0
  constraints (20):
    c: Distance(g0) = 12.8
    c: DistanceY(g-3,g0) = 9
    c: PointOnObject(g0,g-4)
    c: PointOnObject(g0,g-4)
    c: Coincident(g1,g0)
    c: Coincident(g2,g0)
    c: Distance(g1) = 2
    c: Distance(g2) = 5
    c: Perpendicular(g0,g1)
    c: Perpendicular(g0,g2)
    c: Equal(g3,g0)
    c: Parallel(g3,g0)
    c: Coincident(g3,g1)
    c: Equal(g4,g0)
    c: Parallel(g4,g0)
    c: Coincident(g4,g2)
    c: Coincident(g5,g3)
    c: Coincident(g5,g0)
    c: Coincident(g6,g0)
    c: Coincident(g6,g4)
FEATURE [Part::Extrusion] Extrude078  label="Extrude078 - scavo_nuovo_driver_alto"
  Base = -> Sketch138
  Dir = (0,-1,2e-16)
  DirMode = 2
  FaceMakerClass = Part::FaceMakerBullseye
  FaceMakerMode = 3
  LengthFwd = 16.6
  LengthRev = 0
  Solid = true
  Symmetric = true
FEATURE [Sketcher::SketchObject] Sketch139  label="fermi_nuovo_driver_alto"
  ArcFitTolerance = 1e-06
  AttachmentSupport = -> [XZ_Plane]
  ExternalGeometry = -> [Sketch138,Sketch]
  FullyConstrained = true
  MakeInternals = false
  MapMode = 5
  Placement = pos=(0,0,0) rot=(1,0,0;1.5708rad)
  sketch-geometry (17):
    g0: LineSegment [constr] StartX=-188.314 StartY=16.4295 StartZ=0 EndX=-187.885 EndY=13.7638 EndZ=0
    g1: LineSegment [constr] StartX=-187.885 StartY=13.7638 StartZ=0 EndX=-187.456 EndY=11.0981 EndZ=0
    g2: LineSegment StartX=-187.885 StartY=13.7638 StartZ=0 EndX=-187.71 EndY=12.6778 EndZ=0
    g3: LineSegment StartX=-187.885 StartY=13.7638 StartZ=0 EndX=-188.06 EndY=14.8499 EndZ=0
    g4: LineSegment StartX=-187.71 StartY=12.6778 StartZ=0 EndX=-185.538 EndY=13.0274 EndZ=0
    g5: LineSegment StartX=-188.06 StartY=14.8499 StartZ=0 EndX=-185.888 EndY=15.1994 EndZ=0
    g6: LineSegment StartX=-185.888 StartY=15.1994 StartZ=0 EndX=-185.538 EndY=13.0274 EndZ=0
    g7: LineSegment StartX=-187.456 StartY=11.0981 StartZ=0 EndX=-189.035 EndY=10.8439 EndZ=0
    g8: LineSegment StartX=-188.314 StartY=16.4295 StartZ=0 EndX=-189.893 EndY=16.1753 EndZ=0
    g9: LineSegment StartX=-189.893 StartY=16.1753 StartZ=0 EndX=-189.035 EndY=10.8439 EndZ=0
    g10: LineSegment StartX=-187.456 StartY=11.0981 StartZ=0 EndX=-185.284 EndY=11.4477 EndZ=0
    g11: LineSegment StartX=-188.314 StartY=16.4295 StartZ=0 EndX=-186.142 EndY=16.7791 EndZ=0
    g12: LineSegment StartX=-184.308 StartY=15.4537 StartZ=0 EndX=-183.958 EndY=13.2816 EndZ=0
    g13: ArcOfCircle CenterX=-185.888 CenterY=15.1994 CenterZ=0 NormalX=0 NormalY=0 NormalZ=1 AngleXU=0 Radius=1.6 StartAngle=0.15957 EndAngle=1.73037
    g14: GeomPoint [constr] X=-184.562 Y=17.0333 Z=0
    g15: ArcOfCircle CenterX=-185.538 CenterY=13.0274 CenterZ=0 NormalX=0 NormalY=0 NormalZ=1 AngleXU=0 Radius=1.6 StartAngle=4.87196 EndAngle=6.44276
    g16: GeomPoint [constr] X=-183.704 Y=11.7019 Z=0
  constraints (43):
    c: Tangent(g1,g0) = -1.5708
    c: Distance(g0) = 2.7
    c: Equal(g1,g0)
    c: Tangent(g1,g-5)
    c: Coincident(g2,g0)
    c: Coincident(g3,g0)
    c: Distance(g2) = 1.1
    c: Equal(g3,g2)
    c: PointOnObject(g3,g2)
    c: Coincident(g4,g2)
    c: Coincident(g5,g3)
    c: Distance(g4) = 2.2
    c: Equal(g4,g5)
    c: Perpendicular(g1,g4)
    c: Perpendicular(g0,g5)
    c: Coincident(g6,g5)
    c: Coincident(g6,g4)
    c: Coincident(g7,g1)
    c: Coincident(g8,g0)
    c: Distance(g7) = 1.6
    c: Equal(g7,g8)
    c: Perpendicular(g1,g7)
    c: Perpendicular(g8,g0)
    c: Coincident(g9,g8)
    c: Coincident(g9,g7)
    c: Coincident(g10,g1)
    c: Coincident(g11,g0)
    c: Distance(g10,g16) = 3.8
    c: Perpendicular(g1,g10)
    c: Perpendicular(g1,g11)
    c: DistanceY(g0,g-4) = 3.8
    c: PointOnObject(g14,g12)
    c: PointOnObject(g14,g11)
    c: Tangent(g12,g13) = 1.5708
    c: Tangent(g11,g13) = 1.5708
    c: PointOnObject(g16,g12)
    c: PointOnObject(g16,g10)
    c: Tangent(g12,g15) = 1.5708
    c: Tangent(g10,g15) = -1.5708
    c: Equal(g13,g15)
    c: Coincident(g13,g5)
    c: Parallel(g2,g0)
    c: PointOnObject(g0,g-5)
FEATURE [Part::Extrusion] Extrude079  label="Extrude079 - fermi_nuovo_driver_alto"
  Base = -> Sketch139
  Dir = (0,-1,2e-16)
  DirMode = 2
  FaceMakerClass = Part::FaceMakerBullseye
  FaceMakerMode = 3
  LengthFwd = 25.2
  LengthRev = 0
  Solid = true
  Symmetric = true
FEATURE [Sketcher::SketchObject] Sketch140  label="scavo_diodo_nuovo_driver_alto"
  ArcFitTolerance = 1e-06
  AttachmentSupport = -> [XZ_Plane]
  ExternalGeometry = -> [Sketch138]
  FullyConstrained = true
  MakeInternals = false
  MapMode = 5
  Placement = pos=(0,0,0) rot=(1,0,0;1.5708rad)
  sketch-geometry (4):
    g0: LineSegment StartX=-190.79 StartY=17.5638 StartZ=0 EndX=-189.743 EndY=4.8067 EndZ=0
    g1: LineSegment StartX=-193.78 StartY=17.3185 StartZ=0 EndX=-192.733 EndY=4.56137 EndZ=0
    g2: LineSegment StartX=-190.79 StartY=17.5638 StartZ=0 EndX=-193.78 EndY=17.3185 EndZ=0
    g3: LineSegment StartX=-192.733 StartY=4.56137 StartZ=0 EndX=-189.743 EndY=4.8067 EndZ=0
  constraints (11):
    c: Equal(g0,g-3)
    c: Parallel(g0,g-3)
    c: Equal(g1,g-3)
    c: Parallel(g1,g-3)
    c: Coincident(g2,g0)
    c: Distance(g2) = 3
    c: Perpendicular(g0,g2)
    c: Coincident(g1,g2)
    c: Coincident(g3,g1)
    c: Coincident(g3,g0)
    c: Coincident(g0,g-3)
FEATURE [Part::Extrusion] Extrude080  label="Extrude080 - scavo_diodo_nuovo_driver_alto"
  Base = -> Sketch140
  Dir = (0,-1,2e-16)
  DirMode = 2
  FaceMakerClass = Part::FaceMakerBullseye
  FaceMakerMode = 3
  LengthFwd = 4
  LengthRev = 0
  Placement = pos=(0,7.8,0) rot=(0,0,1;0rad)
  Solid = true
  Symmetric = false
FEATURE [Part::MultiFuse] Fusion001
  Refine = true
  Shapes = -> [Cut043,Extrude079]
FEATURE [Part::Cut] Cut044
  Base = -> Fusion001
  Refine = true
  Tool = -> Extrude078
FEATURE [Part::Cut] Cut045
  Base = -> Cut044
  Refine = true
  Tool = -> Extrude080
FEATURE [Sketcher::SketchObject] Sketch141  label="fermi_nuovo_driver"
  ArcFitTolerance = 1e-06
  AttachmentSupport = -> [XZ_Plane]
  ExternalGeometry = -> [Sketch,Sketch137]
  FullyConstrained = true
  MakeInternals = false
  MapMode = 5
  Placement = pos=(0,0,0) rot=(1,0,0;1.5708rad)
  sketch-geometry (16):
    g0: LineSegment [constr] StartX=-157.875 StartY=-23.8217 StartZ=0 EndX=-160.157 EndY=-23.0801 EndZ=0
    g1: LineSegment [constr] StartX=-160.157 StartY=-23.0801 StartZ=0 EndX=-160.405 EndY=-23.8409 EndZ=0
    g2: LineSegment [constr] StartX=-160.405 StartY=-23.8409 StartZ=0 EndX=-162.073 EndY=-28.9766 EndZ=0
    g3: LineSegment StartX=-162.073 StartY=-28.9766 StartZ=0 EndX=-164.166 EndY=-28.2968 EndZ=0
    g4: LineSegment StartX=-165.193 StartY=-26.2807 StartZ=0 EndX=-164.513 EndY=-24.1883 EndZ=0
    g5: LineSegment StartX=-162.497 StartY=-23.1611 StartZ=0 EndX=-158.883 EndY=-24.3354 EndZ=0
    g6: LineSegment StartX=-158.883 StartY=-24.3354 StartZ=0 EndX=-160.552 EndY=-29.4711 EndZ=0
    g7: LineSegment StartX=-162.073 StartY=-28.9766 StartZ=0 EndX=-160.552 EndY=-29.4711 EndZ=0
    g8: LineSegment StartX=-162.991 StartY=-24.6828 StartZ=0 EndX=-163.671 EndY=-26.7751 EndZ=0
    g9: LineSegment StartX=-163.671 StartY=-26.7751 StartZ=0 EndX=-161.579 EndY=-27.4549 EndZ=0
    g10: LineSegment StartX=-161.579 StartY=-27.4549 StartZ=0 EndX=-160.899 EndY=-25.3626 EndZ=0
    g11: LineSegment StartX=-160.899 StartY=-25.3626 StartZ=0 EndX=-162.991 EndY=-24.6828 EndZ=0
    g12: ArcOfCircle CenterX=-162.991 CenterY=-24.6828 CenterZ=0 NormalX=0 NormalY=0 NormalZ=1 AngleXU=0 Radius=1.6 StartAngle=1.25664 EndAngle=2.82743
    g13: GeomPoint [constr] X=-164.019 Y=-22.6667 Z=0
    g14: ArcOfCircle CenterX=-163.671 CenterY=-26.7751 CenterZ=0 NormalX=0 NormalY=0 NormalZ=1 AngleXU=0 Radius=1.6 StartAngle=2.82743 EndAngle=4.39823
    g15: GeomPoint [constr] X=-165.687 Y=-27.8024 Z=0
  constraints (41):
    c: Coincident(g0,g-4)
    c: PointOnObject(g0,g-3)
    c: Parallel(g0,g-4)
    c: Coincident(g1,g0)
    c: Parallel(g1,g-3)
    c: Distance(g1) = 0.8
    c: Coincident(g2,g1)
    c: Distance(g2) = 5.4
    c: Coincident(g3,g2)
    c: Parallel(g2,g-3)
    c: Distance(g15,g13) = 5.4
    c: Perpendicular(g3,g2)
    c: Parallel(g4,g2)
    c: Distance(g5,g13) = 5.4
    c: Distance(g3,g15) = 3.8
    c: Perpendicular(g4,g5)
    c: Coincident(g6,g5)
    c: Distance(g6) = 5.4
    c: Parallel(g6,g4)
    c: Coincident(g7,g2)
    c: Coincident(g7,g6)
    c: Coincident(g8,g9)
    c: Coincident(g9,g10)
    c: Coincident(g10,g11)
    c: Coincident(g11,g8)
    c: Distance(g8,g10) = 2.2
    c: Distance(g9,g11) = 2.2
    c: Perpendicular(g11,g8)
    c: Equal(g8,g10)
    c: Equal(g11,g9)
    c: Tangent(g10,g2)
    c: Distance(g10,g1) = 1.6
    c: PointOnObject(g13,g4)
    c: PointOnObject(g13,g5)
    c: Tangent(g4,g12) = 1.5708
    c: Tangent(g5,g12) = 1.5708
    c: PointOnObject(g15,g4)
    c: Tangent(g4,g14) = 1.5708
    c: Tangent(g3,g14) = 1.5708
    c: Equal(g14,g12)
    c: Coincident(g12,g8)
FEATURE [Part::Extrusion] Extrude081  label="Extrude081 - fermi_nuovo_driver"
  Base = -> Sketch141
  Dir = (0,-1,2e-16)
  DirMode = 2
  FaceMakerClass = Part::FaceMakerBullseye
  FaceMakerMode = 3
  LengthFwd = 25.2
  LengthRev = 0
  Solid = true
  Symmetric = true
FEATURE [Part::MultiFuse] Fusion002
  Refine = true
  Shapes = -> [Cut045,Extrude081]
FEATURE [Part::Cut] Cut046
  Base = -> Fusion002
  Refine = true
  Tool = -> Extrude077
FEATURE [Sketcher::SketchObject] Sketch142  label="fermi_rele"
  ArcFitTolerance = 1e-06
  AttachmentSupport = -> [XZ_Plane]
  ExternalGeometry = -> [Sketch,Sketch136]
  FullyConstrained = true
  MakeInternals = false
  MapMode = 5
  Placement = pos=(0,0,0) rot=(1,0,0;1.5708rad)
  sketch-geometry (15):
    g0: LineSegment StartX=-177.245 StartY=-63.3719 StartZ=0 EndX=-177.924 EndY=-65.4642 EndZ=0
    g1: LineSegment StartX=-175.228 StartY=-62.3446 StartZ=0 EndX=-171.614 EndY=-63.5189 EndZ=0
    g2: LineSegment StartX=-171.614 StartY=-63.5189 StartZ=0 EndX=-173.283 EndY=-68.6546 EndZ=0
    g3: LineSegment StartX=-176.897 StartY=-67.4803 StartZ=0 EndX=-173.283 EndY=-68.6546 EndZ=0
    g4: LineSegment StartX=-175.723 StartY=-63.8663 StartZ=0 EndX=-173.631 EndY=-64.5461 EndZ=0
    g5: LineSegment StartX=-175.723 StartY=-63.8663 StartZ=0 EndX=-176.403 EndY=-65.9586 EndZ=0
    g6: LineSegment StartX=-173.631 StartY=-64.5461 StartZ=0 EndX=-174.31 EndY=-66.6385 EndZ=0
    g7: LineSegment StartX=-176.403 StartY=-65.9586 StartZ=0 EndX=-174.31 EndY=-66.6385 EndZ=0
    g8: LineSegment [constr] StartX=-173.631 StartY=-64.5461 StartZ=0 EndX=-173.136 EndY=-63.0245 EndZ=0
    g9: LineSegment [constr] StartX=-173.631 StartY=-64.5461 StartZ=0 EndX=-172.109 EndY=-65.0406 EndZ=0
    g10: LineSegment [constr] StartX=-170.35 StartY=-63.5093 StartZ=0 EndX=-173.013 EndY=-62.644 EndZ=0
    g11: ArcOfCircle CenterX=-175.723 CenterY=-63.8663 CenterZ=0 NormalX=0 NormalY=0 NormalZ=1 AngleXU=0 Radius=1.6 StartAngle=1.25664 EndAngle=2.82743
    g12: GeomPoint [constr] X=-176.75 Y=-61.8502 Z=0
    g13: ArcOfCircle CenterX=-176.403 CenterY=-65.9586 CenterZ=0 NormalX=0 NormalY=0 NormalZ=1 AngleXU=0 Radius=1.6 StartAngle=2.82743 EndAngle=4.39823
    g14: GeomPoint [constr] X=-178.419 Y=-66.9859 Z=0
  constraints (39):
    c: Distance(g14,g12) = 5.4
    c: Distance(g1,g12) = 5.4
    c: Perpendicular(g1,g0)
    c: Coincident(g2,g1)
    c: Parallel(g2,g0)
    c: Coincident(g3,g2)
    c: Parallel(g2,g-3)
    c: Coincident(g5,g4)
    c: Distance(g5) = 2.2
    c: Distance(g4) = 2.2
    c: Perpendicular(g4,g5)
    c: Coincident(g6,g4)
    c: Equal(g6,g5)
    c: Parallel(g6,g5)
    c: Coincident(g7,g5)
    c: Coincident(g7,g6)
    c: Coincident(g8,g4)
    c: Coincident(g9,g4)
    c: Distance(g8) = 1.6
    c: Distance(g9) = 1.6
    c: Parallel(g8,g6)
    c: Parallel(g9,g4)
    c: PointOnObject(g8,g1)
    c: PointOnObject(g9,g2)
    c: Coincident(g10,g-4)
    c: Parallel(g10,g-4)
    c: PointOnObject(g10,g-3)
    c: Tangent(g6,g-3) = 1.5708
    c: Distance(g4,g10) = 2
    c: PointOnObject(g12,g1)
    c: Tangent(g1,g11) = 1.5708
    c: Tangent(g0,g11) = -1.5708
    c: PointOnObject(g14,g3)
    c: PointOnObject(g14,g0)
    c: Tangent(g3,g13) = -1.5708
    c: Tangent(g0,g13) = -1.5708
    c: Equal(g11,g13)
    c: Coincident(g11,g4)
    c: Parallel(g3,g1)
FEATURE [Part::Extrusion] Extrude082  label="Extrude082 - fermi_rele"
  Base = -> Sketch142
  Dir = (0,-1,2e-16)
  DirMode = 2
  FaceMakerClass = Part::FaceMakerBullseye
  FaceMakerMode = 3
  LengthFwd = 25.2
  LengthRev = 0
  Solid = true
  Symmetric = true
FEATURE [Part::MultiFuse] Fusion003
  Refine = true
  Shapes = -> [Cut046,Extrude082]
FEATURE [Part::Cut] Cut047
  Base = -> Fusion003
  Refine = true
  Tool = -> Extrude076
FEATURE [Sketcher::SketchObject] Sketch143  label="foro_passaggio_cavi_led_batteria"
  ArcFitTolerance = 1e-06
  AttachmentSupport = -> [XZ_Plane]
  ExternalGeometry = -> [Sketch,Sketch042,Sketch036]
  FullyConstrained = true
  MakeInternals = false
  MapMode = 5
  Placement = pos=(0,0,0) rot=(1,0,0;1.5708rad)
  sketch-geometry (4):
    g0: LineSegment StartX=-207.775 StartY=-41.3701 StartZ=0 EndX=-213.607 EndY=-53.8767 EndZ=0
    g1: LineSegment StartX=-213.607 StartY=-53.8767 StartZ=0 EndX=-211.843 EndY=-59.5559 EndZ=0
    g2: LineSegment StartX=-207.775 StartY=-41.3701 StartZ=0 EndX=-207.775 EndY=-50.8316 EndZ=0
    g3: LineSegment StartX=-207.775 StartY=-50.8316 StartZ=0 EndX=-211.843 EndY=-59.5559 EndZ=0
  constraints (9):
    c: Coincident(g0,g-3)
    c: PointOnObject(g1,g-6)
    c: Coincident(g1,g0)
    c: Coincident(g2,g0)
    c: Coincident(g2,g-7)
    c: Coincident(g3,g2)
    c: Parallel(g3,g0)
    c: Coincident(g3,g1)
    c: Coincident(g0,g-5)
FEATURE [Part::Extrusion] Extrude083  label="Extrude083 - foro_passaggio_cavi_led_batteria"
  Base = -> Sketch143
  Dir = (0,-1,2e-16)
  DirMode = 2
  FaceMakerClass = Part::FaceMakerBullseye
  FaceMakerMode = 3
  LengthFwd = 6
  LengthRev = 0
  Solid = true
  Symmetric = true
FEATURE [Part::Cut] Cut048
  Base = -> Cut047
  Refine = true
  Tool = -> Extrude083
FEATURE [Sketcher::SketchObject] Sketch144  label="foro_areazione_alimentatore"
  ArcFitTolerance = 1e-06
  AttachmentSupport = -> [XZ_Plane]
  ExternalGeometry = -> [Sketch036]
  FullyConstrained = true
  MakeInternals = false
  MapMode = 5
  Placement = pos=(0,0,0) rot=(1,0,0;1.5708rad)
  sketch-geometry (4):
    g0: LineSegment StartX=-211.843 StartY=-60.3701 StartZ=0 EndX=-207.775 EndY=-60.3701 EndZ=0
    g1: LineSegment StartX=-207.775 StartY=-60.3701 StartZ=0 EndX=-207.775 EndY=-70.3701 EndZ=0
    g2: LineSegment StartX=-211.843 StartY=-60.3701 StartZ=0 EndX=-211.843 EndY=-70.3701 EndZ=0
    g3: LineSegment StartX=-207.775 StartY=-70.3701 StartZ=0 EndX=-211.843 EndY=-70.3701 EndZ=0
  constraints (11):
    c: Horizontal(g0)
    c: Distance(g1) = 10
    c: Coincident(g1,g0)
    c: Tangent(g1,g-3)
    c: PointOnObject(g0,g-4)
    c: Coincident(g2,g0)
    c: PointOnObject(g2,g-4)
    c: Coincident(g3,g1)
    c: Horizontal(g3)
    c: Coincident(g3,g2)
    c: DistanceY(g0,g-3) = 19
FEATURE [Part::Extrusion] Extrude084  label="Extrude084 - foro_areazione_alimentatore"
  Base = -> Sketch144
  Dir = (0,-1,2e-16)
  DirMode = 2
  FaceMakerClass = Part::FaceMakerBullseye
  FaceMakerMode = 3
  LengthFwd = 10
  LengthRev = 0
  Solid = true
  Symmetric = true
FEATURE [Part::Cut] Cut049
  Base = -> Cut048
  Refine = true
  Tool = -> Extrude084
FEATURE [Sketcher::SketchObject] Sketch145  label="foro_per_condesatore"
  ArcFitTolerance = 1e-06
  AttachmentSupport = -> [XZ_Plane]
  ExternalGeometry = -> [Sketch,Sketch139]
  FullyConstrained = true
  MakeInternals = false
  MapMode = 5
  Placement = pos=(0,0,0) rot=(1,0,0;1.5708rad)
  sketch-geometry (1):
    g0: Circle CenterX=-182.345 CenterY=7.02342 CenterZ=0 NormalX=0 NormalY=0 NormalZ=1 AngleXU=0 Radius=5.2
  constraints (3):
    c: Diameter(g0) = 10.4
    c: Tangent(g0,g-3)
    c: Tangent(g0,g-4)
FEATURE [Part::Extrusion] Extrude085  label="Extrude085 - foro_per_condesatore"
  Base = -> Sketch145
  Dir = (0,-1,2e-16)
  DirMode = 2
  FaceMakerClass = Part::FaceMakerBullseye
  FaceMakerMode = 3
  LengthFwd = 25.2
  LengthRev = 0
  Solid = true
  Symmetric = true
FEATURE [Part::Cut] Cut050
  Base = -> Cut049
  Refine = true
  Tool = -> Extrude085
FEATURE [Sketcher::SketchObject] Sketch146  label="scavo_pulsante_6x6_per_led_batteria"
  ArcFitTolerance = 1e-06
  AttachmentSupport = -> [XZ_Plane]
  ExternalGeometry = -> [Sketch016]
  FullyConstrained = true
  MakeInternals = false
  MapMode = 5
  Placement = pos=(0,0,0) rot=(1,0,0;1.5708rad)
  sketch-geometry (5):
    g0: LineSegment StartX=-216.643 StartY=-65.8316 StartZ=0 EndX=-216.643 EndY=-72.8316 EndZ=0
    g1: LineSegment StartX=-216.643 StartY=-72.8316 StartZ=0 EndX=-210.243 EndY=-72.8316 EndZ=0
    g2: LineSegment StartX=-210.243 StartY=-72.8316 StartZ=0 EndX=-210.243 EndY=-65.8316 EndZ=0
    g3: LineSegment StartX=-210.243 StartY=-65.8316 StartZ=0 EndX=-216.643 EndY=-65.8316 EndZ=0
    g4: GeomPoint [constr] X=-213.443 Y=-69.3316 Z=0
  constraints (13):
    c: Coincident(g0,g1)
    c: Coincident(g1,g2)
    c: Coincident(g2,g3)
    c: Coincident(g3,g0)
    c: Vertical(g0)
    c: Vertical(g2)
    c: Horizontal(g1)
    c: Horizontal(g3)
    c: Distance(g0,g2) = 6.4
    c: Distance(g1,g3) = 7
    c: Tangent(g1,g-3)
    c: Symmetric(g0,g2,g4)
    c: Vertical(g-3,g4)
FEATURE [Part::Extrusion] Extrude086  label="Extrude086 - scavo_pulsante_6x6_per_led_batteria"
  Base = -> Sketch146
  Dir = (0,-1,2e-16)
  DirMode = 2
  FaceMakerClass = Part::FaceMakerBullseye
  FaceMakerMode = 3
  LengthFwd = 4
  LengthRev = 0
  Placement = pos=(0,12.6,0) rot=(0,0,1;0rad)
  Solid = true
  Symmetric = false
FEATURE [Sketcher::SketchObject] Sketch147  label="scavo_led_stato_batteria"
  ArcFitTolerance = 1e-06
  AttachmentSupport = -> [XZ_Plane]
  ExternalGeometry = -> [Sketch016]
  FullyConstrained = true
  MakeInternals = false
  MapMode = 5
  Placement = pos=(0,0,0) rot=(1,0,0;1.5708rad)
  sketch-geometry (5):
    g0: LineSegment StartX=-215.843 StartY=-56.2316 StartZ=0 EndX=-215.843 EndY=-65.4316 EndZ=0
    g1: LineSegment StartX=-215.843 StartY=-65.4316 StartZ=0 EndX=-211.043 EndY=-65.4316 EndZ=0
    g2: LineSegment StartX=-211.043 StartY=-65.4316 StartZ=0 EndX=-211.043 EndY=-56.2316 EndZ=0
    g3: LineSegment StartX=-211.043 StartY=-56.2316 StartZ=0 EndX=-215.843 EndY=-56.2316 EndZ=0
    g4: GeomPoint [constr] X=-213.443 Y=-60.8316 Z=0
  constraints (13):
    c: Coincident(g0,g1)
    c: Coincident(g1,g2)
    c: Coincident(g2,g3)
    c: Coincident(g3,g0)
    c: Distance(g0,g2) = 4.8
    c: Distance(g1,g3) = 9.2
    c: Equal(g0,g2)
    c: Equal(g1,g3)
    c: Perpendicular(g3,g0)
    c: DistanceY(g-3,g0) = 11.4
    c: Vertical(g2)
    c: Symmetric(g0,g2,g4)
    c: Vertical(g4,g-3)
FEATURE [Part::Extrusion] Extrude087  label="Extrude087 - scavo_led_stato_batteria"
  Base = -> Sketch147
  Dir = (0,-1,2e-16)
  DirMode = 2
  FaceMakerClass = Part::FaceMakerBullseye
  FaceMakerMode = 3
  LengthFwd = 2.2
  LengthRev = 0
  Placement = pos=(0,12.6,0) rot=(0,0,1;0rad)
  Solid = true
  Symmetric = false
FEATURE [Sketcher::SketchObject] Sketch148
  ArcFitTolerance = 1e-06
  AttachmentSupport = -> [Pad016]
  ExternalGeometry = -> [Pad016]
  FullyConstrained = true
  MakeInternals = false
  MapMode = 5
  Placement = pos=(0,0,-80.4316) rot=(1,0,0;3.14159rad)
  sketch-geometry (8):
    g0: LineSegment StartX=-176.685 StartY=3.6 StartZ=0 EndX=-186.685 EndY=3.6 EndZ=0
    g1: LineSegment StartX=-176.685 StartY=3.6 StartZ=0 EndX=-176.685 EndY=-9e-16 EndZ=0
    g2: LineSegment [constr] StartX=-186.685 StartY=3.6 StartZ=0 EndX=-186.685 EndY=-9e-16 EndZ=0
    g3: ArcOfEllipse CenterX=-186.685 CenterY=-9e-16 CenterZ=0 NormalX=0 NormalY=0 NormalZ=1 MajorRadius=10 MinorRadius=3.6 AngleXU=0 StartAngle=0 EndAngle=1.5708
    g4: LineSegment [constr] StartX=-176.685 StartY=-1e-15 StartZ=0 EndX=-196.685 EndY=-1e-15 EndZ=0
    g5: LineSegment [constr] StartX=-186.685 StartY=3.6 StartZ=0 EndX=-186.685 EndY=-3.6 EndZ=0
    g6: GeomPoint [constr] X=-177.356 Y=-1e-15 Z=0
    g7: GeomPoint [constr] X=-196.015 Y=-1e-15 Z=0
  constraints (13):
    c: Distance(g0) = 10
    c: Coincident(g0,g-5)
    c: PointOnObject(g0,g-3)
    c: Coincident(g1,g0)
    c: Coincident(g1,g-5)
    c: Coincident(g2,g0)
    c: Vertical(g2)
    c: PointOnObject(g2,g-4)
    c: InternalAlignment(g4-g7 -> g3) x4
    c: Coincident(g3,g2)
    c: Coincident(g3,g0)
    c: Coincident(g3,g1)
    c: Horizontal(g4)
FEATURE [PartDesign::SubtractivePipe] SubtractivePipe004
  AuxilleryCurvelinear = true
  AuxillerySpineTangent = false
  BaseFeature = -> Pad016
  Binormal = (0,0,0)
  Mode = 0
  Profile = -> Sketch148
  Refine = true
  Spine = -> Pad016 [Edge253]
  SpineTangent = false
  Suppressed = false
  Transformation = 0
  Transition = 0
FEATURE [Sketcher::SketchObject] Sketch149
  ArcFitTolerance = 1e-06
  AttachmentSupport = -> [Pad016]
  ExternalGeometry = -> [Pad016]
  FullyConstrained = true
  MakeInternals = false
  MapMode = 5
  Placement = pos=(0,0,-80.4316) rot=(1,0,0;3.14159rad)
  sketch-geometry (8):
    g0: LineSegment StartX=-215.932 StartY=3.6 StartZ=0 EndX=-205.932 EndY=3.6 EndZ=0
    g1: LineSegment StartX=-215.932 StartY=3.6 StartZ=0 EndX=-215.932 EndY=-4e-16 EndZ=0
    g2: LineSegment [constr] StartX=-205.932 StartY=3.6 StartZ=0 EndX=-205.932 EndY=-9e-16 EndZ=0
    g3: ArcOfEllipse CenterX=-205.932 CenterY=-1e-15 CenterZ=0 NormalX=0 NormalY=0 NormalZ=1 MajorRadius=10 MinorRadius=3.6 AngleXU=-3.14159 StartAngle=4.71239 EndAngle=6.28319
    g4: LineSegment [constr] StartX=-215.932 StartY=-1e-15 StartZ=0 EndX=-195.932 EndY=-1e-15 EndZ=0
    g5: LineSegment [constr] StartX=-205.932 StartY=-3.6 StartZ=0 EndX=-205.932 EndY=3.6 EndZ=0
    g6: GeomPoint [constr] X=-215.262 Y=-2.1e-15 Z=0
    g7: GeomPoint [constr] X=-196.602 Y=-9e-16 Z=0
  constraints (13):
    c: Distance(g0) = 10
    c: Coincident(g0,g-5)
    c: PointOnObject(g0,g-5)
    c: Coincident(g1,g0)
    c: Coincident(g1,g-4)
    c: Coincident(g2,g0)
    c: Vertical(g2)
    c: PointOnObject(g2,g-3)
    c: InternalAlignment(g4-g7 -> g3) x4
    c: Coincident(g3,g2)
    c: Coincident(g3,g0)
    c: Coincident(g3,g1)
    c: Horizontal(g4)
FEATURE [PartDesign::SubtractivePipe] SubtractivePipe005
  AuxilleryCurvelinear = true
  AuxillerySpineTangent = false
  BaseFeature = -> SubtractivePipe004
  Binormal = (0,0,0)
  Mode = 0
  Profile = -> Sketch149
  Refine = true
  Spine = -> Pad016 [Edge251,Edge256,Edge255]
  SpineTangent = false
  Suppressed = false
  Transformation = 0
  Transition = 0
FEATURE [PartDesign::SubtractiveLoft] SubtractiveLoft002
  BaseFeature = -> SubtractivePipe005
  Closed = false
  Profile = -> Sketch129
  Refine = true
  Ruled = false
  Sections = -> [Sketch130]
  Suppressed = false
FEATURE [PartDesign::SubtractiveLoft] SubtractiveLoft003
  BaseFeature = -> SubtractiveLoft002
  Closed = false
  Profile = -> Clone2D001
  Refine = true
  Ruled = false
  Sections = -> [Sketch131]
  Suppressed = false
FEATURE [PartDesign::Chamfer] Chamfer010
  Angle = 45
  Base = -> SubtractiveLoft003 [Edge203,Edge204,Edge202,Edge201,Edge195]
  BaseFeature = -> SubtractiveLoft003
  ChamferType = 0
  FlipDirection = false
  Refine = true
  Size = 1.5
  Size2 = 1
  SupportTransform = false
  Suppressed = false
  UseAllEdges = false
FEATURE [PartDesign::Chamfer] Chamfer011
  Angle = 45
  Base = -> Chamfer010 [Edge15]
  BaseFeature = -> Chamfer010
  ChamferType = 0
  FlipDirection = false
  Refine = true
  Size = 1.6
  Size2 = 1
  SupportTransform = false
  Suppressed = false
  UseAllEdges = false
FEATURE [PartDesign::Chamfer] Chamfer012
  Angle = 45
  Base = -> Chamfer011 [Edge10]
  BaseFeature = -> Chamfer011
  ChamferType = 0
  FlipDirection = false
  Refine = true
  Size = 3.5
  Size2 = 1
  SupportTransform = false
  Suppressed = false
  UseAllEdges = false
FEATURE [PartDesign::Chamfer] Chamfer013
  Angle = 45
  Base = -> Chamfer012 [Edge94]
  BaseFeature = -> Chamfer012
  ChamferType = 0
  FlipDirection = false
  Refine = true
  Size = 1.9
  Size2 = 1
  SupportTransform = false
  Suppressed = false
  UseAllEdges = false
FEATURE [PartDesign::Fillet] Fillet007
  Base = -> Chamfer013 [Edge83]
  BaseFeature = -> Chamfer013
  Radius = 1.1
  Refine = true
  SupportTransform = false
  Suppressed = false
  UseAllEdges = false
FEATURE [PartDesign::Fillet] Fillet008
  Base = -> Fillet007 [Edge75]
  BaseFeature = -> Fillet007
  Radius = 1.9
  Refine = true
  SupportTransform = false
  Suppressed = false
  UseAllEdges = false
FEATURE [PartDesign::Pocket] Pocket011
  BaseFeature = -> Fillet008
  Direction = (0,1,-2e-16)
  Length = 0.8
  Length2 = 5
  Profile = -> Sketch132
  ReferenceAxis = -> Sketch132 [N_Axis]
  Refine = true
  Suppressed = false
  Type = 0
FEATURE [PartDesign::Pocket] Pocket012
  BaseFeature = -> Pocket011
  Direction = (0,1,0)
  Length = 1
  Length2 = 5
  Profile = -> ShapeString
  ReferenceAxis = -> ShapeString [N_Axis]
  Refine = true
  Suppressed = false
  Type = 0
FEATURE [Sketcher::SketchObject] Sketch150
  ArcFitTolerance = 1e-06
  AttachmentSupport = -> [Pad008]
  ExternalGeometry = -> [Pad008]
  FullyConstrained = true
  MakeInternals = false
  MapMode = 5
  Placement = pos=(0,3.6,0) rot=(0,0.707107,0.707107;3.14159rad)
  sketch-geometry (7):
    g0: LineSegment [constr] StartX=210.343 StartY=-66.0316 StartZ=0 EndX=210.343 EndY=-72.8316 EndZ=0
    g1: LineSegment [constr] StartX=210.343 StartY=-72.8316 StartZ=0 EndX=216.543 EndY=-72.8316 EndZ=0
    g2: LineSegment [constr] StartX=216.543 StartY=-72.8316 StartZ=0 EndX=216.543 EndY=-66.0316 EndZ=0
    g3: LineSegment [constr] StartX=216.543 StartY=-66.0316 StartZ=0 EndX=210.343 EndY=-66.0316 EndZ=0
    g4: LineSegment [constr] StartX=210.343 StartY=-72.8316 StartZ=0 EndX=216.543 EndY=-66.0316 EndZ=0
    g5: LineSegment [constr] StartX=210.343 StartY=-66.0316 StartZ=0 EndX=213.443 EndY=-69.4316 EndZ=0
    g6: Circle CenterX=213.443 CenterY=-69.4316 CenterZ=0 NormalX=0 NormalY=0 NormalZ=1 AngleXU=0 Radius=2
  constraints (18):
    c: Coincident(g0,g1)
    c: Coincident(g1,g2)
    c: Coincident(g2,g3)
    c: Coincident(g3,g0)
    c: Vertical(g0)
    c: Vertical(g2)
    c: Horizontal(g1)
    c: Horizontal(g3)
    c: Distance(g0,g2) = 6.2
    c: Distance(g1,g3) = 6.8
    c: DistanceY(g-3,g1) = 4
    c: Coincident(g4,g0)
    c: Coincident(g4,g2)
    c: Coincident(g5,g0)
    c: Symmetric(g0,g2,g5)
    c: Diameter(g6) = 4
    c: Coincident(g6,g5)
    c: Vertical(g5,g-3)
FEATURE [Sketcher::SketchObject] Sketch151
  ArcFitTolerance = 1e-06
  AttachmentSupport = -> [Pad008]
  ExternalGeometry = -> [Pad008]
  FullyConstrained = true
  MakeInternals = false
  MapMode = 5
  Placement = pos=(0,3.6,0) rot=(0,0.707107,0.707107;3.14159rad)
  sketch-geometry (10):
    g0: LineSegment [constr] StartX=211.143 StartY=-56.2316 StartZ=0 EndX=211.143 EndY=-65.4316 EndZ=0
    g1: LineSegment [constr] StartX=211.143 StartY=-65.4316 StartZ=0 EndX=215.743 EndY=-65.4316 EndZ=0
    g2: LineSegment [constr] StartX=215.743 StartY=-65.4316 StartZ=0 EndX=215.743 EndY=-56.2316 EndZ=0
    g3: LineSegment [constr] StartX=215.743 StartY=-56.2316 StartZ=0 EndX=211.143 EndY=-56.2316 EndZ=0
    g4: LineSegment StartX=212.243 StartY=-63.8316 StartZ=0 EndX=214.643 EndY=-63.8316 EndZ=0
    g5: LineSegment StartX=214.643 StartY=-63.8316 StartZ=0 EndX=214.643 EndY=-57.0316 EndZ=0
    g6: LineSegment StartX=214.643 StartY=-57.0316 StartZ=0 EndX=212.243 EndY=-57.0316 EndZ=0
    g7: LineSegment StartX=212.243 StartY=-57.0316 StartZ=0 EndX=212.243 EndY=-63.8316 EndZ=0
    g8: GeomPoint [constr] X=213.443 Y=-60.4316 Z=0
    g9: GeomPoint [constr] X=213.443 Y=-60.8316 Z=0
  constraints (26):
    c: Coincident(g0,g1)
    c: Coincident(g1,g2)
    c: Coincident(g2,g3)
    c: Coincident(g3,g0)
    c: Vertical(g0)
    c: Vertical(g2)
    c: Horizontal(g1)
    c: Horizontal(g3)
    c: Distance(g0,g2) = 4.6
    c: Distance(g1,g3) = 9.2
    c: DistanceY(g-3,g1) = 11.4
    c: Coincident(g4,g5)
    c: Coincident(g5,g6)
    c: Coincident(g6,g7)
    c: Coincident(g7,g4)
    c: Horizontal(g4)
    c: Horizontal(g6)
    c: Vertical(g5)
    c: Vertical(g7)
    c: Symmetric(g6,g4,g8)
    c: Distance(g5,g7) = 2.4
    c: Distance(g4,g6) = 6.8
    c: Symmetric(g2,g0,g9)
    c: Vertical(g8,g9)
    c: DistanceY(g1,g4) = 1.6
    c: Vertical(g9,g-3)
FEATURE [PartDesign::Pocket] Pocket019
  BaseFeature = -> Pocket013
  Direction = (0,-1,2e-16)
  Length = 3.6
  Length2 = 5
  Profile = -> Sketch151
  ReferenceAxis = -> Sketch151 [N_Axis]
  Refine = true
  Suppressed = false
  Type = 0
FEATURE [PartDesign::Pocket] Pocket018
  BaseFeature = -> Pocket019
  Direction = (0,-1,2e-16)
  Length = 3.6
  Length2 = 5
  Profile = -> Sketch150
  ReferenceAxis = -> Sketch150 [N_Axis]
  Refine = true
  Suppressed = false
  Type = 0
FEATURE [PartDesign::Point] DatumPoint
  AttacherType = Attacher::AttachEnginePoint
  AttachmentSupport = -> [Sketch150]
  MapMode = 36
  Placement = pos=(-213.443,3.6,-69.4316) rot=(0,1,0;3.14159rad)
FEATURE [PartDesign::Plane] DatumPlane002
  AttachmentSupport = -> [DatumPoint]
  Length = 260.281
  MapMode = 1
  Placement = pos=(-213.443,3.6,-69.4316) rot=(0,0,1;0rad)
  ResizeMode = 0
  Width = 71.8377
FEATURE [Sketcher::SketchObject] Sketch152
  ArcFitTolerance = 1e-06
  AttachmentSupport = -> [DatumPlane002]
  ExternalGeometry = -> [Sketch150]
  FullyConstrained = true
  MakeInternals = false
  MapMode = 5
  Placement = pos=(-213.443,3.6,-69.4316) rot=(0,0,1;0rad)
  sketch-geometry (7):
    g0: LineSegment StartX=0 StartY=0 StartZ=0 EndX=-4 EndY=5.1e-15 EndZ=0
    g1: ArcOfEllipse CenterX=0 CenterY=0 CenterZ=0 NormalX=0 NormalY=0 NormalZ=1 MajorRadius=4 MinorRadius=3.6 AngleXU=3.14159 StartAngle=2e-16 EndAngle=1.5708
    g2: LineSegment [constr] StartX=-4 StartY=9e-16 StartZ=0 EndX=4 EndY=-9e-16 EndZ=0
    g3: LineSegment [constr] StartX=0 StartY=-3.6 StartZ=0 EndX=0 EndY=3.6 EndZ=0
    g4: GeomPoint [constr] X=-1.74356 Y=2.5e-15 Z=0
    g5: GeomPoint [constr] X=1.74356 Y=-2e-15 Z=0
    g6: LineSegment StartX=0 StartY=0 StartZ=0 EndX=-5.5e-15 EndY=-3.6 EndZ=0
  constraints (11):
    c: PointOnObject(g1,g-2)
    c: Distance(g0) = 4
    c: PointOnObject(g0,g-1)
    c: InternalAlignment(g2-g5 -> g1) x4
    c: Coincident(g1,g0)
    c: Vertical(g3)
    c: Coincident(g1,g-1)
    c: Distance(g6) = 3.6
    c: Coincident(g6,g1)
    c: Coincident(g1,g6)
    c: Coincident(g0,g1)
FEATURE [PartDesign::Groove] Groove
  Angle = 360
  Angle2 = 60
  Axis = (0,1,0)
  Base = (-213.443,3.6,-69.4316)
  BaseFeature = -> Pocket018
  Profile = -> Sketch152
  ReferenceAxis = -> Sketch152 [V_Axis]
  Refine = true
  Reversed = true
  Suppressed = false
  Type = 0
FEATURE [PartDesign::Body] Body006  label="lato SX"
  AllowCompound = false
  Group = -> [Binder,Pad019,Chamfer015,Pocket002,Sketch133,Sketch091,Pad005,Sketch092,Pocket001,Sketch093,Sketch094,Pad006,Sketch095,Pad007,Sketch096,Pad008,Sketch097,Pad009,Chamfer005,Pocket004,Sketch098,Pad010,Chamfer006,Pocket003,SubtractivePipe,SubtractivePipe001,Sketch099,Sketch106,Sketch107,Sketch108,Clone2D,Sketch109,SubtractiveLoft,SubtractiveLoft001,Sketch110,Sketch111,Sketch112,Chamfer016,Chamfer017,+15 more]
  Origin = -> Origin006
  Tip = -> Groove
FEATURE [Sketcher::SketchObject] Sketch153  label="ripieno_per_sostegno_led_batteria"
  ArcFitTolerance = 1e-06
  AttachmentSupport = -> [XZ_Plane]
  ExternalGeometry = -> [Sketch036]
  FullyConstrained = true
  MakeInternals = false
  MapMode = 5
  Placement = pos=(0,0,0) rot=(1,0,0;1.5708rad)
  sketch-geometry (4):
    g0: LineSegment StartX=-217.343 StartY=-54.5944 StartZ=0 EndX=-217.343 EndY=-63.1944 EndZ=0
    g1: LineSegment StartX=-217.343 StartY=-63.1944 StartZ=0 EndX=-211.843 EndY=-63.1944 EndZ=0
    g2: LineSegment StartX=-211.843 StartY=-63.1944 StartZ=0 EndX=-211.843 EndY=-54.5944 EndZ=0
    g3: LineSegment StartX=-211.843 StartY=-54.5944 StartZ=0 EndX=-217.343 EndY=-54.5944 EndZ=0
  constraints (11):
    c: Coincident(g0,g1)
    c: Coincident(g1,g2)
    c: Coincident(g2,g3)
    c: Coincident(g3,g0)
    c: Vertical(g0)
    c: Horizontal(g1)
    c: Horizontal(g3)
    c: Tangent(g2,g-3)
    c: DistanceY(g2,g-3) = 4.5
    c: DistanceX(g3,g3) = 5.5
    c: DistanceY(g0,g0) = 8.6
FEATURE [PartDesign::Body] Body  label="Struttura pistola"
  AllowCompound = false
  Group = -> [Sketch,Sketch002,Sketch004,DatumPlane,Sketch005,DatumPlane001,CopyCut,Sketch008,Sketch009,Sketch010,Sketch011,Sketch012,Sketch013,Sketch014,Sketch015,Sketch016,Sketch017,Sketch018,Sketch019,Sketch020,Sketch022,Sketch023,Sketch024,Sketch025,Sketch026,Sketch027,Sketch029,Sketch030,Sketch031,Sketch032,Sketch033,Sketch034,Sketch035,Sketch036,Sketch037,Sketch038,Sketch039,Sketch040,Sketch041,Sketch042,+28 more]
  Origin = -> Origin
FEATURE [Part::Extrusion] Extrude088  label="Extrude088 - ripieno_per_sostegno_led_batteria"
  Base = -> Sketch153
  Dir = (0,-1,2e-16)
  DirMode = 2
  FaceMakerClass = Part::FaceMakerBullseye
  FaceMakerMode = 3
  LengthFwd = 4
  LengthRev = 0
  Placement = pos=(0,12.6,0) rot=(0,0,1;0rad)
  Solid = true
  Symmetric = false
FEATURE [Part::MultiFuse] Fusion004
  Refine = true
  Shapes = -> [Cut050,Extrude088]
FEATURE [Part::Cut] Cut051
  Base = -> Fusion004
  Refine = true
  Tool = -> Extrude087
FEATURE [Part::Cut] Cut052
  Base = -> Cut051
  Refine = true
  Tool = -> Extrude086
FEATURE [Sketcher::SketchObject] Sketch154
  ArcFitTolerance = 1e-06
  AttachmentSupport = -> [Pad016]
  ExternalGeometry = -> [Binder001]
  FullyConstrained = true
  MakeInternals = false
  MapMode = 5
  Placement = pos=(0,-3.6,0) rot=(1,0,0;1.5708rad)
  sketch-geometry (25):
    g0: LineSegment StartX=-214.643 StartY=-72.4316 StartZ=0 EndX=-212.243 EndY=-72.4316 EndZ=0
    g1: LineSegment StartX=-212.243 StartY=-72.4316 StartZ=0 EndX=-212.243 EndY=-71.2316 EndZ=0
    g2: LineSegment StartX=-212.243 StartY=-71.2316 StartZ=0 EndX=-214.643 EndY=-71.2316 EndZ=0
    g3: LineSegment StartX=-214.643 StartY=-71.2316 StartZ=0 EndX=-214.643 EndY=-72.4316 EndZ=0
    g4: GeomPoint [constr] X=-213.443 Y=-71.8316 Z=0
    g5: LineSegment StartX=-214.643 StartY=-69.6316 StartZ=0 EndX=-212.243 EndY=-69.6316 EndZ=0
    g6: LineSegment StartX=-212.243 StartY=-69.6316 StartZ=0 EndX=-212.243 EndY=-68.4316 EndZ=0
    g7: LineSegment StartX=-212.243 StartY=-68.4316 StartZ=0 EndX=-214.643 EndY=-68.4316 EndZ=0
    g8: LineSegment StartX=-214.643 StartY=-68.4316 StartZ=0 EndX=-214.643 EndY=-69.6316 EndZ=0
    g9: GeomPoint [constr] X=-213.443 Y=-69.0316 Z=0
    g10: LineSegment StartX=-214.643 StartY=-66.8316 StartZ=0 EndX=-212.243 EndY=-66.8316 EndZ=0
    g11: LineSegment StartX=-212.243 StartY=-66.8316 StartZ=0 EndX=-212.243 EndY=-65.6316 EndZ=0
    g12: LineSegment StartX=-212.243 StartY=-65.6316 StartZ=0 EndX=-214.643 EndY=-65.6316 EndZ=0
    g13: LineSegment StartX=-214.643 StartY=-65.6316 StartZ=0 EndX=-214.643 EndY=-66.8316 EndZ=0
    g14: GeomPoint [constr] X=-213.443 Y=-66.2316 Z=0
    g15: LineSegment StartX=-214.643 StartY=-64.0316 StartZ=0 EndX=-212.243 EndY=-64.0316 EndZ=0
    g16: LineSegment StartX=-212.243 StartY=-64.0316 StartZ=0 EndX=-212.243 EndY=-62.8316 EndZ=0
    g17: LineSegment StartX=-212.243 StartY=-62.8316 StartZ=0 EndX=-214.643 EndY=-62.8316 EndZ=0
    g18: LineSegment StartX=-214.643 StartY=-62.8316 StartZ=0 EndX=-214.643 EndY=-64.0316 EndZ=0
    g19: GeomPoint [constr] X=-213.443 Y=-63.4316 Z=0
    g20: LineSegment StartX=-214.643 StartY=-61.2316 StartZ=0 EndX=-212.243 EndY=-61.2316 EndZ=0
    g21: LineSegment StartX=-212.243 StartY=-61.2316 StartZ=0 EndX=-212.243 EndY=-60.0316 EndZ=0
    g22: LineSegment StartX=-212.243 StartY=-60.0316 StartZ=0 EndX=-214.643 EndY=-60.0316 EndZ=0
    g23: LineSegment StartX=-214.643 StartY=-60.0316 StartZ=0 EndX=-214.643 EndY=-61.2316 EndZ=0
    g24: GeomPoint [constr] X=-213.443 Y=-60.6316 Z=0
  constraints (65):
    c: Coincident(g0,g1)
    c: Coincident(g1,g2)
    c: Coincident(g2,g3)
    c: Coincident(g3,g0)
    c: Horizontal(g0)
    c: Horizontal(g2)
    c: Vertical(g1)
    c: Vertical(g3)
    c: Symmetric(g2,g0,g4)
    c: Distance(g1,g3) = 2.4
    c: Distance(g0,g2) = 1.2
    c: Coincident(g5,g6)
    c: Coincident(g6,g7)
    c: Coincident(g7,g8)
    c: Coincident(g8,g5)
    c: Horizontal(g5)
    c: Horizontal(g7)
    c: Vertical(g6)
    c: Vertical(g8)
    c: Symmetric(g7,g5,g9)
    c: Distance(g6,g8) = 2.4
    c: Distance(g5,g7) = 1.2
    c: Coincident(g10,g11)
    c: Coincident(g11,g12)
    c: Coincident(g12,g13)
    c: Coincident(g13,g10)
    c: Horizontal(g10)
    c: Horizontal(g12)
    c: Vertical(g11)
    c: Vertical(g13)
    c: Symmetric(g12,g10,g14)
    c: Distance(g11,g13) = 2.4
    c: Distance(g10,g12) = 1.2
    c: Coincident(g15,g16)
    c: Coincident(g16,g17)
    c: Coincident(g17,g18)
    c: Coincident(g18,g15)
    c: Horizontal(g15)
    c: Horizontal(g17)
    c: Vertical(g16)
    c: Vertical(g18)
    c: Symmetric(g17,g15,g19)
    c: Distance(g16,g18) = 2.4
    c: Distance(g15,g17) = 1.2
    c: Vertical(g4,g-3)
    c: Vertical(g9,g-3)
    c: Vertical(g14,g-3)
    c: Vertical(g19,g-3)
    c: DistanceY(g-3,g4) = 5
    c: DistanceY(g4,g9) = 2.8
    c: DistanceY(g9,g14) = 2.8
    c: DistanceY(g14,g19) = 2.8
    c: Coincident(g20,g21)
    c: Coincident(g21,g22)
    c: Coincident(g22,g23)
    c: Coincident(g23,g20)
    c: Horizontal(g20)
    c: Horizontal(g22)
    c: Vertical(g21)
    c: Vertical(g23)
    c: Symmetric(g22,g20,g24)
    c: Distance(g21,g23) = 2.4
    c: Distance(g20,g22) = 1.2
    c: DistanceY(g19,g24) = 2.8
    c: Vertical(g-3,g24)
FEATURE [PartDesign::Pocket] Pocket020
  BaseFeature = -> Pocket012
  Direction = (0,1,-2e-16)
  Length = 3.6
  Length2 = 5
  Profile = -> Sketch154
  ReferenceAxis = -> Sketch154 [N_Axis]
  Refine = true
  Suppressed = false
  Type = 0
FEATURE [PartDesign::Body] Body007  label="lato DX"
  AllowCompound = false
  Group = -> [Binder001,Sketch114,Pad011,Chamfer014,Sketch115,Pocket006,Sketch116,Pad012,Sketch117,Pocket007,Sketch118,Pad013,Sketch119,Pocket008,Pad017,Chamfer009,Pocket009,Sketch123,Sketch120,Pad014,Pad018,Chamfer008,Pocket010,Sketch121,Pad015,Sketch122,Pad016,SubtractivePipe004,SubtractivePipe005,Sketch149,Sketch148,Sketch124,Sketch125,Sketch126,Sketch129,Sketch130,Clone2D001,Sketch131,SubtractiveLoft002,+13 more]
  Origin = -> Origin007
  Tip = -> Pocket020
note: 2 file-system paths scrubbed to <path> (originals preserved in the JSON sidecar)
